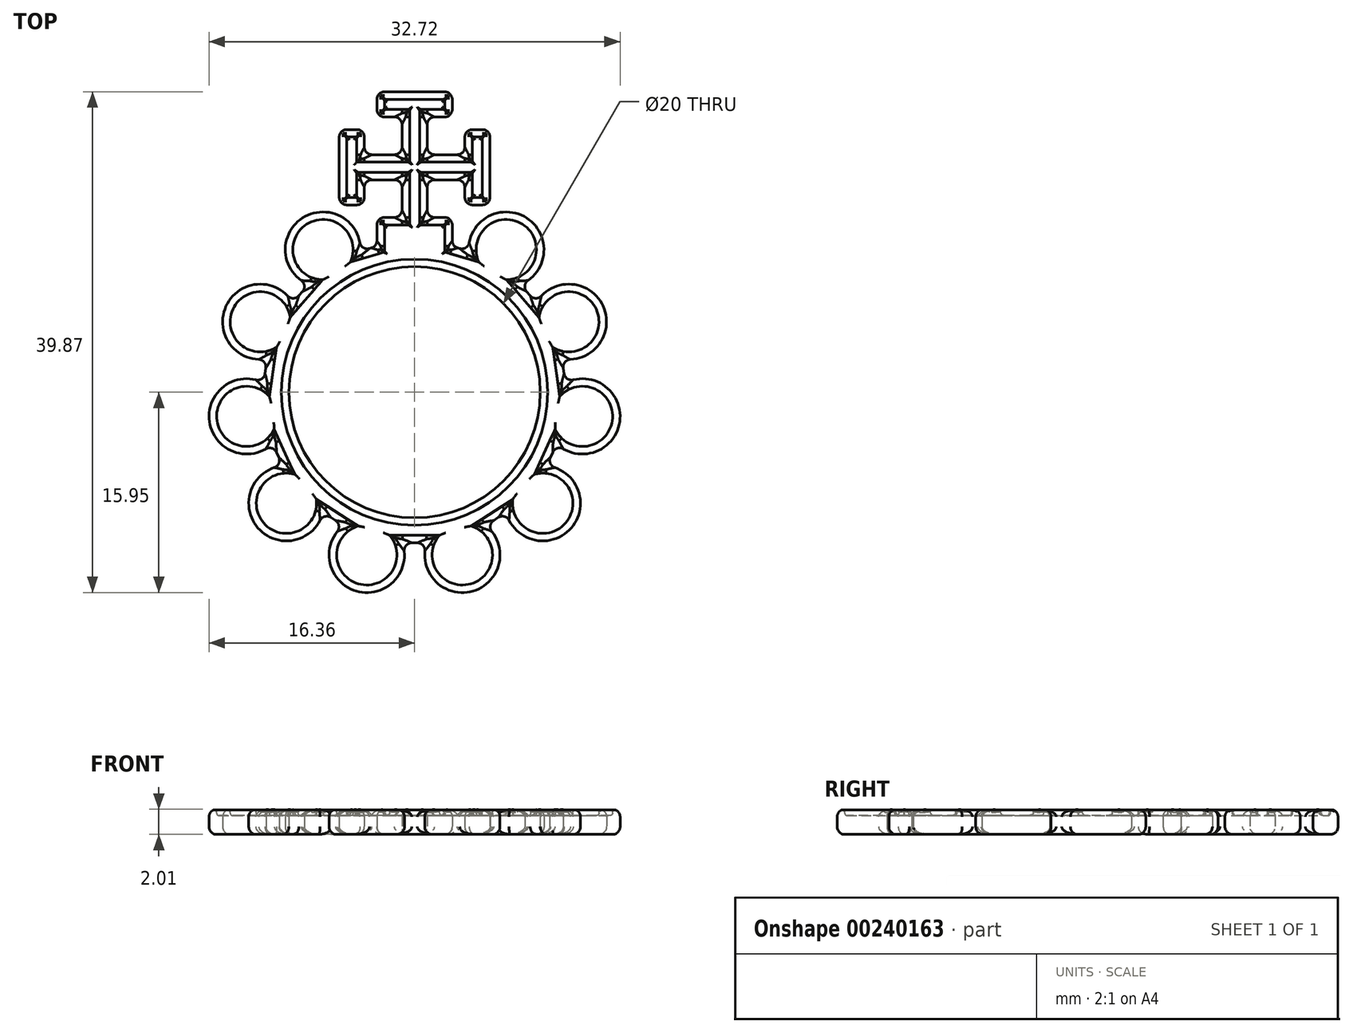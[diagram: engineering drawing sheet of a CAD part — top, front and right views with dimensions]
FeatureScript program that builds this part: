
annotation { "Feature Type Name" : "Feature", "Feature Type Description" : "" }
export const myFeature = defineFeature(function(context is Context, id is Id, definition is map)
    precondition{}
    {
        {
            var Q0;
            Q0=qCreatedBy(makeId("Top.planeOp"),FACE);
            var sketch = newSketch(context, id + "F0", { "sketchPlane" : qUnion([Q0])});
            skCircle(sketch, "E0", {"center": v(0, 0) * mm, "radius": 10 * mm});
            skLineSegment(sketch, "E1.0", {"start": v(3, 11.62) * mm, "end": v(4.3, 11.24) * mm});
            skLineSegment(sketch, "E1.1", {"start": v(8.43, 8.58) * mm, "end": v(9.7, 7.13) * mm});
            skLineSegment(sketch, "E1.2", {"start": v(11.73, 2.66) * mm, "end": v(12, 0.76) * mm});
            skLineSegment(sketch, "E1.3", {"start": v(11.3, -4.1) * mm, "end": v(10.51, -5.86) * mm});
            skLineSegment(sketch, "E1.4", {"start": v(7.3, -9.57) * mm, "end": v(5.68, -10.6) * mm});
            skLineSegment(sketch, "E1.5", {"start": v(0.96, -12) * mm, "end": v(-0.96, -12) * mm});
            skLineSegment(sketch, "E1.6", {"start": v(-5.68, -10.6) * mm, "end": v(-7.3, -9.57) * mm});
            skLineSegment(sketch, "E1.7", {"start": v(-10.51, -5.86) * mm, "end": v(-11.3, -4.1) * mm});
            skLineSegment(sketch, "E1.8", {"start": v(-12, 0.76) * mm, "end": v(-11.73, 2.66) * mm});
            skLineSegment(sketch, "E1.9", {"start": v(-9.7, 7.13) * mm, "end": v(-8.43, 8.58) * mm});
            skLineSegment(sketch, "E1.10", {"start": v(-4.3, 11.24) * mm, "end": v(-3, 11.62) * mm});
            skArc(sketch, "E2", {"start": v(8.43, 8.58) * mm, "mid": v(8.92, 13.88) * mm, "end": v(4.3, 11.24) * mm});
            skArc(sketch, "E3.2.0", {"start": v(-4.3, 11.24) * mm, "mid": v(-8.92, 13.88) * mm, "end": v(-8.43, 8.58) * mm});
            skArc(sketch, "E3.3.0", {"start": v(-9.7, 7.13) * mm, "mid": v(-15, 6.85) * mm, "end": v(-11.73, 2.66) * mm});
            skArc(sketch, "E3.4.0", {"start": v(-12, 0.76) * mm, "mid": v(-16.33, -2.35) * mm, "end": v(-11.3, -4.1) * mm});
            skArc(sketch, "E3.5.0", {"start": v(-10.51, -5.86) * mm, "mid": v(-12.47, -10.8) * mm, "end": v(-7.3, -9.57) * mm});
            skArc(sketch, "E3.6.0", {"start": v(-5.68, -10.6) * mm, "mid": v(-4.65, -15.83) * mm, "end": v(-0.96, -12) * mm});
            skArc(sketch, "E3.7.0", {"start": v(0.96, -12) * mm, "mid": v(4.65, -15.83) * mm, "end": v(5.68, -10.6) * mm});
            skArc(sketch, "E3.8.0", {"start": v(7.3, -9.57) * mm, "mid": v(12.47, -10.8) * mm, "end": v(10.51, -5.86) * mm});
            skArc(sketch, "E3.9.0", {"start": v(11.3, -4.1) * mm, "mid": v(16.33, -2.35) * mm, "end": v(12, 0.76) * mm});
            skArc(sketch, "E3.10.0", {"start": v(11.73, 2.66) * mm, "mid": v(15, 6.85) * mm, "end": v(9.7, 7.13) * mm});
            skLineSegment(sketch, "E4", {"start": v(3, 11.62) * mm, "end": v(3, 13.92) * mm});
            skLineSegment(sketch, "E5", {"start": v(3, 13.92) * mm, "end": v(1, 13.92) * mm});
            skLineSegment(sketch, "E6", {"start": v(1, 13.92) * mm, "end": v(1, 16.92) * mm});
            skLineSegment(sketch, "E7", {"start": v(1, 16.92) * mm, "end": v(4, 16.92) * mm});
            skLineSegment(sketch, "E8", {"start": v(4, 16.92) * mm, "end": v(4, 14.92) * mm});
            skLineSegment(sketch, "E9", {"start": v(4, 14.92) * mm, "end": v(6, 14.92) * mm});
            skLineSegment(sketch, "E10", {"start": v(6, 14.92) * mm, "end": v(6, 20.92) * mm});
            skLineSegment(sketch, "E11", {"start": v(6, 20.92) * mm, "end": v(4, 20.92) * mm});
            skLineSegment(sketch, "E12", {"start": v(4, 20.92) * mm, "end": v(4, 18.92) * mm});
            skLineSegment(sketch, "E13", {"start": v(4, 18.92) * mm, "end": v(1, 18.92) * mm});
            skLineSegment(sketch, "E14", {"start": v(1, 18.92) * mm, "end": v(1, 21.92) * mm});
            skLineSegment(sketch, "E15", {"start": v(1, 21.92) * mm, "end": v(3, 21.92) * mm});
            skLineSegment(sketch, "E16", {"start": v(3, 21.92) * mm, "end": v(3, 23.92) * mm});
            skLineSegment(sketch, "E17", {"start": v(3, 23.92) * mm, "end": v(0, 23.92) * mm});
            skLineSegment(sketch, "E18.MirrorCS", {"start": v(-3, 23.92) * mm, "end": v(0, 23.92) * mm});
            skLineSegment(sketch, "E19.MirrorCS", {"start": v(-3, 21.92) * mm, "end": v(-3, 23.92) * mm});
            skLineSegment(sketch, "E20.MirrorCS", {"start": v(-1, 21.92) * mm, "end": v(-3, 21.92) * mm});
            skLineSegment(sketch, "E21.MirrorCS", {"start": v(-1, 18.92) * mm, "end": v(-1, 21.92) * mm});
            skLineSegment(sketch, "E22.MirrorCS", {"start": v(-4, 18.92) * mm, "end": v(-1, 18.92) * mm});
            skLineSegment(sketch, "E23.MirrorCS", {"start": v(-4, 20.92) * mm, "end": v(-4, 18.92) * mm});
            skLineSegment(sketch, "E24.MirrorCS", {"start": v(-6, 20.92) * mm, "end": v(-4, 20.92) * mm});
            skLineSegment(sketch, "E25.MirrorCS", {"start": v(-6, 14.92) * mm, "end": v(-6, 20.92) * mm});
            skLineSegment(sketch, "E26.MirrorCS", {"start": v(-1, 16.92) * mm, "end": v(-4, 16.92) * mm});
            skLineSegment(sketch, "E27.MirrorCS", {"start": v(-4, 16.92) * mm, "end": v(-4, 14.92) * mm});
            skLineSegment(sketch, "E28.MirrorCS", {"start": v(-1, 13.92) * mm, "end": v(-1, 16.92) * mm});
            skLineSegment(sketch, "E29.MirrorCS", {"start": v(-4, 14.92) * mm, "end": v(-6, 14.92) * mm});
            skLineSegment(sketch, "E30.MirrorCS", {"start": v(-3, 13.92) * mm, "end": v(-1, 13.92) * mm});
            skLineSegment(sketch, "E31.MirrorCS", {"start": v(-3, 11.62) * mm, "end": v(-3, 13.92) * mm});
            skPoint(sketch, "E32.orphan", {"position": v(-3, 11.92) * mm});
            skPoint(sketch, "E33.MirrorCS.start.orphan", {"position": v(0, 12.5) * mm});
            skPoint(sketch, "E34.end.orphan", {"position": v(3, 11.92) * mm});
            skSolve(sketch);
        }
        {
            var Q0;
            Q0=qSketchRegion(id+"F0",true);
            extrude(context, id + "F1", {"entities" : qUnion([Q0]), "depth" : 2 * mm});
        }
        {
            var Q0;
            Q0=makeQuery(id+"F1.opExtrude","CAP_EDGE",EDGE,{"disambiguationData":[OSD([sQuery(id+"F0.wireOp",EDGE,"E0")])],"isStart":false});
            var Q1;
            Q1=makeQuery(id+"F1.opExtrude","CAP_EDGE",EDGE,{"disambiguationData":[OSD([sQuery(id+"F0.wireOp",EDGE,"E0")])],"isStart":true});
            var Q2;
            Q2=makeQuery(id+"F1.opExtrude","CAP_EDGE",EDGE,{"disambiguationData":[OSD([sQuery(id+"F0.wireOp",EDGE,"E2")])],"isStart":false});
            var Q3;
            Q3=makeQuery(id+"F1.opExtrude","CAP_EDGE",EDGE,{"disambiguationData":[OSD([sQuery(id+"F0.wireOp",EDGE,"E3.10.0")])],"isStart":false});
            var Q4;
            Q4=makeQuery(id+"F1.opExtrude","CAP_EDGE",EDGE,{"disambiguationData":[OSD([sQuery(id+"F0.wireOp",EDGE,"E1.1")])],"isStart":false});
            var Q5;
            Q5=makeQuery(id+"F1.opExtrude","CAP_EDGE",EDGE,{"disambiguationData":[OSD([sQuery(id+"F0.wireOp",EDGE,"E1.2")])],"isStart":false});
            var Q6;
            Q6=makeQuery(id+"F1.opExtrude","CAP_EDGE",EDGE,{"disambiguationData":[OSD([sQuery(id+"F0.wireOp",EDGE,"E3.9.0")])],"isStart":false});
            var Q7;
            Q7=makeQuery(id+"F1.opExtrude","CAP_EDGE",EDGE,{"disambiguationData":[OSD([sQuery(id+"F0.wireOp",EDGE,"E3.8.0")])],"isStart":false});
            var Q8;
            Q8=makeQuery(id+"F1.opExtrude","CAP_EDGE",EDGE,{"disambiguationData":[OSD([sQuery(id+"F0.wireOp",EDGE,"E1.3")])],"isStart":false});
            var Q9;
            Q9=makeQuery(id+"F1.opExtrude","CAP_EDGE",EDGE,{"disambiguationData":[OSD([sQuery(id+"F0.wireOp",EDGE,"E3.7.0")])],"isStart":false});
            var Q10;
            Q10=makeQuery(id+"F1.opExtrude","CAP_EDGE",EDGE,{"disambiguationData":[OSD([sQuery(id+"F0.wireOp",EDGE,"E1.4")])],"isStart":false});
            var Q11;
            Q11=makeQuery(id+"F1.opExtrude","CAP_EDGE",EDGE,{"disambiguationData":[OSD([sQuery(id+"F0.wireOp",EDGE,"E3.6.0")])],"isStart":false});
            var Q12;
            Q12=makeQuery(id+"F1.opExtrude","CAP_EDGE",EDGE,{"disambiguationData":[OSD([sQuery(id+"F0.wireOp",EDGE,"E1.5")])],"isStart":false});
            var Q13;
            Q13=makeQuery(id+"F1.opExtrude","CAP_EDGE",EDGE,{"disambiguationData":[OSD([sQuery(id+"F0.wireOp",EDGE,"E3.5.0")])],"isStart":false});
            var Q14;
            Q14=makeQuery(id+"F1.opExtrude","CAP_EDGE",EDGE,{"disambiguationData":[OSD([sQuery(id+"F0.wireOp",EDGE,"E1.6")])],"isStart":false});
            var Q15;
            Q15=makeQuery(id+"F1.opExtrude","CAP_EDGE",EDGE,{"disambiguationData":[OSD([sQuery(id+"F0.wireOp",EDGE,"E3.4.0")])],"isStart":false});
            var Q16;
            Q16=makeQuery(id+"F1.opExtrude","CAP_EDGE",EDGE,{"disambiguationData":[OSD([sQuery(id+"F0.wireOp",EDGE,"E3.3.0")])],"isStart":false});
            var Q17;
            Q17=makeQuery(id+"F1.opExtrude","CAP_EDGE",EDGE,{"disambiguationData":[OSD([sQuery(id+"F0.wireOp",EDGE,"E3.2.0")])],"isStart":false});
            var Q18;
            Q18=makeQuery(id+"F1.opExtrude","CAP_EDGE",EDGE,{"disambiguationData":[OSD([sQuery(id+"F0.wireOp",EDGE,"E1.9")])],"isStart":false});
            var Q19;
            Q19=makeQuery(id+"F1.opExtrude","CAP_EDGE",EDGE,{"disambiguationData":[OSD([sQuery(id+"F0.wireOp",EDGE,"E1.8")])],"isStart":false});
            var Q20;
            Q20=makeQuery(id+"F1.opExtrude","CAP_EDGE",EDGE,{"disambiguationData":[OSD([sQuery(id+"F0.wireOp",EDGE,"E1.7")])],"isStart":false});
            var Q21;
            Q21=makeQuery(id+"F1.opExtrude","CAP_EDGE",EDGE,{"disambiguationData":[OSD([sQuery(id+"F0.wireOp",EDGE,"E1.10")])],"isStart":false});
            var Q22;
            Q22=makeQuery(id+"F1.opExtrude","CAP_EDGE",EDGE,{"disambiguationData":[OSD([sQuery(id+"F0.wireOp",EDGE,"E31.MirrorCS")])],"isStart":false});
            var Q23;
            Q23=makeQuery(id+"F1.opExtrude","CAP_EDGE",EDGE,{"disambiguationData":[OSD([sQuery(id+"F0.wireOp",EDGE,"E30.MirrorCS")])],"isStart":false});
            var Q24;
            Q24=makeQuery(id+"F1.opExtrude","CAP_EDGE",EDGE,{"disambiguationData":[OSD([sQuery(id+"F0.wireOp",EDGE,"E28.MirrorCS")])],"isStart":false});
            var Q25;
            Q25=makeQuery(id+"F1.opExtrude","CAP_EDGE",EDGE,{"disambiguationData":[OSD([sQuery(id+"F0.wireOp",EDGE,"E26.MirrorCS")])],"isStart":false});
            var Q26;
            Q26=makeQuery(id+"F1.opExtrude","CAP_EDGE",EDGE,{"disambiguationData":[OSD([sQuery(id+"F0.wireOp",EDGE,"E26.MirrorCS")])],"isStart":true});
            var Q27;
            Q27=makeQuery(id+"F1.opExtrude","CAP_EDGE",EDGE,{"disambiguationData":[OSD([sQuery(id+"F0.wireOp",EDGE,"E29.MirrorCS")])],"isStart":false});
            var Q28;
            Q28=makeQuery(id+"F1.opExtrude","CAP_EDGE",EDGE,{"disambiguationData":[OSD([sQuery(id+"F0.wireOp",EDGE,"E25.MirrorCS")])],"isStart":false});
            var Q29;
            Q29=makeQuery(id+"F1.opExtrude","CAP_EDGE",EDGE,{"disambiguationData":[OSD([sQuery(id+"F0.wireOp",EDGE,"E24.MirrorCS")])],"isStart":false});
            var Q30;
            Q30=makeQuery(id+"F1.opExtrude","CAP_EDGE",EDGE,{"disambiguationData":[OSD([sQuery(id+"F0.wireOp",EDGE,"E22.MirrorCS")])],"isStart":false});
            var Q31;
            Q31=makeQuery(id+"F1.opExtrude","CAP_EDGE",EDGE,{"disambiguationData":[OSD([sQuery(id+"F0.wireOp",EDGE,"E21.MirrorCS")])],"isStart":false});
            var Q32;
            Q32=makeQuery(id+"F1.opExtrude","CAP_EDGE",EDGE,{"disambiguationData":[OSD([sQuery(id+"F0.wireOp",EDGE,"E20.MirrorCS")])],"isStart":false});
            var Q33;
            Q33=makeQuery(id+"F1.opExtrude","CAP_EDGE",EDGE,{"disambiguationData":[OSD([sQuery(id+"F0.wireOp",EDGE,"E19.MirrorCS")])],"isStart":false});
            var Q34;
            Q34=makeQuery(id+"F1.opExtrude","CAP_EDGE",EDGE,{"disambiguationData":[OSD([sQuery(id+"F0.wireOp",EDGE,"E17"),sQuery(id+"F0.wireOp",EDGE,"E18.MirrorCS")])],"isStart":false});
            var Q35;
            Q35=makeQuery(id+"F1.opExtrude","CAP_EDGE",EDGE,{"disambiguationData":[OSD([sQuery(id+"F0.wireOp",EDGE,"E16")])],"isStart":false});
            var Q36;
            Q36=makeQuery(id+"F1.opExtrude","CAP_EDGE",EDGE,{"disambiguationData":[OSD([sQuery(id+"F0.wireOp",EDGE,"E15")])],"isStart":false});
            var Q37;
            Q37=makeQuery(id+"F1.opExtrude","CAP_EDGE",EDGE,{"disambiguationData":[OSD([sQuery(id+"F0.wireOp",EDGE,"E14")])],"isStart":false});
            var Q38;
            Q38=makeQuery(id+"F1.opExtrude","CAP_EDGE",EDGE,{"disambiguationData":[OSD([sQuery(id+"F0.wireOp",EDGE,"E13")])],"isStart":false});
            var Q39;
            Q39=makeQuery(id+"F1.opExtrude","CAP_EDGE",EDGE,{"disambiguationData":[OSD([sQuery(id+"F0.wireOp",EDGE,"E11")])],"isStart":false});
            var Q40;
            Q40=makeQuery(id+"F1.opExtrude","CAP_EDGE",EDGE,{"disambiguationData":[OSD([sQuery(id+"F0.wireOp",EDGE,"E12")])],"isStart":false});
            var Q41;
            Q41=makeQuery(id+"F1.opExtrude","CAP_EDGE",EDGE,{"disambiguationData":[OSD([sQuery(id+"F0.wireOp",EDGE,"E10")])],"isStart":false});
            var Q42;
            Q42=makeQuery(id+"F1.opExtrude","CAP_EDGE",EDGE,{"disambiguationData":[OSD([sQuery(id+"F0.wireOp",EDGE,"E9")])],"isStart":false});
            var Q43;
            Q43=makeQuery(id+"F1.opExtrude","CAP_EDGE",EDGE,{"disambiguationData":[OSD([sQuery(id+"F0.wireOp",EDGE,"E8")])],"isStart":false});
            var Q44;
            Q44=makeQuery(id+"F1.opExtrude","CAP_EDGE",EDGE,{"disambiguationData":[OSD([sQuery(id+"F0.wireOp",EDGE,"E7")])],"isStart":false});
            var Q45;
            Q45=makeQuery(id+"F1.opExtrude","CAP_EDGE",EDGE,{"disambiguationData":[OSD([sQuery(id+"F0.wireOp",EDGE,"E6")])],"isStart":false});
            var Q46;
            Q46=makeQuery(id+"F1.opExtrude","CAP_EDGE",EDGE,{"disambiguationData":[OSD([sQuery(id+"F0.wireOp",EDGE,"E5")])],"isStart":false});
            var Q47;
            Q47=makeQuery(id+"F1.opExtrude","CAP_EDGE",EDGE,{"disambiguationData":[OSD([sQuery(id+"F0.wireOp",EDGE,"E4")])],"isStart":false});
            var Q48;
            Q48=makeQuery(id+"F1.opExtrude","CAP_EDGE",EDGE,{"disambiguationData":[OSD([sQuery(id+"F0.wireOp",EDGE,"E1.0")])],"isStart":false});
            var Q49;
            Q49=makeQuery(id+"F1.opExtrude","CAP_EDGE",EDGE,{"disambiguationData":[OSD([sQuery(id+"F0.wireOp",EDGE,"E3.5.0")])],"isStart":true});
            var Q50;
            Q50=makeQuery(id+"F1.opExtrude","CAP_EDGE",EDGE,{"disambiguationData":[OSD([sQuery(id+"F0.wireOp",EDGE,"E1.6")])],"isStart":true});
            var Q51;
            Q51=makeQuery(id+"F1.opExtrude","CAP_EDGE",EDGE,{"disambiguationData":[OSD([sQuery(id+"F0.wireOp",EDGE,"E3.6.0")])],"isStart":true});
            var Q52;
            Q52=makeQuery(id+"F1.opExtrude","CAP_EDGE",EDGE,{"disambiguationData":[OSD([sQuery(id+"F0.wireOp",EDGE,"E1.5")])],"isStart":true});
            var Q53;
            Q53=makeQuery(id+"F1.opExtrude","CAP_EDGE",EDGE,{"disambiguationData":[OSD([sQuery(id+"F0.wireOp",EDGE,"E3.7.0")])],"isStart":true});
            var Q54;
            Q54=makeQuery(id+"F1.opExtrude","CAP_EDGE",EDGE,{"disambiguationData":[OSD([sQuery(id+"F0.wireOp",EDGE,"E3.4.0")])],"isStart":true});
            var Q55;
            Q55=makeQuery(id+"F1.opExtrude","CAP_EDGE",EDGE,{"disambiguationData":[OSD([sQuery(id+"F0.wireOp",EDGE,"E1.7")])],"isStart":true});
            var Q56;
            Q56=makeQuery(id+"F1.opExtrude","CAP_EDGE",EDGE,{"disambiguationData":[OSD([sQuery(id+"F0.wireOp",EDGE,"E3.3.0")])],"isStart":true});
            var Q57;
            Q57=makeQuery(id+"F1.opExtrude","CAP_EDGE",EDGE,{"disambiguationData":[OSD([sQuery(id+"F0.wireOp",EDGE,"E1.8")])],"isStart":true});
            var Q58;
            Q58=makeQuery(id+"F1.opExtrude","CAP_EDGE",EDGE,{"disambiguationData":[OSD([sQuery(id+"F0.wireOp",EDGE,"E3.2.0")])],"isStart":true});
            var Q59;
            Q59=makeQuery(id+"F1.opExtrude","CAP_EDGE",EDGE,{"disambiguationData":[OSD([sQuery(id+"F0.wireOp",EDGE,"E1.9")])],"isStart":true});
            var Q60;
            Q60=makeQuery(id+"F1.opExtrude","CAP_EDGE",EDGE,{"disambiguationData":[OSD([sQuery(id+"F0.wireOp",EDGE,"E1.10")])],"isStart":true});
            var Q61;
            Q61=makeQuery(id+"F1.opExtrude","CAP_EDGE",EDGE,{"disambiguationData":[OSD([sQuery(id+"F0.wireOp",EDGE,"E31.MirrorCS")])],"isStart":true});
            var Q62;
            Q62=makeQuery(id+"F1.opExtrude","CAP_EDGE",EDGE,{"disambiguationData":[OSD([sQuery(id+"F0.wireOp",EDGE,"E25.MirrorCS")])],"isStart":true});
            var Q63;
            Q63=makeQuery(id+"F1.opExtrude","CAP_EDGE",EDGE,{"disambiguationData":[OSD([sQuery(id+"F0.wireOp",EDGE,"E29.MirrorCS")])],"isStart":true});
            var Q64;
            Q64=makeQuery(id+"F1.opExtrude","CAP_EDGE",EDGE,{"disambiguationData":[OSD([sQuery(id+"F0.wireOp",EDGE,"E30.MirrorCS")])],"isStart":true});
            var Q65;
            Q65=makeQuery(id+"F1.opExtrude","CAP_EDGE",EDGE,{"disambiguationData":[OSD([sQuery(id+"F0.wireOp",EDGE,"E28.MirrorCS")])],"isStart":true});
            var Q66;
            Q66=makeQuery(id+"F1.opExtrude","CAP_EDGE",EDGE,{"disambiguationData":[OSD([sQuery(id+"F0.wireOp",EDGE,"E6")])],"isStart":true});
            var Q67;
            Q67=makeQuery(id+"F1.opExtrude","CAP_EDGE",EDGE,{"disambiguationData":[OSD([sQuery(id+"F0.wireOp",EDGE,"E5")])],"isStart":true});
            var Q68;
            Q68=makeQuery(id+"F1.opExtrude","CAP_EDGE",EDGE,{"disambiguationData":[OSD([sQuery(id+"F0.wireOp",EDGE,"E4")])],"isStart":true});
            var Q69;
            Q69=makeQuery(id+"F1.opExtrude","CAP_EDGE",EDGE,{"disambiguationData":[OSD([sQuery(id+"F0.wireOp",EDGE,"E1.0")])],"isStart":true});
            var Q70;
            Q70=makeQuery(id+"F1.opExtrude","CAP_EDGE",EDGE,{"disambiguationData":[OSD([sQuery(id+"F0.wireOp",EDGE,"E2")])],"isStart":true});
            var Q71;
            Q71=makeQuery(id+"F1.opExtrude","CAP_EDGE",EDGE,{"disambiguationData":[OSD([sQuery(id+"F0.wireOp",EDGE,"E7")])],"isStart":true});
            var Q72;
            Q72=makeQuery(id+"F1.opExtrude","CAP_EDGE",EDGE,{"disambiguationData":[OSD([sQuery(id+"F0.wireOp",EDGE,"E8")])],"isStart":true});
            var Q73;
            Q73=makeQuery(id+"F1.opExtrude","CAP_EDGE",EDGE,{"disambiguationData":[OSD([sQuery(id+"F0.wireOp",EDGE,"E9")])],"isStart":true});
            var Q74;
            Q74=makeQuery(id+"F1.opExtrude","CAP_EDGE",EDGE,{"disambiguationData":[OSD([sQuery(id+"F0.wireOp",EDGE,"E10")])],"isStart":true});
            var Q75;
            Q75=makeQuery(id+"F1.opExtrude","CAP_EDGE",EDGE,{"disambiguationData":[OSD([sQuery(id+"F0.wireOp",EDGE,"E11")])],"isStart":true});
            var Q76;
            Q76=makeQuery(id+"F1.opExtrude","CAP_EDGE",EDGE,{"disambiguationData":[OSD([sQuery(id+"F0.wireOp",EDGE,"E12")])],"isStart":true});
            var Q77;
            Q77=makeQuery(id+"F1.opExtrude","CAP_EDGE",EDGE,{"disambiguationData":[OSD([sQuery(id+"F0.wireOp",EDGE,"E13")])],"isStart":true});
            var Q78;
            Q78=makeQuery(id+"F1.opExtrude","CAP_EDGE",EDGE,{"disambiguationData":[OSD([sQuery(id+"F0.wireOp",EDGE,"E14")])],"isStart":true});
            var Q79;
            Q79=makeQuery(id+"F1.opExtrude","CAP_EDGE",EDGE,{"disambiguationData":[OSD([sQuery(id+"F0.wireOp",EDGE,"E15")])],"isStart":true});
            var Q80;
            Q80=makeQuery(id+"F1.opExtrude","CAP_EDGE",EDGE,{"disambiguationData":[OSD([sQuery(id+"F0.wireOp",EDGE,"E16")])],"isStart":true});
            var Q81;
            Q81=makeQuery(id+"F1.opExtrude","CAP_EDGE",EDGE,{"disambiguationData":[OSD([sQuery(id+"F0.wireOp",EDGE,"E17"),sQuery(id+"F0.wireOp",EDGE,"E18.MirrorCS")])],"isStart":true});
            var Q82;
            Q82=makeQuery(id+"F1.opExtrude","CAP_EDGE",EDGE,{"disambiguationData":[OSD([sQuery(id+"F0.wireOp",EDGE,"E19.MirrorCS")])],"isStart":true});
            var Q83;
            Q83=makeQuery(id+"F1.opExtrude","CAP_EDGE",EDGE,{"disambiguationData":[OSD([sQuery(id+"F0.wireOp",EDGE,"E20.MirrorCS")])],"isStart":true});
            var Q84;
            Q84=makeQuery(id+"F1.opExtrude","CAP_EDGE",EDGE,{"disambiguationData":[OSD([sQuery(id+"F0.wireOp",EDGE,"E21.MirrorCS")])],"isStart":true});
            var Q85;
            Q85=makeQuery(id+"F1.opExtrude","CAP_EDGE",EDGE,{"disambiguationData":[OSD([sQuery(id+"F0.wireOp",EDGE,"E22.MirrorCS")])],"isStart":true});
            var Q86;
            Q86=makeQuery(id+"F1.opExtrude","CAP_EDGE",EDGE,{"disambiguationData":[OSD([sQuery(id+"F0.wireOp",EDGE,"E23.MirrorCS")])],"isStart":true});
            var Q87;
            Q87=makeQuery(id+"F1.opExtrude","CAP_EDGE",EDGE,{"disambiguationData":[OSD([sQuery(id+"F0.wireOp",EDGE,"E24.MirrorCS")])],"isStart":true});
            var Q88;
            Q88=makeQuery(id+"F1.opExtrude","CAP_EDGE",EDGE,{"disambiguationData":[OSD([sQuery(id+"F0.wireOp",EDGE,"E3.10.0")])],"isStart":true});
            var Q89;
            Q89=makeQuery(id+"F1.opExtrude","CAP_EDGE",EDGE,{"disambiguationData":[OSD([sQuery(id+"F0.wireOp",EDGE,"E1.1")])],"isStart":true});
            var Q90;
            Q90=makeQuery(id+"F1.opExtrude","CAP_EDGE",EDGE,{"disambiguationData":[OSD([sQuery(id+"F0.wireOp",EDGE,"E1.2")])],"isStart":true});
            var Q91;
            Q91=makeQuery(id+"F1.opExtrude","CAP_EDGE",EDGE,{"disambiguationData":[OSD([sQuery(id+"F0.wireOp",EDGE,"E3.9.0")])],"isStart":true});
            var Q92;
            Q92=makeQuery(id+"F1.opExtrude","CAP_EDGE",EDGE,{"disambiguationData":[OSD([sQuery(id+"F0.wireOp",EDGE,"E1.3")])],"isStart":true});
            var Q93;
            Q93=makeQuery(id+"F1.opExtrude","CAP_EDGE",EDGE,{"disambiguationData":[OSD([sQuery(id+"F0.wireOp",EDGE,"E3.8.0")])],"isStart":true});
            var Q94;
            Q94=makeQuery(id+"F1.opExtrude","CAP_EDGE",EDGE,{"disambiguationData":[OSD([sQuery(id+"F0.wireOp",EDGE,"E1.4")])],"isStart":true});
            var Q95;
            Q95=makeQuery(id+"F1.opExtrude","CAP_EDGE",EDGE,{"disambiguationData":[OSD([sQuery(id+"F0.wireOp",EDGE,"E23.MirrorCS")])],"isStart":false});
            var Q96;
            Q96=makeQuery(id+"F1.opExtrude","CAP_EDGE",EDGE,{"disambiguationData":[OSD([sQuery(id+"F0.wireOp",EDGE,"E27.MirrorCS")])],"isStart":false});
            var Q97;
            Q97=makeQuery(id+"F1.opExtrude","CAP_EDGE",EDGE,{"disambiguationData":[OSD([sQuery(id+"F0.wireOp",EDGE,"E27.MirrorCS")])],"isStart":true});
            fillet(context, id + "F2", {"entities" : qUnion([Q0, Q1, Q2, Q3, Q4, Q5, Q6, Q7, Q8, Q9, Q10, Q11, Q12, Q13, Q14, Q15, Q16, Q17, Q18, Q19, Q20, Q21, Q22, Q23, Q24, Q25, Q26, Q27, Q28, Q29, Q30, Q31, Q32, Q33, Q34, Q35, Q36, Q37, Q38, Q39, Q40, Q41, Q42, Q43, Q44, Q45, Q46, Q47, Q48, Q49, Q50, Q51, Q52, Q53, Q54, Q55, Q56, Q57, Q58, Q59, Q60, Q61, Q62, Q63, Q64, Q65, Q66, Q67, Q68, Q69, Q70, Q71, Q72, Q73, Q74, Q75, Q76, Q77, Q78, Q79, Q80, Q81, Q82, Q83, Q84, Q85, Q86, Q87, Q88, Q89, Q90, Q91, Q92, Q93, Q94, Q95, Q96, Q97]), "radius" : 0.6 * mm, "tangentPropagation" : true, "allowEdgeOverflow" : false});
        }
        {
            var Q0;
            Q0=makeQuery(id+"F1.opExtrude","SWEPT_EDGE",EDGE,{"disambiguationData":[OSD([sQuery(id+"F0.wireOp",EDGE,"E1.10"),sQuery(id+"F0.wireOp",EDGE,"E31.MirrorCS")])]});
            var Q1;
            Q1=makeQuery(id+"F1.opExtrude","SWEPT_EDGE",EDGE,{"disambiguationData":[OSD([sQuery(id+"F0.wireOp",EDGE,"E1.10"),sQuery(id+"F0.wireOp",EDGE,"E3.2.0")])]});
            var Q2;
            Q2=makeQuery(id+"F1.opExtrude","SWEPT_EDGE",EDGE,{"disambiguationData":[OSD([sQuery(id+"F0.wireOp",EDGE,"E1.9"),sQuery(id+"F0.wireOp",EDGE,"E3.2.0")])]});
            var Q3;
            Q3=makeQuery(id+"F1.opExtrude","SWEPT_EDGE",EDGE,{"disambiguationData":[OSD([sQuery(id+"F0.wireOp",EDGE,"E1.9"),sQuery(id+"F0.wireOp",EDGE,"E3.3.0")])]});
            var Q4;
            Q4=makeQuery(id+"F1.opExtrude","SWEPT_EDGE",EDGE,{"disambiguationData":[OSD([sQuery(id+"F0.wireOp",EDGE,"E1.8"),sQuery(id+"F0.wireOp",EDGE,"E3.3.0")])]});
            var Q5;
            Q5=makeQuery(id+"F1.opExtrude","SWEPT_EDGE",EDGE,{"disambiguationData":[OSD([sQuery(id+"F0.wireOp",EDGE,"E1.8"),sQuery(id+"F0.wireOp",EDGE,"E3.4.0")])]});
            var Q6;
            Q6=makeQuery(id+"F1.opExtrude","SWEPT_EDGE",EDGE,{"disambiguationData":[OSD([sQuery(id+"F0.wireOp",EDGE,"E1.7"),sQuery(id+"F0.wireOp",EDGE,"E3.4.0")])]});
            var Q7;
            Q7=makeQuery(id+"F1.opExtrude","SWEPT_EDGE",EDGE,{"disambiguationData":[OSD([sQuery(id+"F0.wireOp",EDGE,"E1.7"),sQuery(id+"F0.wireOp",EDGE,"E3.5.0")])]});
            var Q8;
            Q8=makeQuery(id+"F1.opExtrude","SWEPT_EDGE",EDGE,{"disambiguationData":[OSD([sQuery(id+"F0.wireOp",EDGE,"E1.6"),sQuery(id+"F0.wireOp",EDGE,"E3.5.0")])]});
            var Q9;
            Q9=makeQuery(id+"F1.opExtrude","SWEPT_EDGE",EDGE,{"disambiguationData":[OSD([sQuery(id+"F0.wireOp",EDGE,"E1.6"),sQuery(id+"F0.wireOp",EDGE,"E3.6.0")])]});
            var Q10;
            Q10=makeQuery(id+"F1.opExtrude","SWEPT_EDGE",EDGE,{"disambiguationData":[OSD([sQuery(id+"F0.wireOp",EDGE,"E1.5"),sQuery(id+"F0.wireOp",EDGE,"E3.7.0")])]});
            var Q11;
            Q11=makeQuery(id+"F1.opExtrude","SWEPT_EDGE",EDGE,{"disambiguationData":[OSD([sQuery(id+"F0.wireOp",EDGE,"E1.5"),sQuery(id+"F0.wireOp",EDGE,"E3.6.0")])]});
            var Q12;
            Q12=makeQuery(id+"F1.opExtrude","SWEPT_EDGE",EDGE,{"disambiguationData":[OSD([sQuery(id+"F0.wireOp",EDGE,"E1.4"),sQuery(id+"F0.wireOp",EDGE,"E3.7.0")])]});
            var Q13;
            Q13=makeQuery(id+"F1.opExtrude","SWEPT_EDGE",EDGE,{"disambiguationData":[OSD([sQuery(id+"F0.wireOp",EDGE,"E1.4"),sQuery(id+"F0.wireOp",EDGE,"E3.8.0")])]});
            var Q14;
            Q14=makeQuery(id+"F1.opExtrude","SWEPT_EDGE",EDGE,{"disambiguationData":[OSD([sQuery(id+"F0.wireOp",EDGE,"E1.3"),sQuery(id+"F0.wireOp",EDGE,"E3.9.0")])]});
            var Q15;
            Q15=makeQuery(id+"F1.opExtrude","SWEPT_EDGE",EDGE,{"disambiguationData":[OSD([sQuery(id+"F0.wireOp",EDGE,"E1.3"),sQuery(id+"F0.wireOp",EDGE,"E3.8.0")])]});
            var Q16;
            Q16=makeQuery(id+"F1.opExtrude","SWEPT_EDGE",EDGE,{"disambiguationData":[OSD([sQuery(id+"F0.wireOp",EDGE,"E1.2"),sQuery(id+"F0.wireOp",EDGE,"E3.10.0")])]});
            var Q17;
            Q17=makeQuery(id+"F1.opExtrude","SWEPT_EDGE",EDGE,{"disambiguationData":[OSD([sQuery(id+"F0.wireOp",EDGE,"E1.2"),sQuery(id+"F0.wireOp",EDGE,"E3.9.0")])]});
            var Q18;
            Q18=makeQuery(id+"F1.opExtrude","SWEPT_EDGE",EDGE,{"disambiguationData":[OSD([sQuery(id+"F0.wireOp",EDGE,"E1.1"),sQuery(id+"F0.wireOp",EDGE,"E2")])]});
            var Q19;
            Q19=makeQuery(id+"F1.opExtrude","SWEPT_EDGE",EDGE,{"disambiguationData":[OSD([sQuery(id+"F0.wireOp",EDGE,"E1.1"),sQuery(id+"F0.wireOp",EDGE,"E3.10.0")])]});
            var Q20;
            Q20=makeQuery(id+"F1.opExtrude","SWEPT_EDGE",EDGE,{"disambiguationData":[OSD([sQuery(id+"F0.wireOp",EDGE,"E1.0"),sQuery(id+"F0.wireOp",EDGE,"E4")])]});
            var Q21;
            Q21=makeQuery(id+"F1.opExtrude","SWEPT_EDGE",EDGE,{"disambiguationData":[OSD([sQuery(id+"F0.wireOp",EDGE,"E1.0"),sQuery(id+"F0.wireOp",EDGE,"E2")])]});
            fillet(context, id + "F3", {"entities" : qUnion([Q0, Q1, Q2, Q3, Q4, Q5, Q6, Q7, Q8, Q9, Q10, Q11, Q12, Q13, Q14, Q15, Q16, Q17, Q18, Q19, Q20, Q21]), "radius" : 0.6 * mm, "tangentPropagation" : true, "allowEdgeOverflow" : false});
        }
        {
            var Q0;
            Q0=makeQuery(id+"F1.opExtrude","SWEPT_EDGE",EDGE,{"disambiguationData":[OSD([sQuery(id+"F0.wireOp",EDGE,"E4"),sQuery(id+"F0.wireOp",EDGE,"E5")])]});
            var Q1;
            Q1=makeQuery(id+"F1.opExtrude","SWEPT_EDGE",EDGE,{"disambiguationData":[OSD([sQuery(id+"F0.wireOp",EDGE,"E5"),sQuery(id+"F0.wireOp",EDGE,"E6")])]});
            var Q2;
            Q2=makeQuery(id+"F1.opExtrude","SWEPT_EDGE",EDGE,{"disambiguationData":[OSD([sQuery(id+"F0.wireOp",EDGE,"E6"),sQuery(id+"F0.wireOp",EDGE,"E7")])]});
            var Q3;
            Q3=makeQuery(id+"F1.opExtrude","SWEPT_EDGE",EDGE,{"disambiguationData":[OSD([sQuery(id+"F0.wireOp",EDGE,"E7"),sQuery(id+"F0.wireOp",EDGE,"E8")])]});
            var Q4;
            Q4=makeQuery(id+"F1.opExtrude","SWEPT_EDGE",EDGE,{"disambiguationData":[OSD([sQuery(id+"F0.wireOp",EDGE,"E8"),sQuery(id+"F0.wireOp",EDGE,"E9")])]});
            var Q5;
            Q5=makeQuery(id+"F1.opExtrude","SWEPT_EDGE",EDGE,{"disambiguationData":[OSD([sQuery(id+"F0.wireOp",EDGE,"E9"),sQuery(id+"F0.wireOp",EDGE,"E10")])]});
            var Q6;
            Q6=makeQuery(id+"F1.opExtrude","SWEPT_EDGE",EDGE,{"disambiguationData":[OSD([sQuery(id+"F0.wireOp",EDGE,"E10"),sQuery(id+"F0.wireOp",EDGE,"E11")])]});
            var Q7;
            Q7=makeQuery(id+"F1.opExtrude","SWEPT_EDGE",EDGE,{"disambiguationData":[OSD([sQuery(id+"F0.wireOp",EDGE,"E11"),sQuery(id+"F0.wireOp",EDGE,"E12")])]});
            var Q8;
            Q8=makeQuery(id+"F1.opExtrude","SWEPT_EDGE",EDGE,{"disambiguationData":[OSD([sQuery(id+"F0.wireOp",EDGE,"E12"),sQuery(id+"F0.wireOp",EDGE,"E13")])]});
            var Q9;
            Q9=makeQuery(id+"F1.opExtrude","SWEPT_EDGE",EDGE,{"disambiguationData":[OSD([sQuery(id+"F0.wireOp",EDGE,"E13"),sQuery(id+"F0.wireOp",EDGE,"E14")])]});
            var Q10;
            Q10=makeQuery(id+"F1.opExtrude","SWEPT_EDGE",EDGE,{"disambiguationData":[OSD([sQuery(id+"F0.wireOp",EDGE,"E14"),sQuery(id+"F0.wireOp",EDGE,"E15")])]});
            var Q11;
            Q11=makeQuery(id+"F1.opExtrude","SWEPT_EDGE",EDGE,{"disambiguationData":[OSD([sQuery(id+"F0.wireOp",EDGE,"E15"),sQuery(id+"F0.wireOp",EDGE,"E16")])]});
            var Q12;
            Q12=makeQuery(id+"F1.opExtrude","SWEPT_EDGE",EDGE,{"disambiguationData":[OSD([sQuery(id+"F0.wireOp",EDGE,"E16"),sQuery(id+"F0.wireOp",EDGE,"E17")])]});
            var Q13;
            Q13=makeQuery(id+"F1.opExtrude","SWEPT_EDGE",EDGE,{"disambiguationData":[OSD([sQuery(id+"F0.wireOp",EDGE,"E18.MirrorCS"),sQuery(id+"F0.wireOp",EDGE,"E19.MirrorCS")])]});
            var Q14;
            Q14=makeQuery(id+"F1.opExtrude","SWEPT_EDGE",EDGE,{"disambiguationData":[OSD([sQuery(id+"F0.wireOp",EDGE,"E19.MirrorCS"),sQuery(id+"F0.wireOp",EDGE,"E20.MirrorCS")])]});
            var Q15;
            Q15=makeQuery(id+"F1.opExtrude","SWEPT_EDGE",EDGE,{"disambiguationData":[OSD([sQuery(id+"F0.wireOp",EDGE,"E20.MirrorCS"),sQuery(id+"F0.wireOp",EDGE,"E21.MirrorCS")])]});
            var Q16;
            Q16=makeQuery(id+"F1.opExtrude","SWEPT_EDGE",EDGE,{"disambiguationData":[OSD([sQuery(id+"F0.wireOp",EDGE,"E21.MirrorCS"),sQuery(id+"F0.wireOp",EDGE,"E22.MirrorCS")])]});
            var Q17;
            Q17=makeQuery(id+"F1.opExtrude","SWEPT_EDGE",EDGE,{"disambiguationData":[OSD([sQuery(id+"F0.wireOp",EDGE,"E24.MirrorCS"),sQuery(id+"F0.wireOp",EDGE,"E25.MirrorCS")])]});
            var Q18;
            Q18=makeQuery(id+"F1.opExtrude","SWEPT_EDGE",EDGE,{"disambiguationData":[OSD([sQuery(id+"F0.wireOp",EDGE,"E25.MirrorCS"),sQuery(id+"F0.wireOp",EDGE,"E29.MirrorCS")])]});
            var Q19;
            Q19=makeQuery(id+"F1.opExtrude","SWEPT_EDGE",EDGE,{"disambiguationData":[OSD([sQuery(id+"F0.wireOp",EDGE,"E26.MirrorCS"),sQuery(id+"F0.wireOp",EDGE,"E28.MirrorCS")])]});
            var Q20;
            Q20=makeQuery(id+"F1.opExtrude","SWEPT_EDGE",EDGE,{"disambiguationData":[OSD([sQuery(id+"F0.wireOp",EDGE,"E28.MirrorCS"),sQuery(id+"F0.wireOp",EDGE,"E30.MirrorCS")])]});
            var Q21;
            Q21=makeQuery(id+"F1.opExtrude","SWEPT_EDGE",EDGE,{"disambiguationData":[OSD([sQuery(id+"F0.wireOp",EDGE,"E30.MirrorCS"),sQuery(id+"F0.wireOp",EDGE,"E31.MirrorCS")])]});
            var Q22;
            Q22=makeQuery(id+"F1.opExtrude","SWEPT_EDGE",EDGE,{"disambiguationData":[OSD([sQuery(id+"F0.wireOp",EDGE,"E22.MirrorCS"),sQuery(id+"F0.wireOp",EDGE,"E23.MirrorCS")])]});
            var Q23;
            Q23=makeQuery(id+"F1.opExtrude","SWEPT_EDGE",EDGE,{"disambiguationData":[OSD([sQuery(id+"F0.wireOp",EDGE,"E23.MirrorCS"),sQuery(id+"F0.wireOp",EDGE,"E24.MirrorCS")])]});
            var Q24;
            Q24=makeQuery(id+"F1.opExtrude","SWEPT_EDGE",EDGE,{"disambiguationData":[OSD([sQuery(id+"F0.wireOp",EDGE,"E27.MirrorCS"),sQuery(id+"F0.wireOp",EDGE,"E29.MirrorCS")])]});
            var Q25;
            Q25=makeQuery(id+"F1.opExtrude","SWEPT_EDGE",EDGE,{"disambiguationData":[OSD([sQuery(id+"F0.wireOp",EDGE,"E26.MirrorCS"),sQuery(id+"F0.wireOp",EDGE,"E27.MirrorCS")])]});
            fillet(context, id + "F4", {"entities" : qUnion([Q0, Q1, Q2, Q3, Q4, Q5, Q6, Q7, Q8, Q9, Q10, Q11, Q12, Q13, Q14, Q15, Q16, Q17, Q18, Q19, Q20, Q21, Q22, Q23, Q24, Q25]), "radius" : 0.6 * mm, "tangentPropagation" : true, "allowEdgeOverflow" : false});
        }
        {
            var Q0;
            Q0=makeQuery(id+"F1.opExtrude","CAP_FACE",FACE,{"disambiguationData":[OSD([sQuery(id+"F0.wireOp",EDGE,"E0"),sQuery(id+"F0.wireOp",EDGE,"E1.0"),sQuery(id+"F0.wireOp",EDGE,"E1.1"),sQuery(id+"F0.wireOp",EDGE,"E1.2"),sQuery(id+"F0.wireOp",EDGE,"E1.3"),sQuery(id+"F0.wireOp",EDGE,"E1.4"),sQuery(id+"F0.wireOp",EDGE,"E1.5"),sQuery(id+"F0.wireOp",EDGE,"E1.6"),sQuery(id+"F0.wireOp",EDGE,"E1.7"),sQuery(id+"F0.wireOp",EDGE,"E1.8"),sQuery(id+"F0.wireOp",EDGE,"E1.9"),sQuery(id+"F0.wireOp",EDGE,"E1.10"),sQuery(id+"F0.wireOp",EDGE,"E2"),sQuery(id+"F0.wireOp",EDGE,"E3.2.0"),sQuery(id+"F0.wireOp",EDGE,"E3.3.0"),sQuery(id+"F0.wireOp",EDGE,"E3.4.0"),sQuery(id+"F0.wireOp",EDGE,"E3.5.0"),sQuery(id+"F0.wireOp",EDGE,"E3.6.0"),sQuery(id+"F0.wireOp",EDGE,"E3.7.0"),sQuery(id+"F0.wireOp",EDGE,"E3.8.0"),sQuery(id+"F0.wireOp",EDGE,"E3.9.0"),sQuery(id+"F0.wireOp",EDGE,"E3.10.0"),sQuery(id+"F0.wireOp",EDGE,"E4"),sQuery(id+"F0.wireOp",EDGE,"E5"),sQuery(id+"F0.wireOp",EDGE,"E6"),sQuery(id+"F0.wireOp",EDGE,"E7"),sQuery(id+"F0.wireOp",EDGE,"E8"),sQuery(id+"F0.wireOp",EDGE,"E9"),sQuery(id+"F0.wireOp",EDGE,"E10"),sQuery(id+"F0.wireOp",EDGE,"E11"),sQuery(id+"F0.wireOp",EDGE,"E12"),sQuery(id+"F0.wireOp",EDGE,"E13"),sQuery(id+"F0.wireOp",EDGE,"E14"),sQuery(id+"F0.wireOp",EDGE,"E15"),sQuery(id+"F0.wireOp",EDGE,"E16"),sQuery(id+"F0.wireOp",EDGE,"E17"),sQuery(id+"F0.wireOp",EDGE,"E18.MirrorCS"),sQuery(id+"F0.wireOp",EDGE,"E19.MirrorCS"),sQuery(id+"F0.wireOp",EDGE,"E20.MirrorCS"),sQuery(id+"F0.wireOp",EDGE,"E21.MirrorCS"),sQuery(id+"F0.wireOp",EDGE,"E22.MirrorCS"),sQuery(id+"F0.wireOp",EDGE,"E23.MirrorCS"),sQuery(id+"F0.wireOp",EDGE,"E24.MirrorCS"),sQuery(id+"F0.wireOp",EDGE,"E25.MirrorCS"),sQuery(id+"F0.wireOp",EDGE,"E26.MirrorCS"),sQuery(id+"F0.wireOp",EDGE,"E27.MirrorCS"),sQuery(id+"F0.wireOp",EDGE,"E28.MirrorCS"),sQuery(id+"F0.wireOp",EDGE,"E29.MirrorCS"),sQuery(id+"F0.wireOp",EDGE,"E30.MirrorCS"),sQuery(id+"F0.wireOp",EDGE,"E31.MirrorCS")])],"isStart":false});
            var sketch = newSketch(context, id + "F5", { "sketchPlane" : qUnion([Q0])});
            skCircle(sketch, "E35.0", {"center": v(0, 0) * mm, "radius": 10.6 * mm});
            skArc(sketch, "E36.0", {"start": v(7.31, 8.96) * mm, "mid": v(8.6, 13.38) * mm, "end": v(5.1, 10.37) * mm});
            skLineSegment(sketch, "E37.0", {"start": v(5.1, 10.37) * mm, "end": v(2.4, 11.17) * mm});
            skLineSegment(sketch, "E38.0", {"start": v(2.4, 11.17) * mm, "end": v(2.4, 13.32) * mm});
            skLineSegment(sketch, "E39.0", {"start": v(0.4, 13.32) * mm, "end": v(0.4, 17.52) * mm});
            skLineSegment(sketch, "E40.0", {"start": v(2.4, 13.32) * mm, "end": v(0.4, 13.32) * mm});
            skLineSegment(sketch, "E41.0", {"start": v(-0.4, 13.32) * mm, "end": v(-2.4, 13.32) * mm});
            skLineSegment(sketch, "E42.0", {"start": v(-0.4, 17.52) * mm, "end": v(-0.4, 13.32) * mm});
            skLineSegment(sketch, "E43.0", {"start": v(-2.4, 13.32) * mm, "end": v(-2.4, 11.17) * mm});
            skLineSegment(sketch, "E44.0", {"start": v(-2.4, 11.17) * mm, "end": v(-5.1, 10.37) * mm});
            skArc(sketch, "E45.0", {"start": v(-5.1, 10.37) * mm, "mid": v(-8.6, 13.38) * mm, "end": v(-7.31, 8.96) * mm});
            skLineSegment(sketch, "E46.0", {"start": v(-7.31, 8.96) * mm, "end": v(-9.9, 5.97) * mm});
            skArc(sketch, "E47.0", {"start": v(-9.9, 5.97) * mm, "mid": v(-14.46, 6.6) * mm, "end": v(-11, 3.58) * mm});
            skLineSegment(sketch, "E48.0", {"start": v(-11, 3.58) * mm, "end": v(-11.56, -0.34) * mm});
            skArc(sketch, "E49.0", {"start": v(-11.56, -0.34) * mm, "mid": v(-15.74, -2.26) * mm, "end": v(-11.19, -2.93) * mm});
            skLineSegment(sketch, "E50.0", {"start": v(-11.19, -2.93) * mm, "end": v(-9.54, -6.53) * mm});
            skArc(sketch, "E51.0", {"start": v(-9.54, -6.53) * mm, "mid": v(-12.02, -10.41) * mm, "end": v(-7.82, -8.51) * mm});
            skLineSegment(sketch, "E52.0", {"start": v(-7.82, -8.51) * mm, "end": v(-4.5, -10.65) * mm});
            skArc(sketch, "E53.0", {"start": v(-4.5, -10.65) * mm, "mid": v(-4.48, -15.26) * mm, "end": v(-1.98, -11.4) * mm});
            skLineSegment(sketch, "E54.0", {"start": v(-1.98, -11.4) * mm, "end": v(1.98, -11.4) * mm});
            skArc(sketch, "E55.0", {"start": v(1.98, -11.4) * mm, "mid": v(4.48, -15.26) * mm, "end": v(4.5, -10.65) * mm});
            skLineSegment(sketch, "E56.0", {"start": v(4.5, -10.65) * mm, "end": v(7.82, -8.51) * mm});
            skArc(sketch, "E57.0", {"start": v(7.82, -8.51) * mm, "mid": v(12.02, -10.41) * mm, "end": v(9.54, -6.53) * mm});
            skArc(sketch, "E58.0", {"start": v(11.19, -2.93) * mm, "mid": v(15.74, -2.26) * mm, "end": v(11.56, -0.34) * mm});
            skLineSegment(sketch, "E59.0", {"start": v(9.54, -6.53) * mm, "end": v(11.19, -2.93) * mm});
            skLineSegment(sketch, "E60.0", {"start": v(11.56, -0.34) * mm, "end": v(11, 3.58) * mm});
            skArc(sketch, "E61.0", {"start": v(11, 3.58) * mm, "mid": v(14.46, 6.6) * mm, "end": v(9.9, 5.97) * mm});
            skLineSegment(sketch, "E62.0", {"start": v(9.9, 5.97) * mm, "end": v(7.31, 8.96) * mm});
            skLineSegment(sketch, "E63.0", {"start": v(0.4, 17.52) * mm, "end": v(4.6, 17.52) * mm});
            skLineSegment(sketch, "E64.0", {"start": v(4.6, 18.32) * mm, "end": v(0.4, 18.32) * mm});
            skLineSegment(sketch, "E65.0", {"start": v(-0.4, 18.32) * mm, "end": v(-4.6, 18.32) * mm});
            skLineSegment(sketch, "E66.0", {"start": v(-4.6, 17.52) * mm, "end": v(-0.4, 17.52) * mm});
            skLineSegment(sketch, "E67.0", {"start": v(-4.6, 15.52) * mm, "end": v(-4.6, 17.52) * mm});
            skLineSegment(sketch, "E68.0", {"start": v(-5.4, 15.52) * mm, "end": v(-4.6, 15.52) * mm});
            skLineSegment(sketch, "E69.0", {"start": v(-5.4, 20.32) * mm, "end": v(-5.4, 15.52) * mm});
            skLineSegment(sketch, "E70.0", {"start": v(-4.6, 18.32) * mm, "end": v(-4.6, 20.32) * mm});
            skLineSegment(sketch, "E71.0", {"start": v(-4.6, 20.32) * mm, "end": v(-5.4, 20.32) * mm});
            skLineSegment(sketch, "E72.0", {"start": v(-0.4, 22.52) * mm, "end": v(-0.4, 18.32) * mm});
            skLineSegment(sketch, "E73.0", {"start": v(0.4, 18.32) * mm, "end": v(0.4, 22.52) * mm});
            skLineSegment(sketch, "E74.0", {"start": v(4.6, 17.52) * mm, "end": v(4.6, 15.52) * mm});
            skLineSegment(sketch, "E75.0", {"start": v(5.4, 15.52) * mm, "end": v(5.4, 20.32) * mm});
            skLineSegment(sketch, "E76.0", {"start": v(4.6, 15.52) * mm, "end": v(5.4, 15.52) * mm});
            skLineSegment(sketch, "E77.0", {"start": v(5.4, 20.32) * mm, "end": v(4.6, 20.32) * mm});
            skLineSegment(sketch, "E78.0", {"start": v(4.6, 20.32) * mm, "end": v(4.6, 18.32) * mm});
            skLineSegment(sketch, "E79.0", {"start": v(-2.4, 22.52) * mm, "end": v(-0.4, 22.52) * mm});
            skLineSegment(sketch, "E80.0", {"start": v(-2.4, 23.32) * mm, "end": v(-2.4, 22.52) * mm});
            skLineSegment(sketch, "E81.0", {"start": v(2.4, 23.32) * mm, "end": v(-2.4, 23.32) * mm});
            skLineSegment(sketch, "E82.0", {"start": v(2.4, 22.52) * mm, "end": v(2.4, 23.32) * mm});
            skLineSegment(sketch, "E83.0.0", {"start": v(5.4, 20.32) * mm, "end": v(5.4, 15.52) * mm});
            skLineSegment(sketch, "E83.0.1", {"start": v(5.4, 15.52) * mm, "end": v(6, 15.52) * mm});
            skLineSegment(sketch, "E83.0.2", {"start": v(6, 20.32) * mm, "end": v(6, 15.52) * mm});
            skLineSegment(sketch, "E83.0.3", {"start": v(6, 20.32) * mm, "end": v(5.4, 20.32) * mm});
            skLineSegment(sketch, "E84.0", {"start": v(0.4, 22.52) * mm, "end": v(2.4, 22.52) * mm});
            skSolve(sketch);
        }
        {
            var Q0;
            Q0=makeQuery(id+"F5.imprint","IMPRINT",FACE,{"disambiguationData":[TD([[makeQuery(id+"F5.imprint","IMPRINT",EDGE,{"derivedFrom":sQuery(id+"F5.wireOp",EDGE,"E35.0")}),1.0]])]});
            extrude(context, id + "F6", {"entities" : qUnion([Q0]), "operationType" : NewBodyOperationType.REMOVE, "oppositeDirection" : true, "depth" : 0.5 * mm});
        }
        {
            var Q0;
            Q0=makeQuery(id+"F6.boolean.opBoolean","COPY",EDGE,{"derivedFrom":makeQuery(id+"F6.opExtrude","CAP_EDGE",EDGE,{"disambiguationData":[OSD([sQuery(id+"F5.wireOp",EDGE,"E42.0")])],"isStart":false})});
            var Q1;
            {var subQ0=sQuery(id+"F0.wireOp",EDGE,"E28.MirrorCS");Q1=makeQuery(id+"F6.boolean.opBoolean","MERGE",EDGE,{"derivedFrom":[makeQuery(id+"F2.opFillet","BLEND_EDGE",EDGE,{"blendedFrom":[makeQuery(id+"F1.opExtrude","CAP_EDGE",EDGE,{"disambiguationData":[OSD([subQ0])],"isStart":false}),makeQuery(id+"F1.opExtrude","CAP_FACE",FACE,{"disambiguationData":[OSD([sQuery(id+"F0.wireOp",EDGE,"E0"),sQuery(id+"F0.wireOp",EDGE,"E1.0"),sQuery(id+"F0.wireOp",EDGE,"E1.1"),sQuery(id+"F0.wireOp",EDGE,"E1.2"),sQuery(id+"F0.wireOp",EDGE,"E1.3"),sQuery(id+"F0.wireOp",EDGE,"E1.4"),sQuery(id+"F0.wireOp",EDGE,"E1.5"),sQuery(id+"F0.wireOp",EDGE,"E1.6"),sQuery(id+"F0.wireOp",EDGE,"E1.7"),sQuery(id+"F0.wireOp",EDGE,"E1.8"),sQuery(id+"F0.wireOp",EDGE,"E1.9"),sQuery(id+"F0.wireOp",EDGE,"E1.10"),sQuery(id+"F0.wireOp",EDGE,"E2"),sQuery(id+"F0.wireOp",EDGE,"E3.2.0"),sQuery(id+"F0.wireOp",EDGE,"E3.3.0"),sQuery(id+"F0.wireOp",EDGE,"E3.4.0"),sQuery(id+"F0.wireOp",EDGE,"E3.5.0"),sQuery(id+"F0.wireOp",EDGE,"E3.6.0"),sQuery(id+"F0.wireOp",EDGE,"E3.7.0"),sQuery(id+"F0.wireOp",EDGE,"E3.8.0"),sQuery(id+"F0.wireOp",EDGE,"E3.9.0"),sQuery(id+"F0.wireOp",EDGE,"E3.10.0"),sQuery(id+"F0.wireOp",EDGE,"E4"),sQuery(id+"F0.wireOp",EDGE,"E5"),sQuery(id+"F0.wireOp",EDGE,"E6"),sQuery(id+"F0.wireOp",EDGE,"E7"),sQuery(id+"F0.wireOp",EDGE,"E8"),sQuery(id+"F0.wireOp",EDGE,"E9"),sQuery(id+"F0.wireOp",EDGE,"E10"),sQuery(id+"F0.wireOp",EDGE,"E11"),sQuery(id+"F0.wireOp",EDGE,"E12"),sQuery(id+"F0.wireOp",EDGE,"E13"),sQuery(id+"F0.wireOp",EDGE,"E14"),sQuery(id+"F0.wireOp",EDGE,"E15"),sQuery(id+"F0.wireOp",EDGE,"E16"),sQuery(id+"F0.wireOp",EDGE,"E17"),sQuery(id+"F0.wireOp",EDGE,"E18.MirrorCS"),sQuery(id+"F0.wireOp",EDGE,"E19.MirrorCS"),sQuery(id+"F0.wireOp",EDGE,"E20.MirrorCS"),sQuery(id+"F0.wireOp",EDGE,"E21.MirrorCS"),sQuery(id+"F0.wireOp",EDGE,"E22.MirrorCS"),sQuery(id+"F0.wireOp",EDGE,"E23.MirrorCS"),sQuery(id+"F0.wireOp",EDGE,"E24.MirrorCS"),sQuery(id+"F0.wireOp",EDGE,"E25.MirrorCS"),sQuery(id+"F0.wireOp",EDGE,"E26.MirrorCS"),sQuery(id+"F0.wireOp",EDGE,"E27.MirrorCS"),subQ0,sQuery(id+"F0.wireOp",EDGE,"E29.MirrorCS"),sQuery(id+"F0.wireOp",EDGE,"E30.MirrorCS"),sQuery(id+"F0.wireOp",EDGE,"E31.MirrorCS")])],"isStart":false})],"blendedInto":[makeQuery(id+"F1.opExtrude","CAP_FACE",FACE,{"disambiguationData":[OSD([sQuery(id+"F0.wireOp",EDGE,"E0"),sQuery(id+"F0.wireOp",EDGE,"E1.0"),sQuery(id+"F0.wireOp",EDGE,"E1.1"),sQuery(id+"F0.wireOp",EDGE,"E1.2"),sQuery(id+"F0.wireOp",EDGE,"E1.3"),sQuery(id+"F0.wireOp",EDGE,"E1.4"),sQuery(id+"F0.wireOp",EDGE,"E1.5"),sQuery(id+"F0.wireOp",EDGE,"E1.6"),sQuery(id+"F0.wireOp",EDGE,"E1.7"),sQuery(id+"F0.wireOp",EDGE,"E1.8"),sQuery(id+"F0.wireOp",EDGE,"E1.9"),sQuery(id+"F0.wireOp",EDGE,"E1.10"),sQuery(id+"F0.wireOp",EDGE,"E2"),sQuery(id+"F0.wireOp",EDGE,"E3.2.0"),sQuery(id+"F0.wireOp",EDGE,"E3.3.0"),sQuery(id+"F0.wireOp",EDGE,"E3.4.0"),sQuery(id+"F0.wireOp",EDGE,"E3.5.0"),sQuery(id+"F0.wireOp",EDGE,"E3.6.0"),sQuery(id+"F0.wireOp",EDGE,"E3.7.0"),sQuery(id+"F0.wireOp",EDGE,"E3.8.0"),sQuery(id+"F0.wireOp",EDGE,"E3.9.0"),sQuery(id+"F0.wireOp",EDGE,"E3.10.0"),sQuery(id+"F0.wireOp",EDGE,"E4"),sQuery(id+"F0.wireOp",EDGE,"E5"),sQuery(id+"F0.wireOp",EDGE,"E6"),sQuery(id+"F0.wireOp",EDGE,"E7"),sQuery(id+"F0.wireOp",EDGE,"E8"),sQuery(id+"F0.wireOp",EDGE,"E9"),sQuery(id+"F0.wireOp",EDGE,"E10"),sQuery(id+"F0.wireOp",EDGE,"E11"),sQuery(id+"F0.wireOp",EDGE,"E12"),sQuery(id+"F0.wireOp",EDGE,"E13"),sQuery(id+"F0.wireOp",EDGE,"E14"),sQuery(id+"F0.wireOp",EDGE,"E15"),sQuery(id+"F0.wireOp",EDGE,"E16"),sQuery(id+"F0.wireOp",EDGE,"E17"),sQuery(id+"F0.wireOp",EDGE,"E18.MirrorCS"),sQuery(id+"F0.wireOp",EDGE,"E19.MirrorCS"),sQuery(id+"F0.wireOp",EDGE,"E20.MirrorCS"),sQuery(id+"F0.wireOp",EDGE,"E21.MirrorCS"),sQuery(id+"F0.wireOp",EDGE,"E22.MirrorCS"),sQuery(id+"F0.wireOp",EDGE,"E23.MirrorCS"),sQuery(id+"F0.wireOp",EDGE,"E24.MirrorCS"),sQuery(id+"F0.wireOp",EDGE,"E25.MirrorCS"),sQuery(id+"F0.wireOp",EDGE,"E26.MirrorCS"),sQuery(id+"F0.wireOp",EDGE,"E27.MirrorCS"),subQ0,sQuery(id+"F0.wireOp",EDGE,"E29.MirrorCS"),sQuery(id+"F0.wireOp",EDGE,"E30.MirrorCS"),sQuery(id+"F0.wireOp",EDGE,"E31.MirrorCS")])],"isStart":false})]}),makeQuery(id+"F6.opExtrude","CAP_EDGE",EDGE,{"disambiguationData":[OSD([sQuery(id+"F5.wireOp",EDGE,"E42.0")])],"isStart":true})]});}
            var Q2;
            {var subQ0=sQuery(id+"F0.wireOp",EDGE,"E30.MirrorCS");Q2=makeQuery(id+"F6.boolean.opBoolean","MERGE",EDGE,{"derivedFrom":[makeQuery(id+"F2.opFillet","BLEND_EDGE",EDGE,{"blendedFrom":[makeQuery(id+"F1.opExtrude","CAP_EDGE",EDGE,{"disambiguationData":[OSD([subQ0])],"isStart":false}),makeQuery(id+"F1.opExtrude","CAP_FACE",FACE,{"disambiguationData":[OSD([sQuery(id+"F0.wireOp",EDGE,"E0"),sQuery(id+"F0.wireOp",EDGE,"E1.0"),sQuery(id+"F0.wireOp",EDGE,"E1.1"),sQuery(id+"F0.wireOp",EDGE,"E1.2"),sQuery(id+"F0.wireOp",EDGE,"E1.3"),sQuery(id+"F0.wireOp",EDGE,"E1.4"),sQuery(id+"F0.wireOp",EDGE,"E1.5"),sQuery(id+"F0.wireOp",EDGE,"E1.6"),sQuery(id+"F0.wireOp",EDGE,"E1.7"),sQuery(id+"F0.wireOp",EDGE,"E1.8"),sQuery(id+"F0.wireOp",EDGE,"E1.9"),sQuery(id+"F0.wireOp",EDGE,"E1.10"),sQuery(id+"F0.wireOp",EDGE,"E2"),sQuery(id+"F0.wireOp",EDGE,"E3.2.0"),sQuery(id+"F0.wireOp",EDGE,"E3.3.0"),sQuery(id+"F0.wireOp",EDGE,"E3.4.0"),sQuery(id+"F0.wireOp",EDGE,"E3.5.0"),sQuery(id+"F0.wireOp",EDGE,"E3.6.0"),sQuery(id+"F0.wireOp",EDGE,"E3.7.0"),sQuery(id+"F0.wireOp",EDGE,"E3.8.0"),sQuery(id+"F0.wireOp",EDGE,"E3.9.0"),sQuery(id+"F0.wireOp",EDGE,"E3.10.0"),sQuery(id+"F0.wireOp",EDGE,"E4"),sQuery(id+"F0.wireOp",EDGE,"E5"),sQuery(id+"F0.wireOp",EDGE,"E6"),sQuery(id+"F0.wireOp",EDGE,"E7"),sQuery(id+"F0.wireOp",EDGE,"E8"),sQuery(id+"F0.wireOp",EDGE,"E9"),sQuery(id+"F0.wireOp",EDGE,"E10"),sQuery(id+"F0.wireOp",EDGE,"E11"),sQuery(id+"F0.wireOp",EDGE,"E12"),sQuery(id+"F0.wireOp",EDGE,"E13"),sQuery(id+"F0.wireOp",EDGE,"E14"),sQuery(id+"F0.wireOp",EDGE,"E15"),sQuery(id+"F0.wireOp",EDGE,"E16"),sQuery(id+"F0.wireOp",EDGE,"E17"),sQuery(id+"F0.wireOp",EDGE,"E18.MirrorCS"),sQuery(id+"F0.wireOp",EDGE,"E19.MirrorCS"),sQuery(id+"F0.wireOp",EDGE,"E20.MirrorCS"),sQuery(id+"F0.wireOp",EDGE,"E21.MirrorCS"),sQuery(id+"F0.wireOp",EDGE,"E22.MirrorCS"),sQuery(id+"F0.wireOp",EDGE,"E23.MirrorCS"),sQuery(id+"F0.wireOp",EDGE,"E24.MirrorCS"),sQuery(id+"F0.wireOp",EDGE,"E25.MirrorCS"),sQuery(id+"F0.wireOp",EDGE,"E26.MirrorCS"),sQuery(id+"F0.wireOp",EDGE,"E27.MirrorCS"),sQuery(id+"F0.wireOp",EDGE,"E28.MirrorCS"),sQuery(id+"F0.wireOp",EDGE,"E29.MirrorCS"),subQ0,sQuery(id+"F0.wireOp",EDGE,"E31.MirrorCS")])],"isStart":false})],"blendedInto":[makeQuery(id+"F1.opExtrude","CAP_FACE",FACE,{"disambiguationData":[OSD([sQuery(id+"F0.wireOp",EDGE,"E0"),sQuery(id+"F0.wireOp",EDGE,"E1.0"),sQuery(id+"F0.wireOp",EDGE,"E1.1"),sQuery(id+"F0.wireOp",EDGE,"E1.2"),sQuery(id+"F0.wireOp",EDGE,"E1.3"),sQuery(id+"F0.wireOp",EDGE,"E1.4"),sQuery(id+"F0.wireOp",EDGE,"E1.5"),sQuery(id+"F0.wireOp",EDGE,"E1.6"),sQuery(id+"F0.wireOp",EDGE,"E1.7"),sQuery(id+"F0.wireOp",EDGE,"E1.8"),sQuery(id+"F0.wireOp",EDGE,"E1.9"),sQuery(id+"F0.wireOp",EDGE,"E1.10"),sQuery(id+"F0.wireOp",EDGE,"E2"),sQuery(id+"F0.wireOp",EDGE,"E3.2.0"),sQuery(id+"F0.wireOp",EDGE,"E3.3.0"),sQuery(id+"F0.wireOp",EDGE,"E3.4.0"),sQuery(id+"F0.wireOp",EDGE,"E3.5.0"),sQuery(id+"F0.wireOp",EDGE,"E3.6.0"),sQuery(id+"F0.wireOp",EDGE,"E3.7.0"),sQuery(id+"F0.wireOp",EDGE,"E3.8.0"),sQuery(id+"F0.wireOp",EDGE,"E3.9.0"),sQuery(id+"F0.wireOp",EDGE,"E3.10.0"),sQuery(id+"F0.wireOp",EDGE,"E4"),sQuery(id+"F0.wireOp",EDGE,"E5"),sQuery(id+"F0.wireOp",EDGE,"E6"),sQuery(id+"F0.wireOp",EDGE,"E7"),sQuery(id+"F0.wireOp",EDGE,"E8"),sQuery(id+"F0.wireOp",EDGE,"E9"),sQuery(id+"F0.wireOp",EDGE,"E10"),sQuery(id+"F0.wireOp",EDGE,"E11"),sQuery(id+"F0.wireOp",EDGE,"E12"),sQuery(id+"F0.wireOp",EDGE,"E13"),sQuery(id+"F0.wireOp",EDGE,"E14"),sQuery(id+"F0.wireOp",EDGE,"E15"),sQuery(id+"F0.wireOp",EDGE,"E16"),sQuery(id+"F0.wireOp",EDGE,"E17"),sQuery(id+"F0.wireOp",EDGE,"E18.MirrorCS"),sQuery(id+"F0.wireOp",EDGE,"E19.MirrorCS"),sQuery(id+"F0.wireOp",EDGE,"E20.MirrorCS"),sQuery(id+"F0.wireOp",EDGE,"E21.MirrorCS"),sQuery(id+"F0.wireOp",EDGE,"E22.MirrorCS"),sQuery(id+"F0.wireOp",EDGE,"E23.MirrorCS"),sQuery(id+"F0.wireOp",EDGE,"E24.MirrorCS"),sQuery(id+"F0.wireOp",EDGE,"E25.MirrorCS"),sQuery(id+"F0.wireOp",EDGE,"E26.MirrorCS"),sQuery(id+"F0.wireOp",EDGE,"E27.MirrorCS"),sQuery(id+"F0.wireOp",EDGE,"E28.MirrorCS"),sQuery(id+"F0.wireOp",EDGE,"E29.MirrorCS"),subQ0,sQuery(id+"F0.wireOp",EDGE,"E31.MirrorCS")])],"isStart":false})]}),makeQuery(id+"F6.opExtrude","CAP_EDGE",EDGE,{"disambiguationData":[OSD([sQuery(id+"F5.wireOp",EDGE,"E41.0")])],"isStart":true})]});}
            var Q3;
            Q3=makeQuery(id+"F6.boolean.opBoolean","COPY",EDGE,{"derivedFrom":makeQuery(id+"F6.opExtrude","CAP_EDGE",EDGE,{"disambiguationData":[OSD([sQuery(id+"F5.wireOp",EDGE,"E41.0")])],"isStart":false})});
            var Q4;
            {var subQ0=sQuery(id+"F0.wireOp",EDGE,"E31.MirrorCS");Q4=makeQuery(id+"F6.boolean.opBoolean","MERGE",EDGE,{"derivedFrom":[makeQuery(id+"F2.opFillet","BLEND_EDGE",EDGE,{"blendedFrom":[makeQuery(id+"F1.opExtrude","CAP_EDGE",EDGE,{"disambiguationData":[OSD([subQ0])],"isStart":false}),makeQuery(id+"F1.opExtrude","CAP_FACE",FACE,{"disambiguationData":[OSD([sQuery(id+"F0.wireOp",EDGE,"E0"),sQuery(id+"F0.wireOp",EDGE,"E1.0"),sQuery(id+"F0.wireOp",EDGE,"E1.1"),sQuery(id+"F0.wireOp",EDGE,"E1.2"),sQuery(id+"F0.wireOp",EDGE,"E1.3"),sQuery(id+"F0.wireOp",EDGE,"E1.4"),sQuery(id+"F0.wireOp",EDGE,"E1.5"),sQuery(id+"F0.wireOp",EDGE,"E1.6"),sQuery(id+"F0.wireOp",EDGE,"E1.7"),sQuery(id+"F0.wireOp",EDGE,"E1.8"),sQuery(id+"F0.wireOp",EDGE,"E1.9"),sQuery(id+"F0.wireOp",EDGE,"E1.10"),sQuery(id+"F0.wireOp",EDGE,"E2"),sQuery(id+"F0.wireOp",EDGE,"E3.2.0"),sQuery(id+"F0.wireOp",EDGE,"E3.3.0"),sQuery(id+"F0.wireOp",EDGE,"E3.4.0"),sQuery(id+"F0.wireOp",EDGE,"E3.5.0"),sQuery(id+"F0.wireOp",EDGE,"E3.6.0"),sQuery(id+"F0.wireOp",EDGE,"E3.7.0"),sQuery(id+"F0.wireOp",EDGE,"E3.8.0"),sQuery(id+"F0.wireOp",EDGE,"E3.9.0"),sQuery(id+"F0.wireOp",EDGE,"E3.10.0"),sQuery(id+"F0.wireOp",EDGE,"E4"),sQuery(id+"F0.wireOp",EDGE,"E5"),sQuery(id+"F0.wireOp",EDGE,"E6"),sQuery(id+"F0.wireOp",EDGE,"E7"),sQuery(id+"F0.wireOp",EDGE,"E8"),sQuery(id+"F0.wireOp",EDGE,"E9"),sQuery(id+"F0.wireOp",EDGE,"E10"),sQuery(id+"F0.wireOp",EDGE,"E11"),sQuery(id+"F0.wireOp",EDGE,"E12"),sQuery(id+"F0.wireOp",EDGE,"E13"),sQuery(id+"F0.wireOp",EDGE,"E14"),sQuery(id+"F0.wireOp",EDGE,"E15"),sQuery(id+"F0.wireOp",EDGE,"E16"),sQuery(id+"F0.wireOp",EDGE,"E17"),sQuery(id+"F0.wireOp",EDGE,"E18.MirrorCS"),sQuery(id+"F0.wireOp",EDGE,"E19.MirrorCS"),sQuery(id+"F0.wireOp",EDGE,"E20.MirrorCS"),sQuery(id+"F0.wireOp",EDGE,"E21.MirrorCS"),sQuery(id+"F0.wireOp",EDGE,"E22.MirrorCS"),sQuery(id+"F0.wireOp",EDGE,"E23.MirrorCS"),sQuery(id+"F0.wireOp",EDGE,"E24.MirrorCS"),sQuery(id+"F0.wireOp",EDGE,"E25.MirrorCS"),sQuery(id+"F0.wireOp",EDGE,"E26.MirrorCS"),sQuery(id+"F0.wireOp",EDGE,"E27.MirrorCS"),sQuery(id+"F0.wireOp",EDGE,"E28.MirrorCS"),sQuery(id+"F0.wireOp",EDGE,"E29.MirrorCS"),sQuery(id+"F0.wireOp",EDGE,"E30.MirrorCS"),subQ0])],"isStart":false})],"blendedInto":[makeQuery(id+"F1.opExtrude","CAP_FACE",FACE,{"disambiguationData":[OSD([sQuery(id+"F0.wireOp",EDGE,"E0"),sQuery(id+"F0.wireOp",EDGE,"E1.0"),sQuery(id+"F0.wireOp",EDGE,"E1.1"),sQuery(id+"F0.wireOp",EDGE,"E1.2"),sQuery(id+"F0.wireOp",EDGE,"E1.3"),sQuery(id+"F0.wireOp",EDGE,"E1.4"),sQuery(id+"F0.wireOp",EDGE,"E1.5"),sQuery(id+"F0.wireOp",EDGE,"E1.6"),sQuery(id+"F0.wireOp",EDGE,"E1.7"),sQuery(id+"F0.wireOp",EDGE,"E1.8"),sQuery(id+"F0.wireOp",EDGE,"E1.9"),sQuery(id+"F0.wireOp",EDGE,"E1.10"),sQuery(id+"F0.wireOp",EDGE,"E2"),sQuery(id+"F0.wireOp",EDGE,"E3.2.0"),sQuery(id+"F0.wireOp",EDGE,"E3.3.0"),sQuery(id+"F0.wireOp",EDGE,"E3.4.0"),sQuery(id+"F0.wireOp",EDGE,"E3.5.0"),sQuery(id+"F0.wireOp",EDGE,"E3.6.0"),sQuery(id+"F0.wireOp",EDGE,"E3.7.0"),sQuery(id+"F0.wireOp",EDGE,"E3.8.0"),sQuery(id+"F0.wireOp",EDGE,"E3.9.0"),sQuery(id+"F0.wireOp",EDGE,"E3.10.0"),sQuery(id+"F0.wireOp",EDGE,"E4"),sQuery(id+"F0.wireOp",EDGE,"E5"),sQuery(id+"F0.wireOp",EDGE,"E6"),sQuery(id+"F0.wireOp",EDGE,"E7"),sQuery(id+"F0.wireOp",EDGE,"E8"),sQuery(id+"F0.wireOp",EDGE,"E9"),sQuery(id+"F0.wireOp",EDGE,"E10"),sQuery(id+"F0.wireOp",EDGE,"E11"),sQuery(id+"F0.wireOp",EDGE,"E12"),sQuery(id+"F0.wireOp",EDGE,"E13"),sQuery(id+"F0.wireOp",EDGE,"E14"),sQuery(id+"F0.wireOp",EDGE,"E15"),sQuery(id+"F0.wireOp",EDGE,"E16"),sQuery(id+"F0.wireOp",EDGE,"E17"),sQuery(id+"F0.wireOp",EDGE,"E18.MirrorCS"),sQuery(id+"F0.wireOp",EDGE,"E19.MirrorCS"),sQuery(id+"F0.wireOp",EDGE,"E20.MirrorCS"),sQuery(id+"F0.wireOp",EDGE,"E21.MirrorCS"),sQuery(id+"F0.wireOp",EDGE,"E22.MirrorCS"),sQuery(id+"F0.wireOp",EDGE,"E23.MirrorCS"),sQuery(id+"F0.wireOp",EDGE,"E24.MirrorCS"),sQuery(id+"F0.wireOp",EDGE,"E25.MirrorCS"),sQuery(id+"F0.wireOp",EDGE,"E26.MirrorCS"),sQuery(id+"F0.wireOp",EDGE,"E27.MirrorCS"),sQuery(id+"F0.wireOp",EDGE,"E28.MirrorCS"),sQuery(id+"F0.wireOp",EDGE,"E29.MirrorCS"),sQuery(id+"F0.wireOp",EDGE,"E30.MirrorCS"),subQ0])],"isStart":false})]}),makeQuery(id+"F6.opExtrude","CAP_EDGE",EDGE,{"disambiguationData":[OSD([sQuery(id+"F5.wireOp",EDGE,"E43.0")])],"isStart":true})]});}
            var Q5;
            Q5=makeQuery(id+"F6.boolean.opBoolean","COPY",EDGE,{"derivedFrom":makeQuery(id+"F6.opExtrude","CAP_EDGE",EDGE,{"disambiguationData":[OSD([sQuery(id+"F5.wireOp",EDGE,"E43.0")])],"isStart":false})});
            var Q6;
            {var subQ0=sQuery(id+"F0.wireOp",EDGE,"E1.10");Q6=makeQuery(id+"F6.boolean.opBoolean","MERGE",EDGE,{"derivedFrom":[makeQuery(id+"F2.opFillet","BLEND_EDGE",EDGE,{"blendedFrom":[makeQuery(id+"F1.opExtrude","CAP_EDGE",EDGE,{"disambiguationData":[OSD([subQ0])],"isStart":false}),makeQuery(id+"F1.opExtrude","CAP_FACE",FACE,{"disambiguationData":[OSD([sQuery(id+"F0.wireOp",EDGE,"E0"),sQuery(id+"F0.wireOp",EDGE,"E1.0"),sQuery(id+"F0.wireOp",EDGE,"E1.1"),sQuery(id+"F0.wireOp",EDGE,"E1.2"),sQuery(id+"F0.wireOp",EDGE,"E1.3"),sQuery(id+"F0.wireOp",EDGE,"E1.4"),sQuery(id+"F0.wireOp",EDGE,"E1.5"),sQuery(id+"F0.wireOp",EDGE,"E1.6"),sQuery(id+"F0.wireOp",EDGE,"E1.7"),sQuery(id+"F0.wireOp",EDGE,"E1.8"),sQuery(id+"F0.wireOp",EDGE,"E1.9"),subQ0,sQuery(id+"F0.wireOp",EDGE,"E2"),sQuery(id+"F0.wireOp",EDGE,"E3.2.0"),sQuery(id+"F0.wireOp",EDGE,"E3.3.0"),sQuery(id+"F0.wireOp",EDGE,"E3.4.0"),sQuery(id+"F0.wireOp",EDGE,"E3.5.0"),sQuery(id+"F0.wireOp",EDGE,"E3.6.0"),sQuery(id+"F0.wireOp",EDGE,"E3.7.0"),sQuery(id+"F0.wireOp",EDGE,"E3.8.0"),sQuery(id+"F0.wireOp",EDGE,"E3.9.0"),sQuery(id+"F0.wireOp",EDGE,"E3.10.0"),sQuery(id+"F0.wireOp",EDGE,"E4"),sQuery(id+"F0.wireOp",EDGE,"E5"),sQuery(id+"F0.wireOp",EDGE,"E6"),sQuery(id+"F0.wireOp",EDGE,"E7"),sQuery(id+"F0.wireOp",EDGE,"E8"),sQuery(id+"F0.wireOp",EDGE,"E9"),sQuery(id+"F0.wireOp",EDGE,"E10"),sQuery(id+"F0.wireOp",EDGE,"E11"),sQuery(id+"F0.wireOp",EDGE,"E12"),sQuery(id+"F0.wireOp",EDGE,"E13"),sQuery(id+"F0.wireOp",EDGE,"E14"),sQuery(id+"F0.wireOp",EDGE,"E15"),sQuery(id+"F0.wireOp",EDGE,"E16"),sQuery(id+"F0.wireOp",EDGE,"E17"),sQuery(id+"F0.wireOp",EDGE,"E18.MirrorCS"),sQuery(id+"F0.wireOp",EDGE,"E19.MirrorCS"),sQuery(id+"F0.wireOp",EDGE,"E20.MirrorCS"),sQuery(id+"F0.wireOp",EDGE,"E21.MirrorCS"),sQuery(id+"F0.wireOp",EDGE,"E22.MirrorCS"),sQuery(id+"F0.wireOp",EDGE,"E23.MirrorCS"),sQuery(id+"F0.wireOp",EDGE,"E24.MirrorCS"),sQuery(id+"F0.wireOp",EDGE,"E25.MirrorCS"),sQuery(id+"F0.wireOp",EDGE,"E26.MirrorCS"),sQuery(id+"F0.wireOp",EDGE,"E27.MirrorCS"),sQuery(id+"F0.wireOp",EDGE,"E28.MirrorCS"),sQuery(id+"F0.wireOp",EDGE,"E29.MirrorCS"),sQuery(id+"F0.wireOp",EDGE,"E30.MirrorCS"),sQuery(id+"F0.wireOp",EDGE,"E31.MirrorCS")])],"isStart":false})],"blendedInto":[makeQuery(id+"F1.opExtrude","CAP_FACE",FACE,{"disambiguationData":[OSD([sQuery(id+"F0.wireOp",EDGE,"E0"),sQuery(id+"F0.wireOp",EDGE,"E1.0"),sQuery(id+"F0.wireOp",EDGE,"E1.1"),sQuery(id+"F0.wireOp",EDGE,"E1.2"),sQuery(id+"F0.wireOp",EDGE,"E1.3"),sQuery(id+"F0.wireOp",EDGE,"E1.4"),sQuery(id+"F0.wireOp",EDGE,"E1.5"),sQuery(id+"F0.wireOp",EDGE,"E1.6"),sQuery(id+"F0.wireOp",EDGE,"E1.7"),sQuery(id+"F0.wireOp",EDGE,"E1.8"),sQuery(id+"F0.wireOp",EDGE,"E1.9"),subQ0,sQuery(id+"F0.wireOp",EDGE,"E2"),sQuery(id+"F0.wireOp",EDGE,"E3.2.0"),sQuery(id+"F0.wireOp",EDGE,"E3.3.0"),sQuery(id+"F0.wireOp",EDGE,"E3.4.0"),sQuery(id+"F0.wireOp",EDGE,"E3.5.0"),sQuery(id+"F0.wireOp",EDGE,"E3.6.0"),sQuery(id+"F0.wireOp",EDGE,"E3.7.0"),sQuery(id+"F0.wireOp",EDGE,"E3.8.0"),sQuery(id+"F0.wireOp",EDGE,"E3.9.0"),sQuery(id+"F0.wireOp",EDGE,"E3.10.0"),sQuery(id+"F0.wireOp",EDGE,"E4"),sQuery(id+"F0.wireOp",EDGE,"E5"),sQuery(id+"F0.wireOp",EDGE,"E6"),sQuery(id+"F0.wireOp",EDGE,"E7"),sQuery(id+"F0.wireOp",EDGE,"E8"),sQuery(id+"F0.wireOp",EDGE,"E9"),sQuery(id+"F0.wireOp",EDGE,"E10"),sQuery(id+"F0.wireOp",EDGE,"E11"),sQuery(id+"F0.wireOp",EDGE,"E12"),sQuery(id+"F0.wireOp",EDGE,"E13"),sQuery(id+"F0.wireOp",EDGE,"E14"),sQuery(id+"F0.wireOp",EDGE,"E15"),sQuery(id+"F0.wireOp",EDGE,"E16"),sQuery(id+"F0.wireOp",EDGE,"E17"),sQuery(id+"F0.wireOp",EDGE,"E18.MirrorCS"),sQuery(id+"F0.wireOp",EDGE,"E19.MirrorCS"),sQuery(id+"F0.wireOp",EDGE,"E20.MirrorCS"),sQuery(id+"F0.wireOp",EDGE,"E21.MirrorCS"),sQuery(id+"F0.wireOp",EDGE,"E22.MirrorCS"),sQuery(id+"F0.wireOp",EDGE,"E23.MirrorCS"),sQuery(id+"F0.wireOp",EDGE,"E24.MirrorCS"),sQuery(id+"F0.wireOp",EDGE,"E25.MirrorCS"),sQuery(id+"F0.wireOp",EDGE,"E26.MirrorCS"),sQuery(id+"F0.wireOp",EDGE,"E27.MirrorCS"),sQuery(id+"F0.wireOp",EDGE,"E28.MirrorCS"),sQuery(id+"F0.wireOp",EDGE,"E29.MirrorCS"),sQuery(id+"F0.wireOp",EDGE,"E30.MirrorCS"),sQuery(id+"F0.wireOp",EDGE,"E31.MirrorCS")])],"isStart":false})]}),makeQuery(id+"F6.opExtrude","CAP_EDGE",EDGE,{"disambiguationData":[OSD([sQuery(id+"F5.wireOp",EDGE,"E44.0")])],"isStart":true})]});}
            var Q7;
            Q7=makeQuery(id+"F6.boolean.opBoolean","COPY",EDGE,{"derivedFrom":makeQuery(id+"F6.opExtrude","CAP_EDGE",EDGE,{"disambiguationData":[OSD([sQuery(id+"F5.wireOp",EDGE,"E44.0")])],"isStart":false})});
            var Q8;
            Q8=makeQuery(id+"F6.boolean.opBoolean","COPY",EDGE,{"derivedFrom":makeQuery(id+"F6.opExtrude","CAP_EDGE",EDGE,{"disambiguationData":[OSD([sQuery(id+"F5.wireOp",EDGE,"E40.0")])],"isStart":false})});
            var Q9;
            {var subQ0=sQuery(id+"F0.wireOp",EDGE,"E5");Q9=makeQuery(id+"F6.boolean.opBoolean","MERGE",EDGE,{"derivedFrom":[makeQuery(id+"F2.opFillet","BLEND_EDGE",EDGE,{"blendedFrom":[makeQuery(id+"F1.opExtrude","CAP_EDGE",EDGE,{"disambiguationData":[OSD([subQ0])],"isStart":false}),makeQuery(id+"F1.opExtrude","CAP_FACE",FACE,{"disambiguationData":[OSD([sQuery(id+"F0.wireOp",EDGE,"E0"),sQuery(id+"F0.wireOp",EDGE,"E1.0"),sQuery(id+"F0.wireOp",EDGE,"E1.1"),sQuery(id+"F0.wireOp",EDGE,"E1.2"),sQuery(id+"F0.wireOp",EDGE,"E1.3"),sQuery(id+"F0.wireOp",EDGE,"E1.4"),sQuery(id+"F0.wireOp",EDGE,"E1.5"),sQuery(id+"F0.wireOp",EDGE,"E1.6"),sQuery(id+"F0.wireOp",EDGE,"E1.7"),sQuery(id+"F0.wireOp",EDGE,"E1.8"),sQuery(id+"F0.wireOp",EDGE,"E1.9"),sQuery(id+"F0.wireOp",EDGE,"E1.10"),sQuery(id+"F0.wireOp",EDGE,"E2"),sQuery(id+"F0.wireOp",EDGE,"E3.2.0"),sQuery(id+"F0.wireOp",EDGE,"E3.3.0"),sQuery(id+"F0.wireOp",EDGE,"E3.4.0"),sQuery(id+"F0.wireOp",EDGE,"E3.5.0"),sQuery(id+"F0.wireOp",EDGE,"E3.6.0"),sQuery(id+"F0.wireOp",EDGE,"E3.7.0"),sQuery(id+"F0.wireOp",EDGE,"E3.8.0"),sQuery(id+"F0.wireOp",EDGE,"E3.9.0"),sQuery(id+"F0.wireOp",EDGE,"E3.10.0"),sQuery(id+"F0.wireOp",EDGE,"E4"),subQ0,sQuery(id+"F0.wireOp",EDGE,"E6"),sQuery(id+"F0.wireOp",EDGE,"E7"),sQuery(id+"F0.wireOp",EDGE,"E8"),sQuery(id+"F0.wireOp",EDGE,"E9"),sQuery(id+"F0.wireOp",EDGE,"E10"),sQuery(id+"F0.wireOp",EDGE,"E11"),sQuery(id+"F0.wireOp",EDGE,"E12"),sQuery(id+"F0.wireOp",EDGE,"E13"),sQuery(id+"F0.wireOp",EDGE,"E14"),sQuery(id+"F0.wireOp",EDGE,"E15"),sQuery(id+"F0.wireOp",EDGE,"E16"),sQuery(id+"F0.wireOp",EDGE,"E17"),sQuery(id+"F0.wireOp",EDGE,"E18.MirrorCS"),sQuery(id+"F0.wireOp",EDGE,"E19.MirrorCS"),sQuery(id+"F0.wireOp",EDGE,"E20.MirrorCS"),sQuery(id+"F0.wireOp",EDGE,"E21.MirrorCS"),sQuery(id+"F0.wireOp",EDGE,"E22.MirrorCS"),sQuery(id+"F0.wireOp",EDGE,"E23.MirrorCS"),sQuery(id+"F0.wireOp",EDGE,"E24.MirrorCS"),sQuery(id+"F0.wireOp",EDGE,"E25.MirrorCS"),sQuery(id+"F0.wireOp",EDGE,"E26.MirrorCS"),sQuery(id+"F0.wireOp",EDGE,"E27.MirrorCS"),sQuery(id+"F0.wireOp",EDGE,"E28.MirrorCS"),sQuery(id+"F0.wireOp",EDGE,"E29.MirrorCS"),sQuery(id+"F0.wireOp",EDGE,"E30.MirrorCS"),sQuery(id+"F0.wireOp",EDGE,"E31.MirrorCS")])],"isStart":false})],"blendedInto":[makeQuery(id+"F1.opExtrude","CAP_FACE",FACE,{"disambiguationData":[OSD([sQuery(id+"F0.wireOp",EDGE,"E0"),sQuery(id+"F0.wireOp",EDGE,"E1.0"),sQuery(id+"F0.wireOp",EDGE,"E1.1"),sQuery(id+"F0.wireOp",EDGE,"E1.2"),sQuery(id+"F0.wireOp",EDGE,"E1.3"),sQuery(id+"F0.wireOp",EDGE,"E1.4"),sQuery(id+"F0.wireOp",EDGE,"E1.5"),sQuery(id+"F0.wireOp",EDGE,"E1.6"),sQuery(id+"F0.wireOp",EDGE,"E1.7"),sQuery(id+"F0.wireOp",EDGE,"E1.8"),sQuery(id+"F0.wireOp",EDGE,"E1.9"),sQuery(id+"F0.wireOp",EDGE,"E1.10"),sQuery(id+"F0.wireOp",EDGE,"E2"),sQuery(id+"F0.wireOp",EDGE,"E3.2.0"),sQuery(id+"F0.wireOp",EDGE,"E3.3.0"),sQuery(id+"F0.wireOp",EDGE,"E3.4.0"),sQuery(id+"F0.wireOp",EDGE,"E3.5.0"),sQuery(id+"F0.wireOp",EDGE,"E3.6.0"),sQuery(id+"F0.wireOp",EDGE,"E3.7.0"),sQuery(id+"F0.wireOp",EDGE,"E3.8.0"),sQuery(id+"F0.wireOp",EDGE,"E3.9.0"),sQuery(id+"F0.wireOp",EDGE,"E3.10.0"),sQuery(id+"F0.wireOp",EDGE,"E4"),subQ0,sQuery(id+"F0.wireOp",EDGE,"E6"),sQuery(id+"F0.wireOp",EDGE,"E7"),sQuery(id+"F0.wireOp",EDGE,"E8"),sQuery(id+"F0.wireOp",EDGE,"E9"),sQuery(id+"F0.wireOp",EDGE,"E10"),sQuery(id+"F0.wireOp",EDGE,"E11"),sQuery(id+"F0.wireOp",EDGE,"E12"),sQuery(id+"F0.wireOp",EDGE,"E13"),sQuery(id+"F0.wireOp",EDGE,"E14"),sQuery(id+"F0.wireOp",EDGE,"E15"),sQuery(id+"F0.wireOp",EDGE,"E16"),sQuery(id+"F0.wireOp",EDGE,"E17"),sQuery(id+"F0.wireOp",EDGE,"E18.MirrorCS"),sQuery(id+"F0.wireOp",EDGE,"E19.MirrorCS"),sQuery(id+"F0.wireOp",EDGE,"E20.MirrorCS"),sQuery(id+"F0.wireOp",EDGE,"E21.MirrorCS"),sQuery(id+"F0.wireOp",EDGE,"E22.MirrorCS"),sQuery(id+"F0.wireOp",EDGE,"E23.MirrorCS"),sQuery(id+"F0.wireOp",EDGE,"E24.MirrorCS"),sQuery(id+"F0.wireOp",EDGE,"E25.MirrorCS"),sQuery(id+"F0.wireOp",EDGE,"E26.MirrorCS"),sQuery(id+"F0.wireOp",EDGE,"E27.MirrorCS"),sQuery(id+"F0.wireOp",EDGE,"E28.MirrorCS"),sQuery(id+"F0.wireOp",EDGE,"E29.MirrorCS"),sQuery(id+"F0.wireOp",EDGE,"E30.MirrorCS"),sQuery(id+"F0.wireOp",EDGE,"E31.MirrorCS")])],"isStart":false})]}),makeQuery(id+"F6.opExtrude","CAP_EDGE",EDGE,{"disambiguationData":[OSD([sQuery(id+"F5.wireOp",EDGE,"E40.0")])],"isStart":true})]});}
            var Q10;
            {var subQ0=sQuery(id+"F0.wireOp",EDGE,"E4");Q10=makeQuery(id+"F6.boolean.opBoolean","MERGE",EDGE,{"derivedFrom":[makeQuery(id+"F2.opFillet","BLEND_EDGE",EDGE,{"blendedFrom":[makeQuery(id+"F1.opExtrude","CAP_EDGE",EDGE,{"disambiguationData":[OSD([subQ0])],"isStart":false}),makeQuery(id+"F1.opExtrude","CAP_FACE",FACE,{"disambiguationData":[OSD([sQuery(id+"F0.wireOp",EDGE,"E0"),sQuery(id+"F0.wireOp",EDGE,"E1.0"),sQuery(id+"F0.wireOp",EDGE,"E1.1"),sQuery(id+"F0.wireOp",EDGE,"E1.2"),sQuery(id+"F0.wireOp",EDGE,"E1.3"),sQuery(id+"F0.wireOp",EDGE,"E1.4"),sQuery(id+"F0.wireOp",EDGE,"E1.5"),sQuery(id+"F0.wireOp",EDGE,"E1.6"),sQuery(id+"F0.wireOp",EDGE,"E1.7"),sQuery(id+"F0.wireOp",EDGE,"E1.8"),sQuery(id+"F0.wireOp",EDGE,"E1.9"),sQuery(id+"F0.wireOp",EDGE,"E1.10"),sQuery(id+"F0.wireOp",EDGE,"E2"),sQuery(id+"F0.wireOp",EDGE,"E3.2.0"),sQuery(id+"F0.wireOp",EDGE,"E3.3.0"),sQuery(id+"F0.wireOp",EDGE,"E3.4.0"),sQuery(id+"F0.wireOp",EDGE,"E3.5.0"),sQuery(id+"F0.wireOp",EDGE,"E3.6.0"),sQuery(id+"F0.wireOp",EDGE,"E3.7.0"),sQuery(id+"F0.wireOp",EDGE,"E3.8.0"),sQuery(id+"F0.wireOp",EDGE,"E3.9.0"),sQuery(id+"F0.wireOp",EDGE,"E3.10.0"),subQ0,sQuery(id+"F0.wireOp",EDGE,"E5"),sQuery(id+"F0.wireOp",EDGE,"E6"),sQuery(id+"F0.wireOp",EDGE,"E7"),sQuery(id+"F0.wireOp",EDGE,"E8"),sQuery(id+"F0.wireOp",EDGE,"E9"),sQuery(id+"F0.wireOp",EDGE,"E10"),sQuery(id+"F0.wireOp",EDGE,"E11"),sQuery(id+"F0.wireOp",EDGE,"E12"),sQuery(id+"F0.wireOp",EDGE,"E13"),sQuery(id+"F0.wireOp",EDGE,"E14"),sQuery(id+"F0.wireOp",EDGE,"E15"),sQuery(id+"F0.wireOp",EDGE,"E16"),sQuery(id+"F0.wireOp",EDGE,"E17"),sQuery(id+"F0.wireOp",EDGE,"E18.MirrorCS"),sQuery(id+"F0.wireOp",EDGE,"E19.MirrorCS"),sQuery(id+"F0.wireOp",EDGE,"E20.MirrorCS"),sQuery(id+"F0.wireOp",EDGE,"E21.MirrorCS"),sQuery(id+"F0.wireOp",EDGE,"E22.MirrorCS"),sQuery(id+"F0.wireOp",EDGE,"E23.MirrorCS"),sQuery(id+"F0.wireOp",EDGE,"E24.MirrorCS"),sQuery(id+"F0.wireOp",EDGE,"E25.MirrorCS"),sQuery(id+"F0.wireOp",EDGE,"E26.MirrorCS"),sQuery(id+"F0.wireOp",EDGE,"E27.MirrorCS"),sQuery(id+"F0.wireOp",EDGE,"E28.MirrorCS"),sQuery(id+"F0.wireOp",EDGE,"E29.MirrorCS"),sQuery(id+"F0.wireOp",EDGE,"E30.MirrorCS"),sQuery(id+"F0.wireOp",EDGE,"E31.MirrorCS")])],"isStart":false})],"blendedInto":[makeQuery(id+"F1.opExtrude","CAP_FACE",FACE,{"disambiguationData":[OSD([sQuery(id+"F0.wireOp",EDGE,"E0"),sQuery(id+"F0.wireOp",EDGE,"E1.0"),sQuery(id+"F0.wireOp",EDGE,"E1.1"),sQuery(id+"F0.wireOp",EDGE,"E1.2"),sQuery(id+"F0.wireOp",EDGE,"E1.3"),sQuery(id+"F0.wireOp",EDGE,"E1.4"),sQuery(id+"F0.wireOp",EDGE,"E1.5"),sQuery(id+"F0.wireOp",EDGE,"E1.6"),sQuery(id+"F0.wireOp",EDGE,"E1.7"),sQuery(id+"F0.wireOp",EDGE,"E1.8"),sQuery(id+"F0.wireOp",EDGE,"E1.9"),sQuery(id+"F0.wireOp",EDGE,"E1.10"),sQuery(id+"F0.wireOp",EDGE,"E2"),sQuery(id+"F0.wireOp",EDGE,"E3.2.0"),sQuery(id+"F0.wireOp",EDGE,"E3.3.0"),sQuery(id+"F0.wireOp",EDGE,"E3.4.0"),sQuery(id+"F0.wireOp",EDGE,"E3.5.0"),sQuery(id+"F0.wireOp",EDGE,"E3.6.0"),sQuery(id+"F0.wireOp",EDGE,"E3.7.0"),sQuery(id+"F0.wireOp",EDGE,"E3.8.0"),sQuery(id+"F0.wireOp",EDGE,"E3.9.0"),sQuery(id+"F0.wireOp",EDGE,"E3.10.0"),subQ0,sQuery(id+"F0.wireOp",EDGE,"E5"),sQuery(id+"F0.wireOp",EDGE,"E6"),sQuery(id+"F0.wireOp",EDGE,"E7"),sQuery(id+"F0.wireOp",EDGE,"E8"),sQuery(id+"F0.wireOp",EDGE,"E9"),sQuery(id+"F0.wireOp",EDGE,"E10"),sQuery(id+"F0.wireOp",EDGE,"E11"),sQuery(id+"F0.wireOp",EDGE,"E12"),sQuery(id+"F0.wireOp",EDGE,"E13"),sQuery(id+"F0.wireOp",EDGE,"E14"),sQuery(id+"F0.wireOp",EDGE,"E15"),sQuery(id+"F0.wireOp",EDGE,"E16"),sQuery(id+"F0.wireOp",EDGE,"E17"),sQuery(id+"F0.wireOp",EDGE,"E18.MirrorCS"),sQuery(id+"F0.wireOp",EDGE,"E19.MirrorCS"),sQuery(id+"F0.wireOp",EDGE,"E20.MirrorCS"),sQuery(id+"F0.wireOp",EDGE,"E21.MirrorCS"),sQuery(id+"F0.wireOp",EDGE,"E22.MirrorCS"),sQuery(id+"F0.wireOp",EDGE,"E23.MirrorCS"),sQuery(id+"F0.wireOp",EDGE,"E24.MirrorCS"),sQuery(id+"F0.wireOp",EDGE,"E25.MirrorCS"),sQuery(id+"F0.wireOp",EDGE,"E26.MirrorCS"),sQuery(id+"F0.wireOp",EDGE,"E27.MirrorCS"),sQuery(id+"F0.wireOp",EDGE,"E28.MirrorCS"),sQuery(id+"F0.wireOp",EDGE,"E29.MirrorCS"),sQuery(id+"F0.wireOp",EDGE,"E30.MirrorCS"),sQuery(id+"F0.wireOp",EDGE,"E31.MirrorCS")])],"isStart":false})]}),makeQuery(id+"F6.opExtrude","CAP_EDGE",EDGE,{"disambiguationData":[OSD([sQuery(id+"F5.wireOp",EDGE,"E38.0")])],"isStart":true})]});}
            var Q11;
            Q11=makeQuery(id+"F6.boolean.opBoolean","COPY",EDGE,{"derivedFrom":makeQuery(id+"F6.opExtrude","CAP_EDGE",EDGE,{"disambiguationData":[OSD([sQuery(id+"F5.wireOp",EDGE,"E38.0")])],"isStart":false})});
            var Q12;
            {var subQ0=sQuery(id+"F0.wireOp",EDGE,"E1.0");Q12=makeQuery(id+"F6.boolean.opBoolean","MERGE",EDGE,{"derivedFrom":[makeQuery(id+"F2.opFillet","BLEND_EDGE",EDGE,{"blendedFrom":[makeQuery(id+"F1.opExtrude","CAP_EDGE",EDGE,{"disambiguationData":[OSD([subQ0])],"isStart":false}),makeQuery(id+"F1.opExtrude","CAP_FACE",FACE,{"disambiguationData":[OSD([sQuery(id+"F0.wireOp",EDGE,"E0"),subQ0,sQuery(id+"F0.wireOp",EDGE,"E1.1"),sQuery(id+"F0.wireOp",EDGE,"E1.2"),sQuery(id+"F0.wireOp",EDGE,"E1.3"),sQuery(id+"F0.wireOp",EDGE,"E1.4"),sQuery(id+"F0.wireOp",EDGE,"E1.5"),sQuery(id+"F0.wireOp",EDGE,"E1.6"),sQuery(id+"F0.wireOp",EDGE,"E1.7"),sQuery(id+"F0.wireOp",EDGE,"E1.8"),sQuery(id+"F0.wireOp",EDGE,"E1.9"),sQuery(id+"F0.wireOp",EDGE,"E1.10"),sQuery(id+"F0.wireOp",EDGE,"E2"),sQuery(id+"F0.wireOp",EDGE,"E3.2.0"),sQuery(id+"F0.wireOp",EDGE,"E3.3.0"),sQuery(id+"F0.wireOp",EDGE,"E3.4.0"),sQuery(id+"F0.wireOp",EDGE,"E3.5.0"),sQuery(id+"F0.wireOp",EDGE,"E3.6.0"),sQuery(id+"F0.wireOp",EDGE,"E3.7.0"),sQuery(id+"F0.wireOp",EDGE,"E3.8.0"),sQuery(id+"F0.wireOp",EDGE,"E3.9.0"),sQuery(id+"F0.wireOp",EDGE,"E3.10.0"),sQuery(id+"F0.wireOp",EDGE,"E4"),sQuery(id+"F0.wireOp",EDGE,"E5"),sQuery(id+"F0.wireOp",EDGE,"E6"),sQuery(id+"F0.wireOp",EDGE,"E7"),sQuery(id+"F0.wireOp",EDGE,"E8"),sQuery(id+"F0.wireOp",EDGE,"E9"),sQuery(id+"F0.wireOp",EDGE,"E10"),sQuery(id+"F0.wireOp",EDGE,"E11"),sQuery(id+"F0.wireOp",EDGE,"E12"),sQuery(id+"F0.wireOp",EDGE,"E13"),sQuery(id+"F0.wireOp",EDGE,"E14"),sQuery(id+"F0.wireOp",EDGE,"E15"),sQuery(id+"F0.wireOp",EDGE,"E16"),sQuery(id+"F0.wireOp",EDGE,"E17"),sQuery(id+"F0.wireOp",EDGE,"E18.MirrorCS"),sQuery(id+"F0.wireOp",EDGE,"E19.MirrorCS"),sQuery(id+"F0.wireOp",EDGE,"E20.MirrorCS"),sQuery(id+"F0.wireOp",EDGE,"E21.MirrorCS"),sQuery(id+"F0.wireOp",EDGE,"E22.MirrorCS"),sQuery(id+"F0.wireOp",EDGE,"E23.MirrorCS"),sQuery(id+"F0.wireOp",EDGE,"E24.MirrorCS"),sQuery(id+"F0.wireOp",EDGE,"E25.MirrorCS"),sQuery(id+"F0.wireOp",EDGE,"E26.MirrorCS"),sQuery(id+"F0.wireOp",EDGE,"E27.MirrorCS"),sQuery(id+"F0.wireOp",EDGE,"E28.MirrorCS"),sQuery(id+"F0.wireOp",EDGE,"E29.MirrorCS"),sQuery(id+"F0.wireOp",EDGE,"E30.MirrorCS"),sQuery(id+"F0.wireOp",EDGE,"E31.MirrorCS")])],"isStart":false})],"blendedInto":[makeQuery(id+"F1.opExtrude","CAP_FACE",FACE,{"disambiguationData":[OSD([sQuery(id+"F0.wireOp",EDGE,"E0"),subQ0,sQuery(id+"F0.wireOp",EDGE,"E1.1"),sQuery(id+"F0.wireOp",EDGE,"E1.2"),sQuery(id+"F0.wireOp",EDGE,"E1.3"),sQuery(id+"F0.wireOp",EDGE,"E1.4"),sQuery(id+"F0.wireOp",EDGE,"E1.5"),sQuery(id+"F0.wireOp",EDGE,"E1.6"),sQuery(id+"F0.wireOp",EDGE,"E1.7"),sQuery(id+"F0.wireOp",EDGE,"E1.8"),sQuery(id+"F0.wireOp",EDGE,"E1.9"),sQuery(id+"F0.wireOp",EDGE,"E1.10"),sQuery(id+"F0.wireOp",EDGE,"E2"),sQuery(id+"F0.wireOp",EDGE,"E3.2.0"),sQuery(id+"F0.wireOp",EDGE,"E3.3.0"),sQuery(id+"F0.wireOp",EDGE,"E3.4.0"),sQuery(id+"F0.wireOp",EDGE,"E3.5.0"),sQuery(id+"F0.wireOp",EDGE,"E3.6.0"),sQuery(id+"F0.wireOp",EDGE,"E3.7.0"),sQuery(id+"F0.wireOp",EDGE,"E3.8.0"),sQuery(id+"F0.wireOp",EDGE,"E3.9.0"),sQuery(id+"F0.wireOp",EDGE,"E3.10.0"),sQuery(id+"F0.wireOp",EDGE,"E4"),sQuery(id+"F0.wireOp",EDGE,"E5"),sQuery(id+"F0.wireOp",EDGE,"E6"),sQuery(id+"F0.wireOp",EDGE,"E7"),sQuery(id+"F0.wireOp",EDGE,"E8"),sQuery(id+"F0.wireOp",EDGE,"E9"),sQuery(id+"F0.wireOp",EDGE,"E10"),sQuery(id+"F0.wireOp",EDGE,"E11"),sQuery(id+"F0.wireOp",EDGE,"E12"),sQuery(id+"F0.wireOp",EDGE,"E13"),sQuery(id+"F0.wireOp",EDGE,"E14"),sQuery(id+"F0.wireOp",EDGE,"E15"),sQuery(id+"F0.wireOp",EDGE,"E16"),sQuery(id+"F0.wireOp",EDGE,"E17"),sQuery(id+"F0.wireOp",EDGE,"E18.MirrorCS"),sQuery(id+"F0.wireOp",EDGE,"E19.MirrorCS"),sQuery(id+"F0.wireOp",EDGE,"E20.MirrorCS"),sQuery(id+"F0.wireOp",EDGE,"E21.MirrorCS"),sQuery(id+"F0.wireOp",EDGE,"E22.MirrorCS"),sQuery(id+"F0.wireOp",EDGE,"E23.MirrorCS"),sQuery(id+"F0.wireOp",EDGE,"E24.MirrorCS"),sQuery(id+"F0.wireOp",EDGE,"E25.MirrorCS"),sQuery(id+"F0.wireOp",EDGE,"E26.MirrorCS"),sQuery(id+"F0.wireOp",EDGE,"E27.MirrorCS"),sQuery(id+"F0.wireOp",EDGE,"E28.MirrorCS"),sQuery(id+"F0.wireOp",EDGE,"E29.MirrorCS"),sQuery(id+"F0.wireOp",EDGE,"E30.MirrorCS"),sQuery(id+"F0.wireOp",EDGE,"E31.MirrorCS")])],"isStart":false})]}),makeQuery(id+"F6.opExtrude","CAP_EDGE",EDGE,{"disambiguationData":[OSD([sQuery(id+"F5.wireOp",EDGE,"E37.0")])],"isStart":true})]});}
            var Q13;
            Q13=makeQuery(id+"F6.boolean.opBoolean","COPY",EDGE,{"derivedFrom":makeQuery(id+"F6.opExtrude","CAP_EDGE",EDGE,{"disambiguationData":[OSD([sQuery(id+"F5.wireOp",EDGE,"E37.0")])],"isStart":false})});
            var Q14;
            {var subQ0=sQuery(id+"F0.wireOp",EDGE,"E2");Q14=makeQuery(id+"F6.boolean.opBoolean","MERGE",EDGE,{"derivedFrom":[makeQuery(id+"F2.opFillet","BLEND_EDGE",EDGE,{"blendedFrom":[makeQuery(id+"F1.opExtrude","CAP_EDGE",EDGE,{"disambiguationData":[OSD([subQ0])],"isStart":false}),makeQuery(id+"F1.opExtrude","CAP_FACE",FACE,{"disambiguationData":[OSD([sQuery(id+"F0.wireOp",EDGE,"E0"),sQuery(id+"F0.wireOp",EDGE,"E1.0"),sQuery(id+"F0.wireOp",EDGE,"E1.1"),sQuery(id+"F0.wireOp",EDGE,"E1.2"),sQuery(id+"F0.wireOp",EDGE,"E1.3"),sQuery(id+"F0.wireOp",EDGE,"E1.4"),sQuery(id+"F0.wireOp",EDGE,"E1.5"),sQuery(id+"F0.wireOp",EDGE,"E1.6"),sQuery(id+"F0.wireOp",EDGE,"E1.7"),sQuery(id+"F0.wireOp",EDGE,"E1.8"),sQuery(id+"F0.wireOp",EDGE,"E1.9"),sQuery(id+"F0.wireOp",EDGE,"E1.10"),subQ0,sQuery(id+"F0.wireOp",EDGE,"E3.2.0"),sQuery(id+"F0.wireOp",EDGE,"E3.3.0"),sQuery(id+"F0.wireOp",EDGE,"E3.4.0"),sQuery(id+"F0.wireOp",EDGE,"E3.5.0"),sQuery(id+"F0.wireOp",EDGE,"E3.6.0"),sQuery(id+"F0.wireOp",EDGE,"E3.7.0"),sQuery(id+"F0.wireOp",EDGE,"E3.8.0"),sQuery(id+"F0.wireOp",EDGE,"E3.9.0"),sQuery(id+"F0.wireOp",EDGE,"E3.10.0"),sQuery(id+"F0.wireOp",EDGE,"E4"),sQuery(id+"F0.wireOp",EDGE,"E5"),sQuery(id+"F0.wireOp",EDGE,"E6"),sQuery(id+"F0.wireOp",EDGE,"E7"),sQuery(id+"F0.wireOp",EDGE,"E8"),sQuery(id+"F0.wireOp",EDGE,"E9"),sQuery(id+"F0.wireOp",EDGE,"E10"),sQuery(id+"F0.wireOp",EDGE,"E11"),sQuery(id+"F0.wireOp",EDGE,"E12"),sQuery(id+"F0.wireOp",EDGE,"E13"),sQuery(id+"F0.wireOp",EDGE,"E14"),sQuery(id+"F0.wireOp",EDGE,"E15"),sQuery(id+"F0.wireOp",EDGE,"E16"),sQuery(id+"F0.wireOp",EDGE,"E17"),sQuery(id+"F0.wireOp",EDGE,"E18.MirrorCS"),sQuery(id+"F0.wireOp",EDGE,"E19.MirrorCS"),sQuery(id+"F0.wireOp",EDGE,"E20.MirrorCS"),sQuery(id+"F0.wireOp",EDGE,"E21.MirrorCS"),sQuery(id+"F0.wireOp",EDGE,"E22.MirrorCS"),sQuery(id+"F0.wireOp",EDGE,"E23.MirrorCS"),sQuery(id+"F0.wireOp",EDGE,"E24.MirrorCS"),sQuery(id+"F0.wireOp",EDGE,"E25.MirrorCS"),sQuery(id+"F0.wireOp",EDGE,"E26.MirrorCS"),sQuery(id+"F0.wireOp",EDGE,"E27.MirrorCS"),sQuery(id+"F0.wireOp",EDGE,"E28.MirrorCS"),sQuery(id+"F0.wireOp",EDGE,"E29.MirrorCS"),sQuery(id+"F0.wireOp",EDGE,"E30.MirrorCS"),sQuery(id+"F0.wireOp",EDGE,"E31.MirrorCS")])],"isStart":false})],"blendedInto":[makeQuery(id+"F1.opExtrude","CAP_FACE",FACE,{"disambiguationData":[OSD([sQuery(id+"F0.wireOp",EDGE,"E0"),sQuery(id+"F0.wireOp",EDGE,"E1.0"),sQuery(id+"F0.wireOp",EDGE,"E1.1"),sQuery(id+"F0.wireOp",EDGE,"E1.2"),sQuery(id+"F0.wireOp",EDGE,"E1.3"),sQuery(id+"F0.wireOp",EDGE,"E1.4"),sQuery(id+"F0.wireOp",EDGE,"E1.5"),sQuery(id+"F0.wireOp",EDGE,"E1.6"),sQuery(id+"F0.wireOp",EDGE,"E1.7"),sQuery(id+"F0.wireOp",EDGE,"E1.8"),sQuery(id+"F0.wireOp",EDGE,"E1.9"),sQuery(id+"F0.wireOp",EDGE,"E1.10"),subQ0,sQuery(id+"F0.wireOp",EDGE,"E3.2.0"),sQuery(id+"F0.wireOp",EDGE,"E3.3.0"),sQuery(id+"F0.wireOp",EDGE,"E3.4.0"),sQuery(id+"F0.wireOp",EDGE,"E3.5.0"),sQuery(id+"F0.wireOp",EDGE,"E3.6.0"),sQuery(id+"F0.wireOp",EDGE,"E3.7.0"),sQuery(id+"F0.wireOp",EDGE,"E3.8.0"),sQuery(id+"F0.wireOp",EDGE,"E3.9.0"),sQuery(id+"F0.wireOp",EDGE,"E3.10.0"),sQuery(id+"F0.wireOp",EDGE,"E4"),sQuery(id+"F0.wireOp",EDGE,"E5"),sQuery(id+"F0.wireOp",EDGE,"E6"),sQuery(id+"F0.wireOp",EDGE,"E7"),sQuery(id+"F0.wireOp",EDGE,"E8"),sQuery(id+"F0.wireOp",EDGE,"E9"),sQuery(id+"F0.wireOp",EDGE,"E10"),sQuery(id+"F0.wireOp",EDGE,"E11"),sQuery(id+"F0.wireOp",EDGE,"E12"),sQuery(id+"F0.wireOp",EDGE,"E13"),sQuery(id+"F0.wireOp",EDGE,"E14"),sQuery(id+"F0.wireOp",EDGE,"E15"),sQuery(id+"F0.wireOp",EDGE,"E16"),sQuery(id+"F0.wireOp",EDGE,"E17"),sQuery(id+"F0.wireOp",EDGE,"E18.MirrorCS"),sQuery(id+"F0.wireOp",EDGE,"E19.MirrorCS"),sQuery(id+"F0.wireOp",EDGE,"E20.MirrorCS"),sQuery(id+"F0.wireOp",EDGE,"E21.MirrorCS"),sQuery(id+"F0.wireOp",EDGE,"E22.MirrorCS"),sQuery(id+"F0.wireOp",EDGE,"E23.MirrorCS"),sQuery(id+"F0.wireOp",EDGE,"E24.MirrorCS"),sQuery(id+"F0.wireOp",EDGE,"E25.MirrorCS"),sQuery(id+"F0.wireOp",EDGE,"E26.MirrorCS"),sQuery(id+"F0.wireOp",EDGE,"E27.MirrorCS"),sQuery(id+"F0.wireOp",EDGE,"E28.MirrorCS"),sQuery(id+"F0.wireOp",EDGE,"E29.MirrorCS"),sQuery(id+"F0.wireOp",EDGE,"E30.MirrorCS"),sQuery(id+"F0.wireOp",EDGE,"E31.MirrorCS")])],"isStart":false})]}),makeQuery(id+"F6.opExtrude","CAP_EDGE",EDGE,{"disambiguationData":[OSD([sQuery(id+"F5.wireOp",EDGE,"E36.0")])],"isStart":true})]});}
            var Q15;
            Q15=makeQuery(id+"F6.boolean.opBoolean","COPY",EDGE,{"derivedFrom":makeQuery(id+"F6.opExtrude","CAP_EDGE",EDGE,{"disambiguationData":[OSD([sQuery(id+"F5.wireOp",EDGE,"E36.0")])],"isStart":false})});
            var Q16;
            {var subQ0=sQuery(id+"F0.wireOp",EDGE,"E1.1");Q16=makeQuery(id+"F6.boolean.opBoolean","MERGE",EDGE,{"derivedFrom":[makeQuery(id+"F2.opFillet","BLEND_EDGE",EDGE,{"blendedFrom":[makeQuery(id+"F1.opExtrude","CAP_EDGE",EDGE,{"disambiguationData":[OSD([subQ0])],"isStart":false}),makeQuery(id+"F1.opExtrude","CAP_FACE",FACE,{"disambiguationData":[OSD([sQuery(id+"F0.wireOp",EDGE,"E0"),sQuery(id+"F0.wireOp",EDGE,"E1.0"),subQ0,sQuery(id+"F0.wireOp",EDGE,"E1.2"),sQuery(id+"F0.wireOp",EDGE,"E1.3"),sQuery(id+"F0.wireOp",EDGE,"E1.4"),sQuery(id+"F0.wireOp",EDGE,"E1.5"),sQuery(id+"F0.wireOp",EDGE,"E1.6"),sQuery(id+"F0.wireOp",EDGE,"E1.7"),sQuery(id+"F0.wireOp",EDGE,"E1.8"),sQuery(id+"F0.wireOp",EDGE,"E1.9"),sQuery(id+"F0.wireOp",EDGE,"E1.10"),sQuery(id+"F0.wireOp",EDGE,"E2"),sQuery(id+"F0.wireOp",EDGE,"E3.2.0"),sQuery(id+"F0.wireOp",EDGE,"E3.3.0"),sQuery(id+"F0.wireOp",EDGE,"E3.4.0"),sQuery(id+"F0.wireOp",EDGE,"E3.5.0"),sQuery(id+"F0.wireOp",EDGE,"E3.6.0"),sQuery(id+"F0.wireOp",EDGE,"E3.7.0"),sQuery(id+"F0.wireOp",EDGE,"E3.8.0"),sQuery(id+"F0.wireOp",EDGE,"E3.9.0"),sQuery(id+"F0.wireOp",EDGE,"E3.10.0"),sQuery(id+"F0.wireOp",EDGE,"E4"),sQuery(id+"F0.wireOp",EDGE,"E5"),sQuery(id+"F0.wireOp",EDGE,"E6"),sQuery(id+"F0.wireOp",EDGE,"E7"),sQuery(id+"F0.wireOp",EDGE,"E8"),sQuery(id+"F0.wireOp",EDGE,"E9"),sQuery(id+"F0.wireOp",EDGE,"E10"),sQuery(id+"F0.wireOp",EDGE,"E11"),sQuery(id+"F0.wireOp",EDGE,"E12"),sQuery(id+"F0.wireOp",EDGE,"E13"),sQuery(id+"F0.wireOp",EDGE,"E14"),sQuery(id+"F0.wireOp",EDGE,"E15"),sQuery(id+"F0.wireOp",EDGE,"E16"),sQuery(id+"F0.wireOp",EDGE,"E17"),sQuery(id+"F0.wireOp",EDGE,"E18.MirrorCS"),sQuery(id+"F0.wireOp",EDGE,"E19.MirrorCS"),sQuery(id+"F0.wireOp",EDGE,"E20.MirrorCS"),sQuery(id+"F0.wireOp",EDGE,"E21.MirrorCS"),sQuery(id+"F0.wireOp",EDGE,"E22.MirrorCS"),sQuery(id+"F0.wireOp",EDGE,"E23.MirrorCS"),sQuery(id+"F0.wireOp",EDGE,"E24.MirrorCS"),sQuery(id+"F0.wireOp",EDGE,"E25.MirrorCS"),sQuery(id+"F0.wireOp",EDGE,"E26.MirrorCS"),sQuery(id+"F0.wireOp",EDGE,"E27.MirrorCS"),sQuery(id+"F0.wireOp",EDGE,"E28.MirrorCS"),sQuery(id+"F0.wireOp",EDGE,"E29.MirrorCS"),sQuery(id+"F0.wireOp",EDGE,"E30.MirrorCS"),sQuery(id+"F0.wireOp",EDGE,"E31.MirrorCS")])],"isStart":false})],"blendedInto":[makeQuery(id+"F1.opExtrude","CAP_FACE",FACE,{"disambiguationData":[OSD([sQuery(id+"F0.wireOp",EDGE,"E0"),sQuery(id+"F0.wireOp",EDGE,"E1.0"),subQ0,sQuery(id+"F0.wireOp",EDGE,"E1.2"),sQuery(id+"F0.wireOp",EDGE,"E1.3"),sQuery(id+"F0.wireOp",EDGE,"E1.4"),sQuery(id+"F0.wireOp",EDGE,"E1.5"),sQuery(id+"F0.wireOp",EDGE,"E1.6"),sQuery(id+"F0.wireOp",EDGE,"E1.7"),sQuery(id+"F0.wireOp",EDGE,"E1.8"),sQuery(id+"F0.wireOp",EDGE,"E1.9"),sQuery(id+"F0.wireOp",EDGE,"E1.10"),sQuery(id+"F0.wireOp",EDGE,"E2"),sQuery(id+"F0.wireOp",EDGE,"E3.2.0"),sQuery(id+"F0.wireOp",EDGE,"E3.3.0"),sQuery(id+"F0.wireOp",EDGE,"E3.4.0"),sQuery(id+"F0.wireOp",EDGE,"E3.5.0"),sQuery(id+"F0.wireOp",EDGE,"E3.6.0"),sQuery(id+"F0.wireOp",EDGE,"E3.7.0"),sQuery(id+"F0.wireOp",EDGE,"E3.8.0"),sQuery(id+"F0.wireOp",EDGE,"E3.9.0"),sQuery(id+"F0.wireOp",EDGE,"E3.10.0"),sQuery(id+"F0.wireOp",EDGE,"E4"),sQuery(id+"F0.wireOp",EDGE,"E5"),sQuery(id+"F0.wireOp",EDGE,"E6"),sQuery(id+"F0.wireOp",EDGE,"E7"),sQuery(id+"F0.wireOp",EDGE,"E8"),sQuery(id+"F0.wireOp",EDGE,"E9"),sQuery(id+"F0.wireOp",EDGE,"E10"),sQuery(id+"F0.wireOp",EDGE,"E11"),sQuery(id+"F0.wireOp",EDGE,"E12"),sQuery(id+"F0.wireOp",EDGE,"E13"),sQuery(id+"F0.wireOp",EDGE,"E14"),sQuery(id+"F0.wireOp",EDGE,"E15"),sQuery(id+"F0.wireOp",EDGE,"E16"),sQuery(id+"F0.wireOp",EDGE,"E17"),sQuery(id+"F0.wireOp",EDGE,"E18.MirrorCS"),sQuery(id+"F0.wireOp",EDGE,"E19.MirrorCS"),sQuery(id+"F0.wireOp",EDGE,"E20.MirrorCS"),sQuery(id+"F0.wireOp",EDGE,"E21.MirrorCS"),sQuery(id+"F0.wireOp",EDGE,"E22.MirrorCS"),sQuery(id+"F0.wireOp",EDGE,"E23.MirrorCS"),sQuery(id+"F0.wireOp",EDGE,"E24.MirrorCS"),sQuery(id+"F0.wireOp",EDGE,"E25.MirrorCS"),sQuery(id+"F0.wireOp",EDGE,"E26.MirrorCS"),sQuery(id+"F0.wireOp",EDGE,"E27.MirrorCS"),sQuery(id+"F0.wireOp",EDGE,"E28.MirrorCS"),sQuery(id+"F0.wireOp",EDGE,"E29.MirrorCS"),sQuery(id+"F0.wireOp",EDGE,"E30.MirrorCS"),sQuery(id+"F0.wireOp",EDGE,"E31.MirrorCS")])],"isStart":false})]}),makeQuery(id+"F6.opExtrude","CAP_EDGE",EDGE,{"disambiguationData":[OSD([sQuery(id+"F5.wireOp",EDGE,"E62.0")])],"isStart":true})]});}
            var Q17;
            Q17=makeQuery(id+"F6.boolean.opBoolean","COPY",EDGE,{"derivedFrom":makeQuery(id+"F6.opExtrude","CAP_EDGE",EDGE,{"disambiguationData":[OSD([sQuery(id+"F5.wireOp",EDGE,"E62.0")])],"isStart":false})});
            var Q18;
            {var subQ0=sQuery(id+"F0.wireOp",EDGE,"E3.10.0");Q18=makeQuery(id+"F6.boolean.opBoolean","MERGE",EDGE,{"derivedFrom":[makeQuery(id+"F2.opFillet","BLEND_EDGE",EDGE,{"blendedFrom":[makeQuery(id+"F1.opExtrude","CAP_EDGE",EDGE,{"disambiguationData":[OSD([subQ0])],"isStart":false}),makeQuery(id+"F1.opExtrude","CAP_FACE",FACE,{"disambiguationData":[OSD([sQuery(id+"F0.wireOp",EDGE,"E0"),sQuery(id+"F0.wireOp",EDGE,"E1.0"),sQuery(id+"F0.wireOp",EDGE,"E1.1"),sQuery(id+"F0.wireOp",EDGE,"E1.2"),sQuery(id+"F0.wireOp",EDGE,"E1.3"),sQuery(id+"F0.wireOp",EDGE,"E1.4"),sQuery(id+"F0.wireOp",EDGE,"E1.5"),sQuery(id+"F0.wireOp",EDGE,"E1.6"),sQuery(id+"F0.wireOp",EDGE,"E1.7"),sQuery(id+"F0.wireOp",EDGE,"E1.8"),sQuery(id+"F0.wireOp",EDGE,"E1.9"),sQuery(id+"F0.wireOp",EDGE,"E1.10"),sQuery(id+"F0.wireOp",EDGE,"E2"),sQuery(id+"F0.wireOp",EDGE,"E3.2.0"),sQuery(id+"F0.wireOp",EDGE,"E3.3.0"),sQuery(id+"F0.wireOp",EDGE,"E3.4.0"),sQuery(id+"F0.wireOp",EDGE,"E3.5.0"),sQuery(id+"F0.wireOp",EDGE,"E3.6.0"),sQuery(id+"F0.wireOp",EDGE,"E3.7.0"),sQuery(id+"F0.wireOp",EDGE,"E3.8.0"),sQuery(id+"F0.wireOp",EDGE,"E3.9.0"),subQ0,sQuery(id+"F0.wireOp",EDGE,"E4"),sQuery(id+"F0.wireOp",EDGE,"E5"),sQuery(id+"F0.wireOp",EDGE,"E6"),sQuery(id+"F0.wireOp",EDGE,"E7"),sQuery(id+"F0.wireOp",EDGE,"E8"),sQuery(id+"F0.wireOp",EDGE,"E9"),sQuery(id+"F0.wireOp",EDGE,"E10"),sQuery(id+"F0.wireOp",EDGE,"E11"),sQuery(id+"F0.wireOp",EDGE,"E12"),sQuery(id+"F0.wireOp",EDGE,"E13"),sQuery(id+"F0.wireOp",EDGE,"E14"),sQuery(id+"F0.wireOp",EDGE,"E15"),sQuery(id+"F0.wireOp",EDGE,"E16"),sQuery(id+"F0.wireOp",EDGE,"E17"),sQuery(id+"F0.wireOp",EDGE,"E18.MirrorCS"),sQuery(id+"F0.wireOp",EDGE,"E19.MirrorCS"),sQuery(id+"F0.wireOp",EDGE,"E20.MirrorCS"),sQuery(id+"F0.wireOp",EDGE,"E21.MirrorCS"),sQuery(id+"F0.wireOp",EDGE,"E22.MirrorCS"),sQuery(id+"F0.wireOp",EDGE,"E23.MirrorCS"),sQuery(id+"F0.wireOp",EDGE,"E24.MirrorCS"),sQuery(id+"F0.wireOp",EDGE,"E25.MirrorCS"),sQuery(id+"F0.wireOp",EDGE,"E26.MirrorCS"),sQuery(id+"F0.wireOp",EDGE,"E27.MirrorCS"),sQuery(id+"F0.wireOp",EDGE,"E28.MirrorCS"),sQuery(id+"F0.wireOp",EDGE,"E29.MirrorCS"),sQuery(id+"F0.wireOp",EDGE,"E30.MirrorCS"),sQuery(id+"F0.wireOp",EDGE,"E31.MirrorCS")])],"isStart":false})],"blendedInto":[makeQuery(id+"F1.opExtrude","CAP_FACE",FACE,{"disambiguationData":[OSD([sQuery(id+"F0.wireOp",EDGE,"E0"),sQuery(id+"F0.wireOp",EDGE,"E1.0"),sQuery(id+"F0.wireOp",EDGE,"E1.1"),sQuery(id+"F0.wireOp",EDGE,"E1.2"),sQuery(id+"F0.wireOp",EDGE,"E1.3"),sQuery(id+"F0.wireOp",EDGE,"E1.4"),sQuery(id+"F0.wireOp",EDGE,"E1.5"),sQuery(id+"F0.wireOp",EDGE,"E1.6"),sQuery(id+"F0.wireOp",EDGE,"E1.7"),sQuery(id+"F0.wireOp",EDGE,"E1.8"),sQuery(id+"F0.wireOp",EDGE,"E1.9"),sQuery(id+"F0.wireOp",EDGE,"E1.10"),sQuery(id+"F0.wireOp",EDGE,"E2"),sQuery(id+"F0.wireOp",EDGE,"E3.2.0"),sQuery(id+"F0.wireOp",EDGE,"E3.3.0"),sQuery(id+"F0.wireOp",EDGE,"E3.4.0"),sQuery(id+"F0.wireOp",EDGE,"E3.5.0"),sQuery(id+"F0.wireOp",EDGE,"E3.6.0"),sQuery(id+"F0.wireOp",EDGE,"E3.7.0"),sQuery(id+"F0.wireOp",EDGE,"E3.8.0"),sQuery(id+"F0.wireOp",EDGE,"E3.9.0"),subQ0,sQuery(id+"F0.wireOp",EDGE,"E4"),sQuery(id+"F0.wireOp",EDGE,"E5"),sQuery(id+"F0.wireOp",EDGE,"E6"),sQuery(id+"F0.wireOp",EDGE,"E7"),sQuery(id+"F0.wireOp",EDGE,"E8"),sQuery(id+"F0.wireOp",EDGE,"E9"),sQuery(id+"F0.wireOp",EDGE,"E10"),sQuery(id+"F0.wireOp",EDGE,"E11"),sQuery(id+"F0.wireOp",EDGE,"E12"),sQuery(id+"F0.wireOp",EDGE,"E13"),sQuery(id+"F0.wireOp",EDGE,"E14"),sQuery(id+"F0.wireOp",EDGE,"E15"),sQuery(id+"F0.wireOp",EDGE,"E16"),sQuery(id+"F0.wireOp",EDGE,"E17"),sQuery(id+"F0.wireOp",EDGE,"E18.MirrorCS"),sQuery(id+"F0.wireOp",EDGE,"E19.MirrorCS"),sQuery(id+"F0.wireOp",EDGE,"E20.MirrorCS"),sQuery(id+"F0.wireOp",EDGE,"E21.MirrorCS"),sQuery(id+"F0.wireOp",EDGE,"E22.MirrorCS"),sQuery(id+"F0.wireOp",EDGE,"E23.MirrorCS"),sQuery(id+"F0.wireOp",EDGE,"E24.MirrorCS"),sQuery(id+"F0.wireOp",EDGE,"E25.MirrorCS"),sQuery(id+"F0.wireOp",EDGE,"E26.MirrorCS"),sQuery(id+"F0.wireOp",EDGE,"E27.MirrorCS"),sQuery(id+"F0.wireOp",EDGE,"E28.MirrorCS"),sQuery(id+"F0.wireOp",EDGE,"E29.MirrorCS"),sQuery(id+"F0.wireOp",EDGE,"E30.MirrorCS"),sQuery(id+"F0.wireOp",EDGE,"E31.MirrorCS")])],"isStart":false})]}),makeQuery(id+"F6.opExtrude","CAP_EDGE",EDGE,{"disambiguationData":[OSD([sQuery(id+"F5.wireOp",EDGE,"E61.0")])],"isStart":true})]});}
            var Q19;
            Q19=makeQuery(id+"F6.boolean.opBoolean","COPY",EDGE,{"derivedFrom":makeQuery(id+"F6.opExtrude","CAP_EDGE",EDGE,{"disambiguationData":[OSD([sQuery(id+"F5.wireOp",EDGE,"E61.0")])],"isStart":false})});
            var Q20;
            {var subQ0=sQuery(id+"F0.wireOp",EDGE,"E1.2");Q20=makeQuery(id+"F6.boolean.opBoolean","MERGE",EDGE,{"derivedFrom":[makeQuery(id+"F2.opFillet","BLEND_EDGE",EDGE,{"blendedFrom":[makeQuery(id+"F1.opExtrude","CAP_EDGE",EDGE,{"disambiguationData":[OSD([subQ0])],"isStart":false}),makeQuery(id+"F1.opExtrude","CAP_FACE",FACE,{"disambiguationData":[OSD([sQuery(id+"F0.wireOp",EDGE,"E0"),sQuery(id+"F0.wireOp",EDGE,"E1.0"),sQuery(id+"F0.wireOp",EDGE,"E1.1"),subQ0,sQuery(id+"F0.wireOp",EDGE,"E1.3"),sQuery(id+"F0.wireOp",EDGE,"E1.4"),sQuery(id+"F0.wireOp",EDGE,"E1.5"),sQuery(id+"F0.wireOp",EDGE,"E1.6"),sQuery(id+"F0.wireOp",EDGE,"E1.7"),sQuery(id+"F0.wireOp",EDGE,"E1.8"),sQuery(id+"F0.wireOp",EDGE,"E1.9"),sQuery(id+"F0.wireOp",EDGE,"E1.10"),sQuery(id+"F0.wireOp",EDGE,"E2"),sQuery(id+"F0.wireOp",EDGE,"E3.2.0"),sQuery(id+"F0.wireOp",EDGE,"E3.3.0"),sQuery(id+"F0.wireOp",EDGE,"E3.4.0"),sQuery(id+"F0.wireOp",EDGE,"E3.5.0"),sQuery(id+"F0.wireOp",EDGE,"E3.6.0"),sQuery(id+"F0.wireOp",EDGE,"E3.7.0"),sQuery(id+"F0.wireOp",EDGE,"E3.8.0"),sQuery(id+"F0.wireOp",EDGE,"E3.9.0"),sQuery(id+"F0.wireOp",EDGE,"E3.10.0"),sQuery(id+"F0.wireOp",EDGE,"E4"),sQuery(id+"F0.wireOp",EDGE,"E5"),sQuery(id+"F0.wireOp",EDGE,"E6"),sQuery(id+"F0.wireOp",EDGE,"E7"),sQuery(id+"F0.wireOp",EDGE,"E8"),sQuery(id+"F0.wireOp",EDGE,"E9"),sQuery(id+"F0.wireOp",EDGE,"E10"),sQuery(id+"F0.wireOp",EDGE,"E11"),sQuery(id+"F0.wireOp",EDGE,"E12"),sQuery(id+"F0.wireOp",EDGE,"E13"),sQuery(id+"F0.wireOp",EDGE,"E14"),sQuery(id+"F0.wireOp",EDGE,"E15"),sQuery(id+"F0.wireOp",EDGE,"E16"),sQuery(id+"F0.wireOp",EDGE,"E17"),sQuery(id+"F0.wireOp",EDGE,"E18.MirrorCS"),sQuery(id+"F0.wireOp",EDGE,"E19.MirrorCS"),sQuery(id+"F0.wireOp",EDGE,"E20.MirrorCS"),sQuery(id+"F0.wireOp",EDGE,"E21.MirrorCS"),sQuery(id+"F0.wireOp",EDGE,"E22.MirrorCS"),sQuery(id+"F0.wireOp",EDGE,"E23.MirrorCS"),sQuery(id+"F0.wireOp",EDGE,"E24.MirrorCS"),sQuery(id+"F0.wireOp",EDGE,"E25.MirrorCS"),sQuery(id+"F0.wireOp",EDGE,"E26.MirrorCS"),sQuery(id+"F0.wireOp",EDGE,"E27.MirrorCS"),sQuery(id+"F0.wireOp",EDGE,"E28.MirrorCS"),sQuery(id+"F0.wireOp",EDGE,"E29.MirrorCS"),sQuery(id+"F0.wireOp",EDGE,"E30.MirrorCS"),sQuery(id+"F0.wireOp",EDGE,"E31.MirrorCS")])],"isStart":false})],"blendedInto":[makeQuery(id+"F1.opExtrude","CAP_FACE",FACE,{"disambiguationData":[OSD([sQuery(id+"F0.wireOp",EDGE,"E0"),sQuery(id+"F0.wireOp",EDGE,"E1.0"),sQuery(id+"F0.wireOp",EDGE,"E1.1"),subQ0,sQuery(id+"F0.wireOp",EDGE,"E1.3"),sQuery(id+"F0.wireOp",EDGE,"E1.4"),sQuery(id+"F0.wireOp",EDGE,"E1.5"),sQuery(id+"F0.wireOp",EDGE,"E1.6"),sQuery(id+"F0.wireOp",EDGE,"E1.7"),sQuery(id+"F0.wireOp",EDGE,"E1.8"),sQuery(id+"F0.wireOp",EDGE,"E1.9"),sQuery(id+"F0.wireOp",EDGE,"E1.10"),sQuery(id+"F0.wireOp",EDGE,"E2"),sQuery(id+"F0.wireOp",EDGE,"E3.2.0"),sQuery(id+"F0.wireOp",EDGE,"E3.3.0"),sQuery(id+"F0.wireOp",EDGE,"E3.4.0"),sQuery(id+"F0.wireOp",EDGE,"E3.5.0"),sQuery(id+"F0.wireOp",EDGE,"E3.6.0"),sQuery(id+"F0.wireOp",EDGE,"E3.7.0"),sQuery(id+"F0.wireOp",EDGE,"E3.8.0"),sQuery(id+"F0.wireOp",EDGE,"E3.9.0"),sQuery(id+"F0.wireOp",EDGE,"E3.10.0"),sQuery(id+"F0.wireOp",EDGE,"E4"),sQuery(id+"F0.wireOp",EDGE,"E5"),sQuery(id+"F0.wireOp",EDGE,"E6"),sQuery(id+"F0.wireOp",EDGE,"E7"),sQuery(id+"F0.wireOp",EDGE,"E8"),sQuery(id+"F0.wireOp",EDGE,"E9"),sQuery(id+"F0.wireOp",EDGE,"E10"),sQuery(id+"F0.wireOp",EDGE,"E11"),sQuery(id+"F0.wireOp",EDGE,"E12"),sQuery(id+"F0.wireOp",EDGE,"E13"),sQuery(id+"F0.wireOp",EDGE,"E14"),sQuery(id+"F0.wireOp",EDGE,"E15"),sQuery(id+"F0.wireOp",EDGE,"E16"),sQuery(id+"F0.wireOp",EDGE,"E17"),sQuery(id+"F0.wireOp",EDGE,"E18.MirrorCS"),sQuery(id+"F0.wireOp",EDGE,"E19.MirrorCS"),sQuery(id+"F0.wireOp",EDGE,"E20.MirrorCS"),sQuery(id+"F0.wireOp",EDGE,"E21.MirrorCS"),sQuery(id+"F0.wireOp",EDGE,"E22.MirrorCS"),sQuery(id+"F0.wireOp",EDGE,"E23.MirrorCS"),sQuery(id+"F0.wireOp",EDGE,"E24.MirrorCS"),sQuery(id+"F0.wireOp",EDGE,"E25.MirrorCS"),sQuery(id+"F0.wireOp",EDGE,"E26.MirrorCS"),sQuery(id+"F0.wireOp",EDGE,"E27.MirrorCS"),sQuery(id+"F0.wireOp",EDGE,"E28.MirrorCS"),sQuery(id+"F0.wireOp",EDGE,"E29.MirrorCS"),sQuery(id+"F0.wireOp",EDGE,"E30.MirrorCS"),sQuery(id+"F0.wireOp",EDGE,"E31.MirrorCS")])],"isStart":false})]}),makeQuery(id+"F6.opExtrude","CAP_EDGE",EDGE,{"disambiguationData":[OSD([sQuery(id+"F5.wireOp",EDGE,"E60.0")])],"isStart":true})]});}
            var Q21;
            Q21=makeQuery(id+"F6.boolean.opBoolean","COPY",EDGE,{"derivedFrom":makeQuery(id+"F6.opExtrude","CAP_EDGE",EDGE,{"disambiguationData":[OSD([sQuery(id+"F5.wireOp",EDGE,"E60.0")])],"isStart":false})});
            var Q22;
            {var subQ0=sQuery(id+"F0.wireOp",EDGE,"E3.9.0");Q22=makeQuery(id+"F6.boolean.opBoolean","MERGE",EDGE,{"derivedFrom":[makeQuery(id+"F2.opFillet","BLEND_EDGE",EDGE,{"blendedFrom":[makeQuery(id+"F1.opExtrude","CAP_EDGE",EDGE,{"disambiguationData":[OSD([subQ0])],"isStart":false}),makeQuery(id+"F1.opExtrude","CAP_FACE",FACE,{"disambiguationData":[OSD([sQuery(id+"F0.wireOp",EDGE,"E0"),sQuery(id+"F0.wireOp",EDGE,"E1.0"),sQuery(id+"F0.wireOp",EDGE,"E1.1"),sQuery(id+"F0.wireOp",EDGE,"E1.2"),sQuery(id+"F0.wireOp",EDGE,"E1.3"),sQuery(id+"F0.wireOp",EDGE,"E1.4"),sQuery(id+"F0.wireOp",EDGE,"E1.5"),sQuery(id+"F0.wireOp",EDGE,"E1.6"),sQuery(id+"F0.wireOp",EDGE,"E1.7"),sQuery(id+"F0.wireOp",EDGE,"E1.8"),sQuery(id+"F0.wireOp",EDGE,"E1.9"),sQuery(id+"F0.wireOp",EDGE,"E1.10"),sQuery(id+"F0.wireOp",EDGE,"E2"),sQuery(id+"F0.wireOp",EDGE,"E3.2.0"),sQuery(id+"F0.wireOp",EDGE,"E3.3.0"),sQuery(id+"F0.wireOp",EDGE,"E3.4.0"),sQuery(id+"F0.wireOp",EDGE,"E3.5.0"),sQuery(id+"F0.wireOp",EDGE,"E3.6.0"),sQuery(id+"F0.wireOp",EDGE,"E3.7.0"),sQuery(id+"F0.wireOp",EDGE,"E3.8.0"),subQ0,sQuery(id+"F0.wireOp",EDGE,"E3.10.0"),sQuery(id+"F0.wireOp",EDGE,"E4"),sQuery(id+"F0.wireOp",EDGE,"E5"),sQuery(id+"F0.wireOp",EDGE,"E6"),sQuery(id+"F0.wireOp",EDGE,"E7"),sQuery(id+"F0.wireOp",EDGE,"E8"),sQuery(id+"F0.wireOp",EDGE,"E9"),sQuery(id+"F0.wireOp",EDGE,"E10"),sQuery(id+"F0.wireOp",EDGE,"E11"),sQuery(id+"F0.wireOp",EDGE,"E12"),sQuery(id+"F0.wireOp",EDGE,"E13"),sQuery(id+"F0.wireOp",EDGE,"E14"),sQuery(id+"F0.wireOp",EDGE,"E15"),sQuery(id+"F0.wireOp",EDGE,"E16"),sQuery(id+"F0.wireOp",EDGE,"E17"),sQuery(id+"F0.wireOp",EDGE,"E18.MirrorCS"),sQuery(id+"F0.wireOp",EDGE,"E19.MirrorCS"),sQuery(id+"F0.wireOp",EDGE,"E20.MirrorCS"),sQuery(id+"F0.wireOp",EDGE,"E21.MirrorCS"),sQuery(id+"F0.wireOp",EDGE,"E22.MirrorCS"),sQuery(id+"F0.wireOp",EDGE,"E23.MirrorCS"),sQuery(id+"F0.wireOp",EDGE,"E24.MirrorCS"),sQuery(id+"F0.wireOp",EDGE,"E25.MirrorCS"),sQuery(id+"F0.wireOp",EDGE,"E26.MirrorCS"),sQuery(id+"F0.wireOp",EDGE,"E27.MirrorCS"),sQuery(id+"F0.wireOp",EDGE,"E28.MirrorCS"),sQuery(id+"F0.wireOp",EDGE,"E29.MirrorCS"),sQuery(id+"F0.wireOp",EDGE,"E30.MirrorCS"),sQuery(id+"F0.wireOp",EDGE,"E31.MirrorCS")])],"isStart":false})],"blendedInto":[makeQuery(id+"F1.opExtrude","CAP_FACE",FACE,{"disambiguationData":[OSD([sQuery(id+"F0.wireOp",EDGE,"E0"),sQuery(id+"F0.wireOp",EDGE,"E1.0"),sQuery(id+"F0.wireOp",EDGE,"E1.1"),sQuery(id+"F0.wireOp",EDGE,"E1.2"),sQuery(id+"F0.wireOp",EDGE,"E1.3"),sQuery(id+"F0.wireOp",EDGE,"E1.4"),sQuery(id+"F0.wireOp",EDGE,"E1.5"),sQuery(id+"F0.wireOp",EDGE,"E1.6"),sQuery(id+"F0.wireOp",EDGE,"E1.7"),sQuery(id+"F0.wireOp",EDGE,"E1.8"),sQuery(id+"F0.wireOp",EDGE,"E1.9"),sQuery(id+"F0.wireOp",EDGE,"E1.10"),sQuery(id+"F0.wireOp",EDGE,"E2"),sQuery(id+"F0.wireOp",EDGE,"E3.2.0"),sQuery(id+"F0.wireOp",EDGE,"E3.3.0"),sQuery(id+"F0.wireOp",EDGE,"E3.4.0"),sQuery(id+"F0.wireOp",EDGE,"E3.5.0"),sQuery(id+"F0.wireOp",EDGE,"E3.6.0"),sQuery(id+"F0.wireOp",EDGE,"E3.7.0"),sQuery(id+"F0.wireOp",EDGE,"E3.8.0"),subQ0,sQuery(id+"F0.wireOp",EDGE,"E3.10.0"),sQuery(id+"F0.wireOp",EDGE,"E4"),sQuery(id+"F0.wireOp",EDGE,"E5"),sQuery(id+"F0.wireOp",EDGE,"E6"),sQuery(id+"F0.wireOp",EDGE,"E7"),sQuery(id+"F0.wireOp",EDGE,"E8"),sQuery(id+"F0.wireOp",EDGE,"E9"),sQuery(id+"F0.wireOp",EDGE,"E10"),sQuery(id+"F0.wireOp",EDGE,"E11"),sQuery(id+"F0.wireOp",EDGE,"E12"),sQuery(id+"F0.wireOp",EDGE,"E13"),sQuery(id+"F0.wireOp",EDGE,"E14"),sQuery(id+"F0.wireOp",EDGE,"E15"),sQuery(id+"F0.wireOp",EDGE,"E16"),sQuery(id+"F0.wireOp",EDGE,"E17"),sQuery(id+"F0.wireOp",EDGE,"E18.MirrorCS"),sQuery(id+"F0.wireOp",EDGE,"E19.MirrorCS"),sQuery(id+"F0.wireOp",EDGE,"E20.MirrorCS"),sQuery(id+"F0.wireOp",EDGE,"E21.MirrorCS"),sQuery(id+"F0.wireOp",EDGE,"E22.MirrorCS"),sQuery(id+"F0.wireOp",EDGE,"E23.MirrorCS"),sQuery(id+"F0.wireOp",EDGE,"E24.MirrorCS"),sQuery(id+"F0.wireOp",EDGE,"E25.MirrorCS"),sQuery(id+"F0.wireOp",EDGE,"E26.MirrorCS"),sQuery(id+"F0.wireOp",EDGE,"E27.MirrorCS"),sQuery(id+"F0.wireOp",EDGE,"E28.MirrorCS"),sQuery(id+"F0.wireOp",EDGE,"E29.MirrorCS"),sQuery(id+"F0.wireOp",EDGE,"E30.MirrorCS"),sQuery(id+"F0.wireOp",EDGE,"E31.MirrorCS")])],"isStart":false})]}),makeQuery(id+"F6.opExtrude","CAP_EDGE",EDGE,{"disambiguationData":[OSD([sQuery(id+"F5.wireOp",EDGE,"E58.0")])],"isStart":true})]});}
            var Q23;
            Q23=makeQuery(id+"F6.boolean.opBoolean","COPY",EDGE,{"derivedFrom":makeQuery(id+"F6.opExtrude","CAP_EDGE",EDGE,{"disambiguationData":[OSD([sQuery(id+"F5.wireOp",EDGE,"E58.0")])],"isStart":false})});
            var Q24;
            {var subQ0=sQuery(id+"F0.wireOp",EDGE,"E1.3");Q24=makeQuery(id+"F6.boolean.opBoolean","MERGE",EDGE,{"derivedFrom":[makeQuery(id+"F2.opFillet","BLEND_EDGE",EDGE,{"blendedFrom":[makeQuery(id+"F1.opExtrude","CAP_EDGE",EDGE,{"disambiguationData":[OSD([subQ0])],"isStart":false}),makeQuery(id+"F1.opExtrude","CAP_FACE",FACE,{"disambiguationData":[OSD([sQuery(id+"F0.wireOp",EDGE,"E0"),sQuery(id+"F0.wireOp",EDGE,"E1.0"),sQuery(id+"F0.wireOp",EDGE,"E1.1"),sQuery(id+"F0.wireOp",EDGE,"E1.2"),subQ0,sQuery(id+"F0.wireOp",EDGE,"E1.4"),sQuery(id+"F0.wireOp",EDGE,"E1.5"),sQuery(id+"F0.wireOp",EDGE,"E1.6"),sQuery(id+"F0.wireOp",EDGE,"E1.7"),sQuery(id+"F0.wireOp",EDGE,"E1.8"),sQuery(id+"F0.wireOp",EDGE,"E1.9"),sQuery(id+"F0.wireOp",EDGE,"E1.10"),sQuery(id+"F0.wireOp",EDGE,"E2"),sQuery(id+"F0.wireOp",EDGE,"E3.2.0"),sQuery(id+"F0.wireOp",EDGE,"E3.3.0"),sQuery(id+"F0.wireOp",EDGE,"E3.4.0"),sQuery(id+"F0.wireOp",EDGE,"E3.5.0"),sQuery(id+"F0.wireOp",EDGE,"E3.6.0"),sQuery(id+"F0.wireOp",EDGE,"E3.7.0"),sQuery(id+"F0.wireOp",EDGE,"E3.8.0"),sQuery(id+"F0.wireOp",EDGE,"E3.9.0"),sQuery(id+"F0.wireOp",EDGE,"E3.10.0"),sQuery(id+"F0.wireOp",EDGE,"E4"),sQuery(id+"F0.wireOp",EDGE,"E5"),sQuery(id+"F0.wireOp",EDGE,"E6"),sQuery(id+"F0.wireOp",EDGE,"E7"),sQuery(id+"F0.wireOp",EDGE,"E8"),sQuery(id+"F0.wireOp",EDGE,"E9"),sQuery(id+"F0.wireOp",EDGE,"E10"),sQuery(id+"F0.wireOp",EDGE,"E11"),sQuery(id+"F0.wireOp",EDGE,"E12"),sQuery(id+"F0.wireOp",EDGE,"E13"),sQuery(id+"F0.wireOp",EDGE,"E14"),sQuery(id+"F0.wireOp",EDGE,"E15"),sQuery(id+"F0.wireOp",EDGE,"E16"),sQuery(id+"F0.wireOp",EDGE,"E17"),sQuery(id+"F0.wireOp",EDGE,"E18.MirrorCS"),sQuery(id+"F0.wireOp",EDGE,"E19.MirrorCS"),sQuery(id+"F0.wireOp",EDGE,"E20.MirrorCS"),sQuery(id+"F0.wireOp",EDGE,"E21.MirrorCS"),sQuery(id+"F0.wireOp",EDGE,"E22.MirrorCS"),sQuery(id+"F0.wireOp",EDGE,"E23.MirrorCS"),sQuery(id+"F0.wireOp",EDGE,"E24.MirrorCS"),sQuery(id+"F0.wireOp",EDGE,"E25.MirrorCS"),sQuery(id+"F0.wireOp",EDGE,"E26.MirrorCS"),sQuery(id+"F0.wireOp",EDGE,"E27.MirrorCS"),sQuery(id+"F0.wireOp",EDGE,"E28.MirrorCS"),sQuery(id+"F0.wireOp",EDGE,"E29.MirrorCS"),sQuery(id+"F0.wireOp",EDGE,"E30.MirrorCS"),sQuery(id+"F0.wireOp",EDGE,"E31.MirrorCS")])],"isStart":false})],"blendedInto":[makeQuery(id+"F1.opExtrude","CAP_FACE",FACE,{"disambiguationData":[OSD([sQuery(id+"F0.wireOp",EDGE,"E0"),sQuery(id+"F0.wireOp",EDGE,"E1.0"),sQuery(id+"F0.wireOp",EDGE,"E1.1"),sQuery(id+"F0.wireOp",EDGE,"E1.2"),subQ0,sQuery(id+"F0.wireOp",EDGE,"E1.4"),sQuery(id+"F0.wireOp",EDGE,"E1.5"),sQuery(id+"F0.wireOp",EDGE,"E1.6"),sQuery(id+"F0.wireOp",EDGE,"E1.7"),sQuery(id+"F0.wireOp",EDGE,"E1.8"),sQuery(id+"F0.wireOp",EDGE,"E1.9"),sQuery(id+"F0.wireOp",EDGE,"E1.10"),sQuery(id+"F0.wireOp",EDGE,"E2"),sQuery(id+"F0.wireOp",EDGE,"E3.2.0"),sQuery(id+"F0.wireOp",EDGE,"E3.3.0"),sQuery(id+"F0.wireOp",EDGE,"E3.4.0"),sQuery(id+"F0.wireOp",EDGE,"E3.5.0"),sQuery(id+"F0.wireOp",EDGE,"E3.6.0"),sQuery(id+"F0.wireOp",EDGE,"E3.7.0"),sQuery(id+"F0.wireOp",EDGE,"E3.8.0"),sQuery(id+"F0.wireOp",EDGE,"E3.9.0"),sQuery(id+"F0.wireOp",EDGE,"E3.10.0"),sQuery(id+"F0.wireOp",EDGE,"E4"),sQuery(id+"F0.wireOp",EDGE,"E5"),sQuery(id+"F0.wireOp",EDGE,"E6"),sQuery(id+"F0.wireOp",EDGE,"E7"),sQuery(id+"F0.wireOp",EDGE,"E8"),sQuery(id+"F0.wireOp",EDGE,"E9"),sQuery(id+"F0.wireOp",EDGE,"E10"),sQuery(id+"F0.wireOp",EDGE,"E11"),sQuery(id+"F0.wireOp",EDGE,"E12"),sQuery(id+"F0.wireOp",EDGE,"E13"),sQuery(id+"F0.wireOp",EDGE,"E14"),sQuery(id+"F0.wireOp",EDGE,"E15"),sQuery(id+"F0.wireOp",EDGE,"E16"),sQuery(id+"F0.wireOp",EDGE,"E17"),sQuery(id+"F0.wireOp",EDGE,"E18.MirrorCS"),sQuery(id+"F0.wireOp",EDGE,"E19.MirrorCS"),sQuery(id+"F0.wireOp",EDGE,"E20.MirrorCS"),sQuery(id+"F0.wireOp",EDGE,"E21.MirrorCS"),sQuery(id+"F0.wireOp",EDGE,"E22.MirrorCS"),sQuery(id+"F0.wireOp",EDGE,"E23.MirrorCS"),sQuery(id+"F0.wireOp",EDGE,"E24.MirrorCS"),sQuery(id+"F0.wireOp",EDGE,"E25.MirrorCS"),sQuery(id+"F0.wireOp",EDGE,"E26.MirrorCS"),sQuery(id+"F0.wireOp",EDGE,"E27.MirrorCS"),sQuery(id+"F0.wireOp",EDGE,"E28.MirrorCS"),sQuery(id+"F0.wireOp",EDGE,"E29.MirrorCS"),sQuery(id+"F0.wireOp",EDGE,"E30.MirrorCS"),sQuery(id+"F0.wireOp",EDGE,"E31.MirrorCS")])],"isStart":false})]}),makeQuery(id+"F6.opExtrude","CAP_EDGE",EDGE,{"disambiguationData":[OSD([sQuery(id+"F5.wireOp",EDGE,"E59.0")])],"isStart":true})]});}
            var Q25;
            Q25=makeQuery(id+"F6.boolean.opBoolean","COPY",EDGE,{"derivedFrom":makeQuery(id+"F6.opExtrude","CAP_EDGE",EDGE,{"disambiguationData":[OSD([sQuery(id+"F5.wireOp",EDGE,"E59.0")])],"isStart":false})});
            var Q26;
            {var subQ0=sQuery(id+"F0.wireOp",EDGE,"E3.8.0");Q26=makeQuery(id+"F6.boolean.opBoolean","MERGE",EDGE,{"derivedFrom":[makeQuery(id+"F2.opFillet","BLEND_EDGE",EDGE,{"blendedFrom":[makeQuery(id+"F1.opExtrude","CAP_EDGE",EDGE,{"disambiguationData":[OSD([subQ0])],"isStart":false}),makeQuery(id+"F1.opExtrude","CAP_FACE",FACE,{"disambiguationData":[OSD([sQuery(id+"F0.wireOp",EDGE,"E0"),sQuery(id+"F0.wireOp",EDGE,"E1.0"),sQuery(id+"F0.wireOp",EDGE,"E1.1"),sQuery(id+"F0.wireOp",EDGE,"E1.2"),sQuery(id+"F0.wireOp",EDGE,"E1.3"),sQuery(id+"F0.wireOp",EDGE,"E1.4"),sQuery(id+"F0.wireOp",EDGE,"E1.5"),sQuery(id+"F0.wireOp",EDGE,"E1.6"),sQuery(id+"F0.wireOp",EDGE,"E1.7"),sQuery(id+"F0.wireOp",EDGE,"E1.8"),sQuery(id+"F0.wireOp",EDGE,"E1.9"),sQuery(id+"F0.wireOp",EDGE,"E1.10"),sQuery(id+"F0.wireOp",EDGE,"E2"),sQuery(id+"F0.wireOp",EDGE,"E3.2.0"),sQuery(id+"F0.wireOp",EDGE,"E3.3.0"),sQuery(id+"F0.wireOp",EDGE,"E3.4.0"),sQuery(id+"F0.wireOp",EDGE,"E3.5.0"),sQuery(id+"F0.wireOp",EDGE,"E3.6.0"),sQuery(id+"F0.wireOp",EDGE,"E3.7.0"),subQ0,sQuery(id+"F0.wireOp",EDGE,"E3.9.0"),sQuery(id+"F0.wireOp",EDGE,"E3.10.0"),sQuery(id+"F0.wireOp",EDGE,"E4"),sQuery(id+"F0.wireOp",EDGE,"E5"),sQuery(id+"F0.wireOp",EDGE,"E6"),sQuery(id+"F0.wireOp",EDGE,"E7"),sQuery(id+"F0.wireOp",EDGE,"E8"),sQuery(id+"F0.wireOp",EDGE,"E9"),sQuery(id+"F0.wireOp",EDGE,"E10"),sQuery(id+"F0.wireOp",EDGE,"E11"),sQuery(id+"F0.wireOp",EDGE,"E12"),sQuery(id+"F0.wireOp",EDGE,"E13"),sQuery(id+"F0.wireOp",EDGE,"E14"),sQuery(id+"F0.wireOp",EDGE,"E15"),sQuery(id+"F0.wireOp",EDGE,"E16"),sQuery(id+"F0.wireOp",EDGE,"E17"),sQuery(id+"F0.wireOp",EDGE,"E18.MirrorCS"),sQuery(id+"F0.wireOp",EDGE,"E19.MirrorCS"),sQuery(id+"F0.wireOp",EDGE,"E20.MirrorCS"),sQuery(id+"F0.wireOp",EDGE,"E21.MirrorCS"),sQuery(id+"F0.wireOp",EDGE,"E22.MirrorCS"),sQuery(id+"F0.wireOp",EDGE,"E23.MirrorCS"),sQuery(id+"F0.wireOp",EDGE,"E24.MirrorCS"),sQuery(id+"F0.wireOp",EDGE,"E25.MirrorCS"),sQuery(id+"F0.wireOp",EDGE,"E26.MirrorCS"),sQuery(id+"F0.wireOp",EDGE,"E27.MirrorCS"),sQuery(id+"F0.wireOp",EDGE,"E28.MirrorCS"),sQuery(id+"F0.wireOp",EDGE,"E29.MirrorCS"),sQuery(id+"F0.wireOp",EDGE,"E30.MirrorCS"),sQuery(id+"F0.wireOp",EDGE,"E31.MirrorCS")])],"isStart":false})],"blendedInto":[makeQuery(id+"F1.opExtrude","CAP_FACE",FACE,{"disambiguationData":[OSD([sQuery(id+"F0.wireOp",EDGE,"E0"),sQuery(id+"F0.wireOp",EDGE,"E1.0"),sQuery(id+"F0.wireOp",EDGE,"E1.1"),sQuery(id+"F0.wireOp",EDGE,"E1.2"),sQuery(id+"F0.wireOp",EDGE,"E1.3"),sQuery(id+"F0.wireOp",EDGE,"E1.4"),sQuery(id+"F0.wireOp",EDGE,"E1.5"),sQuery(id+"F0.wireOp",EDGE,"E1.6"),sQuery(id+"F0.wireOp",EDGE,"E1.7"),sQuery(id+"F0.wireOp",EDGE,"E1.8"),sQuery(id+"F0.wireOp",EDGE,"E1.9"),sQuery(id+"F0.wireOp",EDGE,"E1.10"),sQuery(id+"F0.wireOp",EDGE,"E2"),sQuery(id+"F0.wireOp",EDGE,"E3.2.0"),sQuery(id+"F0.wireOp",EDGE,"E3.3.0"),sQuery(id+"F0.wireOp",EDGE,"E3.4.0"),sQuery(id+"F0.wireOp",EDGE,"E3.5.0"),sQuery(id+"F0.wireOp",EDGE,"E3.6.0"),sQuery(id+"F0.wireOp",EDGE,"E3.7.0"),subQ0,sQuery(id+"F0.wireOp",EDGE,"E3.9.0"),sQuery(id+"F0.wireOp",EDGE,"E3.10.0"),sQuery(id+"F0.wireOp",EDGE,"E4"),sQuery(id+"F0.wireOp",EDGE,"E5"),sQuery(id+"F0.wireOp",EDGE,"E6"),sQuery(id+"F0.wireOp",EDGE,"E7"),sQuery(id+"F0.wireOp",EDGE,"E8"),sQuery(id+"F0.wireOp",EDGE,"E9"),sQuery(id+"F0.wireOp",EDGE,"E10"),sQuery(id+"F0.wireOp",EDGE,"E11"),sQuery(id+"F0.wireOp",EDGE,"E12"),sQuery(id+"F0.wireOp",EDGE,"E13"),sQuery(id+"F0.wireOp",EDGE,"E14"),sQuery(id+"F0.wireOp",EDGE,"E15"),sQuery(id+"F0.wireOp",EDGE,"E16"),sQuery(id+"F0.wireOp",EDGE,"E17"),sQuery(id+"F0.wireOp",EDGE,"E18.MirrorCS"),sQuery(id+"F0.wireOp",EDGE,"E19.MirrorCS"),sQuery(id+"F0.wireOp",EDGE,"E20.MirrorCS"),sQuery(id+"F0.wireOp",EDGE,"E21.MirrorCS"),sQuery(id+"F0.wireOp",EDGE,"E22.MirrorCS"),sQuery(id+"F0.wireOp",EDGE,"E23.MirrorCS"),sQuery(id+"F0.wireOp",EDGE,"E24.MirrorCS"),sQuery(id+"F0.wireOp",EDGE,"E25.MirrorCS"),sQuery(id+"F0.wireOp",EDGE,"E26.MirrorCS"),sQuery(id+"F0.wireOp",EDGE,"E27.MirrorCS"),sQuery(id+"F0.wireOp",EDGE,"E28.MirrorCS"),sQuery(id+"F0.wireOp",EDGE,"E29.MirrorCS"),sQuery(id+"F0.wireOp",EDGE,"E30.MirrorCS"),sQuery(id+"F0.wireOp",EDGE,"E31.MirrorCS")])],"isStart":false})]}),makeQuery(id+"F6.opExtrude","CAP_EDGE",EDGE,{"disambiguationData":[OSD([sQuery(id+"F5.wireOp",EDGE,"E57.0")])],"isStart":true})]});}
            var Q27;
            Q27=makeQuery(id+"F6.boolean.opBoolean","COPY",EDGE,{"derivedFrom":makeQuery(id+"F6.opExtrude","CAP_EDGE",EDGE,{"disambiguationData":[OSD([sQuery(id+"F5.wireOp",EDGE,"E57.0")])],"isStart":false})});
            var Q28;
            Q28=makeQuery(id+"F6.boolean.opBoolean","COPY",EDGE,{"derivedFrom":makeQuery(id+"F6.opExtrude","CAP_EDGE",EDGE,{"disambiguationData":[OSD([sQuery(id+"F5.wireOp",EDGE,"E56.0")])],"isStart":false})});
            var Q29;
            {var subQ0=sQuery(id+"F0.wireOp",EDGE,"E1.4");Q29=makeQuery(id+"F6.boolean.opBoolean","MERGE",EDGE,{"derivedFrom":[makeQuery(id+"F2.opFillet","BLEND_EDGE",EDGE,{"blendedFrom":[makeQuery(id+"F1.opExtrude","CAP_EDGE",EDGE,{"disambiguationData":[OSD([subQ0])],"isStart":false}),makeQuery(id+"F1.opExtrude","CAP_FACE",FACE,{"disambiguationData":[OSD([sQuery(id+"F0.wireOp",EDGE,"E0"),sQuery(id+"F0.wireOp",EDGE,"E1.0"),sQuery(id+"F0.wireOp",EDGE,"E1.1"),sQuery(id+"F0.wireOp",EDGE,"E1.2"),sQuery(id+"F0.wireOp",EDGE,"E1.3"),subQ0,sQuery(id+"F0.wireOp",EDGE,"E1.5"),sQuery(id+"F0.wireOp",EDGE,"E1.6"),sQuery(id+"F0.wireOp",EDGE,"E1.7"),sQuery(id+"F0.wireOp",EDGE,"E1.8"),sQuery(id+"F0.wireOp",EDGE,"E1.9"),sQuery(id+"F0.wireOp",EDGE,"E1.10"),sQuery(id+"F0.wireOp",EDGE,"E2"),sQuery(id+"F0.wireOp",EDGE,"E3.2.0"),sQuery(id+"F0.wireOp",EDGE,"E3.3.0"),sQuery(id+"F0.wireOp",EDGE,"E3.4.0"),sQuery(id+"F0.wireOp",EDGE,"E3.5.0"),sQuery(id+"F0.wireOp",EDGE,"E3.6.0"),sQuery(id+"F0.wireOp",EDGE,"E3.7.0"),sQuery(id+"F0.wireOp",EDGE,"E3.8.0"),sQuery(id+"F0.wireOp",EDGE,"E3.9.0"),sQuery(id+"F0.wireOp",EDGE,"E3.10.0"),sQuery(id+"F0.wireOp",EDGE,"E4"),sQuery(id+"F0.wireOp",EDGE,"E5"),sQuery(id+"F0.wireOp",EDGE,"E6"),sQuery(id+"F0.wireOp",EDGE,"E7"),sQuery(id+"F0.wireOp",EDGE,"E8"),sQuery(id+"F0.wireOp",EDGE,"E9"),sQuery(id+"F0.wireOp",EDGE,"E10"),sQuery(id+"F0.wireOp",EDGE,"E11"),sQuery(id+"F0.wireOp",EDGE,"E12"),sQuery(id+"F0.wireOp",EDGE,"E13"),sQuery(id+"F0.wireOp",EDGE,"E14"),sQuery(id+"F0.wireOp",EDGE,"E15"),sQuery(id+"F0.wireOp",EDGE,"E16"),sQuery(id+"F0.wireOp",EDGE,"E17"),sQuery(id+"F0.wireOp",EDGE,"E18.MirrorCS"),sQuery(id+"F0.wireOp",EDGE,"E19.MirrorCS"),sQuery(id+"F0.wireOp",EDGE,"E20.MirrorCS"),sQuery(id+"F0.wireOp",EDGE,"E21.MirrorCS"),sQuery(id+"F0.wireOp",EDGE,"E22.MirrorCS"),sQuery(id+"F0.wireOp",EDGE,"E23.MirrorCS"),sQuery(id+"F0.wireOp",EDGE,"E24.MirrorCS"),sQuery(id+"F0.wireOp",EDGE,"E25.MirrorCS"),sQuery(id+"F0.wireOp",EDGE,"E26.MirrorCS"),sQuery(id+"F0.wireOp",EDGE,"E27.MirrorCS"),sQuery(id+"F0.wireOp",EDGE,"E28.MirrorCS"),sQuery(id+"F0.wireOp",EDGE,"E29.MirrorCS"),sQuery(id+"F0.wireOp",EDGE,"E30.MirrorCS"),sQuery(id+"F0.wireOp",EDGE,"E31.MirrorCS")])],"isStart":false})],"blendedInto":[makeQuery(id+"F1.opExtrude","CAP_FACE",FACE,{"disambiguationData":[OSD([sQuery(id+"F0.wireOp",EDGE,"E0"),sQuery(id+"F0.wireOp",EDGE,"E1.0"),sQuery(id+"F0.wireOp",EDGE,"E1.1"),sQuery(id+"F0.wireOp",EDGE,"E1.2"),sQuery(id+"F0.wireOp",EDGE,"E1.3"),subQ0,sQuery(id+"F0.wireOp",EDGE,"E1.5"),sQuery(id+"F0.wireOp",EDGE,"E1.6"),sQuery(id+"F0.wireOp",EDGE,"E1.7"),sQuery(id+"F0.wireOp",EDGE,"E1.8"),sQuery(id+"F0.wireOp",EDGE,"E1.9"),sQuery(id+"F0.wireOp",EDGE,"E1.10"),sQuery(id+"F0.wireOp",EDGE,"E2"),sQuery(id+"F0.wireOp",EDGE,"E3.2.0"),sQuery(id+"F0.wireOp",EDGE,"E3.3.0"),sQuery(id+"F0.wireOp",EDGE,"E3.4.0"),sQuery(id+"F0.wireOp",EDGE,"E3.5.0"),sQuery(id+"F0.wireOp",EDGE,"E3.6.0"),sQuery(id+"F0.wireOp",EDGE,"E3.7.0"),sQuery(id+"F0.wireOp",EDGE,"E3.8.0"),sQuery(id+"F0.wireOp",EDGE,"E3.9.0"),sQuery(id+"F0.wireOp",EDGE,"E3.10.0"),sQuery(id+"F0.wireOp",EDGE,"E4"),sQuery(id+"F0.wireOp",EDGE,"E5"),sQuery(id+"F0.wireOp",EDGE,"E6"),sQuery(id+"F0.wireOp",EDGE,"E7"),sQuery(id+"F0.wireOp",EDGE,"E8"),sQuery(id+"F0.wireOp",EDGE,"E9"),sQuery(id+"F0.wireOp",EDGE,"E10"),sQuery(id+"F0.wireOp",EDGE,"E11"),sQuery(id+"F0.wireOp",EDGE,"E12"),sQuery(id+"F0.wireOp",EDGE,"E13"),sQuery(id+"F0.wireOp",EDGE,"E14"),sQuery(id+"F0.wireOp",EDGE,"E15"),sQuery(id+"F0.wireOp",EDGE,"E16"),sQuery(id+"F0.wireOp",EDGE,"E17"),sQuery(id+"F0.wireOp",EDGE,"E18.MirrorCS"),sQuery(id+"F0.wireOp",EDGE,"E19.MirrorCS"),sQuery(id+"F0.wireOp",EDGE,"E20.MirrorCS"),sQuery(id+"F0.wireOp",EDGE,"E21.MirrorCS"),sQuery(id+"F0.wireOp",EDGE,"E22.MirrorCS"),sQuery(id+"F0.wireOp",EDGE,"E23.MirrorCS"),sQuery(id+"F0.wireOp",EDGE,"E24.MirrorCS"),sQuery(id+"F0.wireOp",EDGE,"E25.MirrorCS"),sQuery(id+"F0.wireOp",EDGE,"E26.MirrorCS"),sQuery(id+"F0.wireOp",EDGE,"E27.MirrorCS"),sQuery(id+"F0.wireOp",EDGE,"E28.MirrorCS"),sQuery(id+"F0.wireOp",EDGE,"E29.MirrorCS"),sQuery(id+"F0.wireOp",EDGE,"E30.MirrorCS"),sQuery(id+"F0.wireOp",EDGE,"E31.MirrorCS")])],"isStart":false})]}),makeQuery(id+"F6.opExtrude","CAP_EDGE",EDGE,{"disambiguationData":[OSD([sQuery(id+"F5.wireOp",EDGE,"E56.0")])],"isStart":true})]});}
            var Q30;
            {var subQ0=sQuery(id+"F0.wireOp",EDGE,"E3.7.0");Q30=makeQuery(id+"F6.boolean.opBoolean","MERGE",EDGE,{"derivedFrom":[makeQuery(id+"F2.opFillet","BLEND_EDGE",EDGE,{"blendedFrom":[makeQuery(id+"F1.opExtrude","CAP_EDGE",EDGE,{"disambiguationData":[OSD([subQ0])],"isStart":false}),makeQuery(id+"F1.opExtrude","CAP_FACE",FACE,{"disambiguationData":[OSD([sQuery(id+"F0.wireOp",EDGE,"E0"),sQuery(id+"F0.wireOp",EDGE,"E1.0"),sQuery(id+"F0.wireOp",EDGE,"E1.1"),sQuery(id+"F0.wireOp",EDGE,"E1.2"),sQuery(id+"F0.wireOp",EDGE,"E1.3"),sQuery(id+"F0.wireOp",EDGE,"E1.4"),sQuery(id+"F0.wireOp",EDGE,"E1.5"),sQuery(id+"F0.wireOp",EDGE,"E1.6"),sQuery(id+"F0.wireOp",EDGE,"E1.7"),sQuery(id+"F0.wireOp",EDGE,"E1.8"),sQuery(id+"F0.wireOp",EDGE,"E1.9"),sQuery(id+"F0.wireOp",EDGE,"E1.10"),sQuery(id+"F0.wireOp",EDGE,"E2"),sQuery(id+"F0.wireOp",EDGE,"E3.2.0"),sQuery(id+"F0.wireOp",EDGE,"E3.3.0"),sQuery(id+"F0.wireOp",EDGE,"E3.4.0"),sQuery(id+"F0.wireOp",EDGE,"E3.5.0"),sQuery(id+"F0.wireOp",EDGE,"E3.6.0"),subQ0,sQuery(id+"F0.wireOp",EDGE,"E3.8.0"),sQuery(id+"F0.wireOp",EDGE,"E3.9.0"),sQuery(id+"F0.wireOp",EDGE,"E3.10.0"),sQuery(id+"F0.wireOp",EDGE,"E4"),sQuery(id+"F0.wireOp",EDGE,"E5"),sQuery(id+"F0.wireOp",EDGE,"E6"),sQuery(id+"F0.wireOp",EDGE,"E7"),sQuery(id+"F0.wireOp",EDGE,"E8"),sQuery(id+"F0.wireOp",EDGE,"E9"),sQuery(id+"F0.wireOp",EDGE,"E10"),sQuery(id+"F0.wireOp",EDGE,"E11"),sQuery(id+"F0.wireOp",EDGE,"E12"),sQuery(id+"F0.wireOp",EDGE,"E13"),sQuery(id+"F0.wireOp",EDGE,"E14"),sQuery(id+"F0.wireOp",EDGE,"E15"),sQuery(id+"F0.wireOp",EDGE,"E16"),sQuery(id+"F0.wireOp",EDGE,"E17"),sQuery(id+"F0.wireOp",EDGE,"E18.MirrorCS"),sQuery(id+"F0.wireOp",EDGE,"E19.MirrorCS"),sQuery(id+"F0.wireOp",EDGE,"E20.MirrorCS"),sQuery(id+"F0.wireOp",EDGE,"E21.MirrorCS"),sQuery(id+"F0.wireOp",EDGE,"E22.MirrorCS"),sQuery(id+"F0.wireOp",EDGE,"E23.MirrorCS"),sQuery(id+"F0.wireOp",EDGE,"E24.MirrorCS"),sQuery(id+"F0.wireOp",EDGE,"E25.MirrorCS"),sQuery(id+"F0.wireOp",EDGE,"E26.MirrorCS"),sQuery(id+"F0.wireOp",EDGE,"E27.MirrorCS"),sQuery(id+"F0.wireOp",EDGE,"E28.MirrorCS"),sQuery(id+"F0.wireOp",EDGE,"E29.MirrorCS"),sQuery(id+"F0.wireOp",EDGE,"E30.MirrorCS"),sQuery(id+"F0.wireOp",EDGE,"E31.MirrorCS")])],"isStart":false})],"blendedInto":[makeQuery(id+"F1.opExtrude","CAP_FACE",FACE,{"disambiguationData":[OSD([sQuery(id+"F0.wireOp",EDGE,"E0"),sQuery(id+"F0.wireOp",EDGE,"E1.0"),sQuery(id+"F0.wireOp",EDGE,"E1.1"),sQuery(id+"F0.wireOp",EDGE,"E1.2"),sQuery(id+"F0.wireOp",EDGE,"E1.3"),sQuery(id+"F0.wireOp",EDGE,"E1.4"),sQuery(id+"F0.wireOp",EDGE,"E1.5"),sQuery(id+"F0.wireOp",EDGE,"E1.6"),sQuery(id+"F0.wireOp",EDGE,"E1.7"),sQuery(id+"F0.wireOp",EDGE,"E1.8"),sQuery(id+"F0.wireOp",EDGE,"E1.9"),sQuery(id+"F0.wireOp",EDGE,"E1.10"),sQuery(id+"F0.wireOp",EDGE,"E2"),sQuery(id+"F0.wireOp",EDGE,"E3.2.0"),sQuery(id+"F0.wireOp",EDGE,"E3.3.0"),sQuery(id+"F0.wireOp",EDGE,"E3.4.0"),sQuery(id+"F0.wireOp",EDGE,"E3.5.0"),sQuery(id+"F0.wireOp",EDGE,"E3.6.0"),subQ0,sQuery(id+"F0.wireOp",EDGE,"E3.8.0"),sQuery(id+"F0.wireOp",EDGE,"E3.9.0"),sQuery(id+"F0.wireOp",EDGE,"E3.10.0"),sQuery(id+"F0.wireOp",EDGE,"E4"),sQuery(id+"F0.wireOp",EDGE,"E5"),sQuery(id+"F0.wireOp",EDGE,"E6"),sQuery(id+"F0.wireOp",EDGE,"E7"),sQuery(id+"F0.wireOp",EDGE,"E8"),sQuery(id+"F0.wireOp",EDGE,"E9"),sQuery(id+"F0.wireOp",EDGE,"E10"),sQuery(id+"F0.wireOp",EDGE,"E11"),sQuery(id+"F0.wireOp",EDGE,"E12"),sQuery(id+"F0.wireOp",EDGE,"E13"),sQuery(id+"F0.wireOp",EDGE,"E14"),sQuery(id+"F0.wireOp",EDGE,"E15"),sQuery(id+"F0.wireOp",EDGE,"E16"),sQuery(id+"F0.wireOp",EDGE,"E17"),sQuery(id+"F0.wireOp",EDGE,"E18.MirrorCS"),sQuery(id+"F0.wireOp",EDGE,"E19.MirrorCS"),sQuery(id+"F0.wireOp",EDGE,"E20.MirrorCS"),sQuery(id+"F0.wireOp",EDGE,"E21.MirrorCS"),sQuery(id+"F0.wireOp",EDGE,"E22.MirrorCS"),sQuery(id+"F0.wireOp",EDGE,"E23.MirrorCS"),sQuery(id+"F0.wireOp",EDGE,"E24.MirrorCS"),sQuery(id+"F0.wireOp",EDGE,"E25.MirrorCS"),sQuery(id+"F0.wireOp",EDGE,"E26.MirrorCS"),sQuery(id+"F0.wireOp",EDGE,"E27.MirrorCS"),sQuery(id+"F0.wireOp",EDGE,"E28.MirrorCS"),sQuery(id+"F0.wireOp",EDGE,"E29.MirrorCS"),sQuery(id+"F0.wireOp",EDGE,"E30.MirrorCS"),sQuery(id+"F0.wireOp",EDGE,"E31.MirrorCS")])],"isStart":false})]}),makeQuery(id+"F6.opExtrude","CAP_EDGE",EDGE,{"disambiguationData":[OSD([sQuery(id+"F5.wireOp",EDGE,"E55.0")])],"isStart":true})]});}
            var Q31;
            Q31=makeQuery(id+"F6.boolean.opBoolean","COPY",EDGE,{"derivedFrom":makeQuery(id+"F6.opExtrude","CAP_EDGE",EDGE,{"disambiguationData":[OSD([sQuery(id+"F5.wireOp",EDGE,"E55.0")])],"isStart":false})});
            var Q32;
            {var subQ0=sQuery(id+"F0.wireOp",EDGE,"E1.5");Q32=makeQuery(id+"F6.boolean.opBoolean","MERGE",EDGE,{"derivedFrom":[makeQuery(id+"F2.opFillet","BLEND_EDGE",EDGE,{"blendedFrom":[makeQuery(id+"F1.opExtrude","CAP_EDGE",EDGE,{"disambiguationData":[OSD([subQ0])],"isStart":false}),makeQuery(id+"F1.opExtrude","CAP_FACE",FACE,{"disambiguationData":[OSD([sQuery(id+"F0.wireOp",EDGE,"E0"),sQuery(id+"F0.wireOp",EDGE,"E1.0"),sQuery(id+"F0.wireOp",EDGE,"E1.1"),sQuery(id+"F0.wireOp",EDGE,"E1.2"),sQuery(id+"F0.wireOp",EDGE,"E1.3"),sQuery(id+"F0.wireOp",EDGE,"E1.4"),subQ0,sQuery(id+"F0.wireOp",EDGE,"E1.6"),sQuery(id+"F0.wireOp",EDGE,"E1.7"),sQuery(id+"F0.wireOp",EDGE,"E1.8"),sQuery(id+"F0.wireOp",EDGE,"E1.9"),sQuery(id+"F0.wireOp",EDGE,"E1.10"),sQuery(id+"F0.wireOp",EDGE,"E2"),sQuery(id+"F0.wireOp",EDGE,"E3.2.0"),sQuery(id+"F0.wireOp",EDGE,"E3.3.0"),sQuery(id+"F0.wireOp",EDGE,"E3.4.0"),sQuery(id+"F0.wireOp",EDGE,"E3.5.0"),sQuery(id+"F0.wireOp",EDGE,"E3.6.0"),sQuery(id+"F0.wireOp",EDGE,"E3.7.0"),sQuery(id+"F0.wireOp",EDGE,"E3.8.0"),sQuery(id+"F0.wireOp",EDGE,"E3.9.0"),sQuery(id+"F0.wireOp",EDGE,"E3.10.0"),sQuery(id+"F0.wireOp",EDGE,"E4"),sQuery(id+"F0.wireOp",EDGE,"E5"),sQuery(id+"F0.wireOp",EDGE,"E6"),sQuery(id+"F0.wireOp",EDGE,"E7"),sQuery(id+"F0.wireOp",EDGE,"E8"),sQuery(id+"F0.wireOp",EDGE,"E9"),sQuery(id+"F0.wireOp",EDGE,"E10"),sQuery(id+"F0.wireOp",EDGE,"E11"),sQuery(id+"F0.wireOp",EDGE,"E12"),sQuery(id+"F0.wireOp",EDGE,"E13"),sQuery(id+"F0.wireOp",EDGE,"E14"),sQuery(id+"F0.wireOp",EDGE,"E15"),sQuery(id+"F0.wireOp",EDGE,"E16"),sQuery(id+"F0.wireOp",EDGE,"E17"),sQuery(id+"F0.wireOp",EDGE,"E18.MirrorCS"),sQuery(id+"F0.wireOp",EDGE,"E19.MirrorCS"),sQuery(id+"F0.wireOp",EDGE,"E20.MirrorCS"),sQuery(id+"F0.wireOp",EDGE,"E21.MirrorCS"),sQuery(id+"F0.wireOp",EDGE,"E22.MirrorCS"),sQuery(id+"F0.wireOp",EDGE,"E23.MirrorCS"),sQuery(id+"F0.wireOp",EDGE,"E24.MirrorCS"),sQuery(id+"F0.wireOp",EDGE,"E25.MirrorCS"),sQuery(id+"F0.wireOp",EDGE,"E26.MirrorCS"),sQuery(id+"F0.wireOp",EDGE,"E27.MirrorCS"),sQuery(id+"F0.wireOp",EDGE,"E28.MirrorCS"),sQuery(id+"F0.wireOp",EDGE,"E29.MirrorCS"),sQuery(id+"F0.wireOp",EDGE,"E30.MirrorCS"),sQuery(id+"F0.wireOp",EDGE,"E31.MirrorCS")])],"isStart":false})],"blendedInto":[makeQuery(id+"F1.opExtrude","CAP_FACE",FACE,{"disambiguationData":[OSD([sQuery(id+"F0.wireOp",EDGE,"E0"),sQuery(id+"F0.wireOp",EDGE,"E1.0"),sQuery(id+"F0.wireOp",EDGE,"E1.1"),sQuery(id+"F0.wireOp",EDGE,"E1.2"),sQuery(id+"F0.wireOp",EDGE,"E1.3"),sQuery(id+"F0.wireOp",EDGE,"E1.4"),subQ0,sQuery(id+"F0.wireOp",EDGE,"E1.6"),sQuery(id+"F0.wireOp",EDGE,"E1.7"),sQuery(id+"F0.wireOp",EDGE,"E1.8"),sQuery(id+"F0.wireOp",EDGE,"E1.9"),sQuery(id+"F0.wireOp",EDGE,"E1.10"),sQuery(id+"F0.wireOp",EDGE,"E2"),sQuery(id+"F0.wireOp",EDGE,"E3.2.0"),sQuery(id+"F0.wireOp",EDGE,"E3.3.0"),sQuery(id+"F0.wireOp",EDGE,"E3.4.0"),sQuery(id+"F0.wireOp",EDGE,"E3.5.0"),sQuery(id+"F0.wireOp",EDGE,"E3.6.0"),sQuery(id+"F0.wireOp",EDGE,"E3.7.0"),sQuery(id+"F0.wireOp",EDGE,"E3.8.0"),sQuery(id+"F0.wireOp",EDGE,"E3.9.0"),sQuery(id+"F0.wireOp",EDGE,"E3.10.0"),sQuery(id+"F0.wireOp",EDGE,"E4"),sQuery(id+"F0.wireOp",EDGE,"E5"),sQuery(id+"F0.wireOp",EDGE,"E6"),sQuery(id+"F0.wireOp",EDGE,"E7"),sQuery(id+"F0.wireOp",EDGE,"E8"),sQuery(id+"F0.wireOp",EDGE,"E9"),sQuery(id+"F0.wireOp",EDGE,"E10"),sQuery(id+"F0.wireOp",EDGE,"E11"),sQuery(id+"F0.wireOp",EDGE,"E12"),sQuery(id+"F0.wireOp",EDGE,"E13"),sQuery(id+"F0.wireOp",EDGE,"E14"),sQuery(id+"F0.wireOp",EDGE,"E15"),sQuery(id+"F0.wireOp",EDGE,"E16"),sQuery(id+"F0.wireOp",EDGE,"E17"),sQuery(id+"F0.wireOp",EDGE,"E18.MirrorCS"),sQuery(id+"F0.wireOp",EDGE,"E19.MirrorCS"),sQuery(id+"F0.wireOp",EDGE,"E20.MirrorCS"),sQuery(id+"F0.wireOp",EDGE,"E21.MirrorCS"),sQuery(id+"F0.wireOp",EDGE,"E22.MirrorCS"),sQuery(id+"F0.wireOp",EDGE,"E23.MirrorCS"),sQuery(id+"F0.wireOp",EDGE,"E24.MirrorCS"),sQuery(id+"F0.wireOp",EDGE,"E25.MirrorCS"),sQuery(id+"F0.wireOp",EDGE,"E26.MirrorCS"),sQuery(id+"F0.wireOp",EDGE,"E27.MirrorCS"),sQuery(id+"F0.wireOp",EDGE,"E28.MirrorCS"),sQuery(id+"F0.wireOp",EDGE,"E29.MirrorCS"),sQuery(id+"F0.wireOp",EDGE,"E30.MirrorCS"),sQuery(id+"F0.wireOp",EDGE,"E31.MirrorCS")])],"isStart":false})]}),makeQuery(id+"F6.opExtrude","CAP_EDGE",EDGE,{"disambiguationData":[OSD([sQuery(id+"F5.wireOp",EDGE,"E54.0")])],"isStart":true})]});}
            var Q33;
            Q33=makeQuery(id+"F6.boolean.opBoolean","COPY",EDGE,{"derivedFrom":makeQuery(id+"F6.opExtrude","CAP_EDGE",EDGE,{"disambiguationData":[OSD([sQuery(id+"F5.wireOp",EDGE,"E54.0")])],"isStart":false})});
            var Q34;
            {var subQ0=sQuery(id+"F0.wireOp",EDGE,"E3.6.0");Q34=makeQuery(id+"F6.boolean.opBoolean","MERGE",EDGE,{"derivedFrom":[makeQuery(id+"F2.opFillet","BLEND_EDGE",EDGE,{"blendedFrom":[makeQuery(id+"F1.opExtrude","CAP_EDGE",EDGE,{"disambiguationData":[OSD([subQ0])],"isStart":false}),makeQuery(id+"F1.opExtrude","CAP_FACE",FACE,{"disambiguationData":[OSD([sQuery(id+"F0.wireOp",EDGE,"E0"),sQuery(id+"F0.wireOp",EDGE,"E1.0"),sQuery(id+"F0.wireOp",EDGE,"E1.1"),sQuery(id+"F0.wireOp",EDGE,"E1.2"),sQuery(id+"F0.wireOp",EDGE,"E1.3"),sQuery(id+"F0.wireOp",EDGE,"E1.4"),sQuery(id+"F0.wireOp",EDGE,"E1.5"),sQuery(id+"F0.wireOp",EDGE,"E1.6"),sQuery(id+"F0.wireOp",EDGE,"E1.7"),sQuery(id+"F0.wireOp",EDGE,"E1.8"),sQuery(id+"F0.wireOp",EDGE,"E1.9"),sQuery(id+"F0.wireOp",EDGE,"E1.10"),sQuery(id+"F0.wireOp",EDGE,"E2"),sQuery(id+"F0.wireOp",EDGE,"E3.2.0"),sQuery(id+"F0.wireOp",EDGE,"E3.3.0"),sQuery(id+"F0.wireOp",EDGE,"E3.4.0"),sQuery(id+"F0.wireOp",EDGE,"E3.5.0"),subQ0,sQuery(id+"F0.wireOp",EDGE,"E3.7.0"),sQuery(id+"F0.wireOp",EDGE,"E3.8.0"),sQuery(id+"F0.wireOp",EDGE,"E3.9.0"),sQuery(id+"F0.wireOp",EDGE,"E3.10.0"),sQuery(id+"F0.wireOp",EDGE,"E4"),sQuery(id+"F0.wireOp",EDGE,"E5"),sQuery(id+"F0.wireOp",EDGE,"E6"),sQuery(id+"F0.wireOp",EDGE,"E7"),sQuery(id+"F0.wireOp",EDGE,"E8"),sQuery(id+"F0.wireOp",EDGE,"E9"),sQuery(id+"F0.wireOp",EDGE,"E10"),sQuery(id+"F0.wireOp",EDGE,"E11"),sQuery(id+"F0.wireOp",EDGE,"E12"),sQuery(id+"F0.wireOp",EDGE,"E13"),sQuery(id+"F0.wireOp",EDGE,"E14"),sQuery(id+"F0.wireOp",EDGE,"E15"),sQuery(id+"F0.wireOp",EDGE,"E16"),sQuery(id+"F0.wireOp",EDGE,"E17"),sQuery(id+"F0.wireOp",EDGE,"E18.MirrorCS"),sQuery(id+"F0.wireOp",EDGE,"E19.MirrorCS"),sQuery(id+"F0.wireOp",EDGE,"E20.MirrorCS"),sQuery(id+"F0.wireOp",EDGE,"E21.MirrorCS"),sQuery(id+"F0.wireOp",EDGE,"E22.MirrorCS"),sQuery(id+"F0.wireOp",EDGE,"E23.MirrorCS"),sQuery(id+"F0.wireOp",EDGE,"E24.MirrorCS"),sQuery(id+"F0.wireOp",EDGE,"E25.MirrorCS"),sQuery(id+"F0.wireOp",EDGE,"E26.MirrorCS"),sQuery(id+"F0.wireOp",EDGE,"E27.MirrorCS"),sQuery(id+"F0.wireOp",EDGE,"E28.MirrorCS"),sQuery(id+"F0.wireOp",EDGE,"E29.MirrorCS"),sQuery(id+"F0.wireOp",EDGE,"E30.MirrorCS"),sQuery(id+"F0.wireOp",EDGE,"E31.MirrorCS")])],"isStart":false})],"blendedInto":[makeQuery(id+"F1.opExtrude","CAP_FACE",FACE,{"disambiguationData":[OSD([sQuery(id+"F0.wireOp",EDGE,"E0"),sQuery(id+"F0.wireOp",EDGE,"E1.0"),sQuery(id+"F0.wireOp",EDGE,"E1.1"),sQuery(id+"F0.wireOp",EDGE,"E1.2"),sQuery(id+"F0.wireOp",EDGE,"E1.3"),sQuery(id+"F0.wireOp",EDGE,"E1.4"),sQuery(id+"F0.wireOp",EDGE,"E1.5"),sQuery(id+"F0.wireOp",EDGE,"E1.6"),sQuery(id+"F0.wireOp",EDGE,"E1.7"),sQuery(id+"F0.wireOp",EDGE,"E1.8"),sQuery(id+"F0.wireOp",EDGE,"E1.9"),sQuery(id+"F0.wireOp",EDGE,"E1.10"),sQuery(id+"F0.wireOp",EDGE,"E2"),sQuery(id+"F0.wireOp",EDGE,"E3.2.0"),sQuery(id+"F0.wireOp",EDGE,"E3.3.0"),sQuery(id+"F0.wireOp",EDGE,"E3.4.0"),sQuery(id+"F0.wireOp",EDGE,"E3.5.0"),subQ0,sQuery(id+"F0.wireOp",EDGE,"E3.7.0"),sQuery(id+"F0.wireOp",EDGE,"E3.8.0"),sQuery(id+"F0.wireOp",EDGE,"E3.9.0"),sQuery(id+"F0.wireOp",EDGE,"E3.10.0"),sQuery(id+"F0.wireOp",EDGE,"E4"),sQuery(id+"F0.wireOp",EDGE,"E5"),sQuery(id+"F0.wireOp",EDGE,"E6"),sQuery(id+"F0.wireOp",EDGE,"E7"),sQuery(id+"F0.wireOp",EDGE,"E8"),sQuery(id+"F0.wireOp",EDGE,"E9"),sQuery(id+"F0.wireOp",EDGE,"E10"),sQuery(id+"F0.wireOp",EDGE,"E11"),sQuery(id+"F0.wireOp",EDGE,"E12"),sQuery(id+"F0.wireOp",EDGE,"E13"),sQuery(id+"F0.wireOp",EDGE,"E14"),sQuery(id+"F0.wireOp",EDGE,"E15"),sQuery(id+"F0.wireOp",EDGE,"E16"),sQuery(id+"F0.wireOp",EDGE,"E17"),sQuery(id+"F0.wireOp",EDGE,"E18.MirrorCS"),sQuery(id+"F0.wireOp",EDGE,"E19.MirrorCS"),sQuery(id+"F0.wireOp",EDGE,"E20.MirrorCS"),sQuery(id+"F0.wireOp",EDGE,"E21.MirrorCS"),sQuery(id+"F0.wireOp",EDGE,"E22.MirrorCS"),sQuery(id+"F0.wireOp",EDGE,"E23.MirrorCS"),sQuery(id+"F0.wireOp",EDGE,"E24.MirrorCS"),sQuery(id+"F0.wireOp",EDGE,"E25.MirrorCS"),sQuery(id+"F0.wireOp",EDGE,"E26.MirrorCS"),sQuery(id+"F0.wireOp",EDGE,"E27.MirrorCS"),sQuery(id+"F0.wireOp",EDGE,"E28.MirrorCS"),sQuery(id+"F0.wireOp",EDGE,"E29.MirrorCS"),sQuery(id+"F0.wireOp",EDGE,"E30.MirrorCS"),sQuery(id+"F0.wireOp",EDGE,"E31.MirrorCS")])],"isStart":false})]}),makeQuery(id+"F6.opExtrude","CAP_EDGE",EDGE,{"disambiguationData":[OSD([sQuery(id+"F5.wireOp",EDGE,"E53.0")])],"isStart":true})]});}
            var Q35;
            Q35=makeQuery(id+"F6.boolean.opBoolean","COPY",EDGE,{"derivedFrom":makeQuery(id+"F6.opExtrude","CAP_EDGE",EDGE,{"disambiguationData":[OSD([sQuery(id+"F5.wireOp",EDGE,"E53.0")])],"isStart":false})});
            var Q36;
            Q36=makeQuery(id+"F6.boolean.opBoolean","COPY",EDGE,{"derivedFrom":makeQuery(id+"F6.opExtrude","CAP_EDGE",EDGE,{"disambiguationData":[OSD([sQuery(id+"F5.wireOp",EDGE,"E52.0")])],"isStart":false})});
            var Q37;
            {var subQ0=sQuery(id+"F0.wireOp",EDGE,"E1.6");Q37=makeQuery(id+"F6.boolean.opBoolean","MERGE",EDGE,{"derivedFrom":[makeQuery(id+"F2.opFillet","BLEND_EDGE",EDGE,{"blendedFrom":[makeQuery(id+"F1.opExtrude","CAP_EDGE",EDGE,{"disambiguationData":[OSD([subQ0])],"isStart":false}),makeQuery(id+"F1.opExtrude","CAP_FACE",FACE,{"disambiguationData":[OSD([sQuery(id+"F0.wireOp",EDGE,"E0"),sQuery(id+"F0.wireOp",EDGE,"E1.0"),sQuery(id+"F0.wireOp",EDGE,"E1.1"),sQuery(id+"F0.wireOp",EDGE,"E1.2"),sQuery(id+"F0.wireOp",EDGE,"E1.3"),sQuery(id+"F0.wireOp",EDGE,"E1.4"),sQuery(id+"F0.wireOp",EDGE,"E1.5"),subQ0,sQuery(id+"F0.wireOp",EDGE,"E1.7"),sQuery(id+"F0.wireOp",EDGE,"E1.8"),sQuery(id+"F0.wireOp",EDGE,"E1.9"),sQuery(id+"F0.wireOp",EDGE,"E1.10"),sQuery(id+"F0.wireOp",EDGE,"E2"),sQuery(id+"F0.wireOp",EDGE,"E3.2.0"),sQuery(id+"F0.wireOp",EDGE,"E3.3.0"),sQuery(id+"F0.wireOp",EDGE,"E3.4.0"),sQuery(id+"F0.wireOp",EDGE,"E3.5.0"),sQuery(id+"F0.wireOp",EDGE,"E3.6.0"),sQuery(id+"F0.wireOp",EDGE,"E3.7.0"),sQuery(id+"F0.wireOp",EDGE,"E3.8.0"),sQuery(id+"F0.wireOp",EDGE,"E3.9.0"),sQuery(id+"F0.wireOp",EDGE,"E3.10.0"),sQuery(id+"F0.wireOp",EDGE,"E4"),sQuery(id+"F0.wireOp",EDGE,"E5"),sQuery(id+"F0.wireOp",EDGE,"E6"),sQuery(id+"F0.wireOp",EDGE,"E7"),sQuery(id+"F0.wireOp",EDGE,"E8"),sQuery(id+"F0.wireOp",EDGE,"E9"),sQuery(id+"F0.wireOp",EDGE,"E10"),sQuery(id+"F0.wireOp",EDGE,"E11"),sQuery(id+"F0.wireOp",EDGE,"E12"),sQuery(id+"F0.wireOp",EDGE,"E13"),sQuery(id+"F0.wireOp",EDGE,"E14"),sQuery(id+"F0.wireOp",EDGE,"E15"),sQuery(id+"F0.wireOp",EDGE,"E16"),sQuery(id+"F0.wireOp",EDGE,"E17"),sQuery(id+"F0.wireOp",EDGE,"E18.MirrorCS"),sQuery(id+"F0.wireOp",EDGE,"E19.MirrorCS"),sQuery(id+"F0.wireOp",EDGE,"E20.MirrorCS"),sQuery(id+"F0.wireOp",EDGE,"E21.MirrorCS"),sQuery(id+"F0.wireOp",EDGE,"E22.MirrorCS"),sQuery(id+"F0.wireOp",EDGE,"E23.MirrorCS"),sQuery(id+"F0.wireOp",EDGE,"E24.MirrorCS"),sQuery(id+"F0.wireOp",EDGE,"E25.MirrorCS"),sQuery(id+"F0.wireOp",EDGE,"E26.MirrorCS"),sQuery(id+"F0.wireOp",EDGE,"E27.MirrorCS"),sQuery(id+"F0.wireOp",EDGE,"E28.MirrorCS"),sQuery(id+"F0.wireOp",EDGE,"E29.MirrorCS"),sQuery(id+"F0.wireOp",EDGE,"E30.MirrorCS"),sQuery(id+"F0.wireOp",EDGE,"E31.MirrorCS")])],"isStart":false})],"blendedInto":[makeQuery(id+"F1.opExtrude","CAP_FACE",FACE,{"disambiguationData":[OSD([sQuery(id+"F0.wireOp",EDGE,"E0"),sQuery(id+"F0.wireOp",EDGE,"E1.0"),sQuery(id+"F0.wireOp",EDGE,"E1.1"),sQuery(id+"F0.wireOp",EDGE,"E1.2"),sQuery(id+"F0.wireOp",EDGE,"E1.3"),sQuery(id+"F0.wireOp",EDGE,"E1.4"),sQuery(id+"F0.wireOp",EDGE,"E1.5"),subQ0,sQuery(id+"F0.wireOp",EDGE,"E1.7"),sQuery(id+"F0.wireOp",EDGE,"E1.8"),sQuery(id+"F0.wireOp",EDGE,"E1.9"),sQuery(id+"F0.wireOp",EDGE,"E1.10"),sQuery(id+"F0.wireOp",EDGE,"E2"),sQuery(id+"F0.wireOp",EDGE,"E3.2.0"),sQuery(id+"F0.wireOp",EDGE,"E3.3.0"),sQuery(id+"F0.wireOp",EDGE,"E3.4.0"),sQuery(id+"F0.wireOp",EDGE,"E3.5.0"),sQuery(id+"F0.wireOp",EDGE,"E3.6.0"),sQuery(id+"F0.wireOp",EDGE,"E3.7.0"),sQuery(id+"F0.wireOp",EDGE,"E3.8.0"),sQuery(id+"F0.wireOp",EDGE,"E3.9.0"),sQuery(id+"F0.wireOp",EDGE,"E3.10.0"),sQuery(id+"F0.wireOp",EDGE,"E4"),sQuery(id+"F0.wireOp",EDGE,"E5"),sQuery(id+"F0.wireOp",EDGE,"E6"),sQuery(id+"F0.wireOp",EDGE,"E7"),sQuery(id+"F0.wireOp",EDGE,"E8"),sQuery(id+"F0.wireOp",EDGE,"E9"),sQuery(id+"F0.wireOp",EDGE,"E10"),sQuery(id+"F0.wireOp",EDGE,"E11"),sQuery(id+"F0.wireOp",EDGE,"E12"),sQuery(id+"F0.wireOp",EDGE,"E13"),sQuery(id+"F0.wireOp",EDGE,"E14"),sQuery(id+"F0.wireOp",EDGE,"E15"),sQuery(id+"F0.wireOp",EDGE,"E16"),sQuery(id+"F0.wireOp",EDGE,"E17"),sQuery(id+"F0.wireOp",EDGE,"E18.MirrorCS"),sQuery(id+"F0.wireOp",EDGE,"E19.MirrorCS"),sQuery(id+"F0.wireOp",EDGE,"E20.MirrorCS"),sQuery(id+"F0.wireOp",EDGE,"E21.MirrorCS"),sQuery(id+"F0.wireOp",EDGE,"E22.MirrorCS"),sQuery(id+"F0.wireOp",EDGE,"E23.MirrorCS"),sQuery(id+"F0.wireOp",EDGE,"E24.MirrorCS"),sQuery(id+"F0.wireOp",EDGE,"E25.MirrorCS"),sQuery(id+"F0.wireOp",EDGE,"E26.MirrorCS"),sQuery(id+"F0.wireOp",EDGE,"E27.MirrorCS"),sQuery(id+"F0.wireOp",EDGE,"E28.MirrorCS"),sQuery(id+"F0.wireOp",EDGE,"E29.MirrorCS"),sQuery(id+"F0.wireOp",EDGE,"E30.MirrorCS"),sQuery(id+"F0.wireOp",EDGE,"E31.MirrorCS")])],"isStart":false})]}),makeQuery(id+"F6.opExtrude","CAP_EDGE",EDGE,{"disambiguationData":[OSD([sQuery(id+"F5.wireOp",EDGE,"E52.0")])],"isStart":true})]});}
            var Q38;
            {var subQ0=sQuery(id+"F0.wireOp",EDGE,"E3.5.0");Q38=makeQuery(id+"F6.boolean.opBoolean","MERGE",EDGE,{"derivedFrom":[makeQuery(id+"F2.opFillet","BLEND_EDGE",EDGE,{"blendedFrom":[makeQuery(id+"F1.opExtrude","CAP_EDGE",EDGE,{"disambiguationData":[OSD([subQ0])],"isStart":false}),makeQuery(id+"F1.opExtrude","CAP_FACE",FACE,{"disambiguationData":[OSD([sQuery(id+"F0.wireOp",EDGE,"E0"),sQuery(id+"F0.wireOp",EDGE,"E1.0"),sQuery(id+"F0.wireOp",EDGE,"E1.1"),sQuery(id+"F0.wireOp",EDGE,"E1.2"),sQuery(id+"F0.wireOp",EDGE,"E1.3"),sQuery(id+"F0.wireOp",EDGE,"E1.4"),sQuery(id+"F0.wireOp",EDGE,"E1.5"),sQuery(id+"F0.wireOp",EDGE,"E1.6"),sQuery(id+"F0.wireOp",EDGE,"E1.7"),sQuery(id+"F0.wireOp",EDGE,"E1.8"),sQuery(id+"F0.wireOp",EDGE,"E1.9"),sQuery(id+"F0.wireOp",EDGE,"E1.10"),sQuery(id+"F0.wireOp",EDGE,"E2"),sQuery(id+"F0.wireOp",EDGE,"E3.2.0"),sQuery(id+"F0.wireOp",EDGE,"E3.3.0"),sQuery(id+"F0.wireOp",EDGE,"E3.4.0"),subQ0,sQuery(id+"F0.wireOp",EDGE,"E3.6.0"),sQuery(id+"F0.wireOp",EDGE,"E3.7.0"),sQuery(id+"F0.wireOp",EDGE,"E3.8.0"),sQuery(id+"F0.wireOp",EDGE,"E3.9.0"),sQuery(id+"F0.wireOp",EDGE,"E3.10.0"),sQuery(id+"F0.wireOp",EDGE,"E4"),sQuery(id+"F0.wireOp",EDGE,"E5"),sQuery(id+"F0.wireOp",EDGE,"E6"),sQuery(id+"F0.wireOp",EDGE,"E7"),sQuery(id+"F0.wireOp",EDGE,"E8"),sQuery(id+"F0.wireOp",EDGE,"E9"),sQuery(id+"F0.wireOp",EDGE,"E10"),sQuery(id+"F0.wireOp",EDGE,"E11"),sQuery(id+"F0.wireOp",EDGE,"E12"),sQuery(id+"F0.wireOp",EDGE,"E13"),sQuery(id+"F0.wireOp",EDGE,"E14"),sQuery(id+"F0.wireOp",EDGE,"E15"),sQuery(id+"F0.wireOp",EDGE,"E16"),sQuery(id+"F0.wireOp",EDGE,"E17"),sQuery(id+"F0.wireOp",EDGE,"E18.MirrorCS"),sQuery(id+"F0.wireOp",EDGE,"E19.MirrorCS"),sQuery(id+"F0.wireOp",EDGE,"E20.MirrorCS"),sQuery(id+"F0.wireOp",EDGE,"E21.MirrorCS"),sQuery(id+"F0.wireOp",EDGE,"E22.MirrorCS"),sQuery(id+"F0.wireOp",EDGE,"E23.MirrorCS"),sQuery(id+"F0.wireOp",EDGE,"E24.MirrorCS"),sQuery(id+"F0.wireOp",EDGE,"E25.MirrorCS"),sQuery(id+"F0.wireOp",EDGE,"E26.MirrorCS"),sQuery(id+"F0.wireOp",EDGE,"E27.MirrorCS"),sQuery(id+"F0.wireOp",EDGE,"E28.MirrorCS"),sQuery(id+"F0.wireOp",EDGE,"E29.MirrorCS"),sQuery(id+"F0.wireOp",EDGE,"E30.MirrorCS"),sQuery(id+"F0.wireOp",EDGE,"E31.MirrorCS")])],"isStart":false})],"blendedInto":[makeQuery(id+"F1.opExtrude","CAP_FACE",FACE,{"disambiguationData":[OSD([sQuery(id+"F0.wireOp",EDGE,"E0"),sQuery(id+"F0.wireOp",EDGE,"E1.0"),sQuery(id+"F0.wireOp",EDGE,"E1.1"),sQuery(id+"F0.wireOp",EDGE,"E1.2"),sQuery(id+"F0.wireOp",EDGE,"E1.3"),sQuery(id+"F0.wireOp",EDGE,"E1.4"),sQuery(id+"F0.wireOp",EDGE,"E1.5"),sQuery(id+"F0.wireOp",EDGE,"E1.6"),sQuery(id+"F0.wireOp",EDGE,"E1.7"),sQuery(id+"F0.wireOp",EDGE,"E1.8"),sQuery(id+"F0.wireOp",EDGE,"E1.9"),sQuery(id+"F0.wireOp",EDGE,"E1.10"),sQuery(id+"F0.wireOp",EDGE,"E2"),sQuery(id+"F0.wireOp",EDGE,"E3.2.0"),sQuery(id+"F0.wireOp",EDGE,"E3.3.0"),sQuery(id+"F0.wireOp",EDGE,"E3.4.0"),subQ0,sQuery(id+"F0.wireOp",EDGE,"E3.6.0"),sQuery(id+"F0.wireOp",EDGE,"E3.7.0"),sQuery(id+"F0.wireOp",EDGE,"E3.8.0"),sQuery(id+"F0.wireOp",EDGE,"E3.9.0"),sQuery(id+"F0.wireOp",EDGE,"E3.10.0"),sQuery(id+"F0.wireOp",EDGE,"E4"),sQuery(id+"F0.wireOp",EDGE,"E5"),sQuery(id+"F0.wireOp",EDGE,"E6"),sQuery(id+"F0.wireOp",EDGE,"E7"),sQuery(id+"F0.wireOp",EDGE,"E8"),sQuery(id+"F0.wireOp",EDGE,"E9"),sQuery(id+"F0.wireOp",EDGE,"E10"),sQuery(id+"F0.wireOp",EDGE,"E11"),sQuery(id+"F0.wireOp",EDGE,"E12"),sQuery(id+"F0.wireOp",EDGE,"E13"),sQuery(id+"F0.wireOp",EDGE,"E14"),sQuery(id+"F0.wireOp",EDGE,"E15"),sQuery(id+"F0.wireOp",EDGE,"E16"),sQuery(id+"F0.wireOp",EDGE,"E17"),sQuery(id+"F0.wireOp",EDGE,"E18.MirrorCS"),sQuery(id+"F0.wireOp",EDGE,"E19.MirrorCS"),sQuery(id+"F0.wireOp",EDGE,"E20.MirrorCS"),sQuery(id+"F0.wireOp",EDGE,"E21.MirrorCS"),sQuery(id+"F0.wireOp",EDGE,"E22.MirrorCS"),sQuery(id+"F0.wireOp",EDGE,"E23.MirrorCS"),sQuery(id+"F0.wireOp",EDGE,"E24.MirrorCS"),sQuery(id+"F0.wireOp",EDGE,"E25.MirrorCS"),sQuery(id+"F0.wireOp",EDGE,"E26.MirrorCS"),sQuery(id+"F0.wireOp",EDGE,"E27.MirrorCS"),sQuery(id+"F0.wireOp",EDGE,"E28.MirrorCS"),sQuery(id+"F0.wireOp",EDGE,"E29.MirrorCS"),sQuery(id+"F0.wireOp",EDGE,"E30.MirrorCS"),sQuery(id+"F0.wireOp",EDGE,"E31.MirrorCS")])],"isStart":false})]}),makeQuery(id+"F6.opExtrude","CAP_EDGE",EDGE,{"disambiguationData":[OSD([sQuery(id+"F5.wireOp",EDGE,"E51.0")])],"isStart":true})]});}
            var Q39;
            Q39=makeQuery(id+"F6.boolean.opBoolean","COPY",EDGE,{"derivedFrom":makeQuery(id+"F6.opExtrude","CAP_EDGE",EDGE,{"disambiguationData":[OSD([sQuery(id+"F5.wireOp",EDGE,"E51.0")])],"isStart":false})});
            var Q40;
            {var subQ0=sQuery(id+"F0.wireOp",EDGE,"E1.7");Q40=makeQuery(id+"F6.boolean.opBoolean","MERGE",EDGE,{"derivedFrom":[makeQuery(id+"F2.opFillet","BLEND_EDGE",EDGE,{"blendedFrom":[makeQuery(id+"F1.opExtrude","CAP_EDGE",EDGE,{"disambiguationData":[OSD([subQ0])],"isStart":false}),makeQuery(id+"F1.opExtrude","CAP_FACE",FACE,{"disambiguationData":[OSD([sQuery(id+"F0.wireOp",EDGE,"E0"),sQuery(id+"F0.wireOp",EDGE,"E1.0"),sQuery(id+"F0.wireOp",EDGE,"E1.1"),sQuery(id+"F0.wireOp",EDGE,"E1.2"),sQuery(id+"F0.wireOp",EDGE,"E1.3"),sQuery(id+"F0.wireOp",EDGE,"E1.4"),sQuery(id+"F0.wireOp",EDGE,"E1.5"),sQuery(id+"F0.wireOp",EDGE,"E1.6"),subQ0,sQuery(id+"F0.wireOp",EDGE,"E1.8"),sQuery(id+"F0.wireOp",EDGE,"E1.9"),sQuery(id+"F0.wireOp",EDGE,"E1.10"),sQuery(id+"F0.wireOp",EDGE,"E2"),sQuery(id+"F0.wireOp",EDGE,"E3.2.0"),sQuery(id+"F0.wireOp",EDGE,"E3.3.0"),sQuery(id+"F0.wireOp",EDGE,"E3.4.0"),sQuery(id+"F0.wireOp",EDGE,"E3.5.0"),sQuery(id+"F0.wireOp",EDGE,"E3.6.0"),sQuery(id+"F0.wireOp",EDGE,"E3.7.0"),sQuery(id+"F0.wireOp",EDGE,"E3.8.0"),sQuery(id+"F0.wireOp",EDGE,"E3.9.0"),sQuery(id+"F0.wireOp",EDGE,"E3.10.0"),sQuery(id+"F0.wireOp",EDGE,"E4"),sQuery(id+"F0.wireOp",EDGE,"E5"),sQuery(id+"F0.wireOp",EDGE,"E6"),sQuery(id+"F0.wireOp",EDGE,"E7"),sQuery(id+"F0.wireOp",EDGE,"E8"),sQuery(id+"F0.wireOp",EDGE,"E9"),sQuery(id+"F0.wireOp",EDGE,"E10"),sQuery(id+"F0.wireOp",EDGE,"E11"),sQuery(id+"F0.wireOp",EDGE,"E12"),sQuery(id+"F0.wireOp",EDGE,"E13"),sQuery(id+"F0.wireOp",EDGE,"E14"),sQuery(id+"F0.wireOp",EDGE,"E15"),sQuery(id+"F0.wireOp",EDGE,"E16"),sQuery(id+"F0.wireOp",EDGE,"E17"),sQuery(id+"F0.wireOp",EDGE,"E18.MirrorCS"),sQuery(id+"F0.wireOp",EDGE,"E19.MirrorCS"),sQuery(id+"F0.wireOp",EDGE,"E20.MirrorCS"),sQuery(id+"F0.wireOp",EDGE,"E21.MirrorCS"),sQuery(id+"F0.wireOp",EDGE,"E22.MirrorCS"),sQuery(id+"F0.wireOp",EDGE,"E23.MirrorCS"),sQuery(id+"F0.wireOp",EDGE,"E24.MirrorCS"),sQuery(id+"F0.wireOp",EDGE,"E25.MirrorCS"),sQuery(id+"F0.wireOp",EDGE,"E26.MirrorCS"),sQuery(id+"F0.wireOp",EDGE,"E27.MirrorCS"),sQuery(id+"F0.wireOp",EDGE,"E28.MirrorCS"),sQuery(id+"F0.wireOp",EDGE,"E29.MirrorCS"),sQuery(id+"F0.wireOp",EDGE,"E30.MirrorCS"),sQuery(id+"F0.wireOp",EDGE,"E31.MirrorCS")])],"isStart":false})],"blendedInto":[makeQuery(id+"F1.opExtrude","CAP_FACE",FACE,{"disambiguationData":[OSD([sQuery(id+"F0.wireOp",EDGE,"E0"),sQuery(id+"F0.wireOp",EDGE,"E1.0"),sQuery(id+"F0.wireOp",EDGE,"E1.1"),sQuery(id+"F0.wireOp",EDGE,"E1.2"),sQuery(id+"F0.wireOp",EDGE,"E1.3"),sQuery(id+"F0.wireOp",EDGE,"E1.4"),sQuery(id+"F0.wireOp",EDGE,"E1.5"),sQuery(id+"F0.wireOp",EDGE,"E1.6"),subQ0,sQuery(id+"F0.wireOp",EDGE,"E1.8"),sQuery(id+"F0.wireOp",EDGE,"E1.9"),sQuery(id+"F0.wireOp",EDGE,"E1.10"),sQuery(id+"F0.wireOp",EDGE,"E2"),sQuery(id+"F0.wireOp",EDGE,"E3.2.0"),sQuery(id+"F0.wireOp",EDGE,"E3.3.0"),sQuery(id+"F0.wireOp",EDGE,"E3.4.0"),sQuery(id+"F0.wireOp",EDGE,"E3.5.0"),sQuery(id+"F0.wireOp",EDGE,"E3.6.0"),sQuery(id+"F0.wireOp",EDGE,"E3.7.0"),sQuery(id+"F0.wireOp",EDGE,"E3.8.0"),sQuery(id+"F0.wireOp",EDGE,"E3.9.0"),sQuery(id+"F0.wireOp",EDGE,"E3.10.0"),sQuery(id+"F0.wireOp",EDGE,"E4"),sQuery(id+"F0.wireOp",EDGE,"E5"),sQuery(id+"F0.wireOp",EDGE,"E6"),sQuery(id+"F0.wireOp",EDGE,"E7"),sQuery(id+"F0.wireOp",EDGE,"E8"),sQuery(id+"F0.wireOp",EDGE,"E9"),sQuery(id+"F0.wireOp",EDGE,"E10"),sQuery(id+"F0.wireOp",EDGE,"E11"),sQuery(id+"F0.wireOp",EDGE,"E12"),sQuery(id+"F0.wireOp",EDGE,"E13"),sQuery(id+"F0.wireOp",EDGE,"E14"),sQuery(id+"F0.wireOp",EDGE,"E15"),sQuery(id+"F0.wireOp",EDGE,"E16"),sQuery(id+"F0.wireOp",EDGE,"E17"),sQuery(id+"F0.wireOp",EDGE,"E18.MirrorCS"),sQuery(id+"F0.wireOp",EDGE,"E19.MirrorCS"),sQuery(id+"F0.wireOp",EDGE,"E20.MirrorCS"),sQuery(id+"F0.wireOp",EDGE,"E21.MirrorCS"),sQuery(id+"F0.wireOp",EDGE,"E22.MirrorCS"),sQuery(id+"F0.wireOp",EDGE,"E23.MirrorCS"),sQuery(id+"F0.wireOp",EDGE,"E24.MirrorCS"),sQuery(id+"F0.wireOp",EDGE,"E25.MirrorCS"),sQuery(id+"F0.wireOp",EDGE,"E26.MirrorCS"),sQuery(id+"F0.wireOp",EDGE,"E27.MirrorCS"),sQuery(id+"F0.wireOp",EDGE,"E28.MirrorCS"),sQuery(id+"F0.wireOp",EDGE,"E29.MirrorCS"),sQuery(id+"F0.wireOp",EDGE,"E30.MirrorCS"),sQuery(id+"F0.wireOp",EDGE,"E31.MirrorCS")])],"isStart":false})]}),makeQuery(id+"F6.opExtrude","CAP_EDGE",EDGE,{"disambiguationData":[OSD([sQuery(id+"F5.wireOp",EDGE,"E50.0")])],"isStart":true})]});}
            var Q41;
            Q41=makeQuery(id+"F6.boolean.opBoolean","COPY",EDGE,{"derivedFrom":makeQuery(id+"F6.opExtrude","CAP_EDGE",EDGE,{"disambiguationData":[OSD([sQuery(id+"F5.wireOp",EDGE,"E50.0")])],"isStart":false})});
            var Q42;
            {var subQ0=sQuery(id+"F0.wireOp",EDGE,"E3.4.0");Q42=makeQuery(id+"F6.boolean.opBoolean","MERGE",EDGE,{"derivedFrom":[makeQuery(id+"F2.opFillet","BLEND_EDGE",EDGE,{"blendedFrom":[makeQuery(id+"F1.opExtrude","CAP_EDGE",EDGE,{"disambiguationData":[OSD([subQ0])],"isStart":false}),makeQuery(id+"F1.opExtrude","CAP_FACE",FACE,{"disambiguationData":[OSD([sQuery(id+"F0.wireOp",EDGE,"E0"),sQuery(id+"F0.wireOp",EDGE,"E1.0"),sQuery(id+"F0.wireOp",EDGE,"E1.1"),sQuery(id+"F0.wireOp",EDGE,"E1.2"),sQuery(id+"F0.wireOp",EDGE,"E1.3"),sQuery(id+"F0.wireOp",EDGE,"E1.4"),sQuery(id+"F0.wireOp",EDGE,"E1.5"),sQuery(id+"F0.wireOp",EDGE,"E1.6"),sQuery(id+"F0.wireOp",EDGE,"E1.7"),sQuery(id+"F0.wireOp",EDGE,"E1.8"),sQuery(id+"F0.wireOp",EDGE,"E1.9"),sQuery(id+"F0.wireOp",EDGE,"E1.10"),sQuery(id+"F0.wireOp",EDGE,"E2"),sQuery(id+"F0.wireOp",EDGE,"E3.2.0"),sQuery(id+"F0.wireOp",EDGE,"E3.3.0"),subQ0,sQuery(id+"F0.wireOp",EDGE,"E3.5.0"),sQuery(id+"F0.wireOp",EDGE,"E3.6.0"),sQuery(id+"F0.wireOp",EDGE,"E3.7.0"),sQuery(id+"F0.wireOp",EDGE,"E3.8.0"),sQuery(id+"F0.wireOp",EDGE,"E3.9.0"),sQuery(id+"F0.wireOp",EDGE,"E3.10.0"),sQuery(id+"F0.wireOp",EDGE,"E4"),sQuery(id+"F0.wireOp",EDGE,"E5"),sQuery(id+"F0.wireOp",EDGE,"E6"),sQuery(id+"F0.wireOp",EDGE,"E7"),sQuery(id+"F0.wireOp",EDGE,"E8"),sQuery(id+"F0.wireOp",EDGE,"E9"),sQuery(id+"F0.wireOp",EDGE,"E10"),sQuery(id+"F0.wireOp",EDGE,"E11"),sQuery(id+"F0.wireOp",EDGE,"E12"),sQuery(id+"F0.wireOp",EDGE,"E13"),sQuery(id+"F0.wireOp",EDGE,"E14"),sQuery(id+"F0.wireOp",EDGE,"E15"),sQuery(id+"F0.wireOp",EDGE,"E16"),sQuery(id+"F0.wireOp",EDGE,"E17"),sQuery(id+"F0.wireOp",EDGE,"E18.MirrorCS"),sQuery(id+"F0.wireOp",EDGE,"E19.MirrorCS"),sQuery(id+"F0.wireOp",EDGE,"E20.MirrorCS"),sQuery(id+"F0.wireOp",EDGE,"E21.MirrorCS"),sQuery(id+"F0.wireOp",EDGE,"E22.MirrorCS"),sQuery(id+"F0.wireOp",EDGE,"E23.MirrorCS"),sQuery(id+"F0.wireOp",EDGE,"E24.MirrorCS"),sQuery(id+"F0.wireOp",EDGE,"E25.MirrorCS"),sQuery(id+"F0.wireOp",EDGE,"E26.MirrorCS"),sQuery(id+"F0.wireOp",EDGE,"E27.MirrorCS"),sQuery(id+"F0.wireOp",EDGE,"E28.MirrorCS"),sQuery(id+"F0.wireOp",EDGE,"E29.MirrorCS"),sQuery(id+"F0.wireOp",EDGE,"E30.MirrorCS"),sQuery(id+"F0.wireOp",EDGE,"E31.MirrorCS")])],"isStart":false})],"blendedInto":[makeQuery(id+"F1.opExtrude","CAP_FACE",FACE,{"disambiguationData":[OSD([sQuery(id+"F0.wireOp",EDGE,"E0"),sQuery(id+"F0.wireOp",EDGE,"E1.0"),sQuery(id+"F0.wireOp",EDGE,"E1.1"),sQuery(id+"F0.wireOp",EDGE,"E1.2"),sQuery(id+"F0.wireOp",EDGE,"E1.3"),sQuery(id+"F0.wireOp",EDGE,"E1.4"),sQuery(id+"F0.wireOp",EDGE,"E1.5"),sQuery(id+"F0.wireOp",EDGE,"E1.6"),sQuery(id+"F0.wireOp",EDGE,"E1.7"),sQuery(id+"F0.wireOp",EDGE,"E1.8"),sQuery(id+"F0.wireOp",EDGE,"E1.9"),sQuery(id+"F0.wireOp",EDGE,"E1.10"),sQuery(id+"F0.wireOp",EDGE,"E2"),sQuery(id+"F0.wireOp",EDGE,"E3.2.0"),sQuery(id+"F0.wireOp",EDGE,"E3.3.0"),subQ0,sQuery(id+"F0.wireOp",EDGE,"E3.5.0"),sQuery(id+"F0.wireOp",EDGE,"E3.6.0"),sQuery(id+"F0.wireOp",EDGE,"E3.7.0"),sQuery(id+"F0.wireOp",EDGE,"E3.8.0"),sQuery(id+"F0.wireOp",EDGE,"E3.9.0"),sQuery(id+"F0.wireOp",EDGE,"E3.10.0"),sQuery(id+"F0.wireOp",EDGE,"E4"),sQuery(id+"F0.wireOp",EDGE,"E5"),sQuery(id+"F0.wireOp",EDGE,"E6"),sQuery(id+"F0.wireOp",EDGE,"E7"),sQuery(id+"F0.wireOp",EDGE,"E8"),sQuery(id+"F0.wireOp",EDGE,"E9"),sQuery(id+"F0.wireOp",EDGE,"E10"),sQuery(id+"F0.wireOp",EDGE,"E11"),sQuery(id+"F0.wireOp",EDGE,"E12"),sQuery(id+"F0.wireOp",EDGE,"E13"),sQuery(id+"F0.wireOp",EDGE,"E14"),sQuery(id+"F0.wireOp",EDGE,"E15"),sQuery(id+"F0.wireOp",EDGE,"E16"),sQuery(id+"F0.wireOp",EDGE,"E17"),sQuery(id+"F0.wireOp",EDGE,"E18.MirrorCS"),sQuery(id+"F0.wireOp",EDGE,"E19.MirrorCS"),sQuery(id+"F0.wireOp",EDGE,"E20.MirrorCS"),sQuery(id+"F0.wireOp",EDGE,"E21.MirrorCS"),sQuery(id+"F0.wireOp",EDGE,"E22.MirrorCS"),sQuery(id+"F0.wireOp",EDGE,"E23.MirrorCS"),sQuery(id+"F0.wireOp",EDGE,"E24.MirrorCS"),sQuery(id+"F0.wireOp",EDGE,"E25.MirrorCS"),sQuery(id+"F0.wireOp",EDGE,"E26.MirrorCS"),sQuery(id+"F0.wireOp",EDGE,"E27.MirrorCS"),sQuery(id+"F0.wireOp",EDGE,"E28.MirrorCS"),sQuery(id+"F0.wireOp",EDGE,"E29.MirrorCS"),sQuery(id+"F0.wireOp",EDGE,"E30.MirrorCS"),sQuery(id+"F0.wireOp",EDGE,"E31.MirrorCS")])],"isStart":false})]}),makeQuery(id+"F6.opExtrude","CAP_EDGE",EDGE,{"disambiguationData":[OSD([sQuery(id+"F5.wireOp",EDGE,"E49.0")])],"isStart":true})]});}
            var Q43;
            Q43=makeQuery(id+"F6.boolean.opBoolean","COPY",EDGE,{"derivedFrom":makeQuery(id+"F6.opExtrude","CAP_EDGE",EDGE,{"disambiguationData":[OSD([sQuery(id+"F5.wireOp",EDGE,"E49.0")])],"isStart":false})});
            var Q44;
            Q44=makeQuery(id+"F6.boolean.opBoolean","COPY",EDGE,{"derivedFrom":makeQuery(id+"F6.opExtrude","CAP_EDGE",EDGE,{"disambiguationData":[OSD([sQuery(id+"F5.wireOp",EDGE,"E48.0")])],"isStart":false})});
            var Q45;
            {var subQ0=sQuery(id+"F0.wireOp",EDGE,"E1.8");Q45=makeQuery(id+"F6.boolean.opBoolean","MERGE",EDGE,{"derivedFrom":[makeQuery(id+"F2.opFillet","BLEND_EDGE",EDGE,{"blendedFrom":[makeQuery(id+"F1.opExtrude","CAP_EDGE",EDGE,{"disambiguationData":[OSD([subQ0])],"isStart":false}),makeQuery(id+"F1.opExtrude","CAP_FACE",FACE,{"disambiguationData":[OSD([sQuery(id+"F0.wireOp",EDGE,"E0"),sQuery(id+"F0.wireOp",EDGE,"E1.0"),sQuery(id+"F0.wireOp",EDGE,"E1.1"),sQuery(id+"F0.wireOp",EDGE,"E1.2"),sQuery(id+"F0.wireOp",EDGE,"E1.3"),sQuery(id+"F0.wireOp",EDGE,"E1.4"),sQuery(id+"F0.wireOp",EDGE,"E1.5"),sQuery(id+"F0.wireOp",EDGE,"E1.6"),sQuery(id+"F0.wireOp",EDGE,"E1.7"),subQ0,sQuery(id+"F0.wireOp",EDGE,"E1.9"),sQuery(id+"F0.wireOp",EDGE,"E1.10"),sQuery(id+"F0.wireOp",EDGE,"E2"),sQuery(id+"F0.wireOp",EDGE,"E3.2.0"),sQuery(id+"F0.wireOp",EDGE,"E3.3.0"),sQuery(id+"F0.wireOp",EDGE,"E3.4.0"),sQuery(id+"F0.wireOp",EDGE,"E3.5.0"),sQuery(id+"F0.wireOp",EDGE,"E3.6.0"),sQuery(id+"F0.wireOp",EDGE,"E3.7.0"),sQuery(id+"F0.wireOp",EDGE,"E3.8.0"),sQuery(id+"F0.wireOp",EDGE,"E3.9.0"),sQuery(id+"F0.wireOp",EDGE,"E3.10.0"),sQuery(id+"F0.wireOp",EDGE,"E4"),sQuery(id+"F0.wireOp",EDGE,"E5"),sQuery(id+"F0.wireOp",EDGE,"E6"),sQuery(id+"F0.wireOp",EDGE,"E7"),sQuery(id+"F0.wireOp",EDGE,"E8"),sQuery(id+"F0.wireOp",EDGE,"E9"),sQuery(id+"F0.wireOp",EDGE,"E10"),sQuery(id+"F0.wireOp",EDGE,"E11"),sQuery(id+"F0.wireOp",EDGE,"E12"),sQuery(id+"F0.wireOp",EDGE,"E13"),sQuery(id+"F0.wireOp",EDGE,"E14"),sQuery(id+"F0.wireOp",EDGE,"E15"),sQuery(id+"F0.wireOp",EDGE,"E16"),sQuery(id+"F0.wireOp",EDGE,"E17"),sQuery(id+"F0.wireOp",EDGE,"E18.MirrorCS"),sQuery(id+"F0.wireOp",EDGE,"E19.MirrorCS"),sQuery(id+"F0.wireOp",EDGE,"E20.MirrorCS"),sQuery(id+"F0.wireOp",EDGE,"E21.MirrorCS"),sQuery(id+"F0.wireOp",EDGE,"E22.MirrorCS"),sQuery(id+"F0.wireOp",EDGE,"E23.MirrorCS"),sQuery(id+"F0.wireOp",EDGE,"E24.MirrorCS"),sQuery(id+"F0.wireOp",EDGE,"E25.MirrorCS"),sQuery(id+"F0.wireOp",EDGE,"E26.MirrorCS"),sQuery(id+"F0.wireOp",EDGE,"E27.MirrorCS"),sQuery(id+"F0.wireOp",EDGE,"E28.MirrorCS"),sQuery(id+"F0.wireOp",EDGE,"E29.MirrorCS"),sQuery(id+"F0.wireOp",EDGE,"E30.MirrorCS"),sQuery(id+"F0.wireOp",EDGE,"E31.MirrorCS")])],"isStart":false})],"blendedInto":[makeQuery(id+"F1.opExtrude","CAP_FACE",FACE,{"disambiguationData":[OSD([sQuery(id+"F0.wireOp",EDGE,"E0"),sQuery(id+"F0.wireOp",EDGE,"E1.0"),sQuery(id+"F0.wireOp",EDGE,"E1.1"),sQuery(id+"F0.wireOp",EDGE,"E1.2"),sQuery(id+"F0.wireOp",EDGE,"E1.3"),sQuery(id+"F0.wireOp",EDGE,"E1.4"),sQuery(id+"F0.wireOp",EDGE,"E1.5"),sQuery(id+"F0.wireOp",EDGE,"E1.6"),sQuery(id+"F0.wireOp",EDGE,"E1.7"),subQ0,sQuery(id+"F0.wireOp",EDGE,"E1.9"),sQuery(id+"F0.wireOp",EDGE,"E1.10"),sQuery(id+"F0.wireOp",EDGE,"E2"),sQuery(id+"F0.wireOp",EDGE,"E3.2.0"),sQuery(id+"F0.wireOp",EDGE,"E3.3.0"),sQuery(id+"F0.wireOp",EDGE,"E3.4.0"),sQuery(id+"F0.wireOp",EDGE,"E3.5.0"),sQuery(id+"F0.wireOp",EDGE,"E3.6.0"),sQuery(id+"F0.wireOp",EDGE,"E3.7.0"),sQuery(id+"F0.wireOp",EDGE,"E3.8.0"),sQuery(id+"F0.wireOp",EDGE,"E3.9.0"),sQuery(id+"F0.wireOp",EDGE,"E3.10.0"),sQuery(id+"F0.wireOp",EDGE,"E4"),sQuery(id+"F0.wireOp",EDGE,"E5"),sQuery(id+"F0.wireOp",EDGE,"E6"),sQuery(id+"F0.wireOp",EDGE,"E7"),sQuery(id+"F0.wireOp",EDGE,"E8"),sQuery(id+"F0.wireOp",EDGE,"E9"),sQuery(id+"F0.wireOp",EDGE,"E10"),sQuery(id+"F0.wireOp",EDGE,"E11"),sQuery(id+"F0.wireOp",EDGE,"E12"),sQuery(id+"F0.wireOp",EDGE,"E13"),sQuery(id+"F0.wireOp",EDGE,"E14"),sQuery(id+"F0.wireOp",EDGE,"E15"),sQuery(id+"F0.wireOp",EDGE,"E16"),sQuery(id+"F0.wireOp",EDGE,"E17"),sQuery(id+"F0.wireOp",EDGE,"E18.MirrorCS"),sQuery(id+"F0.wireOp",EDGE,"E19.MirrorCS"),sQuery(id+"F0.wireOp",EDGE,"E20.MirrorCS"),sQuery(id+"F0.wireOp",EDGE,"E21.MirrorCS"),sQuery(id+"F0.wireOp",EDGE,"E22.MirrorCS"),sQuery(id+"F0.wireOp",EDGE,"E23.MirrorCS"),sQuery(id+"F0.wireOp",EDGE,"E24.MirrorCS"),sQuery(id+"F0.wireOp",EDGE,"E25.MirrorCS"),sQuery(id+"F0.wireOp",EDGE,"E26.MirrorCS"),sQuery(id+"F0.wireOp",EDGE,"E27.MirrorCS"),sQuery(id+"F0.wireOp",EDGE,"E28.MirrorCS"),sQuery(id+"F0.wireOp",EDGE,"E29.MirrorCS"),sQuery(id+"F0.wireOp",EDGE,"E30.MirrorCS"),sQuery(id+"F0.wireOp",EDGE,"E31.MirrorCS")])],"isStart":false})]}),makeQuery(id+"F6.opExtrude","CAP_EDGE",EDGE,{"disambiguationData":[OSD([sQuery(id+"F5.wireOp",EDGE,"E48.0")])],"isStart":true})]});}
            var Q46;
            {var subQ0=sQuery(id+"F0.wireOp",EDGE,"E3.3.0");Q46=makeQuery(id+"F6.boolean.opBoolean","MERGE",EDGE,{"derivedFrom":[makeQuery(id+"F2.opFillet","BLEND_EDGE",EDGE,{"blendedFrom":[makeQuery(id+"F1.opExtrude","CAP_EDGE",EDGE,{"disambiguationData":[OSD([subQ0])],"isStart":false}),makeQuery(id+"F1.opExtrude","CAP_FACE",FACE,{"disambiguationData":[OSD([sQuery(id+"F0.wireOp",EDGE,"E0"),sQuery(id+"F0.wireOp",EDGE,"E1.0"),sQuery(id+"F0.wireOp",EDGE,"E1.1"),sQuery(id+"F0.wireOp",EDGE,"E1.2"),sQuery(id+"F0.wireOp",EDGE,"E1.3"),sQuery(id+"F0.wireOp",EDGE,"E1.4"),sQuery(id+"F0.wireOp",EDGE,"E1.5"),sQuery(id+"F0.wireOp",EDGE,"E1.6"),sQuery(id+"F0.wireOp",EDGE,"E1.7"),sQuery(id+"F0.wireOp",EDGE,"E1.8"),sQuery(id+"F0.wireOp",EDGE,"E1.9"),sQuery(id+"F0.wireOp",EDGE,"E1.10"),sQuery(id+"F0.wireOp",EDGE,"E2"),sQuery(id+"F0.wireOp",EDGE,"E3.2.0"),subQ0,sQuery(id+"F0.wireOp",EDGE,"E3.4.0"),sQuery(id+"F0.wireOp",EDGE,"E3.5.0"),sQuery(id+"F0.wireOp",EDGE,"E3.6.0"),sQuery(id+"F0.wireOp",EDGE,"E3.7.0"),sQuery(id+"F0.wireOp",EDGE,"E3.8.0"),sQuery(id+"F0.wireOp",EDGE,"E3.9.0"),sQuery(id+"F0.wireOp",EDGE,"E3.10.0"),sQuery(id+"F0.wireOp",EDGE,"E4"),sQuery(id+"F0.wireOp",EDGE,"E5"),sQuery(id+"F0.wireOp",EDGE,"E6"),sQuery(id+"F0.wireOp",EDGE,"E7"),sQuery(id+"F0.wireOp",EDGE,"E8"),sQuery(id+"F0.wireOp",EDGE,"E9"),sQuery(id+"F0.wireOp",EDGE,"E10"),sQuery(id+"F0.wireOp",EDGE,"E11"),sQuery(id+"F0.wireOp",EDGE,"E12"),sQuery(id+"F0.wireOp",EDGE,"E13"),sQuery(id+"F0.wireOp",EDGE,"E14"),sQuery(id+"F0.wireOp",EDGE,"E15"),sQuery(id+"F0.wireOp",EDGE,"E16"),sQuery(id+"F0.wireOp",EDGE,"E17"),sQuery(id+"F0.wireOp",EDGE,"E18.MirrorCS"),sQuery(id+"F0.wireOp",EDGE,"E19.MirrorCS"),sQuery(id+"F0.wireOp",EDGE,"E20.MirrorCS"),sQuery(id+"F0.wireOp",EDGE,"E21.MirrorCS"),sQuery(id+"F0.wireOp",EDGE,"E22.MirrorCS"),sQuery(id+"F0.wireOp",EDGE,"E23.MirrorCS"),sQuery(id+"F0.wireOp",EDGE,"E24.MirrorCS"),sQuery(id+"F0.wireOp",EDGE,"E25.MirrorCS"),sQuery(id+"F0.wireOp",EDGE,"E26.MirrorCS"),sQuery(id+"F0.wireOp",EDGE,"E27.MirrorCS"),sQuery(id+"F0.wireOp",EDGE,"E28.MirrorCS"),sQuery(id+"F0.wireOp",EDGE,"E29.MirrorCS"),sQuery(id+"F0.wireOp",EDGE,"E30.MirrorCS"),sQuery(id+"F0.wireOp",EDGE,"E31.MirrorCS")])],"isStart":false})],"blendedInto":[makeQuery(id+"F1.opExtrude","CAP_FACE",FACE,{"disambiguationData":[OSD([sQuery(id+"F0.wireOp",EDGE,"E0"),sQuery(id+"F0.wireOp",EDGE,"E1.0"),sQuery(id+"F0.wireOp",EDGE,"E1.1"),sQuery(id+"F0.wireOp",EDGE,"E1.2"),sQuery(id+"F0.wireOp",EDGE,"E1.3"),sQuery(id+"F0.wireOp",EDGE,"E1.4"),sQuery(id+"F0.wireOp",EDGE,"E1.5"),sQuery(id+"F0.wireOp",EDGE,"E1.6"),sQuery(id+"F0.wireOp",EDGE,"E1.7"),sQuery(id+"F0.wireOp",EDGE,"E1.8"),sQuery(id+"F0.wireOp",EDGE,"E1.9"),sQuery(id+"F0.wireOp",EDGE,"E1.10"),sQuery(id+"F0.wireOp",EDGE,"E2"),sQuery(id+"F0.wireOp",EDGE,"E3.2.0"),subQ0,sQuery(id+"F0.wireOp",EDGE,"E3.4.0"),sQuery(id+"F0.wireOp",EDGE,"E3.5.0"),sQuery(id+"F0.wireOp",EDGE,"E3.6.0"),sQuery(id+"F0.wireOp",EDGE,"E3.7.0"),sQuery(id+"F0.wireOp",EDGE,"E3.8.0"),sQuery(id+"F0.wireOp",EDGE,"E3.9.0"),sQuery(id+"F0.wireOp",EDGE,"E3.10.0"),sQuery(id+"F0.wireOp",EDGE,"E4"),sQuery(id+"F0.wireOp",EDGE,"E5"),sQuery(id+"F0.wireOp",EDGE,"E6"),sQuery(id+"F0.wireOp",EDGE,"E7"),sQuery(id+"F0.wireOp",EDGE,"E8"),sQuery(id+"F0.wireOp",EDGE,"E9"),sQuery(id+"F0.wireOp",EDGE,"E10"),sQuery(id+"F0.wireOp",EDGE,"E11"),sQuery(id+"F0.wireOp",EDGE,"E12"),sQuery(id+"F0.wireOp",EDGE,"E13"),sQuery(id+"F0.wireOp",EDGE,"E14"),sQuery(id+"F0.wireOp",EDGE,"E15"),sQuery(id+"F0.wireOp",EDGE,"E16"),sQuery(id+"F0.wireOp",EDGE,"E17"),sQuery(id+"F0.wireOp",EDGE,"E18.MirrorCS"),sQuery(id+"F0.wireOp",EDGE,"E19.MirrorCS"),sQuery(id+"F0.wireOp",EDGE,"E20.MirrorCS"),sQuery(id+"F0.wireOp",EDGE,"E21.MirrorCS"),sQuery(id+"F0.wireOp",EDGE,"E22.MirrorCS"),sQuery(id+"F0.wireOp",EDGE,"E23.MirrorCS"),sQuery(id+"F0.wireOp",EDGE,"E24.MirrorCS"),sQuery(id+"F0.wireOp",EDGE,"E25.MirrorCS"),sQuery(id+"F0.wireOp",EDGE,"E26.MirrorCS"),sQuery(id+"F0.wireOp",EDGE,"E27.MirrorCS"),sQuery(id+"F0.wireOp",EDGE,"E28.MirrorCS"),sQuery(id+"F0.wireOp",EDGE,"E29.MirrorCS"),sQuery(id+"F0.wireOp",EDGE,"E30.MirrorCS"),sQuery(id+"F0.wireOp",EDGE,"E31.MirrorCS")])],"isStart":false})]}),makeQuery(id+"F6.opExtrude","CAP_EDGE",EDGE,{"disambiguationData":[OSD([sQuery(id+"F5.wireOp",EDGE,"E47.0")])],"isStart":true})]});}
            var Q47;
            Q47=makeQuery(id+"F6.boolean.opBoolean","COPY",EDGE,{"derivedFrom":makeQuery(id+"F6.opExtrude","CAP_EDGE",EDGE,{"disambiguationData":[OSD([sQuery(id+"F5.wireOp",EDGE,"E47.0")])],"isStart":false})});
            var Q48;
            Q48=makeQuery(id+"F6.boolean.opBoolean","COPY",EDGE,{"derivedFrom":makeQuery(id+"F6.opExtrude","CAP_EDGE",EDGE,{"disambiguationData":[OSD([sQuery(id+"F5.wireOp",EDGE,"E46.0")])],"isStart":false})});
            var Q49;
            {var subQ0=sQuery(id+"F0.wireOp",EDGE,"E1.9");Q49=makeQuery(id+"F6.boolean.opBoolean","MERGE",EDGE,{"derivedFrom":[makeQuery(id+"F2.opFillet","BLEND_EDGE",EDGE,{"blendedFrom":[makeQuery(id+"F1.opExtrude","CAP_EDGE",EDGE,{"disambiguationData":[OSD([subQ0])],"isStart":false}),makeQuery(id+"F1.opExtrude","CAP_FACE",FACE,{"disambiguationData":[OSD([sQuery(id+"F0.wireOp",EDGE,"E0"),sQuery(id+"F0.wireOp",EDGE,"E1.0"),sQuery(id+"F0.wireOp",EDGE,"E1.1"),sQuery(id+"F0.wireOp",EDGE,"E1.2"),sQuery(id+"F0.wireOp",EDGE,"E1.3"),sQuery(id+"F0.wireOp",EDGE,"E1.4"),sQuery(id+"F0.wireOp",EDGE,"E1.5"),sQuery(id+"F0.wireOp",EDGE,"E1.6"),sQuery(id+"F0.wireOp",EDGE,"E1.7"),sQuery(id+"F0.wireOp",EDGE,"E1.8"),subQ0,sQuery(id+"F0.wireOp",EDGE,"E1.10"),sQuery(id+"F0.wireOp",EDGE,"E2"),sQuery(id+"F0.wireOp",EDGE,"E3.2.0"),sQuery(id+"F0.wireOp",EDGE,"E3.3.0"),sQuery(id+"F0.wireOp",EDGE,"E3.4.0"),sQuery(id+"F0.wireOp",EDGE,"E3.5.0"),sQuery(id+"F0.wireOp",EDGE,"E3.6.0"),sQuery(id+"F0.wireOp",EDGE,"E3.7.0"),sQuery(id+"F0.wireOp",EDGE,"E3.8.0"),sQuery(id+"F0.wireOp",EDGE,"E3.9.0"),sQuery(id+"F0.wireOp",EDGE,"E3.10.0"),sQuery(id+"F0.wireOp",EDGE,"E4"),sQuery(id+"F0.wireOp",EDGE,"E5"),sQuery(id+"F0.wireOp",EDGE,"E6"),sQuery(id+"F0.wireOp",EDGE,"E7"),sQuery(id+"F0.wireOp",EDGE,"E8"),sQuery(id+"F0.wireOp",EDGE,"E9"),sQuery(id+"F0.wireOp",EDGE,"E10"),sQuery(id+"F0.wireOp",EDGE,"E11"),sQuery(id+"F0.wireOp",EDGE,"E12"),sQuery(id+"F0.wireOp",EDGE,"E13"),sQuery(id+"F0.wireOp",EDGE,"E14"),sQuery(id+"F0.wireOp",EDGE,"E15"),sQuery(id+"F0.wireOp",EDGE,"E16"),sQuery(id+"F0.wireOp",EDGE,"E17"),sQuery(id+"F0.wireOp",EDGE,"E18.MirrorCS"),sQuery(id+"F0.wireOp",EDGE,"E19.MirrorCS"),sQuery(id+"F0.wireOp",EDGE,"E20.MirrorCS"),sQuery(id+"F0.wireOp",EDGE,"E21.MirrorCS"),sQuery(id+"F0.wireOp",EDGE,"E22.MirrorCS"),sQuery(id+"F0.wireOp",EDGE,"E23.MirrorCS"),sQuery(id+"F0.wireOp",EDGE,"E24.MirrorCS"),sQuery(id+"F0.wireOp",EDGE,"E25.MirrorCS"),sQuery(id+"F0.wireOp",EDGE,"E26.MirrorCS"),sQuery(id+"F0.wireOp",EDGE,"E27.MirrorCS"),sQuery(id+"F0.wireOp",EDGE,"E28.MirrorCS"),sQuery(id+"F0.wireOp",EDGE,"E29.MirrorCS"),sQuery(id+"F0.wireOp",EDGE,"E30.MirrorCS"),sQuery(id+"F0.wireOp",EDGE,"E31.MirrorCS")])],"isStart":false})],"blendedInto":[makeQuery(id+"F1.opExtrude","CAP_FACE",FACE,{"disambiguationData":[OSD([sQuery(id+"F0.wireOp",EDGE,"E0"),sQuery(id+"F0.wireOp",EDGE,"E1.0"),sQuery(id+"F0.wireOp",EDGE,"E1.1"),sQuery(id+"F0.wireOp",EDGE,"E1.2"),sQuery(id+"F0.wireOp",EDGE,"E1.3"),sQuery(id+"F0.wireOp",EDGE,"E1.4"),sQuery(id+"F0.wireOp",EDGE,"E1.5"),sQuery(id+"F0.wireOp",EDGE,"E1.6"),sQuery(id+"F0.wireOp",EDGE,"E1.7"),sQuery(id+"F0.wireOp",EDGE,"E1.8"),subQ0,sQuery(id+"F0.wireOp",EDGE,"E1.10"),sQuery(id+"F0.wireOp",EDGE,"E2"),sQuery(id+"F0.wireOp",EDGE,"E3.2.0"),sQuery(id+"F0.wireOp",EDGE,"E3.3.0"),sQuery(id+"F0.wireOp",EDGE,"E3.4.0"),sQuery(id+"F0.wireOp",EDGE,"E3.5.0"),sQuery(id+"F0.wireOp",EDGE,"E3.6.0"),sQuery(id+"F0.wireOp",EDGE,"E3.7.0"),sQuery(id+"F0.wireOp",EDGE,"E3.8.0"),sQuery(id+"F0.wireOp",EDGE,"E3.9.0"),sQuery(id+"F0.wireOp",EDGE,"E3.10.0"),sQuery(id+"F0.wireOp",EDGE,"E4"),sQuery(id+"F0.wireOp",EDGE,"E5"),sQuery(id+"F0.wireOp",EDGE,"E6"),sQuery(id+"F0.wireOp",EDGE,"E7"),sQuery(id+"F0.wireOp",EDGE,"E8"),sQuery(id+"F0.wireOp",EDGE,"E9"),sQuery(id+"F0.wireOp",EDGE,"E10"),sQuery(id+"F0.wireOp",EDGE,"E11"),sQuery(id+"F0.wireOp",EDGE,"E12"),sQuery(id+"F0.wireOp",EDGE,"E13"),sQuery(id+"F0.wireOp",EDGE,"E14"),sQuery(id+"F0.wireOp",EDGE,"E15"),sQuery(id+"F0.wireOp",EDGE,"E16"),sQuery(id+"F0.wireOp",EDGE,"E17"),sQuery(id+"F0.wireOp",EDGE,"E18.MirrorCS"),sQuery(id+"F0.wireOp",EDGE,"E19.MirrorCS"),sQuery(id+"F0.wireOp",EDGE,"E20.MirrorCS"),sQuery(id+"F0.wireOp",EDGE,"E21.MirrorCS"),sQuery(id+"F0.wireOp",EDGE,"E22.MirrorCS"),sQuery(id+"F0.wireOp",EDGE,"E23.MirrorCS"),sQuery(id+"F0.wireOp",EDGE,"E24.MirrorCS"),sQuery(id+"F0.wireOp",EDGE,"E25.MirrorCS"),sQuery(id+"F0.wireOp",EDGE,"E26.MirrorCS"),sQuery(id+"F0.wireOp",EDGE,"E27.MirrorCS"),sQuery(id+"F0.wireOp",EDGE,"E28.MirrorCS"),sQuery(id+"F0.wireOp",EDGE,"E29.MirrorCS"),sQuery(id+"F0.wireOp",EDGE,"E30.MirrorCS"),sQuery(id+"F0.wireOp",EDGE,"E31.MirrorCS")])],"isStart":false})]}),makeQuery(id+"F6.opExtrude","CAP_EDGE",EDGE,{"disambiguationData":[OSD([sQuery(id+"F5.wireOp",EDGE,"E46.0")])],"isStart":true})]});}
            var Q50;
            {var subQ0=sQuery(id+"F0.wireOp",EDGE,"E3.2.0");Q50=makeQuery(id+"F6.boolean.opBoolean","MERGE",EDGE,{"derivedFrom":[makeQuery(id+"F2.opFillet","BLEND_EDGE",EDGE,{"blendedFrom":[makeQuery(id+"F1.opExtrude","CAP_EDGE",EDGE,{"disambiguationData":[OSD([subQ0])],"isStart":false}),makeQuery(id+"F1.opExtrude","CAP_FACE",FACE,{"disambiguationData":[OSD([sQuery(id+"F0.wireOp",EDGE,"E0"),sQuery(id+"F0.wireOp",EDGE,"E1.0"),sQuery(id+"F0.wireOp",EDGE,"E1.1"),sQuery(id+"F0.wireOp",EDGE,"E1.2"),sQuery(id+"F0.wireOp",EDGE,"E1.3"),sQuery(id+"F0.wireOp",EDGE,"E1.4"),sQuery(id+"F0.wireOp",EDGE,"E1.5"),sQuery(id+"F0.wireOp",EDGE,"E1.6"),sQuery(id+"F0.wireOp",EDGE,"E1.7"),sQuery(id+"F0.wireOp",EDGE,"E1.8"),sQuery(id+"F0.wireOp",EDGE,"E1.9"),sQuery(id+"F0.wireOp",EDGE,"E1.10"),sQuery(id+"F0.wireOp",EDGE,"E2"),subQ0,sQuery(id+"F0.wireOp",EDGE,"E3.3.0"),sQuery(id+"F0.wireOp",EDGE,"E3.4.0"),sQuery(id+"F0.wireOp",EDGE,"E3.5.0"),sQuery(id+"F0.wireOp",EDGE,"E3.6.0"),sQuery(id+"F0.wireOp",EDGE,"E3.7.0"),sQuery(id+"F0.wireOp",EDGE,"E3.8.0"),sQuery(id+"F0.wireOp",EDGE,"E3.9.0"),sQuery(id+"F0.wireOp",EDGE,"E3.10.0"),sQuery(id+"F0.wireOp",EDGE,"E4"),sQuery(id+"F0.wireOp",EDGE,"E5"),sQuery(id+"F0.wireOp",EDGE,"E6"),sQuery(id+"F0.wireOp",EDGE,"E7"),sQuery(id+"F0.wireOp",EDGE,"E8"),sQuery(id+"F0.wireOp",EDGE,"E9"),sQuery(id+"F0.wireOp",EDGE,"E10"),sQuery(id+"F0.wireOp",EDGE,"E11"),sQuery(id+"F0.wireOp",EDGE,"E12"),sQuery(id+"F0.wireOp",EDGE,"E13"),sQuery(id+"F0.wireOp",EDGE,"E14"),sQuery(id+"F0.wireOp",EDGE,"E15"),sQuery(id+"F0.wireOp",EDGE,"E16"),sQuery(id+"F0.wireOp",EDGE,"E17"),sQuery(id+"F0.wireOp",EDGE,"E18.MirrorCS"),sQuery(id+"F0.wireOp",EDGE,"E19.MirrorCS"),sQuery(id+"F0.wireOp",EDGE,"E20.MirrorCS"),sQuery(id+"F0.wireOp",EDGE,"E21.MirrorCS"),sQuery(id+"F0.wireOp",EDGE,"E22.MirrorCS"),sQuery(id+"F0.wireOp",EDGE,"E23.MirrorCS"),sQuery(id+"F0.wireOp",EDGE,"E24.MirrorCS"),sQuery(id+"F0.wireOp",EDGE,"E25.MirrorCS"),sQuery(id+"F0.wireOp",EDGE,"E26.MirrorCS"),sQuery(id+"F0.wireOp",EDGE,"E27.MirrorCS"),sQuery(id+"F0.wireOp",EDGE,"E28.MirrorCS"),sQuery(id+"F0.wireOp",EDGE,"E29.MirrorCS"),sQuery(id+"F0.wireOp",EDGE,"E30.MirrorCS"),sQuery(id+"F0.wireOp",EDGE,"E31.MirrorCS")])],"isStart":false})],"blendedInto":[makeQuery(id+"F1.opExtrude","CAP_FACE",FACE,{"disambiguationData":[OSD([sQuery(id+"F0.wireOp",EDGE,"E0"),sQuery(id+"F0.wireOp",EDGE,"E1.0"),sQuery(id+"F0.wireOp",EDGE,"E1.1"),sQuery(id+"F0.wireOp",EDGE,"E1.2"),sQuery(id+"F0.wireOp",EDGE,"E1.3"),sQuery(id+"F0.wireOp",EDGE,"E1.4"),sQuery(id+"F0.wireOp",EDGE,"E1.5"),sQuery(id+"F0.wireOp",EDGE,"E1.6"),sQuery(id+"F0.wireOp",EDGE,"E1.7"),sQuery(id+"F0.wireOp",EDGE,"E1.8"),sQuery(id+"F0.wireOp",EDGE,"E1.9"),sQuery(id+"F0.wireOp",EDGE,"E1.10"),sQuery(id+"F0.wireOp",EDGE,"E2"),subQ0,sQuery(id+"F0.wireOp",EDGE,"E3.3.0"),sQuery(id+"F0.wireOp",EDGE,"E3.4.0"),sQuery(id+"F0.wireOp",EDGE,"E3.5.0"),sQuery(id+"F0.wireOp",EDGE,"E3.6.0"),sQuery(id+"F0.wireOp",EDGE,"E3.7.0"),sQuery(id+"F0.wireOp",EDGE,"E3.8.0"),sQuery(id+"F0.wireOp",EDGE,"E3.9.0"),sQuery(id+"F0.wireOp",EDGE,"E3.10.0"),sQuery(id+"F0.wireOp",EDGE,"E4"),sQuery(id+"F0.wireOp",EDGE,"E5"),sQuery(id+"F0.wireOp",EDGE,"E6"),sQuery(id+"F0.wireOp",EDGE,"E7"),sQuery(id+"F0.wireOp",EDGE,"E8"),sQuery(id+"F0.wireOp",EDGE,"E9"),sQuery(id+"F0.wireOp",EDGE,"E10"),sQuery(id+"F0.wireOp",EDGE,"E11"),sQuery(id+"F0.wireOp",EDGE,"E12"),sQuery(id+"F0.wireOp",EDGE,"E13"),sQuery(id+"F0.wireOp",EDGE,"E14"),sQuery(id+"F0.wireOp",EDGE,"E15"),sQuery(id+"F0.wireOp",EDGE,"E16"),sQuery(id+"F0.wireOp",EDGE,"E17"),sQuery(id+"F0.wireOp",EDGE,"E18.MirrorCS"),sQuery(id+"F0.wireOp",EDGE,"E19.MirrorCS"),sQuery(id+"F0.wireOp",EDGE,"E20.MirrorCS"),sQuery(id+"F0.wireOp",EDGE,"E21.MirrorCS"),sQuery(id+"F0.wireOp",EDGE,"E22.MirrorCS"),sQuery(id+"F0.wireOp",EDGE,"E23.MirrorCS"),sQuery(id+"F0.wireOp",EDGE,"E24.MirrorCS"),sQuery(id+"F0.wireOp",EDGE,"E25.MirrorCS"),sQuery(id+"F0.wireOp",EDGE,"E26.MirrorCS"),sQuery(id+"F0.wireOp",EDGE,"E27.MirrorCS"),sQuery(id+"F0.wireOp",EDGE,"E28.MirrorCS"),sQuery(id+"F0.wireOp",EDGE,"E29.MirrorCS"),sQuery(id+"F0.wireOp",EDGE,"E30.MirrorCS"),sQuery(id+"F0.wireOp",EDGE,"E31.MirrorCS")])],"isStart":false})]}),makeQuery(id+"F6.opExtrude","CAP_EDGE",EDGE,{"disambiguationData":[OSD([sQuery(id+"F5.wireOp",EDGE,"E45.0")])],"isStart":true})]});}
            var Q51;
            Q51=makeQuery(id+"F6.boolean.opBoolean","COPY",EDGE,{"derivedFrom":makeQuery(id+"F6.opExtrude","CAP_EDGE",EDGE,{"disambiguationData":[OSD([sQuery(id+"F5.wireOp",EDGE,"E45.0")])],"isStart":false})});
            var Q52;
            {var subQ0=sQuery(id+"F0.wireOp",EDGE,"E0");Q52=makeQuery(id+"F6.boolean.opBoolean","MERGE",EDGE,{"derivedFrom":[makeQuery(id+"F2.opFillet","BLEND_EDGE",EDGE,{"blendedFrom":[makeQuery(id+"F1.opExtrude","CAP_EDGE",EDGE,{"disambiguationData":[OSD([subQ0])],"isStart":false}),makeQuery(id+"F1.opExtrude","CAP_FACE",FACE,{"disambiguationData":[OSD([subQ0,sQuery(id+"F0.wireOp",EDGE,"E1.0"),sQuery(id+"F0.wireOp",EDGE,"E1.1"),sQuery(id+"F0.wireOp",EDGE,"E1.2"),sQuery(id+"F0.wireOp",EDGE,"E1.3"),sQuery(id+"F0.wireOp",EDGE,"E1.4"),sQuery(id+"F0.wireOp",EDGE,"E1.5"),sQuery(id+"F0.wireOp",EDGE,"E1.6"),sQuery(id+"F0.wireOp",EDGE,"E1.7"),sQuery(id+"F0.wireOp",EDGE,"E1.8"),sQuery(id+"F0.wireOp",EDGE,"E1.9"),sQuery(id+"F0.wireOp",EDGE,"E1.10"),sQuery(id+"F0.wireOp",EDGE,"E2"),sQuery(id+"F0.wireOp",EDGE,"E3.2.0"),sQuery(id+"F0.wireOp",EDGE,"E3.3.0"),sQuery(id+"F0.wireOp",EDGE,"E3.4.0"),sQuery(id+"F0.wireOp",EDGE,"E3.5.0"),sQuery(id+"F0.wireOp",EDGE,"E3.6.0"),sQuery(id+"F0.wireOp",EDGE,"E3.7.0"),sQuery(id+"F0.wireOp",EDGE,"E3.8.0"),sQuery(id+"F0.wireOp",EDGE,"E3.9.0"),sQuery(id+"F0.wireOp",EDGE,"E3.10.0"),sQuery(id+"F0.wireOp",EDGE,"E4"),sQuery(id+"F0.wireOp",EDGE,"E5"),sQuery(id+"F0.wireOp",EDGE,"E6"),sQuery(id+"F0.wireOp",EDGE,"E7"),sQuery(id+"F0.wireOp",EDGE,"E8"),sQuery(id+"F0.wireOp",EDGE,"E9"),sQuery(id+"F0.wireOp",EDGE,"E10"),sQuery(id+"F0.wireOp",EDGE,"E11"),sQuery(id+"F0.wireOp",EDGE,"E12"),sQuery(id+"F0.wireOp",EDGE,"E13"),sQuery(id+"F0.wireOp",EDGE,"E14"),sQuery(id+"F0.wireOp",EDGE,"E15"),sQuery(id+"F0.wireOp",EDGE,"E16"),sQuery(id+"F0.wireOp",EDGE,"E17"),sQuery(id+"F0.wireOp",EDGE,"E18.MirrorCS"),sQuery(id+"F0.wireOp",EDGE,"E19.MirrorCS"),sQuery(id+"F0.wireOp",EDGE,"E20.MirrorCS"),sQuery(id+"F0.wireOp",EDGE,"E21.MirrorCS"),sQuery(id+"F0.wireOp",EDGE,"E22.MirrorCS"),sQuery(id+"F0.wireOp",EDGE,"E23.MirrorCS"),sQuery(id+"F0.wireOp",EDGE,"E24.MirrorCS"),sQuery(id+"F0.wireOp",EDGE,"E25.MirrorCS"),sQuery(id+"F0.wireOp",EDGE,"E26.MirrorCS"),sQuery(id+"F0.wireOp",EDGE,"E27.MirrorCS"),sQuery(id+"F0.wireOp",EDGE,"E28.MirrorCS"),sQuery(id+"F0.wireOp",EDGE,"E29.MirrorCS"),sQuery(id+"F0.wireOp",EDGE,"E30.MirrorCS"),sQuery(id+"F0.wireOp",EDGE,"E31.MirrorCS")])],"isStart":false})],"blendedInto":[makeQuery(id+"F1.opExtrude","CAP_FACE",FACE,{"disambiguationData":[OSD([subQ0,sQuery(id+"F0.wireOp",EDGE,"E1.0"),sQuery(id+"F0.wireOp",EDGE,"E1.1"),sQuery(id+"F0.wireOp",EDGE,"E1.2"),sQuery(id+"F0.wireOp",EDGE,"E1.3"),sQuery(id+"F0.wireOp",EDGE,"E1.4"),sQuery(id+"F0.wireOp",EDGE,"E1.5"),sQuery(id+"F0.wireOp",EDGE,"E1.6"),sQuery(id+"F0.wireOp",EDGE,"E1.7"),sQuery(id+"F0.wireOp",EDGE,"E1.8"),sQuery(id+"F0.wireOp",EDGE,"E1.9"),sQuery(id+"F0.wireOp",EDGE,"E1.10"),sQuery(id+"F0.wireOp",EDGE,"E2"),sQuery(id+"F0.wireOp",EDGE,"E3.2.0"),sQuery(id+"F0.wireOp",EDGE,"E3.3.0"),sQuery(id+"F0.wireOp",EDGE,"E3.4.0"),sQuery(id+"F0.wireOp",EDGE,"E3.5.0"),sQuery(id+"F0.wireOp",EDGE,"E3.6.0"),sQuery(id+"F0.wireOp",EDGE,"E3.7.0"),sQuery(id+"F0.wireOp",EDGE,"E3.8.0"),sQuery(id+"F0.wireOp",EDGE,"E3.9.0"),sQuery(id+"F0.wireOp",EDGE,"E3.10.0"),sQuery(id+"F0.wireOp",EDGE,"E4"),sQuery(id+"F0.wireOp",EDGE,"E5"),sQuery(id+"F0.wireOp",EDGE,"E6"),sQuery(id+"F0.wireOp",EDGE,"E7"),sQuery(id+"F0.wireOp",EDGE,"E8"),sQuery(id+"F0.wireOp",EDGE,"E9"),sQuery(id+"F0.wireOp",EDGE,"E10"),sQuery(id+"F0.wireOp",EDGE,"E11"),sQuery(id+"F0.wireOp",EDGE,"E12"),sQuery(id+"F0.wireOp",EDGE,"E13"),sQuery(id+"F0.wireOp",EDGE,"E14"),sQuery(id+"F0.wireOp",EDGE,"E15"),sQuery(id+"F0.wireOp",EDGE,"E16"),sQuery(id+"F0.wireOp",EDGE,"E17"),sQuery(id+"F0.wireOp",EDGE,"E18.MirrorCS"),sQuery(id+"F0.wireOp",EDGE,"E19.MirrorCS"),sQuery(id+"F0.wireOp",EDGE,"E20.MirrorCS"),sQuery(id+"F0.wireOp",EDGE,"E21.MirrorCS"),sQuery(id+"F0.wireOp",EDGE,"E22.MirrorCS"),sQuery(id+"F0.wireOp",EDGE,"E23.MirrorCS"),sQuery(id+"F0.wireOp",EDGE,"E24.MirrorCS"),sQuery(id+"F0.wireOp",EDGE,"E25.MirrorCS"),sQuery(id+"F0.wireOp",EDGE,"E26.MirrorCS"),sQuery(id+"F0.wireOp",EDGE,"E27.MirrorCS"),sQuery(id+"F0.wireOp",EDGE,"E28.MirrorCS"),sQuery(id+"F0.wireOp",EDGE,"E29.MirrorCS"),sQuery(id+"F0.wireOp",EDGE,"E30.MirrorCS"),sQuery(id+"F0.wireOp",EDGE,"E31.MirrorCS")])],"isStart":false})]}),makeQuery(id+"F6.opExtrude","CAP_EDGE",EDGE,{"disambiguationData":[OSD([sQuery(id+"F5.wireOp",EDGE,"E35.0")])],"isStart":true})]});}
            var Q53;
            Q53=makeQuery(id+"F6.boolean.opBoolean","COPY",EDGE,{"derivedFrom":makeQuery(id+"F6.opExtrude","CAP_EDGE",EDGE,{"disambiguationData":[OSD([sQuery(id+"F5.wireOp",EDGE,"E35.0")])],"isStart":false})});
            var Q54;
            {var subQ0=sQuery(id+"F0.wireOp",EDGE,"E26.MirrorCS");Q54=makeQuery(id+"F6.boolean.opBoolean","MERGE",EDGE,{"derivedFrom":[makeQuery(id+"F2.opFillet","BLEND_EDGE",EDGE,{"blendedFrom":[makeQuery(id+"F1.opExtrude","CAP_EDGE",EDGE,{"disambiguationData":[OSD([subQ0])],"isStart":false}),makeQuery(id+"F1.opExtrude","CAP_FACE",FACE,{"disambiguationData":[OSD([sQuery(id+"F0.wireOp",EDGE,"E0"),sQuery(id+"F0.wireOp",EDGE,"E1.0"),sQuery(id+"F0.wireOp",EDGE,"E1.1"),sQuery(id+"F0.wireOp",EDGE,"E1.2"),sQuery(id+"F0.wireOp",EDGE,"E1.3"),sQuery(id+"F0.wireOp",EDGE,"E1.4"),sQuery(id+"F0.wireOp",EDGE,"E1.5"),sQuery(id+"F0.wireOp",EDGE,"E1.6"),sQuery(id+"F0.wireOp",EDGE,"E1.7"),sQuery(id+"F0.wireOp",EDGE,"E1.8"),sQuery(id+"F0.wireOp",EDGE,"E1.9"),sQuery(id+"F0.wireOp",EDGE,"E1.10"),sQuery(id+"F0.wireOp",EDGE,"E2"),sQuery(id+"F0.wireOp",EDGE,"E3.2.0"),sQuery(id+"F0.wireOp",EDGE,"E3.3.0"),sQuery(id+"F0.wireOp",EDGE,"E3.4.0"),sQuery(id+"F0.wireOp",EDGE,"E3.5.0"),sQuery(id+"F0.wireOp",EDGE,"E3.6.0"),sQuery(id+"F0.wireOp",EDGE,"E3.7.0"),sQuery(id+"F0.wireOp",EDGE,"E3.8.0"),sQuery(id+"F0.wireOp",EDGE,"E3.9.0"),sQuery(id+"F0.wireOp",EDGE,"E3.10.0"),sQuery(id+"F0.wireOp",EDGE,"E4"),sQuery(id+"F0.wireOp",EDGE,"E5"),sQuery(id+"F0.wireOp",EDGE,"E6"),sQuery(id+"F0.wireOp",EDGE,"E7"),sQuery(id+"F0.wireOp",EDGE,"E8"),sQuery(id+"F0.wireOp",EDGE,"E9"),sQuery(id+"F0.wireOp",EDGE,"E10"),sQuery(id+"F0.wireOp",EDGE,"E11"),sQuery(id+"F0.wireOp",EDGE,"E12"),sQuery(id+"F0.wireOp",EDGE,"E13"),sQuery(id+"F0.wireOp",EDGE,"E14"),sQuery(id+"F0.wireOp",EDGE,"E15"),sQuery(id+"F0.wireOp",EDGE,"E16"),sQuery(id+"F0.wireOp",EDGE,"E17"),sQuery(id+"F0.wireOp",EDGE,"E18.MirrorCS"),sQuery(id+"F0.wireOp",EDGE,"E19.MirrorCS"),sQuery(id+"F0.wireOp",EDGE,"E20.MirrorCS"),sQuery(id+"F0.wireOp",EDGE,"E21.MirrorCS"),sQuery(id+"F0.wireOp",EDGE,"E22.MirrorCS"),sQuery(id+"F0.wireOp",EDGE,"E23.MirrorCS"),sQuery(id+"F0.wireOp",EDGE,"E24.MirrorCS"),sQuery(id+"F0.wireOp",EDGE,"E25.MirrorCS"),subQ0,sQuery(id+"F0.wireOp",EDGE,"E27.MirrorCS"),sQuery(id+"F0.wireOp",EDGE,"E28.MirrorCS"),sQuery(id+"F0.wireOp",EDGE,"E29.MirrorCS"),sQuery(id+"F0.wireOp",EDGE,"E30.MirrorCS"),sQuery(id+"F0.wireOp",EDGE,"E31.MirrorCS")])],"isStart":false})],"blendedInto":[makeQuery(id+"F1.opExtrude","CAP_FACE",FACE,{"disambiguationData":[OSD([sQuery(id+"F0.wireOp",EDGE,"E0"),sQuery(id+"F0.wireOp",EDGE,"E1.0"),sQuery(id+"F0.wireOp",EDGE,"E1.1"),sQuery(id+"F0.wireOp",EDGE,"E1.2"),sQuery(id+"F0.wireOp",EDGE,"E1.3"),sQuery(id+"F0.wireOp",EDGE,"E1.4"),sQuery(id+"F0.wireOp",EDGE,"E1.5"),sQuery(id+"F0.wireOp",EDGE,"E1.6"),sQuery(id+"F0.wireOp",EDGE,"E1.7"),sQuery(id+"F0.wireOp",EDGE,"E1.8"),sQuery(id+"F0.wireOp",EDGE,"E1.9"),sQuery(id+"F0.wireOp",EDGE,"E1.10"),sQuery(id+"F0.wireOp",EDGE,"E2"),sQuery(id+"F0.wireOp",EDGE,"E3.2.0"),sQuery(id+"F0.wireOp",EDGE,"E3.3.0"),sQuery(id+"F0.wireOp",EDGE,"E3.4.0"),sQuery(id+"F0.wireOp",EDGE,"E3.5.0"),sQuery(id+"F0.wireOp",EDGE,"E3.6.0"),sQuery(id+"F0.wireOp",EDGE,"E3.7.0"),sQuery(id+"F0.wireOp",EDGE,"E3.8.0"),sQuery(id+"F0.wireOp",EDGE,"E3.9.0"),sQuery(id+"F0.wireOp",EDGE,"E3.10.0"),sQuery(id+"F0.wireOp",EDGE,"E4"),sQuery(id+"F0.wireOp",EDGE,"E5"),sQuery(id+"F0.wireOp",EDGE,"E6"),sQuery(id+"F0.wireOp",EDGE,"E7"),sQuery(id+"F0.wireOp",EDGE,"E8"),sQuery(id+"F0.wireOp",EDGE,"E9"),sQuery(id+"F0.wireOp",EDGE,"E10"),sQuery(id+"F0.wireOp",EDGE,"E11"),sQuery(id+"F0.wireOp",EDGE,"E12"),sQuery(id+"F0.wireOp",EDGE,"E13"),sQuery(id+"F0.wireOp",EDGE,"E14"),sQuery(id+"F0.wireOp",EDGE,"E15"),sQuery(id+"F0.wireOp",EDGE,"E16"),sQuery(id+"F0.wireOp",EDGE,"E17"),sQuery(id+"F0.wireOp",EDGE,"E18.MirrorCS"),sQuery(id+"F0.wireOp",EDGE,"E19.MirrorCS"),sQuery(id+"F0.wireOp",EDGE,"E20.MirrorCS"),sQuery(id+"F0.wireOp",EDGE,"E21.MirrorCS"),sQuery(id+"F0.wireOp",EDGE,"E22.MirrorCS"),sQuery(id+"F0.wireOp",EDGE,"E23.MirrorCS"),sQuery(id+"F0.wireOp",EDGE,"E24.MirrorCS"),sQuery(id+"F0.wireOp",EDGE,"E25.MirrorCS"),subQ0,sQuery(id+"F0.wireOp",EDGE,"E27.MirrorCS"),sQuery(id+"F0.wireOp",EDGE,"E28.MirrorCS"),sQuery(id+"F0.wireOp",EDGE,"E29.MirrorCS"),sQuery(id+"F0.wireOp",EDGE,"E30.MirrorCS"),sQuery(id+"F0.wireOp",EDGE,"E31.MirrorCS")])],"isStart":false})]}),makeQuery(id+"F6.opExtrude","CAP_EDGE",EDGE,{"disambiguationData":[OSD([sQuery(id+"F5.wireOp",EDGE,"E66.0")])],"isStart":true})]});}
            var Q55;
            Q55=makeQuery(id+"F6.boolean.opBoolean","COPY",EDGE,{"derivedFrom":makeQuery(id+"F6.opExtrude","CAP_EDGE",EDGE,{"disambiguationData":[OSD([sQuery(id+"F5.wireOp",EDGE,"E66.0")])],"isStart":false})});
            var Q56;
            {var subQ0=sQuery(id+"F0.wireOp",EDGE,"E27.MirrorCS");Q56=makeQuery(id+"F6.boolean.opBoolean","MERGE",EDGE,{"derivedFrom":[makeQuery(id+"F2.opFillet","BLEND_EDGE",EDGE,{"blendedFrom":[makeQuery(id+"F1.opExtrude","CAP_EDGE",EDGE,{"disambiguationData":[OSD([subQ0])],"isStart":false}),makeQuery(id+"F1.opExtrude","CAP_FACE",FACE,{"disambiguationData":[OSD([sQuery(id+"F0.wireOp",EDGE,"E0"),sQuery(id+"F0.wireOp",EDGE,"E1.0"),sQuery(id+"F0.wireOp",EDGE,"E1.1"),sQuery(id+"F0.wireOp",EDGE,"E1.2"),sQuery(id+"F0.wireOp",EDGE,"E1.3"),sQuery(id+"F0.wireOp",EDGE,"E1.4"),sQuery(id+"F0.wireOp",EDGE,"E1.5"),sQuery(id+"F0.wireOp",EDGE,"E1.6"),sQuery(id+"F0.wireOp",EDGE,"E1.7"),sQuery(id+"F0.wireOp",EDGE,"E1.8"),sQuery(id+"F0.wireOp",EDGE,"E1.9"),sQuery(id+"F0.wireOp",EDGE,"E1.10"),sQuery(id+"F0.wireOp",EDGE,"E2"),sQuery(id+"F0.wireOp",EDGE,"E3.2.0"),sQuery(id+"F0.wireOp",EDGE,"E3.3.0"),sQuery(id+"F0.wireOp",EDGE,"E3.4.0"),sQuery(id+"F0.wireOp",EDGE,"E3.5.0"),sQuery(id+"F0.wireOp",EDGE,"E3.6.0"),sQuery(id+"F0.wireOp",EDGE,"E3.7.0"),sQuery(id+"F0.wireOp",EDGE,"E3.8.0"),sQuery(id+"F0.wireOp",EDGE,"E3.9.0"),sQuery(id+"F0.wireOp",EDGE,"E3.10.0"),sQuery(id+"F0.wireOp",EDGE,"E4"),sQuery(id+"F0.wireOp",EDGE,"E5"),sQuery(id+"F0.wireOp",EDGE,"E6"),sQuery(id+"F0.wireOp",EDGE,"E7"),sQuery(id+"F0.wireOp",EDGE,"E8"),sQuery(id+"F0.wireOp",EDGE,"E9"),sQuery(id+"F0.wireOp",EDGE,"E10"),sQuery(id+"F0.wireOp",EDGE,"E11"),sQuery(id+"F0.wireOp",EDGE,"E12"),sQuery(id+"F0.wireOp",EDGE,"E13"),sQuery(id+"F0.wireOp",EDGE,"E14"),sQuery(id+"F0.wireOp",EDGE,"E15"),sQuery(id+"F0.wireOp",EDGE,"E16"),sQuery(id+"F0.wireOp",EDGE,"E17"),sQuery(id+"F0.wireOp",EDGE,"E18.MirrorCS"),sQuery(id+"F0.wireOp",EDGE,"E19.MirrorCS"),sQuery(id+"F0.wireOp",EDGE,"E20.MirrorCS"),sQuery(id+"F0.wireOp",EDGE,"E21.MirrorCS"),sQuery(id+"F0.wireOp",EDGE,"E22.MirrorCS"),sQuery(id+"F0.wireOp",EDGE,"E23.MirrorCS"),sQuery(id+"F0.wireOp",EDGE,"E24.MirrorCS"),sQuery(id+"F0.wireOp",EDGE,"E25.MirrorCS"),sQuery(id+"F0.wireOp",EDGE,"E26.MirrorCS"),subQ0,sQuery(id+"F0.wireOp",EDGE,"E28.MirrorCS"),sQuery(id+"F0.wireOp",EDGE,"E29.MirrorCS"),sQuery(id+"F0.wireOp",EDGE,"E30.MirrorCS"),sQuery(id+"F0.wireOp",EDGE,"E31.MirrorCS")])],"isStart":false})],"blendedInto":[makeQuery(id+"F1.opExtrude","CAP_FACE",FACE,{"disambiguationData":[OSD([sQuery(id+"F0.wireOp",EDGE,"E0"),sQuery(id+"F0.wireOp",EDGE,"E1.0"),sQuery(id+"F0.wireOp",EDGE,"E1.1"),sQuery(id+"F0.wireOp",EDGE,"E1.2"),sQuery(id+"F0.wireOp",EDGE,"E1.3"),sQuery(id+"F0.wireOp",EDGE,"E1.4"),sQuery(id+"F0.wireOp",EDGE,"E1.5"),sQuery(id+"F0.wireOp",EDGE,"E1.6"),sQuery(id+"F0.wireOp",EDGE,"E1.7"),sQuery(id+"F0.wireOp",EDGE,"E1.8"),sQuery(id+"F0.wireOp",EDGE,"E1.9"),sQuery(id+"F0.wireOp",EDGE,"E1.10"),sQuery(id+"F0.wireOp",EDGE,"E2"),sQuery(id+"F0.wireOp",EDGE,"E3.2.0"),sQuery(id+"F0.wireOp",EDGE,"E3.3.0"),sQuery(id+"F0.wireOp",EDGE,"E3.4.0"),sQuery(id+"F0.wireOp",EDGE,"E3.5.0"),sQuery(id+"F0.wireOp",EDGE,"E3.6.0"),sQuery(id+"F0.wireOp",EDGE,"E3.7.0"),sQuery(id+"F0.wireOp",EDGE,"E3.8.0"),sQuery(id+"F0.wireOp",EDGE,"E3.9.0"),sQuery(id+"F0.wireOp",EDGE,"E3.10.0"),sQuery(id+"F0.wireOp",EDGE,"E4"),sQuery(id+"F0.wireOp",EDGE,"E5"),sQuery(id+"F0.wireOp",EDGE,"E6"),sQuery(id+"F0.wireOp",EDGE,"E7"),sQuery(id+"F0.wireOp",EDGE,"E8"),sQuery(id+"F0.wireOp",EDGE,"E9"),sQuery(id+"F0.wireOp",EDGE,"E10"),sQuery(id+"F0.wireOp",EDGE,"E11"),sQuery(id+"F0.wireOp",EDGE,"E12"),sQuery(id+"F0.wireOp",EDGE,"E13"),sQuery(id+"F0.wireOp",EDGE,"E14"),sQuery(id+"F0.wireOp",EDGE,"E15"),sQuery(id+"F0.wireOp",EDGE,"E16"),sQuery(id+"F0.wireOp",EDGE,"E17"),sQuery(id+"F0.wireOp",EDGE,"E18.MirrorCS"),sQuery(id+"F0.wireOp",EDGE,"E19.MirrorCS"),sQuery(id+"F0.wireOp",EDGE,"E20.MirrorCS"),sQuery(id+"F0.wireOp",EDGE,"E21.MirrorCS"),sQuery(id+"F0.wireOp",EDGE,"E22.MirrorCS"),sQuery(id+"F0.wireOp",EDGE,"E23.MirrorCS"),sQuery(id+"F0.wireOp",EDGE,"E24.MirrorCS"),sQuery(id+"F0.wireOp",EDGE,"E25.MirrorCS"),sQuery(id+"F0.wireOp",EDGE,"E26.MirrorCS"),subQ0,sQuery(id+"F0.wireOp",EDGE,"E28.MirrorCS"),sQuery(id+"F0.wireOp",EDGE,"E29.MirrorCS"),sQuery(id+"F0.wireOp",EDGE,"E30.MirrorCS"),sQuery(id+"F0.wireOp",EDGE,"E31.MirrorCS")])],"isStart":false})]}),makeQuery(id+"F6.opExtrude","CAP_EDGE",EDGE,{"disambiguationData":[OSD([sQuery(id+"F5.wireOp",EDGE,"E67.0")])],"isStart":true})]});}
            var Q57;
            Q57=makeQuery(id+"F6.boolean.opBoolean","COPY",FACE,{"derivedFrom":makeQuery(id+"F6.opExtrude","CAP_FACE",FACE,{"disambiguationData":[OSD([sQuery(id+"F5.wireOp",EDGE,"E35.0"),sQuery(id+"F5.wireOp",EDGE,"E36.0"),sQuery(id+"F5.wireOp",EDGE,"E37.0"),sQuery(id+"F5.wireOp",EDGE,"E38.0"),sQuery(id+"F5.wireOp",EDGE,"E39.0"),sQuery(id+"F5.wireOp",EDGE,"E40.0"),sQuery(id+"F5.wireOp",EDGE,"E41.0"),sQuery(id+"F5.wireOp",EDGE,"E42.0"),sQuery(id+"F5.wireOp",EDGE,"E43.0"),sQuery(id+"F5.wireOp",EDGE,"E44.0"),sQuery(id+"F5.wireOp",EDGE,"E45.0"),sQuery(id+"F5.wireOp",EDGE,"E46.0"),sQuery(id+"F5.wireOp",EDGE,"E47.0"),sQuery(id+"F5.wireOp",EDGE,"E48.0"),sQuery(id+"F5.wireOp",EDGE,"E49.0"),sQuery(id+"F5.wireOp",EDGE,"E50.0"),sQuery(id+"F5.wireOp",EDGE,"E51.0"),sQuery(id+"F5.wireOp",EDGE,"E52.0"),sQuery(id+"F5.wireOp",EDGE,"E53.0"),sQuery(id+"F5.wireOp",EDGE,"E54.0"),sQuery(id+"F5.wireOp",EDGE,"E55.0"),sQuery(id+"F5.wireOp",EDGE,"E56.0"),sQuery(id+"F5.wireOp",EDGE,"E57.0"),sQuery(id+"F5.wireOp",EDGE,"E58.0"),sQuery(id+"F5.wireOp",EDGE,"E59.0"),sQuery(id+"F5.wireOp",EDGE,"E60.0"),sQuery(id+"F5.wireOp",EDGE,"E61.0"),sQuery(id+"F5.wireOp",EDGE,"E62.0"),sQuery(id+"F5.wireOp",EDGE,"E63.0"),sQuery(id+"F5.wireOp",EDGE,"E64.0"),sQuery(id+"F5.wireOp",EDGE,"E65.0"),sQuery(id+"F5.wireOp",EDGE,"E66.0"),sQuery(id+"F5.wireOp",EDGE,"E67.0"),sQuery(id+"F5.wireOp",EDGE,"E68.0"),sQuery(id+"F5.wireOp",EDGE,"E69.0"),sQuery(id+"F5.wireOp",EDGE,"E70.0"),sQuery(id+"F5.wireOp",EDGE,"E71.0"),sQuery(id+"F5.wireOp",EDGE,"E73.0"),sQuery(id+"F5.wireOp",EDGE,"E74.0"),sQuery(id+"F5.wireOp",EDGE,"E76.0"),sQuery(id+"F5.wireOp",EDGE,"E77.0"),sQuery(id+"F5.wireOp",EDGE,"E78.0"),sQuery(id+"F5.wireOp",EDGE,"E72.0"),sQuery(id+"F5.wireOp",EDGE,"E83.0.0"),sQuery(id+"F5.wireOp",EDGE,"E84.0"),sQuery(id+"F5.wireOp",EDGE,"E82.0"),sQuery(id+"F5.wireOp",EDGE,"E81.0"),sQuery(id+"F5.wireOp",EDGE,"E80.0"),sQuery(id+"F5.wireOp",EDGE,"E79.0")])],"isStart":false})});
            var Q58;
            {var subQ0=sQuery(id+"F0.wireOp",EDGE,"E29.MirrorCS");Q58=makeQuery(id+"F6.boolean.opBoolean","MERGE",EDGE,{"derivedFrom":[makeQuery(id+"F2.opFillet","BLEND_EDGE",EDGE,{"blendedFrom":[makeQuery(id+"F1.opExtrude","CAP_EDGE",EDGE,{"disambiguationData":[OSD([subQ0])],"isStart":false}),makeQuery(id+"F1.opExtrude","CAP_FACE",FACE,{"disambiguationData":[OSD([sQuery(id+"F0.wireOp",EDGE,"E0"),sQuery(id+"F0.wireOp",EDGE,"E1.0"),sQuery(id+"F0.wireOp",EDGE,"E1.1"),sQuery(id+"F0.wireOp",EDGE,"E1.2"),sQuery(id+"F0.wireOp",EDGE,"E1.3"),sQuery(id+"F0.wireOp",EDGE,"E1.4"),sQuery(id+"F0.wireOp",EDGE,"E1.5"),sQuery(id+"F0.wireOp",EDGE,"E1.6"),sQuery(id+"F0.wireOp",EDGE,"E1.7"),sQuery(id+"F0.wireOp",EDGE,"E1.8"),sQuery(id+"F0.wireOp",EDGE,"E1.9"),sQuery(id+"F0.wireOp",EDGE,"E1.10"),sQuery(id+"F0.wireOp",EDGE,"E2"),sQuery(id+"F0.wireOp",EDGE,"E3.2.0"),sQuery(id+"F0.wireOp",EDGE,"E3.3.0"),sQuery(id+"F0.wireOp",EDGE,"E3.4.0"),sQuery(id+"F0.wireOp",EDGE,"E3.5.0"),sQuery(id+"F0.wireOp",EDGE,"E3.6.0"),sQuery(id+"F0.wireOp",EDGE,"E3.7.0"),sQuery(id+"F0.wireOp",EDGE,"E3.8.0"),sQuery(id+"F0.wireOp",EDGE,"E3.9.0"),sQuery(id+"F0.wireOp",EDGE,"E3.10.0"),sQuery(id+"F0.wireOp",EDGE,"E4"),sQuery(id+"F0.wireOp",EDGE,"E5"),sQuery(id+"F0.wireOp",EDGE,"E6"),sQuery(id+"F0.wireOp",EDGE,"E7"),sQuery(id+"F0.wireOp",EDGE,"E8"),sQuery(id+"F0.wireOp",EDGE,"E9"),sQuery(id+"F0.wireOp",EDGE,"E10"),sQuery(id+"F0.wireOp",EDGE,"E11"),sQuery(id+"F0.wireOp",EDGE,"E12"),sQuery(id+"F0.wireOp",EDGE,"E13"),sQuery(id+"F0.wireOp",EDGE,"E14"),sQuery(id+"F0.wireOp",EDGE,"E15"),sQuery(id+"F0.wireOp",EDGE,"E16"),sQuery(id+"F0.wireOp",EDGE,"E17"),sQuery(id+"F0.wireOp",EDGE,"E18.MirrorCS"),sQuery(id+"F0.wireOp",EDGE,"E19.MirrorCS"),sQuery(id+"F0.wireOp",EDGE,"E20.MirrorCS"),sQuery(id+"F0.wireOp",EDGE,"E21.MirrorCS"),sQuery(id+"F0.wireOp",EDGE,"E22.MirrorCS"),sQuery(id+"F0.wireOp",EDGE,"E23.MirrorCS"),sQuery(id+"F0.wireOp",EDGE,"E24.MirrorCS"),sQuery(id+"F0.wireOp",EDGE,"E25.MirrorCS"),sQuery(id+"F0.wireOp",EDGE,"E26.MirrorCS"),sQuery(id+"F0.wireOp",EDGE,"E27.MirrorCS"),sQuery(id+"F0.wireOp",EDGE,"E28.MirrorCS"),subQ0,sQuery(id+"F0.wireOp",EDGE,"E30.MirrorCS"),sQuery(id+"F0.wireOp",EDGE,"E31.MirrorCS")])],"isStart":false})],"blendedInto":[makeQuery(id+"F1.opExtrude","CAP_FACE",FACE,{"disambiguationData":[OSD([sQuery(id+"F0.wireOp",EDGE,"E0"),sQuery(id+"F0.wireOp",EDGE,"E1.0"),sQuery(id+"F0.wireOp",EDGE,"E1.1"),sQuery(id+"F0.wireOp",EDGE,"E1.2"),sQuery(id+"F0.wireOp",EDGE,"E1.3"),sQuery(id+"F0.wireOp",EDGE,"E1.4"),sQuery(id+"F0.wireOp",EDGE,"E1.5"),sQuery(id+"F0.wireOp",EDGE,"E1.6"),sQuery(id+"F0.wireOp",EDGE,"E1.7"),sQuery(id+"F0.wireOp",EDGE,"E1.8"),sQuery(id+"F0.wireOp",EDGE,"E1.9"),sQuery(id+"F0.wireOp",EDGE,"E1.10"),sQuery(id+"F0.wireOp",EDGE,"E2"),sQuery(id+"F0.wireOp",EDGE,"E3.2.0"),sQuery(id+"F0.wireOp",EDGE,"E3.3.0"),sQuery(id+"F0.wireOp",EDGE,"E3.4.0"),sQuery(id+"F0.wireOp",EDGE,"E3.5.0"),sQuery(id+"F0.wireOp",EDGE,"E3.6.0"),sQuery(id+"F0.wireOp",EDGE,"E3.7.0"),sQuery(id+"F0.wireOp",EDGE,"E3.8.0"),sQuery(id+"F0.wireOp",EDGE,"E3.9.0"),sQuery(id+"F0.wireOp",EDGE,"E3.10.0"),sQuery(id+"F0.wireOp",EDGE,"E4"),sQuery(id+"F0.wireOp",EDGE,"E5"),sQuery(id+"F0.wireOp",EDGE,"E6"),sQuery(id+"F0.wireOp",EDGE,"E7"),sQuery(id+"F0.wireOp",EDGE,"E8"),sQuery(id+"F0.wireOp",EDGE,"E9"),sQuery(id+"F0.wireOp",EDGE,"E10"),sQuery(id+"F0.wireOp",EDGE,"E11"),sQuery(id+"F0.wireOp",EDGE,"E12"),sQuery(id+"F0.wireOp",EDGE,"E13"),sQuery(id+"F0.wireOp",EDGE,"E14"),sQuery(id+"F0.wireOp",EDGE,"E15"),sQuery(id+"F0.wireOp",EDGE,"E16"),sQuery(id+"F0.wireOp",EDGE,"E17"),sQuery(id+"F0.wireOp",EDGE,"E18.MirrorCS"),sQuery(id+"F0.wireOp",EDGE,"E19.MirrorCS"),sQuery(id+"F0.wireOp",EDGE,"E20.MirrorCS"),sQuery(id+"F0.wireOp",EDGE,"E21.MirrorCS"),sQuery(id+"F0.wireOp",EDGE,"E22.MirrorCS"),sQuery(id+"F0.wireOp",EDGE,"E23.MirrorCS"),sQuery(id+"F0.wireOp",EDGE,"E24.MirrorCS"),sQuery(id+"F0.wireOp",EDGE,"E25.MirrorCS"),sQuery(id+"F0.wireOp",EDGE,"E26.MirrorCS"),sQuery(id+"F0.wireOp",EDGE,"E27.MirrorCS"),sQuery(id+"F0.wireOp",EDGE,"E28.MirrorCS"),subQ0,sQuery(id+"F0.wireOp",EDGE,"E30.MirrorCS"),sQuery(id+"F0.wireOp",EDGE,"E31.MirrorCS")])],"isStart":false})]}),makeQuery(id+"F6.opExtrude","CAP_EDGE",EDGE,{"disambiguationData":[OSD([sQuery(id+"F5.wireOp",EDGE,"E68.0")])],"isStart":true})]});}
            var Q59;
            {var subQ0=sQuery(id+"F0.wireOp",EDGE,"E25.MirrorCS");Q59=makeQuery(id+"F6.boolean.opBoolean","MERGE",EDGE,{"derivedFrom":[makeQuery(id+"F2.opFillet","BLEND_EDGE",EDGE,{"blendedFrom":[makeQuery(id+"F1.opExtrude","CAP_EDGE",EDGE,{"disambiguationData":[OSD([subQ0])],"isStart":false}),makeQuery(id+"F1.opExtrude","CAP_FACE",FACE,{"disambiguationData":[OSD([sQuery(id+"F0.wireOp",EDGE,"E0"),sQuery(id+"F0.wireOp",EDGE,"E1.0"),sQuery(id+"F0.wireOp",EDGE,"E1.1"),sQuery(id+"F0.wireOp",EDGE,"E1.2"),sQuery(id+"F0.wireOp",EDGE,"E1.3"),sQuery(id+"F0.wireOp",EDGE,"E1.4"),sQuery(id+"F0.wireOp",EDGE,"E1.5"),sQuery(id+"F0.wireOp",EDGE,"E1.6"),sQuery(id+"F0.wireOp",EDGE,"E1.7"),sQuery(id+"F0.wireOp",EDGE,"E1.8"),sQuery(id+"F0.wireOp",EDGE,"E1.9"),sQuery(id+"F0.wireOp",EDGE,"E1.10"),sQuery(id+"F0.wireOp",EDGE,"E2"),sQuery(id+"F0.wireOp",EDGE,"E3.2.0"),sQuery(id+"F0.wireOp",EDGE,"E3.3.0"),sQuery(id+"F0.wireOp",EDGE,"E3.4.0"),sQuery(id+"F0.wireOp",EDGE,"E3.5.0"),sQuery(id+"F0.wireOp",EDGE,"E3.6.0"),sQuery(id+"F0.wireOp",EDGE,"E3.7.0"),sQuery(id+"F0.wireOp",EDGE,"E3.8.0"),sQuery(id+"F0.wireOp",EDGE,"E3.9.0"),sQuery(id+"F0.wireOp",EDGE,"E3.10.0"),sQuery(id+"F0.wireOp",EDGE,"E4"),sQuery(id+"F0.wireOp",EDGE,"E5"),sQuery(id+"F0.wireOp",EDGE,"E6"),sQuery(id+"F0.wireOp",EDGE,"E7"),sQuery(id+"F0.wireOp",EDGE,"E8"),sQuery(id+"F0.wireOp",EDGE,"E9"),sQuery(id+"F0.wireOp",EDGE,"E10"),sQuery(id+"F0.wireOp",EDGE,"E11"),sQuery(id+"F0.wireOp",EDGE,"E12"),sQuery(id+"F0.wireOp",EDGE,"E13"),sQuery(id+"F0.wireOp",EDGE,"E14"),sQuery(id+"F0.wireOp",EDGE,"E15"),sQuery(id+"F0.wireOp",EDGE,"E16"),sQuery(id+"F0.wireOp",EDGE,"E17"),sQuery(id+"F0.wireOp",EDGE,"E18.MirrorCS"),sQuery(id+"F0.wireOp",EDGE,"E19.MirrorCS"),sQuery(id+"F0.wireOp",EDGE,"E20.MirrorCS"),sQuery(id+"F0.wireOp",EDGE,"E21.MirrorCS"),sQuery(id+"F0.wireOp",EDGE,"E22.MirrorCS"),sQuery(id+"F0.wireOp",EDGE,"E23.MirrorCS"),sQuery(id+"F0.wireOp",EDGE,"E24.MirrorCS"),subQ0,sQuery(id+"F0.wireOp",EDGE,"E26.MirrorCS"),sQuery(id+"F0.wireOp",EDGE,"E27.MirrorCS"),sQuery(id+"F0.wireOp",EDGE,"E28.MirrorCS"),sQuery(id+"F0.wireOp",EDGE,"E29.MirrorCS"),sQuery(id+"F0.wireOp",EDGE,"E30.MirrorCS"),sQuery(id+"F0.wireOp",EDGE,"E31.MirrorCS")])],"isStart":false})],"blendedInto":[makeQuery(id+"F1.opExtrude","CAP_FACE",FACE,{"disambiguationData":[OSD([sQuery(id+"F0.wireOp",EDGE,"E0"),sQuery(id+"F0.wireOp",EDGE,"E1.0"),sQuery(id+"F0.wireOp",EDGE,"E1.1"),sQuery(id+"F0.wireOp",EDGE,"E1.2"),sQuery(id+"F0.wireOp",EDGE,"E1.3"),sQuery(id+"F0.wireOp",EDGE,"E1.4"),sQuery(id+"F0.wireOp",EDGE,"E1.5"),sQuery(id+"F0.wireOp",EDGE,"E1.6"),sQuery(id+"F0.wireOp",EDGE,"E1.7"),sQuery(id+"F0.wireOp",EDGE,"E1.8"),sQuery(id+"F0.wireOp",EDGE,"E1.9"),sQuery(id+"F0.wireOp",EDGE,"E1.10"),sQuery(id+"F0.wireOp",EDGE,"E2"),sQuery(id+"F0.wireOp",EDGE,"E3.2.0"),sQuery(id+"F0.wireOp",EDGE,"E3.3.0"),sQuery(id+"F0.wireOp",EDGE,"E3.4.0"),sQuery(id+"F0.wireOp",EDGE,"E3.5.0"),sQuery(id+"F0.wireOp",EDGE,"E3.6.0"),sQuery(id+"F0.wireOp",EDGE,"E3.7.0"),sQuery(id+"F0.wireOp",EDGE,"E3.8.0"),sQuery(id+"F0.wireOp",EDGE,"E3.9.0"),sQuery(id+"F0.wireOp",EDGE,"E3.10.0"),sQuery(id+"F0.wireOp",EDGE,"E4"),sQuery(id+"F0.wireOp",EDGE,"E5"),sQuery(id+"F0.wireOp",EDGE,"E6"),sQuery(id+"F0.wireOp",EDGE,"E7"),sQuery(id+"F0.wireOp",EDGE,"E8"),sQuery(id+"F0.wireOp",EDGE,"E9"),sQuery(id+"F0.wireOp",EDGE,"E10"),sQuery(id+"F0.wireOp",EDGE,"E11"),sQuery(id+"F0.wireOp",EDGE,"E12"),sQuery(id+"F0.wireOp",EDGE,"E13"),sQuery(id+"F0.wireOp",EDGE,"E14"),sQuery(id+"F0.wireOp",EDGE,"E15"),sQuery(id+"F0.wireOp",EDGE,"E16"),sQuery(id+"F0.wireOp",EDGE,"E17"),sQuery(id+"F0.wireOp",EDGE,"E18.MirrorCS"),sQuery(id+"F0.wireOp",EDGE,"E19.MirrorCS"),sQuery(id+"F0.wireOp",EDGE,"E20.MirrorCS"),sQuery(id+"F0.wireOp",EDGE,"E21.MirrorCS"),sQuery(id+"F0.wireOp",EDGE,"E22.MirrorCS"),sQuery(id+"F0.wireOp",EDGE,"E23.MirrorCS"),sQuery(id+"F0.wireOp",EDGE,"E24.MirrorCS"),subQ0,sQuery(id+"F0.wireOp",EDGE,"E26.MirrorCS"),sQuery(id+"F0.wireOp",EDGE,"E27.MirrorCS"),sQuery(id+"F0.wireOp",EDGE,"E28.MirrorCS"),sQuery(id+"F0.wireOp",EDGE,"E29.MirrorCS"),sQuery(id+"F0.wireOp",EDGE,"E30.MirrorCS"),sQuery(id+"F0.wireOp",EDGE,"E31.MirrorCS")])],"isStart":false})]}),makeQuery(id+"F6.opExtrude","CAP_EDGE",EDGE,{"disambiguationData":[OSD([sQuery(id+"F5.wireOp",EDGE,"E69.0")])],"isStart":true})]});}
            var Q60;
            {var subQ0=sQuery(id+"F0.wireOp",EDGE,"E24.MirrorCS");Q60=makeQuery(id+"F6.boolean.opBoolean","MERGE",EDGE,{"derivedFrom":[makeQuery(id+"F2.opFillet","BLEND_EDGE",EDGE,{"blendedFrom":[makeQuery(id+"F1.opExtrude","CAP_EDGE",EDGE,{"disambiguationData":[OSD([subQ0])],"isStart":false}),makeQuery(id+"F1.opExtrude","CAP_FACE",FACE,{"disambiguationData":[OSD([sQuery(id+"F0.wireOp",EDGE,"E0"),sQuery(id+"F0.wireOp",EDGE,"E1.0"),sQuery(id+"F0.wireOp",EDGE,"E1.1"),sQuery(id+"F0.wireOp",EDGE,"E1.2"),sQuery(id+"F0.wireOp",EDGE,"E1.3"),sQuery(id+"F0.wireOp",EDGE,"E1.4"),sQuery(id+"F0.wireOp",EDGE,"E1.5"),sQuery(id+"F0.wireOp",EDGE,"E1.6"),sQuery(id+"F0.wireOp",EDGE,"E1.7"),sQuery(id+"F0.wireOp",EDGE,"E1.8"),sQuery(id+"F0.wireOp",EDGE,"E1.9"),sQuery(id+"F0.wireOp",EDGE,"E1.10"),sQuery(id+"F0.wireOp",EDGE,"E2"),sQuery(id+"F0.wireOp",EDGE,"E3.2.0"),sQuery(id+"F0.wireOp",EDGE,"E3.3.0"),sQuery(id+"F0.wireOp",EDGE,"E3.4.0"),sQuery(id+"F0.wireOp",EDGE,"E3.5.0"),sQuery(id+"F0.wireOp",EDGE,"E3.6.0"),sQuery(id+"F0.wireOp",EDGE,"E3.7.0"),sQuery(id+"F0.wireOp",EDGE,"E3.8.0"),sQuery(id+"F0.wireOp",EDGE,"E3.9.0"),sQuery(id+"F0.wireOp",EDGE,"E3.10.0"),sQuery(id+"F0.wireOp",EDGE,"E4"),sQuery(id+"F0.wireOp",EDGE,"E5"),sQuery(id+"F0.wireOp",EDGE,"E6"),sQuery(id+"F0.wireOp",EDGE,"E7"),sQuery(id+"F0.wireOp",EDGE,"E8"),sQuery(id+"F0.wireOp",EDGE,"E9"),sQuery(id+"F0.wireOp",EDGE,"E10"),sQuery(id+"F0.wireOp",EDGE,"E11"),sQuery(id+"F0.wireOp",EDGE,"E12"),sQuery(id+"F0.wireOp",EDGE,"E13"),sQuery(id+"F0.wireOp",EDGE,"E14"),sQuery(id+"F0.wireOp",EDGE,"E15"),sQuery(id+"F0.wireOp",EDGE,"E16"),sQuery(id+"F0.wireOp",EDGE,"E17"),sQuery(id+"F0.wireOp",EDGE,"E18.MirrorCS"),sQuery(id+"F0.wireOp",EDGE,"E19.MirrorCS"),sQuery(id+"F0.wireOp",EDGE,"E20.MirrorCS"),sQuery(id+"F0.wireOp",EDGE,"E21.MirrorCS"),sQuery(id+"F0.wireOp",EDGE,"E22.MirrorCS"),sQuery(id+"F0.wireOp",EDGE,"E23.MirrorCS"),subQ0,sQuery(id+"F0.wireOp",EDGE,"E25.MirrorCS"),sQuery(id+"F0.wireOp",EDGE,"E26.MirrorCS"),sQuery(id+"F0.wireOp",EDGE,"E27.MirrorCS"),sQuery(id+"F0.wireOp",EDGE,"E28.MirrorCS"),sQuery(id+"F0.wireOp",EDGE,"E29.MirrorCS"),sQuery(id+"F0.wireOp",EDGE,"E30.MirrorCS"),sQuery(id+"F0.wireOp",EDGE,"E31.MirrorCS")])],"isStart":false})],"blendedInto":[makeQuery(id+"F1.opExtrude","CAP_FACE",FACE,{"disambiguationData":[OSD([sQuery(id+"F0.wireOp",EDGE,"E0"),sQuery(id+"F0.wireOp",EDGE,"E1.0"),sQuery(id+"F0.wireOp",EDGE,"E1.1"),sQuery(id+"F0.wireOp",EDGE,"E1.2"),sQuery(id+"F0.wireOp",EDGE,"E1.3"),sQuery(id+"F0.wireOp",EDGE,"E1.4"),sQuery(id+"F0.wireOp",EDGE,"E1.5"),sQuery(id+"F0.wireOp",EDGE,"E1.6"),sQuery(id+"F0.wireOp",EDGE,"E1.7"),sQuery(id+"F0.wireOp",EDGE,"E1.8"),sQuery(id+"F0.wireOp",EDGE,"E1.9"),sQuery(id+"F0.wireOp",EDGE,"E1.10"),sQuery(id+"F0.wireOp",EDGE,"E2"),sQuery(id+"F0.wireOp",EDGE,"E3.2.0"),sQuery(id+"F0.wireOp",EDGE,"E3.3.0"),sQuery(id+"F0.wireOp",EDGE,"E3.4.0"),sQuery(id+"F0.wireOp",EDGE,"E3.5.0"),sQuery(id+"F0.wireOp",EDGE,"E3.6.0"),sQuery(id+"F0.wireOp",EDGE,"E3.7.0"),sQuery(id+"F0.wireOp",EDGE,"E3.8.0"),sQuery(id+"F0.wireOp",EDGE,"E3.9.0"),sQuery(id+"F0.wireOp",EDGE,"E3.10.0"),sQuery(id+"F0.wireOp",EDGE,"E4"),sQuery(id+"F0.wireOp",EDGE,"E5"),sQuery(id+"F0.wireOp",EDGE,"E6"),sQuery(id+"F0.wireOp",EDGE,"E7"),sQuery(id+"F0.wireOp",EDGE,"E8"),sQuery(id+"F0.wireOp",EDGE,"E9"),sQuery(id+"F0.wireOp",EDGE,"E10"),sQuery(id+"F0.wireOp",EDGE,"E11"),sQuery(id+"F0.wireOp",EDGE,"E12"),sQuery(id+"F0.wireOp",EDGE,"E13"),sQuery(id+"F0.wireOp",EDGE,"E14"),sQuery(id+"F0.wireOp",EDGE,"E15"),sQuery(id+"F0.wireOp",EDGE,"E16"),sQuery(id+"F0.wireOp",EDGE,"E17"),sQuery(id+"F0.wireOp",EDGE,"E18.MirrorCS"),sQuery(id+"F0.wireOp",EDGE,"E19.MirrorCS"),sQuery(id+"F0.wireOp",EDGE,"E20.MirrorCS"),sQuery(id+"F0.wireOp",EDGE,"E21.MirrorCS"),sQuery(id+"F0.wireOp",EDGE,"E22.MirrorCS"),sQuery(id+"F0.wireOp",EDGE,"E23.MirrorCS"),subQ0,sQuery(id+"F0.wireOp",EDGE,"E25.MirrorCS"),sQuery(id+"F0.wireOp",EDGE,"E26.MirrorCS"),sQuery(id+"F0.wireOp",EDGE,"E27.MirrorCS"),sQuery(id+"F0.wireOp",EDGE,"E28.MirrorCS"),sQuery(id+"F0.wireOp",EDGE,"E29.MirrorCS"),sQuery(id+"F0.wireOp",EDGE,"E30.MirrorCS"),sQuery(id+"F0.wireOp",EDGE,"E31.MirrorCS")])],"isStart":false})]}),makeQuery(id+"F6.opExtrude","CAP_EDGE",EDGE,{"disambiguationData":[OSD([sQuery(id+"F5.wireOp",EDGE,"E71.0")])],"isStart":true})]});}
            var Q61;
            {var subQ0=sQuery(id+"F0.wireOp",EDGE,"E23.MirrorCS");Q61=makeQuery(id+"F6.boolean.opBoolean","MERGE",EDGE,{"derivedFrom":[makeQuery(id+"F2.opFillet","BLEND_EDGE",EDGE,{"blendedFrom":[makeQuery(id+"F1.opExtrude","CAP_EDGE",EDGE,{"disambiguationData":[OSD([subQ0])],"isStart":false}),makeQuery(id+"F1.opExtrude","CAP_FACE",FACE,{"disambiguationData":[OSD([sQuery(id+"F0.wireOp",EDGE,"E0"),sQuery(id+"F0.wireOp",EDGE,"E1.0"),sQuery(id+"F0.wireOp",EDGE,"E1.1"),sQuery(id+"F0.wireOp",EDGE,"E1.2"),sQuery(id+"F0.wireOp",EDGE,"E1.3"),sQuery(id+"F0.wireOp",EDGE,"E1.4"),sQuery(id+"F0.wireOp",EDGE,"E1.5"),sQuery(id+"F0.wireOp",EDGE,"E1.6"),sQuery(id+"F0.wireOp",EDGE,"E1.7"),sQuery(id+"F0.wireOp",EDGE,"E1.8"),sQuery(id+"F0.wireOp",EDGE,"E1.9"),sQuery(id+"F0.wireOp",EDGE,"E1.10"),sQuery(id+"F0.wireOp",EDGE,"E2"),sQuery(id+"F0.wireOp",EDGE,"E3.2.0"),sQuery(id+"F0.wireOp",EDGE,"E3.3.0"),sQuery(id+"F0.wireOp",EDGE,"E3.4.0"),sQuery(id+"F0.wireOp",EDGE,"E3.5.0"),sQuery(id+"F0.wireOp",EDGE,"E3.6.0"),sQuery(id+"F0.wireOp",EDGE,"E3.7.0"),sQuery(id+"F0.wireOp",EDGE,"E3.8.0"),sQuery(id+"F0.wireOp",EDGE,"E3.9.0"),sQuery(id+"F0.wireOp",EDGE,"E3.10.0"),sQuery(id+"F0.wireOp",EDGE,"E4"),sQuery(id+"F0.wireOp",EDGE,"E5"),sQuery(id+"F0.wireOp",EDGE,"E6"),sQuery(id+"F0.wireOp",EDGE,"E7"),sQuery(id+"F0.wireOp",EDGE,"E8"),sQuery(id+"F0.wireOp",EDGE,"E9"),sQuery(id+"F0.wireOp",EDGE,"E10"),sQuery(id+"F0.wireOp",EDGE,"E11"),sQuery(id+"F0.wireOp",EDGE,"E12"),sQuery(id+"F0.wireOp",EDGE,"E13"),sQuery(id+"F0.wireOp",EDGE,"E14"),sQuery(id+"F0.wireOp",EDGE,"E15"),sQuery(id+"F0.wireOp",EDGE,"E16"),sQuery(id+"F0.wireOp",EDGE,"E17"),sQuery(id+"F0.wireOp",EDGE,"E18.MirrorCS"),sQuery(id+"F0.wireOp",EDGE,"E19.MirrorCS"),sQuery(id+"F0.wireOp",EDGE,"E20.MirrorCS"),sQuery(id+"F0.wireOp",EDGE,"E21.MirrorCS"),sQuery(id+"F0.wireOp",EDGE,"E22.MirrorCS"),subQ0,sQuery(id+"F0.wireOp",EDGE,"E24.MirrorCS"),sQuery(id+"F0.wireOp",EDGE,"E25.MirrorCS"),sQuery(id+"F0.wireOp",EDGE,"E26.MirrorCS"),sQuery(id+"F0.wireOp",EDGE,"E27.MirrorCS"),sQuery(id+"F0.wireOp",EDGE,"E28.MirrorCS"),sQuery(id+"F0.wireOp",EDGE,"E29.MirrorCS"),sQuery(id+"F0.wireOp",EDGE,"E30.MirrorCS"),sQuery(id+"F0.wireOp",EDGE,"E31.MirrorCS")])],"isStart":false})],"blendedInto":[makeQuery(id+"F1.opExtrude","CAP_FACE",FACE,{"disambiguationData":[OSD([sQuery(id+"F0.wireOp",EDGE,"E0"),sQuery(id+"F0.wireOp",EDGE,"E1.0"),sQuery(id+"F0.wireOp",EDGE,"E1.1"),sQuery(id+"F0.wireOp",EDGE,"E1.2"),sQuery(id+"F0.wireOp",EDGE,"E1.3"),sQuery(id+"F0.wireOp",EDGE,"E1.4"),sQuery(id+"F0.wireOp",EDGE,"E1.5"),sQuery(id+"F0.wireOp",EDGE,"E1.6"),sQuery(id+"F0.wireOp",EDGE,"E1.7"),sQuery(id+"F0.wireOp",EDGE,"E1.8"),sQuery(id+"F0.wireOp",EDGE,"E1.9"),sQuery(id+"F0.wireOp",EDGE,"E1.10"),sQuery(id+"F0.wireOp",EDGE,"E2"),sQuery(id+"F0.wireOp",EDGE,"E3.2.0"),sQuery(id+"F0.wireOp",EDGE,"E3.3.0"),sQuery(id+"F0.wireOp",EDGE,"E3.4.0"),sQuery(id+"F0.wireOp",EDGE,"E3.5.0"),sQuery(id+"F0.wireOp",EDGE,"E3.6.0"),sQuery(id+"F0.wireOp",EDGE,"E3.7.0"),sQuery(id+"F0.wireOp",EDGE,"E3.8.0"),sQuery(id+"F0.wireOp",EDGE,"E3.9.0"),sQuery(id+"F0.wireOp",EDGE,"E3.10.0"),sQuery(id+"F0.wireOp",EDGE,"E4"),sQuery(id+"F0.wireOp",EDGE,"E5"),sQuery(id+"F0.wireOp",EDGE,"E6"),sQuery(id+"F0.wireOp",EDGE,"E7"),sQuery(id+"F0.wireOp",EDGE,"E8"),sQuery(id+"F0.wireOp",EDGE,"E9"),sQuery(id+"F0.wireOp",EDGE,"E10"),sQuery(id+"F0.wireOp",EDGE,"E11"),sQuery(id+"F0.wireOp",EDGE,"E12"),sQuery(id+"F0.wireOp",EDGE,"E13"),sQuery(id+"F0.wireOp",EDGE,"E14"),sQuery(id+"F0.wireOp",EDGE,"E15"),sQuery(id+"F0.wireOp",EDGE,"E16"),sQuery(id+"F0.wireOp",EDGE,"E17"),sQuery(id+"F0.wireOp",EDGE,"E18.MirrorCS"),sQuery(id+"F0.wireOp",EDGE,"E19.MirrorCS"),sQuery(id+"F0.wireOp",EDGE,"E20.MirrorCS"),sQuery(id+"F0.wireOp",EDGE,"E21.MirrorCS"),sQuery(id+"F0.wireOp",EDGE,"E22.MirrorCS"),subQ0,sQuery(id+"F0.wireOp",EDGE,"E24.MirrorCS"),sQuery(id+"F0.wireOp",EDGE,"E25.MirrorCS"),sQuery(id+"F0.wireOp",EDGE,"E26.MirrorCS"),sQuery(id+"F0.wireOp",EDGE,"E27.MirrorCS"),sQuery(id+"F0.wireOp",EDGE,"E28.MirrorCS"),sQuery(id+"F0.wireOp",EDGE,"E29.MirrorCS"),sQuery(id+"F0.wireOp",EDGE,"E30.MirrorCS"),sQuery(id+"F0.wireOp",EDGE,"E31.MirrorCS")])],"isStart":false})]}),makeQuery(id+"F6.opExtrude","CAP_EDGE",EDGE,{"disambiguationData":[OSD([sQuery(id+"F5.wireOp",EDGE,"E70.0")])],"isStart":true})]});}
            var Q62;
            {var subQ0=sQuery(id+"F0.wireOp",EDGE,"E22.MirrorCS");Q62=makeQuery(id+"F6.boolean.opBoolean","MERGE",EDGE,{"derivedFrom":[makeQuery(id+"F2.opFillet","BLEND_EDGE",EDGE,{"blendedFrom":[makeQuery(id+"F1.opExtrude","CAP_EDGE",EDGE,{"disambiguationData":[OSD([subQ0])],"isStart":false}),makeQuery(id+"F1.opExtrude","CAP_FACE",FACE,{"disambiguationData":[OSD([sQuery(id+"F0.wireOp",EDGE,"E0"),sQuery(id+"F0.wireOp",EDGE,"E1.0"),sQuery(id+"F0.wireOp",EDGE,"E1.1"),sQuery(id+"F0.wireOp",EDGE,"E1.2"),sQuery(id+"F0.wireOp",EDGE,"E1.3"),sQuery(id+"F0.wireOp",EDGE,"E1.4"),sQuery(id+"F0.wireOp",EDGE,"E1.5"),sQuery(id+"F0.wireOp",EDGE,"E1.6"),sQuery(id+"F0.wireOp",EDGE,"E1.7"),sQuery(id+"F0.wireOp",EDGE,"E1.8"),sQuery(id+"F0.wireOp",EDGE,"E1.9"),sQuery(id+"F0.wireOp",EDGE,"E1.10"),sQuery(id+"F0.wireOp",EDGE,"E2"),sQuery(id+"F0.wireOp",EDGE,"E3.2.0"),sQuery(id+"F0.wireOp",EDGE,"E3.3.0"),sQuery(id+"F0.wireOp",EDGE,"E3.4.0"),sQuery(id+"F0.wireOp",EDGE,"E3.5.0"),sQuery(id+"F0.wireOp",EDGE,"E3.6.0"),sQuery(id+"F0.wireOp",EDGE,"E3.7.0"),sQuery(id+"F0.wireOp",EDGE,"E3.8.0"),sQuery(id+"F0.wireOp",EDGE,"E3.9.0"),sQuery(id+"F0.wireOp",EDGE,"E3.10.0"),sQuery(id+"F0.wireOp",EDGE,"E4"),sQuery(id+"F0.wireOp",EDGE,"E5"),sQuery(id+"F0.wireOp",EDGE,"E6"),sQuery(id+"F0.wireOp",EDGE,"E7"),sQuery(id+"F0.wireOp",EDGE,"E8"),sQuery(id+"F0.wireOp",EDGE,"E9"),sQuery(id+"F0.wireOp",EDGE,"E10"),sQuery(id+"F0.wireOp",EDGE,"E11"),sQuery(id+"F0.wireOp",EDGE,"E12"),sQuery(id+"F0.wireOp",EDGE,"E13"),sQuery(id+"F0.wireOp",EDGE,"E14"),sQuery(id+"F0.wireOp",EDGE,"E15"),sQuery(id+"F0.wireOp",EDGE,"E16"),sQuery(id+"F0.wireOp",EDGE,"E17"),sQuery(id+"F0.wireOp",EDGE,"E18.MirrorCS"),sQuery(id+"F0.wireOp",EDGE,"E19.MirrorCS"),sQuery(id+"F0.wireOp",EDGE,"E20.MirrorCS"),sQuery(id+"F0.wireOp",EDGE,"E21.MirrorCS"),subQ0,sQuery(id+"F0.wireOp",EDGE,"E23.MirrorCS"),sQuery(id+"F0.wireOp",EDGE,"E24.MirrorCS"),sQuery(id+"F0.wireOp",EDGE,"E25.MirrorCS"),sQuery(id+"F0.wireOp",EDGE,"E26.MirrorCS"),sQuery(id+"F0.wireOp",EDGE,"E27.MirrorCS"),sQuery(id+"F0.wireOp",EDGE,"E28.MirrorCS"),sQuery(id+"F0.wireOp",EDGE,"E29.MirrorCS"),sQuery(id+"F0.wireOp",EDGE,"E30.MirrorCS"),sQuery(id+"F0.wireOp",EDGE,"E31.MirrorCS")])],"isStart":false})],"blendedInto":[makeQuery(id+"F1.opExtrude","CAP_FACE",FACE,{"disambiguationData":[OSD([sQuery(id+"F0.wireOp",EDGE,"E0"),sQuery(id+"F0.wireOp",EDGE,"E1.0"),sQuery(id+"F0.wireOp",EDGE,"E1.1"),sQuery(id+"F0.wireOp",EDGE,"E1.2"),sQuery(id+"F0.wireOp",EDGE,"E1.3"),sQuery(id+"F0.wireOp",EDGE,"E1.4"),sQuery(id+"F0.wireOp",EDGE,"E1.5"),sQuery(id+"F0.wireOp",EDGE,"E1.6"),sQuery(id+"F0.wireOp",EDGE,"E1.7"),sQuery(id+"F0.wireOp",EDGE,"E1.8"),sQuery(id+"F0.wireOp",EDGE,"E1.9"),sQuery(id+"F0.wireOp",EDGE,"E1.10"),sQuery(id+"F0.wireOp",EDGE,"E2"),sQuery(id+"F0.wireOp",EDGE,"E3.2.0"),sQuery(id+"F0.wireOp",EDGE,"E3.3.0"),sQuery(id+"F0.wireOp",EDGE,"E3.4.0"),sQuery(id+"F0.wireOp",EDGE,"E3.5.0"),sQuery(id+"F0.wireOp",EDGE,"E3.6.0"),sQuery(id+"F0.wireOp",EDGE,"E3.7.0"),sQuery(id+"F0.wireOp",EDGE,"E3.8.0"),sQuery(id+"F0.wireOp",EDGE,"E3.9.0"),sQuery(id+"F0.wireOp",EDGE,"E3.10.0"),sQuery(id+"F0.wireOp",EDGE,"E4"),sQuery(id+"F0.wireOp",EDGE,"E5"),sQuery(id+"F0.wireOp",EDGE,"E6"),sQuery(id+"F0.wireOp",EDGE,"E7"),sQuery(id+"F0.wireOp",EDGE,"E8"),sQuery(id+"F0.wireOp",EDGE,"E9"),sQuery(id+"F0.wireOp",EDGE,"E10"),sQuery(id+"F0.wireOp",EDGE,"E11"),sQuery(id+"F0.wireOp",EDGE,"E12"),sQuery(id+"F0.wireOp",EDGE,"E13"),sQuery(id+"F0.wireOp",EDGE,"E14"),sQuery(id+"F0.wireOp",EDGE,"E15"),sQuery(id+"F0.wireOp",EDGE,"E16"),sQuery(id+"F0.wireOp",EDGE,"E17"),sQuery(id+"F0.wireOp",EDGE,"E18.MirrorCS"),sQuery(id+"F0.wireOp",EDGE,"E19.MirrorCS"),sQuery(id+"F0.wireOp",EDGE,"E20.MirrorCS"),sQuery(id+"F0.wireOp",EDGE,"E21.MirrorCS"),subQ0,sQuery(id+"F0.wireOp",EDGE,"E23.MirrorCS"),sQuery(id+"F0.wireOp",EDGE,"E24.MirrorCS"),sQuery(id+"F0.wireOp",EDGE,"E25.MirrorCS"),sQuery(id+"F0.wireOp",EDGE,"E26.MirrorCS"),sQuery(id+"F0.wireOp",EDGE,"E27.MirrorCS"),sQuery(id+"F0.wireOp",EDGE,"E28.MirrorCS"),sQuery(id+"F0.wireOp",EDGE,"E29.MirrorCS"),sQuery(id+"F0.wireOp",EDGE,"E30.MirrorCS"),sQuery(id+"F0.wireOp",EDGE,"E31.MirrorCS")])],"isStart":false})]}),makeQuery(id+"F6.opExtrude","CAP_EDGE",EDGE,{"disambiguationData":[OSD([sQuery(id+"F5.wireOp",EDGE,"E65.0")])],"isStart":true})]});}
            var Q63;
            {var subQ0=sQuery(id+"F0.wireOp",EDGE,"E21.MirrorCS");Q63=makeQuery(id+"F6.boolean.opBoolean","MERGE",EDGE,{"derivedFrom":[makeQuery(id+"F2.opFillet","BLEND_EDGE",EDGE,{"blendedFrom":[makeQuery(id+"F1.opExtrude","CAP_EDGE",EDGE,{"disambiguationData":[OSD([subQ0])],"isStart":false}),makeQuery(id+"F1.opExtrude","CAP_FACE",FACE,{"disambiguationData":[OSD([sQuery(id+"F0.wireOp",EDGE,"E0"),sQuery(id+"F0.wireOp",EDGE,"E1.0"),sQuery(id+"F0.wireOp",EDGE,"E1.1"),sQuery(id+"F0.wireOp",EDGE,"E1.2"),sQuery(id+"F0.wireOp",EDGE,"E1.3"),sQuery(id+"F0.wireOp",EDGE,"E1.4"),sQuery(id+"F0.wireOp",EDGE,"E1.5"),sQuery(id+"F0.wireOp",EDGE,"E1.6"),sQuery(id+"F0.wireOp",EDGE,"E1.7"),sQuery(id+"F0.wireOp",EDGE,"E1.8"),sQuery(id+"F0.wireOp",EDGE,"E1.9"),sQuery(id+"F0.wireOp",EDGE,"E1.10"),sQuery(id+"F0.wireOp",EDGE,"E2"),sQuery(id+"F0.wireOp",EDGE,"E3.2.0"),sQuery(id+"F0.wireOp",EDGE,"E3.3.0"),sQuery(id+"F0.wireOp",EDGE,"E3.4.0"),sQuery(id+"F0.wireOp",EDGE,"E3.5.0"),sQuery(id+"F0.wireOp",EDGE,"E3.6.0"),sQuery(id+"F0.wireOp",EDGE,"E3.7.0"),sQuery(id+"F0.wireOp",EDGE,"E3.8.0"),sQuery(id+"F0.wireOp",EDGE,"E3.9.0"),sQuery(id+"F0.wireOp",EDGE,"E3.10.0"),sQuery(id+"F0.wireOp",EDGE,"E4"),sQuery(id+"F0.wireOp",EDGE,"E5"),sQuery(id+"F0.wireOp",EDGE,"E6"),sQuery(id+"F0.wireOp",EDGE,"E7"),sQuery(id+"F0.wireOp",EDGE,"E8"),sQuery(id+"F0.wireOp",EDGE,"E9"),sQuery(id+"F0.wireOp",EDGE,"E10"),sQuery(id+"F0.wireOp",EDGE,"E11"),sQuery(id+"F0.wireOp",EDGE,"E12"),sQuery(id+"F0.wireOp",EDGE,"E13"),sQuery(id+"F0.wireOp",EDGE,"E14"),sQuery(id+"F0.wireOp",EDGE,"E15"),sQuery(id+"F0.wireOp",EDGE,"E16"),sQuery(id+"F0.wireOp",EDGE,"E17"),sQuery(id+"F0.wireOp",EDGE,"E18.MirrorCS"),sQuery(id+"F0.wireOp",EDGE,"E19.MirrorCS"),sQuery(id+"F0.wireOp",EDGE,"E20.MirrorCS"),subQ0,sQuery(id+"F0.wireOp",EDGE,"E22.MirrorCS"),sQuery(id+"F0.wireOp",EDGE,"E23.MirrorCS"),sQuery(id+"F0.wireOp",EDGE,"E24.MirrorCS"),sQuery(id+"F0.wireOp",EDGE,"E25.MirrorCS"),sQuery(id+"F0.wireOp",EDGE,"E26.MirrorCS"),sQuery(id+"F0.wireOp",EDGE,"E27.MirrorCS"),sQuery(id+"F0.wireOp",EDGE,"E28.MirrorCS"),sQuery(id+"F0.wireOp",EDGE,"E29.MirrorCS"),sQuery(id+"F0.wireOp",EDGE,"E30.MirrorCS"),sQuery(id+"F0.wireOp",EDGE,"E31.MirrorCS")])],"isStart":false})],"blendedInto":[makeQuery(id+"F1.opExtrude","CAP_FACE",FACE,{"disambiguationData":[OSD([sQuery(id+"F0.wireOp",EDGE,"E0"),sQuery(id+"F0.wireOp",EDGE,"E1.0"),sQuery(id+"F0.wireOp",EDGE,"E1.1"),sQuery(id+"F0.wireOp",EDGE,"E1.2"),sQuery(id+"F0.wireOp",EDGE,"E1.3"),sQuery(id+"F0.wireOp",EDGE,"E1.4"),sQuery(id+"F0.wireOp",EDGE,"E1.5"),sQuery(id+"F0.wireOp",EDGE,"E1.6"),sQuery(id+"F0.wireOp",EDGE,"E1.7"),sQuery(id+"F0.wireOp",EDGE,"E1.8"),sQuery(id+"F0.wireOp",EDGE,"E1.9"),sQuery(id+"F0.wireOp",EDGE,"E1.10"),sQuery(id+"F0.wireOp",EDGE,"E2"),sQuery(id+"F0.wireOp",EDGE,"E3.2.0"),sQuery(id+"F0.wireOp",EDGE,"E3.3.0"),sQuery(id+"F0.wireOp",EDGE,"E3.4.0"),sQuery(id+"F0.wireOp",EDGE,"E3.5.0"),sQuery(id+"F0.wireOp",EDGE,"E3.6.0"),sQuery(id+"F0.wireOp",EDGE,"E3.7.0"),sQuery(id+"F0.wireOp",EDGE,"E3.8.0"),sQuery(id+"F0.wireOp",EDGE,"E3.9.0"),sQuery(id+"F0.wireOp",EDGE,"E3.10.0"),sQuery(id+"F0.wireOp",EDGE,"E4"),sQuery(id+"F0.wireOp",EDGE,"E5"),sQuery(id+"F0.wireOp",EDGE,"E6"),sQuery(id+"F0.wireOp",EDGE,"E7"),sQuery(id+"F0.wireOp",EDGE,"E8"),sQuery(id+"F0.wireOp",EDGE,"E9"),sQuery(id+"F0.wireOp",EDGE,"E10"),sQuery(id+"F0.wireOp",EDGE,"E11"),sQuery(id+"F0.wireOp",EDGE,"E12"),sQuery(id+"F0.wireOp",EDGE,"E13"),sQuery(id+"F0.wireOp",EDGE,"E14"),sQuery(id+"F0.wireOp",EDGE,"E15"),sQuery(id+"F0.wireOp",EDGE,"E16"),sQuery(id+"F0.wireOp",EDGE,"E17"),sQuery(id+"F0.wireOp",EDGE,"E18.MirrorCS"),sQuery(id+"F0.wireOp",EDGE,"E19.MirrorCS"),sQuery(id+"F0.wireOp",EDGE,"E20.MirrorCS"),subQ0,sQuery(id+"F0.wireOp",EDGE,"E22.MirrorCS"),sQuery(id+"F0.wireOp",EDGE,"E23.MirrorCS"),sQuery(id+"F0.wireOp",EDGE,"E24.MirrorCS"),sQuery(id+"F0.wireOp",EDGE,"E25.MirrorCS"),sQuery(id+"F0.wireOp",EDGE,"E26.MirrorCS"),sQuery(id+"F0.wireOp",EDGE,"E27.MirrorCS"),sQuery(id+"F0.wireOp",EDGE,"E28.MirrorCS"),sQuery(id+"F0.wireOp",EDGE,"E29.MirrorCS"),sQuery(id+"F0.wireOp",EDGE,"E30.MirrorCS"),sQuery(id+"F0.wireOp",EDGE,"E31.MirrorCS")])],"isStart":false})]}),makeQuery(id+"F6.opExtrude","CAP_EDGE",EDGE,{"disambiguationData":[OSD([sQuery(id+"F5.wireOp",EDGE,"E72.0")])],"isStart":true})]});}
            var Q64;
            {var subQ0=sQuery(id+"F0.wireOp",EDGE,"E20.MirrorCS");Q64=makeQuery(id+"F6.boolean.opBoolean","MERGE",EDGE,{"derivedFrom":[makeQuery(id+"F2.opFillet","BLEND_EDGE",EDGE,{"blendedFrom":[makeQuery(id+"F1.opExtrude","CAP_EDGE",EDGE,{"disambiguationData":[OSD([subQ0])],"isStart":false}),makeQuery(id+"F1.opExtrude","CAP_FACE",FACE,{"disambiguationData":[OSD([sQuery(id+"F0.wireOp",EDGE,"E0"),sQuery(id+"F0.wireOp",EDGE,"E1.0"),sQuery(id+"F0.wireOp",EDGE,"E1.1"),sQuery(id+"F0.wireOp",EDGE,"E1.2"),sQuery(id+"F0.wireOp",EDGE,"E1.3"),sQuery(id+"F0.wireOp",EDGE,"E1.4"),sQuery(id+"F0.wireOp",EDGE,"E1.5"),sQuery(id+"F0.wireOp",EDGE,"E1.6"),sQuery(id+"F0.wireOp",EDGE,"E1.7"),sQuery(id+"F0.wireOp",EDGE,"E1.8"),sQuery(id+"F0.wireOp",EDGE,"E1.9"),sQuery(id+"F0.wireOp",EDGE,"E1.10"),sQuery(id+"F0.wireOp",EDGE,"E2"),sQuery(id+"F0.wireOp",EDGE,"E3.2.0"),sQuery(id+"F0.wireOp",EDGE,"E3.3.0"),sQuery(id+"F0.wireOp",EDGE,"E3.4.0"),sQuery(id+"F0.wireOp",EDGE,"E3.5.0"),sQuery(id+"F0.wireOp",EDGE,"E3.6.0"),sQuery(id+"F0.wireOp",EDGE,"E3.7.0"),sQuery(id+"F0.wireOp",EDGE,"E3.8.0"),sQuery(id+"F0.wireOp",EDGE,"E3.9.0"),sQuery(id+"F0.wireOp",EDGE,"E3.10.0"),sQuery(id+"F0.wireOp",EDGE,"E4"),sQuery(id+"F0.wireOp",EDGE,"E5"),sQuery(id+"F0.wireOp",EDGE,"E6"),sQuery(id+"F0.wireOp",EDGE,"E7"),sQuery(id+"F0.wireOp",EDGE,"E8"),sQuery(id+"F0.wireOp",EDGE,"E9"),sQuery(id+"F0.wireOp",EDGE,"E10"),sQuery(id+"F0.wireOp",EDGE,"E11"),sQuery(id+"F0.wireOp",EDGE,"E12"),sQuery(id+"F0.wireOp",EDGE,"E13"),sQuery(id+"F0.wireOp",EDGE,"E14"),sQuery(id+"F0.wireOp",EDGE,"E15"),sQuery(id+"F0.wireOp",EDGE,"E16"),sQuery(id+"F0.wireOp",EDGE,"E17"),sQuery(id+"F0.wireOp",EDGE,"E18.MirrorCS"),sQuery(id+"F0.wireOp",EDGE,"E19.MirrorCS"),subQ0,sQuery(id+"F0.wireOp",EDGE,"E21.MirrorCS"),sQuery(id+"F0.wireOp",EDGE,"E22.MirrorCS"),sQuery(id+"F0.wireOp",EDGE,"E23.MirrorCS"),sQuery(id+"F0.wireOp",EDGE,"E24.MirrorCS"),sQuery(id+"F0.wireOp",EDGE,"E25.MirrorCS"),sQuery(id+"F0.wireOp",EDGE,"E26.MirrorCS"),sQuery(id+"F0.wireOp",EDGE,"E27.MirrorCS"),sQuery(id+"F0.wireOp",EDGE,"E28.MirrorCS"),sQuery(id+"F0.wireOp",EDGE,"E29.MirrorCS"),sQuery(id+"F0.wireOp",EDGE,"E30.MirrorCS"),sQuery(id+"F0.wireOp",EDGE,"E31.MirrorCS")])],"isStart":false})],"blendedInto":[makeQuery(id+"F1.opExtrude","CAP_FACE",FACE,{"disambiguationData":[OSD([sQuery(id+"F0.wireOp",EDGE,"E0"),sQuery(id+"F0.wireOp",EDGE,"E1.0"),sQuery(id+"F0.wireOp",EDGE,"E1.1"),sQuery(id+"F0.wireOp",EDGE,"E1.2"),sQuery(id+"F0.wireOp",EDGE,"E1.3"),sQuery(id+"F0.wireOp",EDGE,"E1.4"),sQuery(id+"F0.wireOp",EDGE,"E1.5"),sQuery(id+"F0.wireOp",EDGE,"E1.6"),sQuery(id+"F0.wireOp",EDGE,"E1.7"),sQuery(id+"F0.wireOp",EDGE,"E1.8"),sQuery(id+"F0.wireOp",EDGE,"E1.9"),sQuery(id+"F0.wireOp",EDGE,"E1.10"),sQuery(id+"F0.wireOp",EDGE,"E2"),sQuery(id+"F0.wireOp",EDGE,"E3.2.0"),sQuery(id+"F0.wireOp",EDGE,"E3.3.0"),sQuery(id+"F0.wireOp",EDGE,"E3.4.0"),sQuery(id+"F0.wireOp",EDGE,"E3.5.0"),sQuery(id+"F0.wireOp",EDGE,"E3.6.0"),sQuery(id+"F0.wireOp",EDGE,"E3.7.0"),sQuery(id+"F0.wireOp",EDGE,"E3.8.0"),sQuery(id+"F0.wireOp",EDGE,"E3.9.0"),sQuery(id+"F0.wireOp",EDGE,"E3.10.0"),sQuery(id+"F0.wireOp",EDGE,"E4"),sQuery(id+"F0.wireOp",EDGE,"E5"),sQuery(id+"F0.wireOp",EDGE,"E6"),sQuery(id+"F0.wireOp",EDGE,"E7"),sQuery(id+"F0.wireOp",EDGE,"E8"),sQuery(id+"F0.wireOp",EDGE,"E9"),sQuery(id+"F0.wireOp",EDGE,"E10"),sQuery(id+"F0.wireOp",EDGE,"E11"),sQuery(id+"F0.wireOp",EDGE,"E12"),sQuery(id+"F0.wireOp",EDGE,"E13"),sQuery(id+"F0.wireOp",EDGE,"E14"),sQuery(id+"F0.wireOp",EDGE,"E15"),sQuery(id+"F0.wireOp",EDGE,"E16"),sQuery(id+"F0.wireOp",EDGE,"E17"),sQuery(id+"F0.wireOp",EDGE,"E18.MirrorCS"),sQuery(id+"F0.wireOp",EDGE,"E19.MirrorCS"),subQ0,sQuery(id+"F0.wireOp",EDGE,"E21.MirrorCS"),sQuery(id+"F0.wireOp",EDGE,"E22.MirrorCS"),sQuery(id+"F0.wireOp",EDGE,"E23.MirrorCS"),sQuery(id+"F0.wireOp",EDGE,"E24.MirrorCS"),sQuery(id+"F0.wireOp",EDGE,"E25.MirrorCS"),sQuery(id+"F0.wireOp",EDGE,"E26.MirrorCS"),sQuery(id+"F0.wireOp",EDGE,"E27.MirrorCS"),sQuery(id+"F0.wireOp",EDGE,"E28.MirrorCS"),sQuery(id+"F0.wireOp",EDGE,"E29.MirrorCS"),sQuery(id+"F0.wireOp",EDGE,"E30.MirrorCS"),sQuery(id+"F0.wireOp",EDGE,"E31.MirrorCS")])],"isStart":false})]}),makeQuery(id+"F6.opExtrude","CAP_EDGE",EDGE,{"disambiguationData":[OSD([sQuery(id+"F5.wireOp",EDGE,"E79.0")])],"isStart":true})]});}
            var Q65;
            {var subQ0=sQuery(id+"F0.wireOp",EDGE,"E19.MirrorCS");Q65=makeQuery(id+"F6.boolean.opBoolean","MERGE",EDGE,{"derivedFrom":[makeQuery(id+"F2.opFillet","BLEND_EDGE",EDGE,{"blendedFrom":[makeQuery(id+"F1.opExtrude","CAP_EDGE",EDGE,{"disambiguationData":[OSD([subQ0])],"isStart":false}),makeQuery(id+"F1.opExtrude","CAP_FACE",FACE,{"disambiguationData":[OSD([sQuery(id+"F0.wireOp",EDGE,"E0"),sQuery(id+"F0.wireOp",EDGE,"E1.0"),sQuery(id+"F0.wireOp",EDGE,"E1.1"),sQuery(id+"F0.wireOp",EDGE,"E1.2"),sQuery(id+"F0.wireOp",EDGE,"E1.3"),sQuery(id+"F0.wireOp",EDGE,"E1.4"),sQuery(id+"F0.wireOp",EDGE,"E1.5"),sQuery(id+"F0.wireOp",EDGE,"E1.6"),sQuery(id+"F0.wireOp",EDGE,"E1.7"),sQuery(id+"F0.wireOp",EDGE,"E1.8"),sQuery(id+"F0.wireOp",EDGE,"E1.9"),sQuery(id+"F0.wireOp",EDGE,"E1.10"),sQuery(id+"F0.wireOp",EDGE,"E2"),sQuery(id+"F0.wireOp",EDGE,"E3.2.0"),sQuery(id+"F0.wireOp",EDGE,"E3.3.0"),sQuery(id+"F0.wireOp",EDGE,"E3.4.0"),sQuery(id+"F0.wireOp",EDGE,"E3.5.0"),sQuery(id+"F0.wireOp",EDGE,"E3.6.0"),sQuery(id+"F0.wireOp",EDGE,"E3.7.0"),sQuery(id+"F0.wireOp",EDGE,"E3.8.0"),sQuery(id+"F0.wireOp",EDGE,"E3.9.0"),sQuery(id+"F0.wireOp",EDGE,"E3.10.0"),sQuery(id+"F0.wireOp",EDGE,"E4"),sQuery(id+"F0.wireOp",EDGE,"E5"),sQuery(id+"F0.wireOp",EDGE,"E6"),sQuery(id+"F0.wireOp",EDGE,"E7"),sQuery(id+"F0.wireOp",EDGE,"E8"),sQuery(id+"F0.wireOp",EDGE,"E9"),sQuery(id+"F0.wireOp",EDGE,"E10"),sQuery(id+"F0.wireOp",EDGE,"E11"),sQuery(id+"F0.wireOp",EDGE,"E12"),sQuery(id+"F0.wireOp",EDGE,"E13"),sQuery(id+"F0.wireOp",EDGE,"E14"),sQuery(id+"F0.wireOp",EDGE,"E15"),sQuery(id+"F0.wireOp",EDGE,"E16"),sQuery(id+"F0.wireOp",EDGE,"E17"),sQuery(id+"F0.wireOp",EDGE,"E18.MirrorCS"),subQ0,sQuery(id+"F0.wireOp",EDGE,"E20.MirrorCS"),sQuery(id+"F0.wireOp",EDGE,"E21.MirrorCS"),sQuery(id+"F0.wireOp",EDGE,"E22.MirrorCS"),sQuery(id+"F0.wireOp",EDGE,"E23.MirrorCS"),sQuery(id+"F0.wireOp",EDGE,"E24.MirrorCS"),sQuery(id+"F0.wireOp",EDGE,"E25.MirrorCS"),sQuery(id+"F0.wireOp",EDGE,"E26.MirrorCS"),sQuery(id+"F0.wireOp",EDGE,"E27.MirrorCS"),sQuery(id+"F0.wireOp",EDGE,"E28.MirrorCS"),sQuery(id+"F0.wireOp",EDGE,"E29.MirrorCS"),sQuery(id+"F0.wireOp",EDGE,"E30.MirrorCS"),sQuery(id+"F0.wireOp",EDGE,"E31.MirrorCS")])],"isStart":false})],"blendedInto":[makeQuery(id+"F1.opExtrude","CAP_FACE",FACE,{"disambiguationData":[OSD([sQuery(id+"F0.wireOp",EDGE,"E0"),sQuery(id+"F0.wireOp",EDGE,"E1.0"),sQuery(id+"F0.wireOp",EDGE,"E1.1"),sQuery(id+"F0.wireOp",EDGE,"E1.2"),sQuery(id+"F0.wireOp",EDGE,"E1.3"),sQuery(id+"F0.wireOp",EDGE,"E1.4"),sQuery(id+"F0.wireOp",EDGE,"E1.5"),sQuery(id+"F0.wireOp",EDGE,"E1.6"),sQuery(id+"F0.wireOp",EDGE,"E1.7"),sQuery(id+"F0.wireOp",EDGE,"E1.8"),sQuery(id+"F0.wireOp",EDGE,"E1.9"),sQuery(id+"F0.wireOp",EDGE,"E1.10"),sQuery(id+"F0.wireOp",EDGE,"E2"),sQuery(id+"F0.wireOp",EDGE,"E3.2.0"),sQuery(id+"F0.wireOp",EDGE,"E3.3.0"),sQuery(id+"F0.wireOp",EDGE,"E3.4.0"),sQuery(id+"F0.wireOp",EDGE,"E3.5.0"),sQuery(id+"F0.wireOp",EDGE,"E3.6.0"),sQuery(id+"F0.wireOp",EDGE,"E3.7.0"),sQuery(id+"F0.wireOp",EDGE,"E3.8.0"),sQuery(id+"F0.wireOp",EDGE,"E3.9.0"),sQuery(id+"F0.wireOp",EDGE,"E3.10.0"),sQuery(id+"F0.wireOp",EDGE,"E4"),sQuery(id+"F0.wireOp",EDGE,"E5"),sQuery(id+"F0.wireOp",EDGE,"E6"),sQuery(id+"F0.wireOp",EDGE,"E7"),sQuery(id+"F0.wireOp",EDGE,"E8"),sQuery(id+"F0.wireOp",EDGE,"E9"),sQuery(id+"F0.wireOp",EDGE,"E10"),sQuery(id+"F0.wireOp",EDGE,"E11"),sQuery(id+"F0.wireOp",EDGE,"E12"),sQuery(id+"F0.wireOp",EDGE,"E13"),sQuery(id+"F0.wireOp",EDGE,"E14"),sQuery(id+"F0.wireOp",EDGE,"E15"),sQuery(id+"F0.wireOp",EDGE,"E16"),sQuery(id+"F0.wireOp",EDGE,"E17"),sQuery(id+"F0.wireOp",EDGE,"E18.MirrorCS"),subQ0,sQuery(id+"F0.wireOp",EDGE,"E20.MirrorCS"),sQuery(id+"F0.wireOp",EDGE,"E21.MirrorCS"),sQuery(id+"F0.wireOp",EDGE,"E22.MirrorCS"),sQuery(id+"F0.wireOp",EDGE,"E23.MirrorCS"),sQuery(id+"F0.wireOp",EDGE,"E24.MirrorCS"),sQuery(id+"F0.wireOp",EDGE,"E25.MirrorCS"),sQuery(id+"F0.wireOp",EDGE,"E26.MirrorCS"),sQuery(id+"F0.wireOp",EDGE,"E27.MirrorCS"),sQuery(id+"F0.wireOp",EDGE,"E28.MirrorCS"),sQuery(id+"F0.wireOp",EDGE,"E29.MirrorCS"),sQuery(id+"F0.wireOp",EDGE,"E30.MirrorCS"),sQuery(id+"F0.wireOp",EDGE,"E31.MirrorCS")])],"isStart":false})]}),makeQuery(id+"F6.opExtrude","CAP_EDGE",EDGE,{"disambiguationData":[OSD([sQuery(id+"F5.wireOp",EDGE,"E80.0")])],"isStart":true})]});}
            var Q66;
            {var subQ0=sQuery(id+"F0.wireOp",EDGE,"E18.MirrorCS");var subQ1=sQuery(id+"F0.wireOp",EDGE,"E17");Q66=makeQuery(id+"F6.boolean.opBoolean","MERGE",EDGE,{"derivedFrom":[makeQuery(id+"F2.opFillet","BLEND_EDGE",EDGE,{"blendedFrom":[makeQuery(id+"F1.opExtrude","CAP_EDGE",EDGE,{"disambiguationData":[OSD([subQ1,subQ0])],"isStart":false}),makeQuery(id+"F1.opExtrude","CAP_FACE",FACE,{"disambiguationData":[OSD([sQuery(id+"F0.wireOp",EDGE,"E0"),sQuery(id+"F0.wireOp",EDGE,"E1.0"),sQuery(id+"F0.wireOp",EDGE,"E1.1"),sQuery(id+"F0.wireOp",EDGE,"E1.2"),sQuery(id+"F0.wireOp",EDGE,"E1.3"),sQuery(id+"F0.wireOp",EDGE,"E1.4"),sQuery(id+"F0.wireOp",EDGE,"E1.5"),sQuery(id+"F0.wireOp",EDGE,"E1.6"),sQuery(id+"F0.wireOp",EDGE,"E1.7"),sQuery(id+"F0.wireOp",EDGE,"E1.8"),sQuery(id+"F0.wireOp",EDGE,"E1.9"),sQuery(id+"F0.wireOp",EDGE,"E1.10"),sQuery(id+"F0.wireOp",EDGE,"E2"),sQuery(id+"F0.wireOp",EDGE,"E3.2.0"),sQuery(id+"F0.wireOp",EDGE,"E3.3.0"),sQuery(id+"F0.wireOp",EDGE,"E3.4.0"),sQuery(id+"F0.wireOp",EDGE,"E3.5.0"),sQuery(id+"F0.wireOp",EDGE,"E3.6.0"),sQuery(id+"F0.wireOp",EDGE,"E3.7.0"),sQuery(id+"F0.wireOp",EDGE,"E3.8.0"),sQuery(id+"F0.wireOp",EDGE,"E3.9.0"),sQuery(id+"F0.wireOp",EDGE,"E3.10.0"),sQuery(id+"F0.wireOp",EDGE,"E4"),sQuery(id+"F0.wireOp",EDGE,"E5"),sQuery(id+"F0.wireOp",EDGE,"E6"),sQuery(id+"F0.wireOp",EDGE,"E7"),sQuery(id+"F0.wireOp",EDGE,"E8"),sQuery(id+"F0.wireOp",EDGE,"E9"),sQuery(id+"F0.wireOp",EDGE,"E10"),sQuery(id+"F0.wireOp",EDGE,"E11"),sQuery(id+"F0.wireOp",EDGE,"E12"),sQuery(id+"F0.wireOp",EDGE,"E13"),sQuery(id+"F0.wireOp",EDGE,"E14"),sQuery(id+"F0.wireOp",EDGE,"E15"),sQuery(id+"F0.wireOp",EDGE,"E16"),subQ1,subQ0,sQuery(id+"F0.wireOp",EDGE,"E19.MirrorCS"),sQuery(id+"F0.wireOp",EDGE,"E20.MirrorCS"),sQuery(id+"F0.wireOp",EDGE,"E21.MirrorCS"),sQuery(id+"F0.wireOp",EDGE,"E22.MirrorCS"),sQuery(id+"F0.wireOp",EDGE,"E23.MirrorCS"),sQuery(id+"F0.wireOp",EDGE,"E24.MirrorCS"),sQuery(id+"F0.wireOp",EDGE,"E25.MirrorCS"),sQuery(id+"F0.wireOp",EDGE,"E26.MirrorCS"),sQuery(id+"F0.wireOp",EDGE,"E27.MirrorCS"),sQuery(id+"F0.wireOp",EDGE,"E28.MirrorCS"),sQuery(id+"F0.wireOp",EDGE,"E29.MirrorCS"),sQuery(id+"F0.wireOp",EDGE,"E30.MirrorCS"),sQuery(id+"F0.wireOp",EDGE,"E31.MirrorCS")])],"isStart":false})],"blendedInto":[makeQuery(id+"F1.opExtrude","CAP_FACE",FACE,{"disambiguationData":[OSD([sQuery(id+"F0.wireOp",EDGE,"E0"),sQuery(id+"F0.wireOp",EDGE,"E1.0"),sQuery(id+"F0.wireOp",EDGE,"E1.1"),sQuery(id+"F0.wireOp",EDGE,"E1.2"),sQuery(id+"F0.wireOp",EDGE,"E1.3"),sQuery(id+"F0.wireOp",EDGE,"E1.4"),sQuery(id+"F0.wireOp",EDGE,"E1.5"),sQuery(id+"F0.wireOp",EDGE,"E1.6"),sQuery(id+"F0.wireOp",EDGE,"E1.7"),sQuery(id+"F0.wireOp",EDGE,"E1.8"),sQuery(id+"F0.wireOp",EDGE,"E1.9"),sQuery(id+"F0.wireOp",EDGE,"E1.10"),sQuery(id+"F0.wireOp",EDGE,"E2"),sQuery(id+"F0.wireOp",EDGE,"E3.2.0"),sQuery(id+"F0.wireOp",EDGE,"E3.3.0"),sQuery(id+"F0.wireOp",EDGE,"E3.4.0"),sQuery(id+"F0.wireOp",EDGE,"E3.5.0"),sQuery(id+"F0.wireOp",EDGE,"E3.6.0"),sQuery(id+"F0.wireOp",EDGE,"E3.7.0"),sQuery(id+"F0.wireOp",EDGE,"E3.8.0"),sQuery(id+"F0.wireOp",EDGE,"E3.9.0"),sQuery(id+"F0.wireOp",EDGE,"E3.10.0"),sQuery(id+"F0.wireOp",EDGE,"E4"),sQuery(id+"F0.wireOp",EDGE,"E5"),sQuery(id+"F0.wireOp",EDGE,"E6"),sQuery(id+"F0.wireOp",EDGE,"E7"),sQuery(id+"F0.wireOp",EDGE,"E8"),sQuery(id+"F0.wireOp",EDGE,"E9"),sQuery(id+"F0.wireOp",EDGE,"E10"),sQuery(id+"F0.wireOp",EDGE,"E11"),sQuery(id+"F0.wireOp",EDGE,"E12"),sQuery(id+"F0.wireOp",EDGE,"E13"),sQuery(id+"F0.wireOp",EDGE,"E14"),sQuery(id+"F0.wireOp",EDGE,"E15"),sQuery(id+"F0.wireOp",EDGE,"E16"),subQ1,subQ0,sQuery(id+"F0.wireOp",EDGE,"E19.MirrorCS"),sQuery(id+"F0.wireOp",EDGE,"E20.MirrorCS"),sQuery(id+"F0.wireOp",EDGE,"E21.MirrorCS"),sQuery(id+"F0.wireOp",EDGE,"E22.MirrorCS"),sQuery(id+"F0.wireOp",EDGE,"E23.MirrorCS"),sQuery(id+"F0.wireOp",EDGE,"E24.MirrorCS"),sQuery(id+"F0.wireOp",EDGE,"E25.MirrorCS"),sQuery(id+"F0.wireOp",EDGE,"E26.MirrorCS"),sQuery(id+"F0.wireOp",EDGE,"E27.MirrorCS"),sQuery(id+"F0.wireOp",EDGE,"E28.MirrorCS"),sQuery(id+"F0.wireOp",EDGE,"E29.MirrorCS"),sQuery(id+"F0.wireOp",EDGE,"E30.MirrorCS"),sQuery(id+"F0.wireOp",EDGE,"E31.MirrorCS")])],"isStart":false})]}),makeQuery(id+"F6.opExtrude","CAP_EDGE",EDGE,{"disambiguationData":[OSD([sQuery(id+"F5.wireOp",EDGE,"E81.0")])],"isStart":true})]});}
            var Q67;
            {var subQ0=sQuery(id+"F0.wireOp",EDGE,"E15");Q67=makeQuery(id+"F6.boolean.opBoolean","MERGE",EDGE,{"derivedFrom":[makeQuery(id+"F2.opFillet","BLEND_EDGE",EDGE,{"blendedFrom":[makeQuery(id+"F1.opExtrude","CAP_EDGE",EDGE,{"disambiguationData":[OSD([subQ0])],"isStart":false}),makeQuery(id+"F1.opExtrude","CAP_FACE",FACE,{"disambiguationData":[OSD([sQuery(id+"F0.wireOp",EDGE,"E0"),sQuery(id+"F0.wireOp",EDGE,"E1.0"),sQuery(id+"F0.wireOp",EDGE,"E1.1"),sQuery(id+"F0.wireOp",EDGE,"E1.2"),sQuery(id+"F0.wireOp",EDGE,"E1.3"),sQuery(id+"F0.wireOp",EDGE,"E1.4"),sQuery(id+"F0.wireOp",EDGE,"E1.5"),sQuery(id+"F0.wireOp",EDGE,"E1.6"),sQuery(id+"F0.wireOp",EDGE,"E1.7"),sQuery(id+"F0.wireOp",EDGE,"E1.8"),sQuery(id+"F0.wireOp",EDGE,"E1.9"),sQuery(id+"F0.wireOp",EDGE,"E1.10"),sQuery(id+"F0.wireOp",EDGE,"E2"),sQuery(id+"F0.wireOp",EDGE,"E3.2.0"),sQuery(id+"F0.wireOp",EDGE,"E3.3.0"),sQuery(id+"F0.wireOp",EDGE,"E3.4.0"),sQuery(id+"F0.wireOp",EDGE,"E3.5.0"),sQuery(id+"F0.wireOp",EDGE,"E3.6.0"),sQuery(id+"F0.wireOp",EDGE,"E3.7.0"),sQuery(id+"F0.wireOp",EDGE,"E3.8.0"),sQuery(id+"F0.wireOp",EDGE,"E3.9.0"),sQuery(id+"F0.wireOp",EDGE,"E3.10.0"),sQuery(id+"F0.wireOp",EDGE,"E4"),sQuery(id+"F0.wireOp",EDGE,"E5"),sQuery(id+"F0.wireOp",EDGE,"E6"),sQuery(id+"F0.wireOp",EDGE,"E7"),sQuery(id+"F0.wireOp",EDGE,"E8"),sQuery(id+"F0.wireOp",EDGE,"E9"),sQuery(id+"F0.wireOp",EDGE,"E10"),sQuery(id+"F0.wireOp",EDGE,"E11"),sQuery(id+"F0.wireOp",EDGE,"E12"),sQuery(id+"F0.wireOp",EDGE,"E13"),sQuery(id+"F0.wireOp",EDGE,"E14"),subQ0,sQuery(id+"F0.wireOp",EDGE,"E16"),sQuery(id+"F0.wireOp",EDGE,"E17"),sQuery(id+"F0.wireOp",EDGE,"E18.MirrorCS"),sQuery(id+"F0.wireOp",EDGE,"E19.MirrorCS"),sQuery(id+"F0.wireOp",EDGE,"E20.MirrorCS"),sQuery(id+"F0.wireOp",EDGE,"E21.MirrorCS"),sQuery(id+"F0.wireOp",EDGE,"E22.MirrorCS"),sQuery(id+"F0.wireOp",EDGE,"E23.MirrorCS"),sQuery(id+"F0.wireOp",EDGE,"E24.MirrorCS"),sQuery(id+"F0.wireOp",EDGE,"E25.MirrorCS"),sQuery(id+"F0.wireOp",EDGE,"E26.MirrorCS"),sQuery(id+"F0.wireOp",EDGE,"E27.MirrorCS"),sQuery(id+"F0.wireOp",EDGE,"E28.MirrorCS"),sQuery(id+"F0.wireOp",EDGE,"E29.MirrorCS"),sQuery(id+"F0.wireOp",EDGE,"E30.MirrorCS"),sQuery(id+"F0.wireOp",EDGE,"E31.MirrorCS")])],"isStart":false})],"blendedInto":[makeQuery(id+"F1.opExtrude","CAP_FACE",FACE,{"disambiguationData":[OSD([sQuery(id+"F0.wireOp",EDGE,"E0"),sQuery(id+"F0.wireOp",EDGE,"E1.0"),sQuery(id+"F0.wireOp",EDGE,"E1.1"),sQuery(id+"F0.wireOp",EDGE,"E1.2"),sQuery(id+"F0.wireOp",EDGE,"E1.3"),sQuery(id+"F0.wireOp",EDGE,"E1.4"),sQuery(id+"F0.wireOp",EDGE,"E1.5"),sQuery(id+"F0.wireOp",EDGE,"E1.6"),sQuery(id+"F0.wireOp",EDGE,"E1.7"),sQuery(id+"F0.wireOp",EDGE,"E1.8"),sQuery(id+"F0.wireOp",EDGE,"E1.9"),sQuery(id+"F0.wireOp",EDGE,"E1.10"),sQuery(id+"F0.wireOp",EDGE,"E2"),sQuery(id+"F0.wireOp",EDGE,"E3.2.0"),sQuery(id+"F0.wireOp",EDGE,"E3.3.0"),sQuery(id+"F0.wireOp",EDGE,"E3.4.0"),sQuery(id+"F0.wireOp",EDGE,"E3.5.0"),sQuery(id+"F0.wireOp",EDGE,"E3.6.0"),sQuery(id+"F0.wireOp",EDGE,"E3.7.0"),sQuery(id+"F0.wireOp",EDGE,"E3.8.0"),sQuery(id+"F0.wireOp",EDGE,"E3.9.0"),sQuery(id+"F0.wireOp",EDGE,"E3.10.0"),sQuery(id+"F0.wireOp",EDGE,"E4"),sQuery(id+"F0.wireOp",EDGE,"E5"),sQuery(id+"F0.wireOp",EDGE,"E6"),sQuery(id+"F0.wireOp",EDGE,"E7"),sQuery(id+"F0.wireOp",EDGE,"E8"),sQuery(id+"F0.wireOp",EDGE,"E9"),sQuery(id+"F0.wireOp",EDGE,"E10"),sQuery(id+"F0.wireOp",EDGE,"E11"),sQuery(id+"F0.wireOp",EDGE,"E12"),sQuery(id+"F0.wireOp",EDGE,"E13"),sQuery(id+"F0.wireOp",EDGE,"E14"),subQ0,sQuery(id+"F0.wireOp",EDGE,"E16"),sQuery(id+"F0.wireOp",EDGE,"E17"),sQuery(id+"F0.wireOp",EDGE,"E18.MirrorCS"),sQuery(id+"F0.wireOp",EDGE,"E19.MirrorCS"),sQuery(id+"F0.wireOp",EDGE,"E20.MirrorCS"),sQuery(id+"F0.wireOp",EDGE,"E21.MirrorCS"),sQuery(id+"F0.wireOp",EDGE,"E22.MirrorCS"),sQuery(id+"F0.wireOp",EDGE,"E23.MirrorCS"),sQuery(id+"F0.wireOp",EDGE,"E24.MirrorCS"),sQuery(id+"F0.wireOp",EDGE,"E25.MirrorCS"),sQuery(id+"F0.wireOp",EDGE,"E26.MirrorCS"),sQuery(id+"F0.wireOp",EDGE,"E27.MirrorCS"),sQuery(id+"F0.wireOp",EDGE,"E28.MirrorCS"),sQuery(id+"F0.wireOp",EDGE,"E29.MirrorCS"),sQuery(id+"F0.wireOp",EDGE,"E30.MirrorCS"),sQuery(id+"F0.wireOp",EDGE,"E31.MirrorCS")])],"isStart":false})]}),makeQuery(id+"F6.opExtrude","CAP_EDGE",EDGE,{"disambiguationData":[OSD([sQuery(id+"F5.wireOp",EDGE,"E84.0")])],"isStart":true})]});}
            var Q68;
            {var subQ0=sQuery(id+"F0.wireOp",EDGE,"E14");Q68=makeQuery(id+"F6.boolean.opBoolean","MERGE",EDGE,{"derivedFrom":[makeQuery(id+"F2.opFillet","BLEND_EDGE",EDGE,{"blendedFrom":[makeQuery(id+"F1.opExtrude","CAP_EDGE",EDGE,{"disambiguationData":[OSD([subQ0])],"isStart":false}),makeQuery(id+"F1.opExtrude","CAP_FACE",FACE,{"disambiguationData":[OSD([sQuery(id+"F0.wireOp",EDGE,"E0"),sQuery(id+"F0.wireOp",EDGE,"E1.0"),sQuery(id+"F0.wireOp",EDGE,"E1.1"),sQuery(id+"F0.wireOp",EDGE,"E1.2"),sQuery(id+"F0.wireOp",EDGE,"E1.3"),sQuery(id+"F0.wireOp",EDGE,"E1.4"),sQuery(id+"F0.wireOp",EDGE,"E1.5"),sQuery(id+"F0.wireOp",EDGE,"E1.6"),sQuery(id+"F0.wireOp",EDGE,"E1.7"),sQuery(id+"F0.wireOp",EDGE,"E1.8"),sQuery(id+"F0.wireOp",EDGE,"E1.9"),sQuery(id+"F0.wireOp",EDGE,"E1.10"),sQuery(id+"F0.wireOp",EDGE,"E2"),sQuery(id+"F0.wireOp",EDGE,"E3.2.0"),sQuery(id+"F0.wireOp",EDGE,"E3.3.0"),sQuery(id+"F0.wireOp",EDGE,"E3.4.0"),sQuery(id+"F0.wireOp",EDGE,"E3.5.0"),sQuery(id+"F0.wireOp",EDGE,"E3.6.0"),sQuery(id+"F0.wireOp",EDGE,"E3.7.0"),sQuery(id+"F0.wireOp",EDGE,"E3.8.0"),sQuery(id+"F0.wireOp",EDGE,"E3.9.0"),sQuery(id+"F0.wireOp",EDGE,"E3.10.0"),sQuery(id+"F0.wireOp",EDGE,"E4"),sQuery(id+"F0.wireOp",EDGE,"E5"),sQuery(id+"F0.wireOp",EDGE,"E6"),sQuery(id+"F0.wireOp",EDGE,"E7"),sQuery(id+"F0.wireOp",EDGE,"E8"),sQuery(id+"F0.wireOp",EDGE,"E9"),sQuery(id+"F0.wireOp",EDGE,"E10"),sQuery(id+"F0.wireOp",EDGE,"E11"),sQuery(id+"F0.wireOp",EDGE,"E12"),sQuery(id+"F0.wireOp",EDGE,"E13"),subQ0,sQuery(id+"F0.wireOp",EDGE,"E15"),sQuery(id+"F0.wireOp",EDGE,"E16"),sQuery(id+"F0.wireOp",EDGE,"E17"),sQuery(id+"F0.wireOp",EDGE,"E18.MirrorCS"),sQuery(id+"F0.wireOp",EDGE,"E19.MirrorCS"),sQuery(id+"F0.wireOp",EDGE,"E20.MirrorCS"),sQuery(id+"F0.wireOp",EDGE,"E21.MirrorCS"),sQuery(id+"F0.wireOp",EDGE,"E22.MirrorCS"),sQuery(id+"F0.wireOp",EDGE,"E23.MirrorCS"),sQuery(id+"F0.wireOp",EDGE,"E24.MirrorCS"),sQuery(id+"F0.wireOp",EDGE,"E25.MirrorCS"),sQuery(id+"F0.wireOp",EDGE,"E26.MirrorCS"),sQuery(id+"F0.wireOp",EDGE,"E27.MirrorCS"),sQuery(id+"F0.wireOp",EDGE,"E28.MirrorCS"),sQuery(id+"F0.wireOp",EDGE,"E29.MirrorCS"),sQuery(id+"F0.wireOp",EDGE,"E30.MirrorCS"),sQuery(id+"F0.wireOp",EDGE,"E31.MirrorCS")])],"isStart":false})],"blendedInto":[makeQuery(id+"F1.opExtrude","CAP_FACE",FACE,{"disambiguationData":[OSD([sQuery(id+"F0.wireOp",EDGE,"E0"),sQuery(id+"F0.wireOp",EDGE,"E1.0"),sQuery(id+"F0.wireOp",EDGE,"E1.1"),sQuery(id+"F0.wireOp",EDGE,"E1.2"),sQuery(id+"F0.wireOp",EDGE,"E1.3"),sQuery(id+"F0.wireOp",EDGE,"E1.4"),sQuery(id+"F0.wireOp",EDGE,"E1.5"),sQuery(id+"F0.wireOp",EDGE,"E1.6"),sQuery(id+"F0.wireOp",EDGE,"E1.7"),sQuery(id+"F0.wireOp",EDGE,"E1.8"),sQuery(id+"F0.wireOp",EDGE,"E1.9"),sQuery(id+"F0.wireOp",EDGE,"E1.10"),sQuery(id+"F0.wireOp",EDGE,"E2"),sQuery(id+"F0.wireOp",EDGE,"E3.2.0"),sQuery(id+"F0.wireOp",EDGE,"E3.3.0"),sQuery(id+"F0.wireOp",EDGE,"E3.4.0"),sQuery(id+"F0.wireOp",EDGE,"E3.5.0"),sQuery(id+"F0.wireOp",EDGE,"E3.6.0"),sQuery(id+"F0.wireOp",EDGE,"E3.7.0"),sQuery(id+"F0.wireOp",EDGE,"E3.8.0"),sQuery(id+"F0.wireOp",EDGE,"E3.9.0"),sQuery(id+"F0.wireOp",EDGE,"E3.10.0"),sQuery(id+"F0.wireOp",EDGE,"E4"),sQuery(id+"F0.wireOp",EDGE,"E5"),sQuery(id+"F0.wireOp",EDGE,"E6"),sQuery(id+"F0.wireOp",EDGE,"E7"),sQuery(id+"F0.wireOp",EDGE,"E8"),sQuery(id+"F0.wireOp",EDGE,"E9"),sQuery(id+"F0.wireOp",EDGE,"E10"),sQuery(id+"F0.wireOp",EDGE,"E11"),sQuery(id+"F0.wireOp",EDGE,"E12"),sQuery(id+"F0.wireOp",EDGE,"E13"),subQ0,sQuery(id+"F0.wireOp",EDGE,"E15"),sQuery(id+"F0.wireOp",EDGE,"E16"),sQuery(id+"F0.wireOp",EDGE,"E17"),sQuery(id+"F0.wireOp",EDGE,"E18.MirrorCS"),sQuery(id+"F0.wireOp",EDGE,"E19.MirrorCS"),sQuery(id+"F0.wireOp",EDGE,"E20.MirrorCS"),sQuery(id+"F0.wireOp",EDGE,"E21.MirrorCS"),sQuery(id+"F0.wireOp",EDGE,"E22.MirrorCS"),sQuery(id+"F0.wireOp",EDGE,"E23.MirrorCS"),sQuery(id+"F0.wireOp",EDGE,"E24.MirrorCS"),sQuery(id+"F0.wireOp",EDGE,"E25.MirrorCS"),sQuery(id+"F0.wireOp",EDGE,"E26.MirrorCS"),sQuery(id+"F0.wireOp",EDGE,"E27.MirrorCS"),sQuery(id+"F0.wireOp",EDGE,"E28.MirrorCS"),sQuery(id+"F0.wireOp",EDGE,"E29.MirrorCS"),sQuery(id+"F0.wireOp",EDGE,"E30.MirrorCS"),sQuery(id+"F0.wireOp",EDGE,"E31.MirrorCS")])],"isStart":false})]}),makeQuery(id+"F6.opExtrude","CAP_EDGE",EDGE,{"disambiguationData":[OSD([sQuery(id+"F5.wireOp",EDGE,"E73.0")])],"isStart":true})]});}
            var Q69;
            {var subQ0=sQuery(id+"F0.wireOp",EDGE,"E13");Q69=makeQuery(id+"F6.boolean.opBoolean","MERGE",EDGE,{"derivedFrom":[makeQuery(id+"F2.opFillet","BLEND_EDGE",EDGE,{"blendedFrom":[makeQuery(id+"F1.opExtrude","CAP_EDGE",EDGE,{"disambiguationData":[OSD([subQ0])],"isStart":false}),makeQuery(id+"F1.opExtrude","CAP_FACE",FACE,{"disambiguationData":[OSD([sQuery(id+"F0.wireOp",EDGE,"E0"),sQuery(id+"F0.wireOp",EDGE,"E1.0"),sQuery(id+"F0.wireOp",EDGE,"E1.1"),sQuery(id+"F0.wireOp",EDGE,"E1.2"),sQuery(id+"F0.wireOp",EDGE,"E1.3"),sQuery(id+"F0.wireOp",EDGE,"E1.4"),sQuery(id+"F0.wireOp",EDGE,"E1.5"),sQuery(id+"F0.wireOp",EDGE,"E1.6"),sQuery(id+"F0.wireOp",EDGE,"E1.7"),sQuery(id+"F0.wireOp",EDGE,"E1.8"),sQuery(id+"F0.wireOp",EDGE,"E1.9"),sQuery(id+"F0.wireOp",EDGE,"E1.10"),sQuery(id+"F0.wireOp",EDGE,"E2"),sQuery(id+"F0.wireOp",EDGE,"E3.2.0"),sQuery(id+"F0.wireOp",EDGE,"E3.3.0"),sQuery(id+"F0.wireOp",EDGE,"E3.4.0"),sQuery(id+"F0.wireOp",EDGE,"E3.5.0"),sQuery(id+"F0.wireOp",EDGE,"E3.6.0"),sQuery(id+"F0.wireOp",EDGE,"E3.7.0"),sQuery(id+"F0.wireOp",EDGE,"E3.8.0"),sQuery(id+"F0.wireOp",EDGE,"E3.9.0"),sQuery(id+"F0.wireOp",EDGE,"E3.10.0"),sQuery(id+"F0.wireOp",EDGE,"E4"),sQuery(id+"F0.wireOp",EDGE,"E5"),sQuery(id+"F0.wireOp",EDGE,"E6"),sQuery(id+"F0.wireOp",EDGE,"E7"),sQuery(id+"F0.wireOp",EDGE,"E8"),sQuery(id+"F0.wireOp",EDGE,"E9"),sQuery(id+"F0.wireOp",EDGE,"E10"),sQuery(id+"F0.wireOp",EDGE,"E11"),sQuery(id+"F0.wireOp",EDGE,"E12"),subQ0,sQuery(id+"F0.wireOp",EDGE,"E14"),sQuery(id+"F0.wireOp",EDGE,"E15"),sQuery(id+"F0.wireOp",EDGE,"E16"),sQuery(id+"F0.wireOp",EDGE,"E17"),sQuery(id+"F0.wireOp",EDGE,"E18.MirrorCS"),sQuery(id+"F0.wireOp",EDGE,"E19.MirrorCS"),sQuery(id+"F0.wireOp",EDGE,"E20.MirrorCS"),sQuery(id+"F0.wireOp",EDGE,"E21.MirrorCS"),sQuery(id+"F0.wireOp",EDGE,"E22.MirrorCS"),sQuery(id+"F0.wireOp",EDGE,"E23.MirrorCS"),sQuery(id+"F0.wireOp",EDGE,"E24.MirrorCS"),sQuery(id+"F0.wireOp",EDGE,"E25.MirrorCS"),sQuery(id+"F0.wireOp",EDGE,"E26.MirrorCS"),sQuery(id+"F0.wireOp",EDGE,"E27.MirrorCS"),sQuery(id+"F0.wireOp",EDGE,"E28.MirrorCS"),sQuery(id+"F0.wireOp",EDGE,"E29.MirrorCS"),sQuery(id+"F0.wireOp",EDGE,"E30.MirrorCS"),sQuery(id+"F0.wireOp",EDGE,"E31.MirrorCS")])],"isStart":false})],"blendedInto":[makeQuery(id+"F1.opExtrude","CAP_FACE",FACE,{"disambiguationData":[OSD([sQuery(id+"F0.wireOp",EDGE,"E0"),sQuery(id+"F0.wireOp",EDGE,"E1.0"),sQuery(id+"F0.wireOp",EDGE,"E1.1"),sQuery(id+"F0.wireOp",EDGE,"E1.2"),sQuery(id+"F0.wireOp",EDGE,"E1.3"),sQuery(id+"F0.wireOp",EDGE,"E1.4"),sQuery(id+"F0.wireOp",EDGE,"E1.5"),sQuery(id+"F0.wireOp",EDGE,"E1.6"),sQuery(id+"F0.wireOp",EDGE,"E1.7"),sQuery(id+"F0.wireOp",EDGE,"E1.8"),sQuery(id+"F0.wireOp",EDGE,"E1.9"),sQuery(id+"F0.wireOp",EDGE,"E1.10"),sQuery(id+"F0.wireOp",EDGE,"E2"),sQuery(id+"F0.wireOp",EDGE,"E3.2.0"),sQuery(id+"F0.wireOp",EDGE,"E3.3.0"),sQuery(id+"F0.wireOp",EDGE,"E3.4.0"),sQuery(id+"F0.wireOp",EDGE,"E3.5.0"),sQuery(id+"F0.wireOp",EDGE,"E3.6.0"),sQuery(id+"F0.wireOp",EDGE,"E3.7.0"),sQuery(id+"F0.wireOp",EDGE,"E3.8.0"),sQuery(id+"F0.wireOp",EDGE,"E3.9.0"),sQuery(id+"F0.wireOp",EDGE,"E3.10.0"),sQuery(id+"F0.wireOp",EDGE,"E4"),sQuery(id+"F0.wireOp",EDGE,"E5"),sQuery(id+"F0.wireOp",EDGE,"E6"),sQuery(id+"F0.wireOp",EDGE,"E7"),sQuery(id+"F0.wireOp",EDGE,"E8"),sQuery(id+"F0.wireOp",EDGE,"E9"),sQuery(id+"F0.wireOp",EDGE,"E10"),sQuery(id+"F0.wireOp",EDGE,"E11"),sQuery(id+"F0.wireOp",EDGE,"E12"),subQ0,sQuery(id+"F0.wireOp",EDGE,"E14"),sQuery(id+"F0.wireOp",EDGE,"E15"),sQuery(id+"F0.wireOp",EDGE,"E16"),sQuery(id+"F0.wireOp",EDGE,"E17"),sQuery(id+"F0.wireOp",EDGE,"E18.MirrorCS"),sQuery(id+"F0.wireOp",EDGE,"E19.MirrorCS"),sQuery(id+"F0.wireOp",EDGE,"E20.MirrorCS"),sQuery(id+"F0.wireOp",EDGE,"E21.MirrorCS"),sQuery(id+"F0.wireOp",EDGE,"E22.MirrorCS"),sQuery(id+"F0.wireOp",EDGE,"E23.MirrorCS"),sQuery(id+"F0.wireOp",EDGE,"E24.MirrorCS"),sQuery(id+"F0.wireOp",EDGE,"E25.MirrorCS"),sQuery(id+"F0.wireOp",EDGE,"E26.MirrorCS"),sQuery(id+"F0.wireOp",EDGE,"E27.MirrorCS"),sQuery(id+"F0.wireOp",EDGE,"E28.MirrorCS"),sQuery(id+"F0.wireOp",EDGE,"E29.MirrorCS"),sQuery(id+"F0.wireOp",EDGE,"E30.MirrorCS"),sQuery(id+"F0.wireOp",EDGE,"E31.MirrorCS")])],"isStart":false})]}),makeQuery(id+"F6.opExtrude","CAP_EDGE",EDGE,{"disambiguationData":[OSD([sQuery(id+"F5.wireOp",EDGE,"E64.0")])],"isStart":true})]});}
            var Q70;
            {var subQ0=sQuery(id+"F0.wireOp",EDGE,"E7");Q70=makeQuery(id+"F6.boolean.opBoolean","MERGE",EDGE,{"derivedFrom":[makeQuery(id+"F2.opFillet","BLEND_EDGE",EDGE,{"blendedFrom":[makeQuery(id+"F1.opExtrude","CAP_EDGE",EDGE,{"disambiguationData":[OSD([subQ0])],"isStart":false}),makeQuery(id+"F1.opExtrude","CAP_FACE",FACE,{"disambiguationData":[OSD([sQuery(id+"F0.wireOp",EDGE,"E0"),sQuery(id+"F0.wireOp",EDGE,"E1.0"),sQuery(id+"F0.wireOp",EDGE,"E1.1"),sQuery(id+"F0.wireOp",EDGE,"E1.2"),sQuery(id+"F0.wireOp",EDGE,"E1.3"),sQuery(id+"F0.wireOp",EDGE,"E1.4"),sQuery(id+"F0.wireOp",EDGE,"E1.5"),sQuery(id+"F0.wireOp",EDGE,"E1.6"),sQuery(id+"F0.wireOp",EDGE,"E1.7"),sQuery(id+"F0.wireOp",EDGE,"E1.8"),sQuery(id+"F0.wireOp",EDGE,"E1.9"),sQuery(id+"F0.wireOp",EDGE,"E1.10"),sQuery(id+"F0.wireOp",EDGE,"E2"),sQuery(id+"F0.wireOp",EDGE,"E3.2.0"),sQuery(id+"F0.wireOp",EDGE,"E3.3.0"),sQuery(id+"F0.wireOp",EDGE,"E3.4.0"),sQuery(id+"F0.wireOp",EDGE,"E3.5.0"),sQuery(id+"F0.wireOp",EDGE,"E3.6.0"),sQuery(id+"F0.wireOp",EDGE,"E3.7.0"),sQuery(id+"F0.wireOp",EDGE,"E3.8.0"),sQuery(id+"F0.wireOp",EDGE,"E3.9.0"),sQuery(id+"F0.wireOp",EDGE,"E3.10.0"),sQuery(id+"F0.wireOp",EDGE,"E4"),sQuery(id+"F0.wireOp",EDGE,"E5"),sQuery(id+"F0.wireOp",EDGE,"E6"),subQ0,sQuery(id+"F0.wireOp",EDGE,"E8"),sQuery(id+"F0.wireOp",EDGE,"E9"),sQuery(id+"F0.wireOp",EDGE,"E10"),sQuery(id+"F0.wireOp",EDGE,"E11"),sQuery(id+"F0.wireOp",EDGE,"E12"),sQuery(id+"F0.wireOp",EDGE,"E13"),sQuery(id+"F0.wireOp",EDGE,"E14"),sQuery(id+"F0.wireOp",EDGE,"E15"),sQuery(id+"F0.wireOp",EDGE,"E16"),sQuery(id+"F0.wireOp",EDGE,"E17"),sQuery(id+"F0.wireOp",EDGE,"E18.MirrorCS"),sQuery(id+"F0.wireOp",EDGE,"E19.MirrorCS"),sQuery(id+"F0.wireOp",EDGE,"E20.MirrorCS"),sQuery(id+"F0.wireOp",EDGE,"E21.MirrorCS"),sQuery(id+"F0.wireOp",EDGE,"E22.MirrorCS"),sQuery(id+"F0.wireOp",EDGE,"E23.MirrorCS"),sQuery(id+"F0.wireOp",EDGE,"E24.MirrorCS"),sQuery(id+"F0.wireOp",EDGE,"E25.MirrorCS"),sQuery(id+"F0.wireOp",EDGE,"E26.MirrorCS"),sQuery(id+"F0.wireOp",EDGE,"E27.MirrorCS"),sQuery(id+"F0.wireOp",EDGE,"E28.MirrorCS"),sQuery(id+"F0.wireOp",EDGE,"E29.MirrorCS"),sQuery(id+"F0.wireOp",EDGE,"E30.MirrorCS"),sQuery(id+"F0.wireOp",EDGE,"E31.MirrorCS")])],"isStart":false})],"blendedInto":[makeQuery(id+"F1.opExtrude","CAP_FACE",FACE,{"disambiguationData":[OSD([sQuery(id+"F0.wireOp",EDGE,"E0"),sQuery(id+"F0.wireOp",EDGE,"E1.0"),sQuery(id+"F0.wireOp",EDGE,"E1.1"),sQuery(id+"F0.wireOp",EDGE,"E1.2"),sQuery(id+"F0.wireOp",EDGE,"E1.3"),sQuery(id+"F0.wireOp",EDGE,"E1.4"),sQuery(id+"F0.wireOp",EDGE,"E1.5"),sQuery(id+"F0.wireOp",EDGE,"E1.6"),sQuery(id+"F0.wireOp",EDGE,"E1.7"),sQuery(id+"F0.wireOp",EDGE,"E1.8"),sQuery(id+"F0.wireOp",EDGE,"E1.9"),sQuery(id+"F0.wireOp",EDGE,"E1.10"),sQuery(id+"F0.wireOp",EDGE,"E2"),sQuery(id+"F0.wireOp",EDGE,"E3.2.0"),sQuery(id+"F0.wireOp",EDGE,"E3.3.0"),sQuery(id+"F0.wireOp",EDGE,"E3.4.0"),sQuery(id+"F0.wireOp",EDGE,"E3.5.0"),sQuery(id+"F0.wireOp",EDGE,"E3.6.0"),sQuery(id+"F0.wireOp",EDGE,"E3.7.0"),sQuery(id+"F0.wireOp",EDGE,"E3.8.0"),sQuery(id+"F0.wireOp",EDGE,"E3.9.0"),sQuery(id+"F0.wireOp",EDGE,"E3.10.0"),sQuery(id+"F0.wireOp",EDGE,"E4"),sQuery(id+"F0.wireOp",EDGE,"E5"),sQuery(id+"F0.wireOp",EDGE,"E6"),subQ0,sQuery(id+"F0.wireOp",EDGE,"E8"),sQuery(id+"F0.wireOp",EDGE,"E9"),sQuery(id+"F0.wireOp",EDGE,"E10"),sQuery(id+"F0.wireOp",EDGE,"E11"),sQuery(id+"F0.wireOp",EDGE,"E12"),sQuery(id+"F0.wireOp",EDGE,"E13"),sQuery(id+"F0.wireOp",EDGE,"E14"),sQuery(id+"F0.wireOp",EDGE,"E15"),sQuery(id+"F0.wireOp",EDGE,"E16"),sQuery(id+"F0.wireOp",EDGE,"E17"),sQuery(id+"F0.wireOp",EDGE,"E18.MirrorCS"),sQuery(id+"F0.wireOp",EDGE,"E19.MirrorCS"),sQuery(id+"F0.wireOp",EDGE,"E20.MirrorCS"),sQuery(id+"F0.wireOp",EDGE,"E21.MirrorCS"),sQuery(id+"F0.wireOp",EDGE,"E22.MirrorCS"),sQuery(id+"F0.wireOp",EDGE,"E23.MirrorCS"),sQuery(id+"F0.wireOp",EDGE,"E24.MirrorCS"),sQuery(id+"F0.wireOp",EDGE,"E25.MirrorCS"),sQuery(id+"F0.wireOp",EDGE,"E26.MirrorCS"),sQuery(id+"F0.wireOp",EDGE,"E27.MirrorCS"),sQuery(id+"F0.wireOp",EDGE,"E28.MirrorCS"),sQuery(id+"F0.wireOp",EDGE,"E29.MirrorCS"),sQuery(id+"F0.wireOp",EDGE,"E30.MirrorCS"),sQuery(id+"F0.wireOp",EDGE,"E31.MirrorCS")])],"isStart":false})]}),makeQuery(id+"F6.opExtrude","CAP_EDGE",EDGE,{"disambiguationData":[OSD([sQuery(id+"F5.wireOp",EDGE,"E63.0")])],"isStart":true})]});}
            var Q71;
            {var subQ0=sQuery(id+"F0.wireOp",EDGE,"E8");Q71=makeQuery(id+"F6.boolean.opBoolean","MERGE",EDGE,{"derivedFrom":[makeQuery(id+"F2.opFillet","BLEND_EDGE",EDGE,{"blendedFrom":[makeQuery(id+"F1.opExtrude","CAP_EDGE",EDGE,{"disambiguationData":[OSD([subQ0])],"isStart":false}),makeQuery(id+"F1.opExtrude","CAP_FACE",FACE,{"disambiguationData":[OSD([sQuery(id+"F0.wireOp",EDGE,"E0"),sQuery(id+"F0.wireOp",EDGE,"E1.0"),sQuery(id+"F0.wireOp",EDGE,"E1.1"),sQuery(id+"F0.wireOp",EDGE,"E1.2"),sQuery(id+"F0.wireOp",EDGE,"E1.3"),sQuery(id+"F0.wireOp",EDGE,"E1.4"),sQuery(id+"F0.wireOp",EDGE,"E1.5"),sQuery(id+"F0.wireOp",EDGE,"E1.6"),sQuery(id+"F0.wireOp",EDGE,"E1.7"),sQuery(id+"F0.wireOp",EDGE,"E1.8"),sQuery(id+"F0.wireOp",EDGE,"E1.9"),sQuery(id+"F0.wireOp",EDGE,"E1.10"),sQuery(id+"F0.wireOp",EDGE,"E2"),sQuery(id+"F0.wireOp",EDGE,"E3.2.0"),sQuery(id+"F0.wireOp",EDGE,"E3.3.0"),sQuery(id+"F0.wireOp",EDGE,"E3.4.0"),sQuery(id+"F0.wireOp",EDGE,"E3.5.0"),sQuery(id+"F0.wireOp",EDGE,"E3.6.0"),sQuery(id+"F0.wireOp",EDGE,"E3.7.0"),sQuery(id+"F0.wireOp",EDGE,"E3.8.0"),sQuery(id+"F0.wireOp",EDGE,"E3.9.0"),sQuery(id+"F0.wireOp",EDGE,"E3.10.0"),sQuery(id+"F0.wireOp",EDGE,"E4"),sQuery(id+"F0.wireOp",EDGE,"E5"),sQuery(id+"F0.wireOp",EDGE,"E6"),sQuery(id+"F0.wireOp",EDGE,"E7"),subQ0,sQuery(id+"F0.wireOp",EDGE,"E9"),sQuery(id+"F0.wireOp",EDGE,"E10"),sQuery(id+"F0.wireOp",EDGE,"E11"),sQuery(id+"F0.wireOp",EDGE,"E12"),sQuery(id+"F0.wireOp",EDGE,"E13"),sQuery(id+"F0.wireOp",EDGE,"E14"),sQuery(id+"F0.wireOp",EDGE,"E15"),sQuery(id+"F0.wireOp",EDGE,"E16"),sQuery(id+"F0.wireOp",EDGE,"E17"),sQuery(id+"F0.wireOp",EDGE,"E18.MirrorCS"),sQuery(id+"F0.wireOp",EDGE,"E19.MirrorCS"),sQuery(id+"F0.wireOp",EDGE,"E20.MirrorCS"),sQuery(id+"F0.wireOp",EDGE,"E21.MirrorCS"),sQuery(id+"F0.wireOp",EDGE,"E22.MirrorCS"),sQuery(id+"F0.wireOp",EDGE,"E23.MirrorCS"),sQuery(id+"F0.wireOp",EDGE,"E24.MirrorCS"),sQuery(id+"F0.wireOp",EDGE,"E25.MirrorCS"),sQuery(id+"F0.wireOp",EDGE,"E26.MirrorCS"),sQuery(id+"F0.wireOp",EDGE,"E27.MirrorCS"),sQuery(id+"F0.wireOp",EDGE,"E28.MirrorCS"),sQuery(id+"F0.wireOp",EDGE,"E29.MirrorCS"),sQuery(id+"F0.wireOp",EDGE,"E30.MirrorCS"),sQuery(id+"F0.wireOp",EDGE,"E31.MirrorCS")])],"isStart":false})],"blendedInto":[makeQuery(id+"F1.opExtrude","CAP_FACE",FACE,{"disambiguationData":[OSD([sQuery(id+"F0.wireOp",EDGE,"E0"),sQuery(id+"F0.wireOp",EDGE,"E1.0"),sQuery(id+"F0.wireOp",EDGE,"E1.1"),sQuery(id+"F0.wireOp",EDGE,"E1.2"),sQuery(id+"F0.wireOp",EDGE,"E1.3"),sQuery(id+"F0.wireOp",EDGE,"E1.4"),sQuery(id+"F0.wireOp",EDGE,"E1.5"),sQuery(id+"F0.wireOp",EDGE,"E1.6"),sQuery(id+"F0.wireOp",EDGE,"E1.7"),sQuery(id+"F0.wireOp",EDGE,"E1.8"),sQuery(id+"F0.wireOp",EDGE,"E1.9"),sQuery(id+"F0.wireOp",EDGE,"E1.10"),sQuery(id+"F0.wireOp",EDGE,"E2"),sQuery(id+"F0.wireOp",EDGE,"E3.2.0"),sQuery(id+"F0.wireOp",EDGE,"E3.3.0"),sQuery(id+"F0.wireOp",EDGE,"E3.4.0"),sQuery(id+"F0.wireOp",EDGE,"E3.5.0"),sQuery(id+"F0.wireOp",EDGE,"E3.6.0"),sQuery(id+"F0.wireOp",EDGE,"E3.7.0"),sQuery(id+"F0.wireOp",EDGE,"E3.8.0"),sQuery(id+"F0.wireOp",EDGE,"E3.9.0"),sQuery(id+"F0.wireOp",EDGE,"E3.10.0"),sQuery(id+"F0.wireOp",EDGE,"E4"),sQuery(id+"F0.wireOp",EDGE,"E5"),sQuery(id+"F0.wireOp",EDGE,"E6"),sQuery(id+"F0.wireOp",EDGE,"E7"),subQ0,sQuery(id+"F0.wireOp",EDGE,"E9"),sQuery(id+"F0.wireOp",EDGE,"E10"),sQuery(id+"F0.wireOp",EDGE,"E11"),sQuery(id+"F0.wireOp",EDGE,"E12"),sQuery(id+"F0.wireOp",EDGE,"E13"),sQuery(id+"F0.wireOp",EDGE,"E14"),sQuery(id+"F0.wireOp",EDGE,"E15"),sQuery(id+"F0.wireOp",EDGE,"E16"),sQuery(id+"F0.wireOp",EDGE,"E17"),sQuery(id+"F0.wireOp",EDGE,"E18.MirrorCS"),sQuery(id+"F0.wireOp",EDGE,"E19.MirrorCS"),sQuery(id+"F0.wireOp",EDGE,"E20.MirrorCS"),sQuery(id+"F0.wireOp",EDGE,"E21.MirrorCS"),sQuery(id+"F0.wireOp",EDGE,"E22.MirrorCS"),sQuery(id+"F0.wireOp",EDGE,"E23.MirrorCS"),sQuery(id+"F0.wireOp",EDGE,"E24.MirrorCS"),sQuery(id+"F0.wireOp",EDGE,"E25.MirrorCS"),sQuery(id+"F0.wireOp",EDGE,"E26.MirrorCS"),sQuery(id+"F0.wireOp",EDGE,"E27.MirrorCS"),sQuery(id+"F0.wireOp",EDGE,"E28.MirrorCS"),sQuery(id+"F0.wireOp",EDGE,"E29.MirrorCS"),sQuery(id+"F0.wireOp",EDGE,"E30.MirrorCS"),sQuery(id+"F0.wireOp",EDGE,"E31.MirrorCS")])],"isStart":false})]}),makeQuery(id+"F6.opExtrude","CAP_EDGE",EDGE,{"disambiguationData":[OSD([sQuery(id+"F5.wireOp",EDGE,"E74.0")])],"isStart":true})]});}
            var Q72;
            {var subQ0=sQuery(id+"F0.wireOp",EDGE,"E9");Q72=makeQuery(id+"F6.boolean.opBoolean","MERGE",EDGE,{"derivedFrom":[makeQuery(id+"F2.opFillet","BLEND_EDGE",EDGE,{"blendedFrom":[makeQuery(id+"F1.opExtrude","CAP_EDGE",EDGE,{"disambiguationData":[OSD([subQ0])],"isStart":false}),makeQuery(id+"F1.opExtrude","CAP_FACE",FACE,{"disambiguationData":[OSD([sQuery(id+"F0.wireOp",EDGE,"E0"),sQuery(id+"F0.wireOp",EDGE,"E1.0"),sQuery(id+"F0.wireOp",EDGE,"E1.1"),sQuery(id+"F0.wireOp",EDGE,"E1.2"),sQuery(id+"F0.wireOp",EDGE,"E1.3"),sQuery(id+"F0.wireOp",EDGE,"E1.4"),sQuery(id+"F0.wireOp",EDGE,"E1.5"),sQuery(id+"F0.wireOp",EDGE,"E1.6"),sQuery(id+"F0.wireOp",EDGE,"E1.7"),sQuery(id+"F0.wireOp",EDGE,"E1.8"),sQuery(id+"F0.wireOp",EDGE,"E1.9"),sQuery(id+"F0.wireOp",EDGE,"E1.10"),sQuery(id+"F0.wireOp",EDGE,"E2"),sQuery(id+"F0.wireOp",EDGE,"E3.2.0"),sQuery(id+"F0.wireOp",EDGE,"E3.3.0"),sQuery(id+"F0.wireOp",EDGE,"E3.4.0"),sQuery(id+"F0.wireOp",EDGE,"E3.5.0"),sQuery(id+"F0.wireOp",EDGE,"E3.6.0"),sQuery(id+"F0.wireOp",EDGE,"E3.7.0"),sQuery(id+"F0.wireOp",EDGE,"E3.8.0"),sQuery(id+"F0.wireOp",EDGE,"E3.9.0"),sQuery(id+"F0.wireOp",EDGE,"E3.10.0"),sQuery(id+"F0.wireOp",EDGE,"E4"),sQuery(id+"F0.wireOp",EDGE,"E5"),sQuery(id+"F0.wireOp",EDGE,"E6"),sQuery(id+"F0.wireOp",EDGE,"E7"),sQuery(id+"F0.wireOp",EDGE,"E8"),subQ0,sQuery(id+"F0.wireOp",EDGE,"E10"),sQuery(id+"F0.wireOp",EDGE,"E11"),sQuery(id+"F0.wireOp",EDGE,"E12"),sQuery(id+"F0.wireOp",EDGE,"E13"),sQuery(id+"F0.wireOp",EDGE,"E14"),sQuery(id+"F0.wireOp",EDGE,"E15"),sQuery(id+"F0.wireOp",EDGE,"E16"),sQuery(id+"F0.wireOp",EDGE,"E17"),sQuery(id+"F0.wireOp",EDGE,"E18.MirrorCS"),sQuery(id+"F0.wireOp",EDGE,"E19.MirrorCS"),sQuery(id+"F0.wireOp",EDGE,"E20.MirrorCS"),sQuery(id+"F0.wireOp",EDGE,"E21.MirrorCS"),sQuery(id+"F0.wireOp",EDGE,"E22.MirrorCS"),sQuery(id+"F0.wireOp",EDGE,"E23.MirrorCS"),sQuery(id+"F0.wireOp",EDGE,"E24.MirrorCS"),sQuery(id+"F0.wireOp",EDGE,"E25.MirrorCS"),sQuery(id+"F0.wireOp",EDGE,"E26.MirrorCS"),sQuery(id+"F0.wireOp",EDGE,"E27.MirrorCS"),sQuery(id+"F0.wireOp",EDGE,"E28.MirrorCS"),sQuery(id+"F0.wireOp",EDGE,"E29.MirrorCS"),sQuery(id+"F0.wireOp",EDGE,"E30.MirrorCS"),sQuery(id+"F0.wireOp",EDGE,"E31.MirrorCS")])],"isStart":false})],"blendedInto":[makeQuery(id+"F1.opExtrude","CAP_FACE",FACE,{"disambiguationData":[OSD([sQuery(id+"F0.wireOp",EDGE,"E0"),sQuery(id+"F0.wireOp",EDGE,"E1.0"),sQuery(id+"F0.wireOp",EDGE,"E1.1"),sQuery(id+"F0.wireOp",EDGE,"E1.2"),sQuery(id+"F0.wireOp",EDGE,"E1.3"),sQuery(id+"F0.wireOp",EDGE,"E1.4"),sQuery(id+"F0.wireOp",EDGE,"E1.5"),sQuery(id+"F0.wireOp",EDGE,"E1.6"),sQuery(id+"F0.wireOp",EDGE,"E1.7"),sQuery(id+"F0.wireOp",EDGE,"E1.8"),sQuery(id+"F0.wireOp",EDGE,"E1.9"),sQuery(id+"F0.wireOp",EDGE,"E1.10"),sQuery(id+"F0.wireOp",EDGE,"E2"),sQuery(id+"F0.wireOp",EDGE,"E3.2.0"),sQuery(id+"F0.wireOp",EDGE,"E3.3.0"),sQuery(id+"F0.wireOp",EDGE,"E3.4.0"),sQuery(id+"F0.wireOp",EDGE,"E3.5.0"),sQuery(id+"F0.wireOp",EDGE,"E3.6.0"),sQuery(id+"F0.wireOp",EDGE,"E3.7.0"),sQuery(id+"F0.wireOp",EDGE,"E3.8.0"),sQuery(id+"F0.wireOp",EDGE,"E3.9.0"),sQuery(id+"F0.wireOp",EDGE,"E3.10.0"),sQuery(id+"F0.wireOp",EDGE,"E4"),sQuery(id+"F0.wireOp",EDGE,"E5"),sQuery(id+"F0.wireOp",EDGE,"E6"),sQuery(id+"F0.wireOp",EDGE,"E7"),sQuery(id+"F0.wireOp",EDGE,"E8"),subQ0,sQuery(id+"F0.wireOp",EDGE,"E10"),sQuery(id+"F0.wireOp",EDGE,"E11"),sQuery(id+"F0.wireOp",EDGE,"E12"),sQuery(id+"F0.wireOp",EDGE,"E13"),sQuery(id+"F0.wireOp",EDGE,"E14"),sQuery(id+"F0.wireOp",EDGE,"E15"),sQuery(id+"F0.wireOp",EDGE,"E16"),sQuery(id+"F0.wireOp",EDGE,"E17"),sQuery(id+"F0.wireOp",EDGE,"E18.MirrorCS"),sQuery(id+"F0.wireOp",EDGE,"E19.MirrorCS"),sQuery(id+"F0.wireOp",EDGE,"E20.MirrorCS"),sQuery(id+"F0.wireOp",EDGE,"E21.MirrorCS"),sQuery(id+"F0.wireOp",EDGE,"E22.MirrorCS"),sQuery(id+"F0.wireOp",EDGE,"E23.MirrorCS"),sQuery(id+"F0.wireOp",EDGE,"E24.MirrorCS"),sQuery(id+"F0.wireOp",EDGE,"E25.MirrorCS"),sQuery(id+"F0.wireOp",EDGE,"E26.MirrorCS"),sQuery(id+"F0.wireOp",EDGE,"E27.MirrorCS"),sQuery(id+"F0.wireOp",EDGE,"E28.MirrorCS"),sQuery(id+"F0.wireOp",EDGE,"E29.MirrorCS"),sQuery(id+"F0.wireOp",EDGE,"E30.MirrorCS"),sQuery(id+"F0.wireOp",EDGE,"E31.MirrorCS")])],"isStart":false})]}),makeQuery(id+"F6.opExtrude","CAP_EDGE",EDGE,{"disambiguationData":[OSD([sQuery(id+"F5.wireOp",EDGE,"E76.0")])],"isStart":true})]});}
            var Q73;
            {var subQ0=sQuery(id+"F0.wireOp",EDGE,"E10");Q73=makeQuery(id+"F6.boolean.opBoolean","MERGE",EDGE,{"derivedFrom":[makeQuery(id+"F2.opFillet","BLEND_EDGE",EDGE,{"blendedFrom":[makeQuery(id+"F1.opExtrude","CAP_EDGE",EDGE,{"disambiguationData":[OSD([subQ0])],"isStart":false}),makeQuery(id+"F1.opExtrude","CAP_FACE",FACE,{"disambiguationData":[OSD([sQuery(id+"F0.wireOp",EDGE,"E0"),sQuery(id+"F0.wireOp",EDGE,"E1.0"),sQuery(id+"F0.wireOp",EDGE,"E1.1"),sQuery(id+"F0.wireOp",EDGE,"E1.2"),sQuery(id+"F0.wireOp",EDGE,"E1.3"),sQuery(id+"F0.wireOp",EDGE,"E1.4"),sQuery(id+"F0.wireOp",EDGE,"E1.5"),sQuery(id+"F0.wireOp",EDGE,"E1.6"),sQuery(id+"F0.wireOp",EDGE,"E1.7"),sQuery(id+"F0.wireOp",EDGE,"E1.8"),sQuery(id+"F0.wireOp",EDGE,"E1.9"),sQuery(id+"F0.wireOp",EDGE,"E1.10"),sQuery(id+"F0.wireOp",EDGE,"E2"),sQuery(id+"F0.wireOp",EDGE,"E3.2.0"),sQuery(id+"F0.wireOp",EDGE,"E3.3.0"),sQuery(id+"F0.wireOp",EDGE,"E3.4.0"),sQuery(id+"F0.wireOp",EDGE,"E3.5.0"),sQuery(id+"F0.wireOp",EDGE,"E3.6.0"),sQuery(id+"F0.wireOp",EDGE,"E3.7.0"),sQuery(id+"F0.wireOp",EDGE,"E3.8.0"),sQuery(id+"F0.wireOp",EDGE,"E3.9.0"),sQuery(id+"F0.wireOp",EDGE,"E3.10.0"),sQuery(id+"F0.wireOp",EDGE,"E4"),sQuery(id+"F0.wireOp",EDGE,"E5"),sQuery(id+"F0.wireOp",EDGE,"E6"),sQuery(id+"F0.wireOp",EDGE,"E7"),sQuery(id+"F0.wireOp",EDGE,"E8"),sQuery(id+"F0.wireOp",EDGE,"E9"),subQ0,sQuery(id+"F0.wireOp",EDGE,"E11"),sQuery(id+"F0.wireOp",EDGE,"E12"),sQuery(id+"F0.wireOp",EDGE,"E13"),sQuery(id+"F0.wireOp",EDGE,"E14"),sQuery(id+"F0.wireOp",EDGE,"E15"),sQuery(id+"F0.wireOp",EDGE,"E16"),sQuery(id+"F0.wireOp",EDGE,"E17"),sQuery(id+"F0.wireOp",EDGE,"E18.MirrorCS"),sQuery(id+"F0.wireOp",EDGE,"E19.MirrorCS"),sQuery(id+"F0.wireOp",EDGE,"E20.MirrorCS"),sQuery(id+"F0.wireOp",EDGE,"E21.MirrorCS"),sQuery(id+"F0.wireOp",EDGE,"E22.MirrorCS"),sQuery(id+"F0.wireOp",EDGE,"E23.MirrorCS"),sQuery(id+"F0.wireOp",EDGE,"E24.MirrorCS"),sQuery(id+"F0.wireOp",EDGE,"E25.MirrorCS"),sQuery(id+"F0.wireOp",EDGE,"E26.MirrorCS"),sQuery(id+"F0.wireOp",EDGE,"E27.MirrorCS"),sQuery(id+"F0.wireOp",EDGE,"E28.MirrorCS"),sQuery(id+"F0.wireOp",EDGE,"E29.MirrorCS"),sQuery(id+"F0.wireOp",EDGE,"E30.MirrorCS"),sQuery(id+"F0.wireOp",EDGE,"E31.MirrorCS")])],"isStart":false})],"blendedInto":[makeQuery(id+"F1.opExtrude","CAP_FACE",FACE,{"disambiguationData":[OSD([sQuery(id+"F0.wireOp",EDGE,"E0"),sQuery(id+"F0.wireOp",EDGE,"E1.0"),sQuery(id+"F0.wireOp",EDGE,"E1.1"),sQuery(id+"F0.wireOp",EDGE,"E1.2"),sQuery(id+"F0.wireOp",EDGE,"E1.3"),sQuery(id+"F0.wireOp",EDGE,"E1.4"),sQuery(id+"F0.wireOp",EDGE,"E1.5"),sQuery(id+"F0.wireOp",EDGE,"E1.6"),sQuery(id+"F0.wireOp",EDGE,"E1.7"),sQuery(id+"F0.wireOp",EDGE,"E1.8"),sQuery(id+"F0.wireOp",EDGE,"E1.9"),sQuery(id+"F0.wireOp",EDGE,"E1.10"),sQuery(id+"F0.wireOp",EDGE,"E2"),sQuery(id+"F0.wireOp",EDGE,"E3.2.0"),sQuery(id+"F0.wireOp",EDGE,"E3.3.0"),sQuery(id+"F0.wireOp",EDGE,"E3.4.0"),sQuery(id+"F0.wireOp",EDGE,"E3.5.0"),sQuery(id+"F0.wireOp",EDGE,"E3.6.0"),sQuery(id+"F0.wireOp",EDGE,"E3.7.0"),sQuery(id+"F0.wireOp",EDGE,"E3.8.0"),sQuery(id+"F0.wireOp",EDGE,"E3.9.0"),sQuery(id+"F0.wireOp",EDGE,"E3.10.0"),sQuery(id+"F0.wireOp",EDGE,"E4"),sQuery(id+"F0.wireOp",EDGE,"E5"),sQuery(id+"F0.wireOp",EDGE,"E6"),sQuery(id+"F0.wireOp",EDGE,"E7"),sQuery(id+"F0.wireOp",EDGE,"E8"),sQuery(id+"F0.wireOp",EDGE,"E9"),subQ0,sQuery(id+"F0.wireOp",EDGE,"E11"),sQuery(id+"F0.wireOp",EDGE,"E12"),sQuery(id+"F0.wireOp",EDGE,"E13"),sQuery(id+"F0.wireOp",EDGE,"E14"),sQuery(id+"F0.wireOp",EDGE,"E15"),sQuery(id+"F0.wireOp",EDGE,"E16"),sQuery(id+"F0.wireOp",EDGE,"E17"),sQuery(id+"F0.wireOp",EDGE,"E18.MirrorCS"),sQuery(id+"F0.wireOp",EDGE,"E19.MirrorCS"),sQuery(id+"F0.wireOp",EDGE,"E20.MirrorCS"),sQuery(id+"F0.wireOp",EDGE,"E21.MirrorCS"),sQuery(id+"F0.wireOp",EDGE,"E22.MirrorCS"),sQuery(id+"F0.wireOp",EDGE,"E23.MirrorCS"),sQuery(id+"F0.wireOp",EDGE,"E24.MirrorCS"),sQuery(id+"F0.wireOp",EDGE,"E25.MirrorCS"),sQuery(id+"F0.wireOp",EDGE,"E26.MirrorCS"),sQuery(id+"F0.wireOp",EDGE,"E27.MirrorCS"),sQuery(id+"F0.wireOp",EDGE,"E28.MirrorCS"),sQuery(id+"F0.wireOp",EDGE,"E29.MirrorCS"),sQuery(id+"F0.wireOp",EDGE,"E30.MirrorCS"),sQuery(id+"F0.wireOp",EDGE,"E31.MirrorCS")])],"isStart":false})]}),makeQuery(id+"F6.opExtrude","CAP_EDGE",EDGE,{"disambiguationData":[OSD([sQuery(id+"F5.wireOp",EDGE,"E83.0.0")])],"isStart":true})]});}
            var Q74;
            {var subQ0=sQuery(id+"F0.wireOp",EDGE,"E11");Q74=makeQuery(id+"F6.boolean.opBoolean","MERGE",EDGE,{"derivedFrom":[makeQuery(id+"F2.opFillet","BLEND_EDGE",EDGE,{"blendedFrom":[makeQuery(id+"F1.opExtrude","CAP_EDGE",EDGE,{"disambiguationData":[OSD([subQ0])],"isStart":false}),makeQuery(id+"F1.opExtrude","CAP_FACE",FACE,{"disambiguationData":[OSD([sQuery(id+"F0.wireOp",EDGE,"E0"),sQuery(id+"F0.wireOp",EDGE,"E1.0"),sQuery(id+"F0.wireOp",EDGE,"E1.1"),sQuery(id+"F0.wireOp",EDGE,"E1.2"),sQuery(id+"F0.wireOp",EDGE,"E1.3"),sQuery(id+"F0.wireOp",EDGE,"E1.4"),sQuery(id+"F0.wireOp",EDGE,"E1.5"),sQuery(id+"F0.wireOp",EDGE,"E1.6"),sQuery(id+"F0.wireOp",EDGE,"E1.7"),sQuery(id+"F0.wireOp",EDGE,"E1.8"),sQuery(id+"F0.wireOp",EDGE,"E1.9"),sQuery(id+"F0.wireOp",EDGE,"E1.10"),sQuery(id+"F0.wireOp",EDGE,"E2"),sQuery(id+"F0.wireOp",EDGE,"E3.2.0"),sQuery(id+"F0.wireOp",EDGE,"E3.3.0"),sQuery(id+"F0.wireOp",EDGE,"E3.4.0"),sQuery(id+"F0.wireOp",EDGE,"E3.5.0"),sQuery(id+"F0.wireOp",EDGE,"E3.6.0"),sQuery(id+"F0.wireOp",EDGE,"E3.7.0"),sQuery(id+"F0.wireOp",EDGE,"E3.8.0"),sQuery(id+"F0.wireOp",EDGE,"E3.9.0"),sQuery(id+"F0.wireOp",EDGE,"E3.10.0"),sQuery(id+"F0.wireOp",EDGE,"E4"),sQuery(id+"F0.wireOp",EDGE,"E5"),sQuery(id+"F0.wireOp",EDGE,"E6"),sQuery(id+"F0.wireOp",EDGE,"E7"),sQuery(id+"F0.wireOp",EDGE,"E8"),sQuery(id+"F0.wireOp",EDGE,"E9"),sQuery(id+"F0.wireOp",EDGE,"E10"),subQ0,sQuery(id+"F0.wireOp",EDGE,"E12"),sQuery(id+"F0.wireOp",EDGE,"E13"),sQuery(id+"F0.wireOp",EDGE,"E14"),sQuery(id+"F0.wireOp",EDGE,"E15"),sQuery(id+"F0.wireOp",EDGE,"E16"),sQuery(id+"F0.wireOp",EDGE,"E17"),sQuery(id+"F0.wireOp",EDGE,"E18.MirrorCS"),sQuery(id+"F0.wireOp",EDGE,"E19.MirrorCS"),sQuery(id+"F0.wireOp",EDGE,"E20.MirrorCS"),sQuery(id+"F0.wireOp",EDGE,"E21.MirrorCS"),sQuery(id+"F0.wireOp",EDGE,"E22.MirrorCS"),sQuery(id+"F0.wireOp",EDGE,"E23.MirrorCS"),sQuery(id+"F0.wireOp",EDGE,"E24.MirrorCS"),sQuery(id+"F0.wireOp",EDGE,"E25.MirrorCS"),sQuery(id+"F0.wireOp",EDGE,"E26.MirrorCS"),sQuery(id+"F0.wireOp",EDGE,"E27.MirrorCS"),sQuery(id+"F0.wireOp",EDGE,"E28.MirrorCS"),sQuery(id+"F0.wireOp",EDGE,"E29.MirrorCS"),sQuery(id+"F0.wireOp",EDGE,"E30.MirrorCS"),sQuery(id+"F0.wireOp",EDGE,"E31.MirrorCS")])],"isStart":false})],"blendedInto":[makeQuery(id+"F1.opExtrude","CAP_FACE",FACE,{"disambiguationData":[OSD([sQuery(id+"F0.wireOp",EDGE,"E0"),sQuery(id+"F0.wireOp",EDGE,"E1.0"),sQuery(id+"F0.wireOp",EDGE,"E1.1"),sQuery(id+"F0.wireOp",EDGE,"E1.2"),sQuery(id+"F0.wireOp",EDGE,"E1.3"),sQuery(id+"F0.wireOp",EDGE,"E1.4"),sQuery(id+"F0.wireOp",EDGE,"E1.5"),sQuery(id+"F0.wireOp",EDGE,"E1.6"),sQuery(id+"F0.wireOp",EDGE,"E1.7"),sQuery(id+"F0.wireOp",EDGE,"E1.8"),sQuery(id+"F0.wireOp",EDGE,"E1.9"),sQuery(id+"F0.wireOp",EDGE,"E1.10"),sQuery(id+"F0.wireOp",EDGE,"E2"),sQuery(id+"F0.wireOp",EDGE,"E3.2.0"),sQuery(id+"F0.wireOp",EDGE,"E3.3.0"),sQuery(id+"F0.wireOp",EDGE,"E3.4.0"),sQuery(id+"F0.wireOp",EDGE,"E3.5.0"),sQuery(id+"F0.wireOp",EDGE,"E3.6.0"),sQuery(id+"F0.wireOp",EDGE,"E3.7.0"),sQuery(id+"F0.wireOp",EDGE,"E3.8.0"),sQuery(id+"F0.wireOp",EDGE,"E3.9.0"),sQuery(id+"F0.wireOp",EDGE,"E3.10.0"),sQuery(id+"F0.wireOp",EDGE,"E4"),sQuery(id+"F0.wireOp",EDGE,"E5"),sQuery(id+"F0.wireOp",EDGE,"E6"),sQuery(id+"F0.wireOp",EDGE,"E7"),sQuery(id+"F0.wireOp",EDGE,"E8"),sQuery(id+"F0.wireOp",EDGE,"E9"),sQuery(id+"F0.wireOp",EDGE,"E10"),subQ0,sQuery(id+"F0.wireOp",EDGE,"E12"),sQuery(id+"F0.wireOp",EDGE,"E13"),sQuery(id+"F0.wireOp",EDGE,"E14"),sQuery(id+"F0.wireOp",EDGE,"E15"),sQuery(id+"F0.wireOp",EDGE,"E16"),sQuery(id+"F0.wireOp",EDGE,"E17"),sQuery(id+"F0.wireOp",EDGE,"E18.MirrorCS"),sQuery(id+"F0.wireOp",EDGE,"E19.MirrorCS"),sQuery(id+"F0.wireOp",EDGE,"E20.MirrorCS"),sQuery(id+"F0.wireOp",EDGE,"E21.MirrorCS"),sQuery(id+"F0.wireOp",EDGE,"E22.MirrorCS"),sQuery(id+"F0.wireOp",EDGE,"E23.MirrorCS"),sQuery(id+"F0.wireOp",EDGE,"E24.MirrorCS"),sQuery(id+"F0.wireOp",EDGE,"E25.MirrorCS"),sQuery(id+"F0.wireOp",EDGE,"E26.MirrorCS"),sQuery(id+"F0.wireOp",EDGE,"E27.MirrorCS"),sQuery(id+"F0.wireOp",EDGE,"E28.MirrorCS"),sQuery(id+"F0.wireOp",EDGE,"E29.MirrorCS"),sQuery(id+"F0.wireOp",EDGE,"E30.MirrorCS"),sQuery(id+"F0.wireOp",EDGE,"E31.MirrorCS")])],"isStart":false})]}),makeQuery(id+"F6.opExtrude","CAP_EDGE",EDGE,{"disambiguationData":[OSD([sQuery(id+"F5.wireOp",EDGE,"E77.0")])],"isStart":true})]});}
            var Q75;
            {var subQ0=sQuery(id+"F0.wireOp",EDGE,"E12");Q75=makeQuery(id+"F6.boolean.opBoolean","MERGE",EDGE,{"derivedFrom":[makeQuery(id+"F2.opFillet","BLEND_EDGE",EDGE,{"blendedFrom":[makeQuery(id+"F1.opExtrude","CAP_EDGE",EDGE,{"disambiguationData":[OSD([subQ0])],"isStart":false}),makeQuery(id+"F1.opExtrude","CAP_FACE",FACE,{"disambiguationData":[OSD([sQuery(id+"F0.wireOp",EDGE,"E0"),sQuery(id+"F0.wireOp",EDGE,"E1.0"),sQuery(id+"F0.wireOp",EDGE,"E1.1"),sQuery(id+"F0.wireOp",EDGE,"E1.2"),sQuery(id+"F0.wireOp",EDGE,"E1.3"),sQuery(id+"F0.wireOp",EDGE,"E1.4"),sQuery(id+"F0.wireOp",EDGE,"E1.5"),sQuery(id+"F0.wireOp",EDGE,"E1.6"),sQuery(id+"F0.wireOp",EDGE,"E1.7"),sQuery(id+"F0.wireOp",EDGE,"E1.8"),sQuery(id+"F0.wireOp",EDGE,"E1.9"),sQuery(id+"F0.wireOp",EDGE,"E1.10"),sQuery(id+"F0.wireOp",EDGE,"E2"),sQuery(id+"F0.wireOp",EDGE,"E3.2.0"),sQuery(id+"F0.wireOp",EDGE,"E3.3.0"),sQuery(id+"F0.wireOp",EDGE,"E3.4.0"),sQuery(id+"F0.wireOp",EDGE,"E3.5.0"),sQuery(id+"F0.wireOp",EDGE,"E3.6.0"),sQuery(id+"F0.wireOp",EDGE,"E3.7.0"),sQuery(id+"F0.wireOp",EDGE,"E3.8.0"),sQuery(id+"F0.wireOp",EDGE,"E3.9.0"),sQuery(id+"F0.wireOp",EDGE,"E3.10.0"),sQuery(id+"F0.wireOp",EDGE,"E4"),sQuery(id+"F0.wireOp",EDGE,"E5"),sQuery(id+"F0.wireOp",EDGE,"E6"),sQuery(id+"F0.wireOp",EDGE,"E7"),sQuery(id+"F0.wireOp",EDGE,"E8"),sQuery(id+"F0.wireOp",EDGE,"E9"),sQuery(id+"F0.wireOp",EDGE,"E10"),sQuery(id+"F0.wireOp",EDGE,"E11"),subQ0,sQuery(id+"F0.wireOp",EDGE,"E13"),sQuery(id+"F0.wireOp",EDGE,"E14"),sQuery(id+"F0.wireOp",EDGE,"E15"),sQuery(id+"F0.wireOp",EDGE,"E16"),sQuery(id+"F0.wireOp",EDGE,"E17"),sQuery(id+"F0.wireOp",EDGE,"E18.MirrorCS"),sQuery(id+"F0.wireOp",EDGE,"E19.MirrorCS"),sQuery(id+"F0.wireOp",EDGE,"E20.MirrorCS"),sQuery(id+"F0.wireOp",EDGE,"E21.MirrorCS"),sQuery(id+"F0.wireOp",EDGE,"E22.MirrorCS"),sQuery(id+"F0.wireOp",EDGE,"E23.MirrorCS"),sQuery(id+"F0.wireOp",EDGE,"E24.MirrorCS"),sQuery(id+"F0.wireOp",EDGE,"E25.MirrorCS"),sQuery(id+"F0.wireOp",EDGE,"E26.MirrorCS"),sQuery(id+"F0.wireOp",EDGE,"E27.MirrorCS"),sQuery(id+"F0.wireOp",EDGE,"E28.MirrorCS"),sQuery(id+"F0.wireOp",EDGE,"E29.MirrorCS"),sQuery(id+"F0.wireOp",EDGE,"E30.MirrorCS"),sQuery(id+"F0.wireOp",EDGE,"E31.MirrorCS")])],"isStart":false})],"blendedInto":[makeQuery(id+"F1.opExtrude","CAP_FACE",FACE,{"disambiguationData":[OSD([sQuery(id+"F0.wireOp",EDGE,"E0"),sQuery(id+"F0.wireOp",EDGE,"E1.0"),sQuery(id+"F0.wireOp",EDGE,"E1.1"),sQuery(id+"F0.wireOp",EDGE,"E1.2"),sQuery(id+"F0.wireOp",EDGE,"E1.3"),sQuery(id+"F0.wireOp",EDGE,"E1.4"),sQuery(id+"F0.wireOp",EDGE,"E1.5"),sQuery(id+"F0.wireOp",EDGE,"E1.6"),sQuery(id+"F0.wireOp",EDGE,"E1.7"),sQuery(id+"F0.wireOp",EDGE,"E1.8"),sQuery(id+"F0.wireOp",EDGE,"E1.9"),sQuery(id+"F0.wireOp",EDGE,"E1.10"),sQuery(id+"F0.wireOp",EDGE,"E2"),sQuery(id+"F0.wireOp",EDGE,"E3.2.0"),sQuery(id+"F0.wireOp",EDGE,"E3.3.0"),sQuery(id+"F0.wireOp",EDGE,"E3.4.0"),sQuery(id+"F0.wireOp",EDGE,"E3.5.0"),sQuery(id+"F0.wireOp",EDGE,"E3.6.0"),sQuery(id+"F0.wireOp",EDGE,"E3.7.0"),sQuery(id+"F0.wireOp",EDGE,"E3.8.0"),sQuery(id+"F0.wireOp",EDGE,"E3.9.0"),sQuery(id+"F0.wireOp",EDGE,"E3.10.0"),sQuery(id+"F0.wireOp",EDGE,"E4"),sQuery(id+"F0.wireOp",EDGE,"E5"),sQuery(id+"F0.wireOp",EDGE,"E6"),sQuery(id+"F0.wireOp",EDGE,"E7"),sQuery(id+"F0.wireOp",EDGE,"E8"),sQuery(id+"F0.wireOp",EDGE,"E9"),sQuery(id+"F0.wireOp",EDGE,"E10"),sQuery(id+"F0.wireOp",EDGE,"E11"),subQ0,sQuery(id+"F0.wireOp",EDGE,"E13"),sQuery(id+"F0.wireOp",EDGE,"E14"),sQuery(id+"F0.wireOp",EDGE,"E15"),sQuery(id+"F0.wireOp",EDGE,"E16"),sQuery(id+"F0.wireOp",EDGE,"E17"),sQuery(id+"F0.wireOp",EDGE,"E18.MirrorCS"),sQuery(id+"F0.wireOp",EDGE,"E19.MirrorCS"),sQuery(id+"F0.wireOp",EDGE,"E20.MirrorCS"),sQuery(id+"F0.wireOp",EDGE,"E21.MirrorCS"),sQuery(id+"F0.wireOp",EDGE,"E22.MirrorCS"),sQuery(id+"F0.wireOp",EDGE,"E23.MirrorCS"),sQuery(id+"F0.wireOp",EDGE,"E24.MirrorCS"),sQuery(id+"F0.wireOp",EDGE,"E25.MirrorCS"),sQuery(id+"F0.wireOp",EDGE,"E26.MirrorCS"),sQuery(id+"F0.wireOp",EDGE,"E27.MirrorCS"),sQuery(id+"F0.wireOp",EDGE,"E28.MirrorCS"),sQuery(id+"F0.wireOp",EDGE,"E29.MirrorCS"),sQuery(id+"F0.wireOp",EDGE,"E30.MirrorCS"),sQuery(id+"F0.wireOp",EDGE,"E31.MirrorCS")])],"isStart":false})]}),makeQuery(id+"F6.opExtrude","CAP_EDGE",EDGE,{"disambiguationData":[OSD([sQuery(id+"F5.wireOp",EDGE,"E78.0")])],"isStart":true})]});}
            var Q76;
            {var subQ0=sQuery(id+"F0.wireOp",EDGE,"E6");Q76=makeQuery(id+"F6.boolean.opBoolean","MERGE",EDGE,{"derivedFrom":[makeQuery(id+"F2.opFillet","BLEND_EDGE",EDGE,{"blendedFrom":[makeQuery(id+"F1.opExtrude","CAP_EDGE",EDGE,{"disambiguationData":[OSD([subQ0])],"isStart":false}),makeQuery(id+"F1.opExtrude","CAP_FACE",FACE,{"disambiguationData":[OSD([sQuery(id+"F0.wireOp",EDGE,"E0"),sQuery(id+"F0.wireOp",EDGE,"E1.0"),sQuery(id+"F0.wireOp",EDGE,"E1.1"),sQuery(id+"F0.wireOp",EDGE,"E1.2"),sQuery(id+"F0.wireOp",EDGE,"E1.3"),sQuery(id+"F0.wireOp",EDGE,"E1.4"),sQuery(id+"F0.wireOp",EDGE,"E1.5"),sQuery(id+"F0.wireOp",EDGE,"E1.6"),sQuery(id+"F0.wireOp",EDGE,"E1.7"),sQuery(id+"F0.wireOp",EDGE,"E1.8"),sQuery(id+"F0.wireOp",EDGE,"E1.9"),sQuery(id+"F0.wireOp",EDGE,"E1.10"),sQuery(id+"F0.wireOp",EDGE,"E2"),sQuery(id+"F0.wireOp",EDGE,"E3.2.0"),sQuery(id+"F0.wireOp",EDGE,"E3.3.0"),sQuery(id+"F0.wireOp",EDGE,"E3.4.0"),sQuery(id+"F0.wireOp",EDGE,"E3.5.0"),sQuery(id+"F0.wireOp",EDGE,"E3.6.0"),sQuery(id+"F0.wireOp",EDGE,"E3.7.0"),sQuery(id+"F0.wireOp",EDGE,"E3.8.0"),sQuery(id+"F0.wireOp",EDGE,"E3.9.0"),sQuery(id+"F0.wireOp",EDGE,"E3.10.0"),sQuery(id+"F0.wireOp",EDGE,"E4"),sQuery(id+"F0.wireOp",EDGE,"E5"),subQ0,sQuery(id+"F0.wireOp",EDGE,"E7"),sQuery(id+"F0.wireOp",EDGE,"E8"),sQuery(id+"F0.wireOp",EDGE,"E9"),sQuery(id+"F0.wireOp",EDGE,"E10"),sQuery(id+"F0.wireOp",EDGE,"E11"),sQuery(id+"F0.wireOp",EDGE,"E12"),sQuery(id+"F0.wireOp",EDGE,"E13"),sQuery(id+"F0.wireOp",EDGE,"E14"),sQuery(id+"F0.wireOp",EDGE,"E15"),sQuery(id+"F0.wireOp",EDGE,"E16"),sQuery(id+"F0.wireOp",EDGE,"E17"),sQuery(id+"F0.wireOp",EDGE,"E18.MirrorCS"),sQuery(id+"F0.wireOp",EDGE,"E19.MirrorCS"),sQuery(id+"F0.wireOp",EDGE,"E20.MirrorCS"),sQuery(id+"F0.wireOp",EDGE,"E21.MirrorCS"),sQuery(id+"F0.wireOp",EDGE,"E22.MirrorCS"),sQuery(id+"F0.wireOp",EDGE,"E23.MirrorCS"),sQuery(id+"F0.wireOp",EDGE,"E24.MirrorCS"),sQuery(id+"F0.wireOp",EDGE,"E25.MirrorCS"),sQuery(id+"F0.wireOp",EDGE,"E26.MirrorCS"),sQuery(id+"F0.wireOp",EDGE,"E27.MirrorCS"),sQuery(id+"F0.wireOp",EDGE,"E28.MirrorCS"),sQuery(id+"F0.wireOp",EDGE,"E29.MirrorCS"),sQuery(id+"F0.wireOp",EDGE,"E30.MirrorCS"),sQuery(id+"F0.wireOp",EDGE,"E31.MirrorCS")])],"isStart":false})],"blendedInto":[makeQuery(id+"F1.opExtrude","CAP_FACE",FACE,{"disambiguationData":[OSD([sQuery(id+"F0.wireOp",EDGE,"E0"),sQuery(id+"F0.wireOp",EDGE,"E1.0"),sQuery(id+"F0.wireOp",EDGE,"E1.1"),sQuery(id+"F0.wireOp",EDGE,"E1.2"),sQuery(id+"F0.wireOp",EDGE,"E1.3"),sQuery(id+"F0.wireOp",EDGE,"E1.4"),sQuery(id+"F0.wireOp",EDGE,"E1.5"),sQuery(id+"F0.wireOp",EDGE,"E1.6"),sQuery(id+"F0.wireOp",EDGE,"E1.7"),sQuery(id+"F0.wireOp",EDGE,"E1.8"),sQuery(id+"F0.wireOp",EDGE,"E1.9"),sQuery(id+"F0.wireOp",EDGE,"E1.10"),sQuery(id+"F0.wireOp",EDGE,"E2"),sQuery(id+"F0.wireOp",EDGE,"E3.2.0"),sQuery(id+"F0.wireOp",EDGE,"E3.3.0"),sQuery(id+"F0.wireOp",EDGE,"E3.4.0"),sQuery(id+"F0.wireOp",EDGE,"E3.5.0"),sQuery(id+"F0.wireOp",EDGE,"E3.6.0"),sQuery(id+"F0.wireOp",EDGE,"E3.7.0"),sQuery(id+"F0.wireOp",EDGE,"E3.8.0"),sQuery(id+"F0.wireOp",EDGE,"E3.9.0"),sQuery(id+"F0.wireOp",EDGE,"E3.10.0"),sQuery(id+"F0.wireOp",EDGE,"E4"),sQuery(id+"F0.wireOp",EDGE,"E5"),subQ0,sQuery(id+"F0.wireOp",EDGE,"E7"),sQuery(id+"F0.wireOp",EDGE,"E8"),sQuery(id+"F0.wireOp",EDGE,"E9"),sQuery(id+"F0.wireOp",EDGE,"E10"),sQuery(id+"F0.wireOp",EDGE,"E11"),sQuery(id+"F0.wireOp",EDGE,"E12"),sQuery(id+"F0.wireOp",EDGE,"E13"),sQuery(id+"F0.wireOp",EDGE,"E14"),sQuery(id+"F0.wireOp",EDGE,"E15"),sQuery(id+"F0.wireOp",EDGE,"E16"),sQuery(id+"F0.wireOp",EDGE,"E17"),sQuery(id+"F0.wireOp",EDGE,"E18.MirrorCS"),sQuery(id+"F0.wireOp",EDGE,"E19.MirrorCS"),sQuery(id+"F0.wireOp",EDGE,"E20.MirrorCS"),sQuery(id+"F0.wireOp",EDGE,"E21.MirrorCS"),sQuery(id+"F0.wireOp",EDGE,"E22.MirrorCS"),sQuery(id+"F0.wireOp",EDGE,"E23.MirrorCS"),sQuery(id+"F0.wireOp",EDGE,"E24.MirrorCS"),sQuery(id+"F0.wireOp",EDGE,"E25.MirrorCS"),sQuery(id+"F0.wireOp",EDGE,"E26.MirrorCS"),sQuery(id+"F0.wireOp",EDGE,"E27.MirrorCS"),sQuery(id+"F0.wireOp",EDGE,"E28.MirrorCS"),sQuery(id+"F0.wireOp",EDGE,"E29.MirrorCS"),sQuery(id+"F0.wireOp",EDGE,"E30.MirrorCS"),sQuery(id+"F0.wireOp",EDGE,"E31.MirrorCS")])],"isStart":false})]}),makeQuery(id+"F6.opExtrude","CAP_EDGE",EDGE,{"disambiguationData":[OSD([sQuery(id+"F5.wireOp",EDGE,"E39.0")])],"isStart":true})]});}
            var Q77;
            {var subQ0=sQuery(id+"F0.wireOp",EDGE,"E16");Q77=makeQuery(id+"F6.boolean.opBoolean","MERGE",EDGE,{"derivedFrom":[makeQuery(id+"F2.opFillet","BLEND_EDGE",EDGE,{"blendedFrom":[makeQuery(id+"F1.opExtrude","CAP_EDGE",EDGE,{"disambiguationData":[OSD([subQ0])],"isStart":false}),makeQuery(id+"F1.opExtrude","CAP_FACE",FACE,{"disambiguationData":[OSD([sQuery(id+"F0.wireOp",EDGE,"E0"),sQuery(id+"F0.wireOp",EDGE,"E1.0"),sQuery(id+"F0.wireOp",EDGE,"E1.1"),sQuery(id+"F0.wireOp",EDGE,"E1.2"),sQuery(id+"F0.wireOp",EDGE,"E1.3"),sQuery(id+"F0.wireOp",EDGE,"E1.4"),sQuery(id+"F0.wireOp",EDGE,"E1.5"),sQuery(id+"F0.wireOp",EDGE,"E1.6"),sQuery(id+"F0.wireOp",EDGE,"E1.7"),sQuery(id+"F0.wireOp",EDGE,"E1.8"),sQuery(id+"F0.wireOp",EDGE,"E1.9"),sQuery(id+"F0.wireOp",EDGE,"E1.10"),sQuery(id+"F0.wireOp",EDGE,"E2"),sQuery(id+"F0.wireOp",EDGE,"E3.2.0"),sQuery(id+"F0.wireOp",EDGE,"E3.3.0"),sQuery(id+"F0.wireOp",EDGE,"E3.4.0"),sQuery(id+"F0.wireOp",EDGE,"E3.5.0"),sQuery(id+"F0.wireOp",EDGE,"E3.6.0"),sQuery(id+"F0.wireOp",EDGE,"E3.7.0"),sQuery(id+"F0.wireOp",EDGE,"E3.8.0"),sQuery(id+"F0.wireOp",EDGE,"E3.9.0"),sQuery(id+"F0.wireOp",EDGE,"E3.10.0"),sQuery(id+"F0.wireOp",EDGE,"E4"),sQuery(id+"F0.wireOp",EDGE,"E5"),sQuery(id+"F0.wireOp",EDGE,"E6"),sQuery(id+"F0.wireOp",EDGE,"E7"),sQuery(id+"F0.wireOp",EDGE,"E8"),sQuery(id+"F0.wireOp",EDGE,"E9"),sQuery(id+"F0.wireOp",EDGE,"E10"),sQuery(id+"F0.wireOp",EDGE,"E11"),sQuery(id+"F0.wireOp",EDGE,"E12"),sQuery(id+"F0.wireOp",EDGE,"E13"),sQuery(id+"F0.wireOp",EDGE,"E14"),sQuery(id+"F0.wireOp",EDGE,"E15"),subQ0,sQuery(id+"F0.wireOp",EDGE,"E17"),sQuery(id+"F0.wireOp",EDGE,"E18.MirrorCS"),sQuery(id+"F0.wireOp",EDGE,"E19.MirrorCS"),sQuery(id+"F0.wireOp",EDGE,"E20.MirrorCS"),sQuery(id+"F0.wireOp",EDGE,"E21.MirrorCS"),sQuery(id+"F0.wireOp",EDGE,"E22.MirrorCS"),sQuery(id+"F0.wireOp",EDGE,"E23.MirrorCS"),sQuery(id+"F0.wireOp",EDGE,"E24.MirrorCS"),sQuery(id+"F0.wireOp",EDGE,"E25.MirrorCS"),sQuery(id+"F0.wireOp",EDGE,"E26.MirrorCS"),sQuery(id+"F0.wireOp",EDGE,"E27.MirrorCS"),sQuery(id+"F0.wireOp",EDGE,"E28.MirrorCS"),sQuery(id+"F0.wireOp",EDGE,"E29.MirrorCS"),sQuery(id+"F0.wireOp",EDGE,"E30.MirrorCS"),sQuery(id+"F0.wireOp",EDGE,"E31.MirrorCS")])],"isStart":false})],"blendedInto":[makeQuery(id+"F1.opExtrude","CAP_FACE",FACE,{"disambiguationData":[OSD([sQuery(id+"F0.wireOp",EDGE,"E0"),sQuery(id+"F0.wireOp",EDGE,"E1.0"),sQuery(id+"F0.wireOp",EDGE,"E1.1"),sQuery(id+"F0.wireOp",EDGE,"E1.2"),sQuery(id+"F0.wireOp",EDGE,"E1.3"),sQuery(id+"F0.wireOp",EDGE,"E1.4"),sQuery(id+"F0.wireOp",EDGE,"E1.5"),sQuery(id+"F0.wireOp",EDGE,"E1.6"),sQuery(id+"F0.wireOp",EDGE,"E1.7"),sQuery(id+"F0.wireOp",EDGE,"E1.8"),sQuery(id+"F0.wireOp",EDGE,"E1.9"),sQuery(id+"F0.wireOp",EDGE,"E1.10"),sQuery(id+"F0.wireOp",EDGE,"E2"),sQuery(id+"F0.wireOp",EDGE,"E3.2.0"),sQuery(id+"F0.wireOp",EDGE,"E3.3.0"),sQuery(id+"F0.wireOp",EDGE,"E3.4.0"),sQuery(id+"F0.wireOp",EDGE,"E3.5.0"),sQuery(id+"F0.wireOp",EDGE,"E3.6.0"),sQuery(id+"F0.wireOp",EDGE,"E3.7.0"),sQuery(id+"F0.wireOp",EDGE,"E3.8.0"),sQuery(id+"F0.wireOp",EDGE,"E3.9.0"),sQuery(id+"F0.wireOp",EDGE,"E3.10.0"),sQuery(id+"F0.wireOp",EDGE,"E4"),sQuery(id+"F0.wireOp",EDGE,"E5"),sQuery(id+"F0.wireOp",EDGE,"E6"),sQuery(id+"F0.wireOp",EDGE,"E7"),sQuery(id+"F0.wireOp",EDGE,"E8"),sQuery(id+"F0.wireOp",EDGE,"E9"),sQuery(id+"F0.wireOp",EDGE,"E10"),sQuery(id+"F0.wireOp",EDGE,"E11"),sQuery(id+"F0.wireOp",EDGE,"E12"),sQuery(id+"F0.wireOp",EDGE,"E13"),sQuery(id+"F0.wireOp",EDGE,"E14"),sQuery(id+"F0.wireOp",EDGE,"E15"),subQ0,sQuery(id+"F0.wireOp",EDGE,"E17"),sQuery(id+"F0.wireOp",EDGE,"E18.MirrorCS"),sQuery(id+"F0.wireOp",EDGE,"E19.MirrorCS"),sQuery(id+"F0.wireOp",EDGE,"E20.MirrorCS"),sQuery(id+"F0.wireOp",EDGE,"E21.MirrorCS"),sQuery(id+"F0.wireOp",EDGE,"E22.MirrorCS"),sQuery(id+"F0.wireOp",EDGE,"E23.MirrorCS"),sQuery(id+"F0.wireOp",EDGE,"E24.MirrorCS"),sQuery(id+"F0.wireOp",EDGE,"E25.MirrorCS"),sQuery(id+"F0.wireOp",EDGE,"E26.MirrorCS"),sQuery(id+"F0.wireOp",EDGE,"E27.MirrorCS"),sQuery(id+"F0.wireOp",EDGE,"E28.MirrorCS"),sQuery(id+"F0.wireOp",EDGE,"E29.MirrorCS"),sQuery(id+"F0.wireOp",EDGE,"E30.MirrorCS"),sQuery(id+"F0.wireOp",EDGE,"E31.MirrorCS")])],"isStart":false})]}),makeQuery(id+"F6.opExtrude","CAP_EDGE",EDGE,{"disambiguationData":[OSD([sQuery(id+"F5.wireOp",EDGE,"E82.0")])],"isStart":true})]});}
            fillet(context, id + "F7", {"entities" : qUnion([Q0, Q1, Q2, Q3, Q4, Q5, Q6, Q7, Q8, Q9, Q10, Q11, Q12, Q13, Q14, Q15, Q16, Q17, Q18, Q19, Q20, Q21, Q22, Q23, Q24, Q25, Q26, Q27, Q28, Q29, Q30, Q31, Q32, Q33, Q34, Q35, Q36, Q37, Q38, Q39, Q40, Q41, Q42, Q43, Q44, Q45, Q46, Q47, Q48, Q49, Q50, Q51, Q52, Q53, Q54, Q55, Q56, Q57, Q58, Q59, Q60, Q61, Q62, Q63, Q64, Q65, Q66, Q67, Q68, Q69, Q70, Q71, Q72, Q73, Q74, Q75, Q76, Q77]), "radius" : 0.2 * mm, "tangentPropagation" : true, "allowEdgeOverflow" : false});
        }
        {
            var Q0;
            Q0=makeQuery(id+"F6.boolean.opBoolean","COPY",EDGE,{"derivedFrom":makeQuery(id+"F6.opExtrude","SWEPT_EDGE",EDGE,{"disambiguationData":[OSD([sQuery(id+"F5.wireOp",EDGE,"E42.0"),sQuery(id+"F5.wireOp",EDGE,"E66.0")])]})});
            var Q1;
            Q1=makeQuery(id+"F6.boolean.opBoolean","COPY",EDGE,{"derivedFrom":makeQuery(id+"F6.opExtrude","SWEPT_EDGE",EDGE,{"disambiguationData":[OSD([sQuery(id+"F5.wireOp",EDGE,"E39.0"),sQuery(id+"F5.wireOp",EDGE,"E63.0")])]})});
            var Q2;
            Q2=makeQuery(id+"F6.boolean.opBoolean","COPY",EDGE,{"derivedFrom":makeQuery(id+"F6.opExtrude","SWEPT_EDGE",EDGE,{"disambiguationData":[OSD([sQuery(id+"F5.wireOp",EDGE,"E64.0"),sQuery(id+"F5.wireOp",EDGE,"E73.0")])]})});
            var Q3;
            Q3=makeQuery(id+"F6.boolean.opBoolean","COPY",EDGE,{"derivedFrom":makeQuery(id+"F6.opExtrude","SWEPT_EDGE",EDGE,{"disambiguationData":[OSD([sQuery(id+"F5.wireOp",EDGE,"E65.0"),sQuery(id+"F5.wireOp",EDGE,"E72.0")])]})});
            var Q4;
            Q4=makeQuery(id+"F6.boolean.opBoolean","COPY",EDGE,{"derivedFrom":makeQuery(id+"F6.opExtrude","SWEPT_EDGE",EDGE,{"disambiguationData":[OSD([sQuery(id+"F5.wireOp",EDGE,"E76.0"),sQuery(id+"F5.wireOp",EDGE,"E83.0.1"),sQuery(id+"F5.wireOp",EDGE,"E83.0.0")])]})});
            var Q5;
            Q5=makeQuery(id+"F6.boolean.opBoolean","COPY",EDGE,{"derivedFrom":makeQuery(id+"F6.opExtrude","SWEPT_EDGE",EDGE,{"disambiguationData":[OSD([sQuery(id+"F5.wireOp",EDGE,"E74.0"),sQuery(id+"F5.wireOp",EDGE,"E76.0")])]})});
            var Q6;
            Q6=makeQuery(id+"F6.boolean.opBoolean","COPY",EDGE,{"derivedFrom":makeQuery(id+"F6.opExtrude","SWEPT_EDGE",EDGE,{"disambiguationData":[OSD([sQuery(id+"F5.wireOp",EDGE,"E63.0"),sQuery(id+"F5.wireOp",EDGE,"E74.0")])]})});
            var Q7;
            Q7=makeQuery(id+"F6.boolean.opBoolean","COPY",EDGE,{"derivedFrom":makeQuery(id+"F6.opExtrude","SWEPT_EDGE",EDGE,{"disambiguationData":[OSD([sQuery(id+"F5.wireOp",EDGE,"E64.0"),sQuery(id+"F5.wireOp",EDGE,"E78.0")])]})});
            var Q8;
            Q8=makeQuery(id+"F6.boolean.opBoolean","COPY",EDGE,{"derivedFrom":makeQuery(id+"F6.opExtrude","SWEPT_EDGE",EDGE,{"disambiguationData":[OSD([sQuery(id+"F5.wireOp",EDGE,"E77.0"),sQuery(id+"F5.wireOp",EDGE,"E83.0.3"),sQuery(id+"F5.wireOp",EDGE,"E83.0.0")])]})});
            var Q9;
            Q9=makeQuery(id+"F6.boolean.opBoolean","COPY",EDGE,{"derivedFrom":makeQuery(id+"F6.opExtrude","SWEPT_EDGE",EDGE,{"disambiguationData":[OSD([sQuery(id+"F5.wireOp",EDGE,"E77.0"),sQuery(id+"F5.wireOp",EDGE,"E78.0")])]})});
            var Q10;
            Q10=makeQuery(id+"F6.boolean.opBoolean","COPY",EDGE,{"derivedFrom":makeQuery(id+"F6.opExtrude","SWEPT_EDGE",EDGE,{"disambiguationData":[OSD([sQuery(id+"F5.wireOp",EDGE,"E72.0"),sQuery(id+"F5.wireOp",EDGE,"E79.0")])]})});
            var Q11;
            Q11=makeQuery(id+"F6.boolean.opBoolean","COPY",EDGE,{"derivedFrom":makeQuery(id+"F6.opExtrude","SWEPT_EDGE",EDGE,{"disambiguationData":[OSD([sQuery(id+"F5.wireOp",EDGE,"E81.0"),sQuery(id+"F5.wireOp",EDGE,"E80.0")])]})});
            var Q12;
            Q12=makeQuery(id+"F6.boolean.opBoolean","COPY",EDGE,{"derivedFrom":makeQuery(id+"F6.opExtrude","SWEPT_EDGE",EDGE,{"disambiguationData":[OSD([sQuery(id+"F5.wireOp",EDGE,"E80.0"),sQuery(id+"F5.wireOp",EDGE,"E79.0")])]})});
            var Q13;
            Q13=makeQuery(id+"F6.boolean.opBoolean","COPY",EDGE,{"derivedFrom":makeQuery(id+"F6.opExtrude","SWEPT_EDGE",EDGE,{"disambiguationData":[OSD([sQuery(id+"F5.wireOp",EDGE,"E73.0"),sQuery(id+"F5.wireOp",EDGE,"E84.0")])]})});
            var Q14;
            Q14=makeQuery(id+"F6.boolean.opBoolean","COPY",EDGE,{"derivedFrom":makeQuery(id+"F6.opExtrude","SWEPT_EDGE",EDGE,{"disambiguationData":[OSD([sQuery(id+"F5.wireOp",EDGE,"E82.0"),sQuery(id+"F5.wireOp",EDGE,"E81.0")])]})});
            var Q15;
            Q15=makeQuery(id+"F6.boolean.opBoolean","COPY",EDGE,{"derivedFrom":makeQuery(id+"F6.opExtrude","SWEPT_EDGE",EDGE,{"disambiguationData":[OSD([sQuery(id+"F5.wireOp",EDGE,"E84.0"),sQuery(id+"F5.wireOp",EDGE,"E82.0")])]})});
            var Q16;
            Q16=makeQuery(id+"F6.boolean.opBoolean","COPY",EDGE,{"derivedFrom":makeQuery(id+"F6.opExtrude","SWEPT_EDGE",EDGE,{"disambiguationData":[OSD([sQuery(id+"F5.wireOp",EDGE,"E70.0"),sQuery(id+"F5.wireOp",EDGE,"E71.0")])]})});
            var Q17;
            Q17=makeQuery(id+"F6.boolean.opBoolean","COPY",EDGE,{"derivedFrom":makeQuery(id+"F6.opExtrude","SWEPT_EDGE",EDGE,{"disambiguationData":[OSD([sQuery(id+"F5.wireOp",EDGE,"E69.0"),sQuery(id+"F5.wireOp",EDGE,"E71.0")])]})});
            var Q18;
            Q18=makeQuery(id+"F6.boolean.opBoolean","COPY",EDGE,{"derivedFrom":makeQuery(id+"F6.opExtrude","SWEPT_EDGE",EDGE,{"disambiguationData":[OSD([sQuery(id+"F5.wireOp",EDGE,"E68.0"),sQuery(id+"F5.wireOp",EDGE,"E69.0")])]})});
            var Q19;
            Q19=makeQuery(id+"F6.boolean.opBoolean","COPY",EDGE,{"derivedFrom":makeQuery(id+"F6.opExtrude","SWEPT_EDGE",EDGE,{"disambiguationData":[OSD([sQuery(id+"F5.wireOp",EDGE,"E67.0"),sQuery(id+"F5.wireOp",EDGE,"E68.0")])]})});
            var Q20;
            Q20=makeQuery(id+"F6.boolean.opBoolean","COPY",EDGE,{"derivedFrom":makeQuery(id+"F6.opExtrude","SWEPT_EDGE",EDGE,{"disambiguationData":[OSD([sQuery(id+"F5.wireOp",EDGE,"E66.0"),sQuery(id+"F5.wireOp",EDGE,"E67.0")])]})});
            var Q21;
            Q21=makeQuery(id+"F6.boolean.opBoolean","COPY",EDGE,{"derivedFrom":makeQuery(id+"F6.opExtrude","SWEPT_EDGE",EDGE,{"disambiguationData":[OSD([sQuery(id+"F5.wireOp",EDGE,"E41.0"),sQuery(id+"F5.wireOp",EDGE,"E42.0")])]})});
            var Q22;
            Q22=makeQuery(id+"F6.boolean.opBoolean","COPY",EDGE,{"derivedFrom":makeQuery(id+"F6.opExtrude","SWEPT_EDGE",EDGE,{"disambiguationData":[OSD([sQuery(id+"F5.wireOp",EDGE,"E39.0"),sQuery(id+"F5.wireOp",EDGE,"E40.0")])]})});
            var Q23;
            Q23=makeQuery(id+"F6.boolean.opBoolean","COPY",EDGE,{"derivedFrom":makeQuery(id+"F6.opExtrude","SWEPT_EDGE",EDGE,{"disambiguationData":[OSD([sQuery(id+"F5.wireOp",EDGE,"E41.0"),sQuery(id+"F5.wireOp",EDGE,"E43.0")])]})});
            var Q24;
            Q24=makeQuery(id+"F6.boolean.opBoolean","COPY",EDGE,{"derivedFrom":makeQuery(id+"F6.opExtrude","SWEPT_EDGE",EDGE,{"disambiguationData":[OSD([sQuery(id+"F5.wireOp",EDGE,"E43.0"),sQuery(id+"F5.wireOp",EDGE,"E44.0")])]})});
            var Q25;
            Q25=makeQuery(id+"F6.boolean.opBoolean","COPY",EDGE,{"derivedFrom":makeQuery(id+"F6.opExtrude","SWEPT_EDGE",EDGE,{"disambiguationData":[OSD([sQuery(id+"F5.wireOp",EDGE,"E38.0"),sQuery(id+"F5.wireOp",EDGE,"E40.0")])]})});
            var Q26;
            Q26=makeQuery(id+"F6.boolean.opBoolean","COPY",EDGE,{"derivedFrom":makeQuery(id+"F6.opExtrude","SWEPT_EDGE",EDGE,{"disambiguationData":[OSD([sQuery(id+"F5.wireOp",EDGE,"E37.0"),sQuery(id+"F5.wireOp",EDGE,"E38.0")])]})});
            fillet(context, id + "F8", {"entities" : qUnion([Q0, Q1, Q2, Q3, Q4, Q5, Q6, Q7, Q8, Q9, Q10, Q11, Q12, Q13, Q14, Q15, Q16, Q17, Q18, Q19, Q20, Q21, Q22, Q23, Q24, Q25, Q26]), "radius" : 0.1 * mm, "tangentPropagation" : true, "allowEdgeOverflow" : false});
        }
    });
